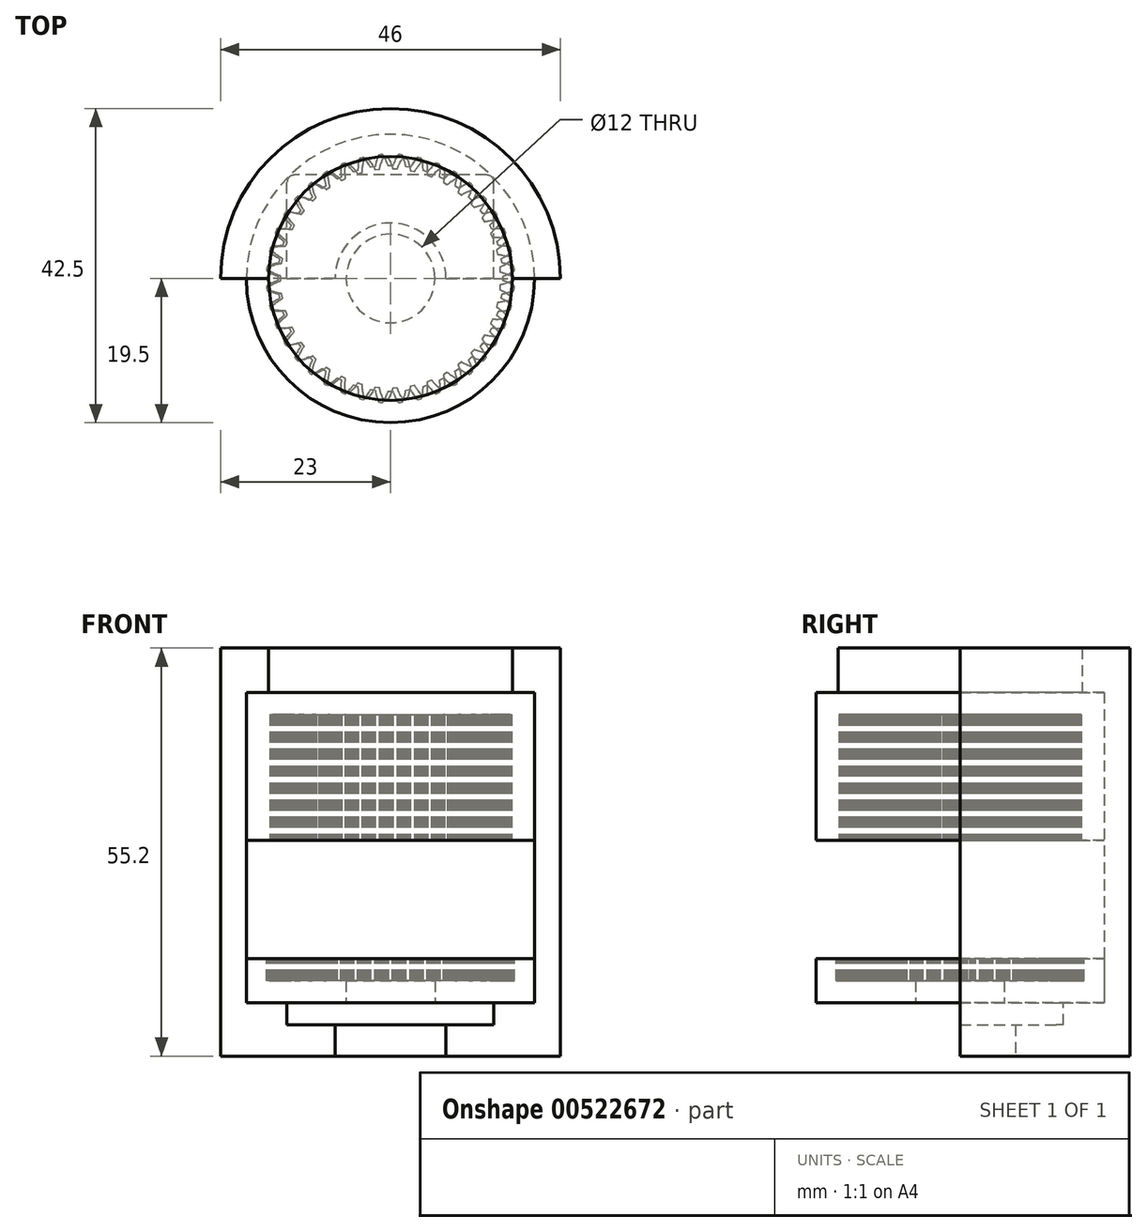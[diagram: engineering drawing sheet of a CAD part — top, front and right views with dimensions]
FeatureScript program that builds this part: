
annotation { "Feature Type Name" : "Feature", "Feature Type Description" : "" }
export const myFeature = defineFeature(function(context is Context, id is Id, definition is map)
    precondition{}
    {
        {
            var Q0;
            Q0=qCreatedBy(makeId("Top.planeOp"),FACE);
            var sketch = newSketch(context, id + "F0", { "sketchPlane" : qUnion([Q0])});
            skLineSegment(sketch, "E0", {"start": v(-16.75, 1.06) * mm, "end": v(-16.75, 1.32) * mm});
            skLineSegment(sketch, "E1", {"start": v(-16.75, 1.32) * mm, "end": v(-16.7, 1.58) * mm});
            skLineSegment(sketch, "E2", {"start": v(-16.7, 1.58) * mm, "end": v(-16.66, 1.63) * mm});
            skLineSegment(sketch, "E3", {"start": v(-16.66, 1.63) * mm, "end": v(-16.6, 1.66) * mm});
            skLineSegment(sketch, "E4", {"start": v(-16.6, 1.66) * mm, "end": v(-16.3, 1.78) * mm});
            skLineSegment(sketch, "E5", {"start": v(-16.3, 1.78) * mm, "end": v(-16.24, 1.8) * mm});
            skLineSegment(sketch, "E6", {"start": v(-16.24, 1.8) * mm, "end": v(-16.22, 1.8) * mm});
            skLineSegment(sketch, "E7", {"start": v(-16.22, 1.8) * mm, "end": v(-16.03, 1.87) * mm});
            skLineSegment(sketch, "E8", {"start": v(-16.03, 1.87) * mm, "end": v(-16.03, 1.87) * mm});
            skLineSegment(sketch, "E9", {"start": v(-16.03, 1.87) * mm, "end": v(-16, 1.87) * mm});
            skLineSegment(sketch, "E10", {"start": v(-16, 1.87) * mm, "end": v(-15.79, 1.94) * mm});
            skLineSegment(sketch, "E11", {"start": v(-15.79, 1.94) * mm, "end": v(-15.77, 1.94) * mm});
            skLineSegment(sketch, "E12", {"start": v(-15.77, 1.94) * mm, "end": v(-15.6, 1.99) * mm});
            skLineSegment(sketch, "E13", {"start": v(-15.6, 1.99) * mm, "end": v(-15.53, 2) * mm});
            skLineSegment(sketch, "E14", {"start": v(-15.53, 2) * mm, "end": v(-15.42, 2.02) * mm});
            skLineSegment(sketch, "E15", {"start": v(-15.42, 2.02) * mm, "end": v(-15.32, 2.04) * mm});
            skLineSegment(sketch, "E16", {"start": v(-15.32, 2.04) * mm, "end": v(-15.2, 2.06) * mm});
            skLineSegment(sketch, "E17", {"start": v(-15.2, 2.06) * mm, "end": v(-15.16, 2.07) * mm});
            skLineSegment(sketch, "E18", {"start": v(-15.16, 2.07) * mm, "end": v(-15.14, 2.08) * mm});
            skLineSegment(sketch, "E19", {"start": v(-15.14, 2.08) * mm, "end": v(-15.12, 2.1) * mm});
            skLineSegment(sketch, "E20", {"start": v(-15.12, 2.1) * mm, "end": v(-15.1, 2.1) * mm});
            skLineSegment(sketch, "E21", {"start": v(-15.1, 2.1) * mm, "end": v(-15.02, 2.66) * mm});
            skLineSegment(sketch, "E22", {"start": v(-15.02, 2.66) * mm, "end": v(-15.03, 2.68) * mm});
            skLineSegment(sketch, "E23", {"start": v(-15.03, 2.68) * mm, "end": v(-15.04, 2.7) * mm});
            skLineSegment(sketch, "E24", {"start": v(-15.04, 2.7) * mm, "end": v(-15.06, 2.71) * mm});
            skLineSegment(sketch, "E25", {"start": v(-15.06, 2.71) * mm, "end": v(-15.1, 2.74) * mm});
            skLineSegment(sketch, "E26", {"start": v(-15.1, 2.74) * mm, "end": v(-15.2, 2.8) * mm});
            skLineSegment(sketch, "E27", {"start": v(-15.2, 2.8) * mm, "end": v(-15.29, 2.84) * mm});
            skLineSegment(sketch, "E28", {"start": v(-15.29, 2.84) * mm, "end": v(-15.39, 2.9) * mm});
            skLineSegment(sketch, "E29", {"start": v(-15.39, 2.9) * mm, "end": v(-15.44, 2.93) * mm});
            skLineSegment(sketch, "E30", {"start": v(-15.44, 2.93) * mm, "end": v(-15.6, 3.03) * mm});
            skLineSegment(sketch, "E31", {"start": v(-15.6, 3.03) * mm, "end": v(-15.61, 3.04) * mm});
            skLineSegment(sketch, "E32", {"start": v(-15.61, 3.04) * mm, "end": v(-15.8, 3.16) * mm});
            skLineSegment(sketch, "E33", {"start": v(-15.8, 3.16) * mm, "end": v(-15.82, 3.18) * mm});
            skLineSegment(sketch, "E34", {"start": v(-15.82, 3.18) * mm, "end": v(-15.82, 3.18) * mm});
            skLineSegment(sketch, "E35", {"start": v(-15.82, 3.18) * mm, "end": v(-15.98, 3.3) * mm});
            skLineSegment(sketch, "E36", {"start": v(-15.98, 3.3) * mm, "end": v(-16, 3.3) * mm});
            skLineSegment(sketch, "E37", {"start": v(-16, 3.3) * mm, "end": v(-16.05, 3.35) * mm});
            skLineSegment(sketch, "E38", {"start": v(-16.05, 3.35) * mm, "end": v(-16.3, 3.54) * mm});
            skLineSegment(sketch, "E39", {"start": v(-16.3, 3.54) * mm, "end": v(-16.35, 3.6) * mm});
            skLineSegment(sketch, "E40", {"start": v(-16.35, 3.6) * mm, "end": v(-16.38, 3.66) * mm});
            skLineSegment(sketch, "E41", {"start": v(-16.38, 3.66) * mm, "end": v(-16.34, 3.92) * mm});
            skLineSegment(sketch, "E42", {"start": v(-16.34, 3.92) * mm, "end": v(-16.26, 4.17) * mm});
            skLineSegment(sketch, "E43", {"start": v(-16.26, 4.17) * mm, "end": v(-16.2, 4.22) * mm});
            skLineSegment(sketch, "E44", {"start": v(-16.2, 4.22) * mm, "end": v(-16.13, 4.24) * mm});
            skLineSegment(sketch, "E45", {"start": v(-16.13, 4.24) * mm, "end": v(-15.82, 4.3) * mm});
            skLineSegment(sketch, "E46", {"start": v(-15.82, 4.3) * mm, "end": v(-15.76, 4.32) * mm});
            skLineSegment(sketch, "E47", {"start": v(-15.76, 4.32) * mm, "end": v(-15.74, 4.32) * mm});
            skLineSegment(sketch, "E48", {"start": v(-15.74, 4.32) * mm, "end": v(-15.54, 4.35) * mm});
            skLineSegment(sketch, "E49", {"start": v(-15.54, 4.35) * mm, "end": v(-15.54, 4.35) * mm});
            skLineSegment(sketch, "E50", {"start": v(-15.54, 4.35) * mm, "end": v(-15.51, 4.36) * mm});
            skLineSegment(sketch, "E51", {"start": v(-15.51, 4.36) * mm, "end": v(-15.3, 4.38) * mm});
            skLineSegment(sketch, "E52", {"start": v(-15.3, 4.38) * mm, "end": v(-15.27, 4.38) * mm});
            skLineSegment(sketch, "E53", {"start": v(-15.27, 4.38) * mm, "end": v(-15.09, 4.4) * mm});
            skLineSegment(sketch, "E54", {"start": v(-15.09, 4.4) * mm, "end": v(-15.03, 4.4) * mm});
            skLineSegment(sketch, "E55", {"start": v(-15.03, 4.4) * mm, "end": v(-14.91, 4.4) * mm});
            skLineSegment(sketch, "E56", {"start": v(-14.91, 4.4) * mm, "end": v(-14.8, 4.41) * mm});
            skLineSegment(sketch, "E57", {"start": v(-14.8, 4.41) * mm, "end": v(-14.7, 4.41) * mm});
            skLineSegment(sketch, "E58", {"start": v(-14.7, 4.41) * mm, "end": v(-14.65, 4.42) * mm});
            skLineSegment(sketch, "E59", {"start": v(-14.65, 4.42) * mm, "end": v(-14.62, 4.43) * mm});
            skLineSegment(sketch, "E60", {"start": v(-14.62, 4.43) * mm, "end": v(-14.6, 4.43) * mm});
            skLineSegment(sketch, "E61", {"start": v(-14.6, 4.43) * mm, "end": v(-14.6, 4.44) * mm});
            skLineSegment(sketch, "E62", {"start": v(-14.6, 4.44) * mm, "end": v(-14.42, 4.98) * mm});
            skLineSegment(sketch, "E63", {"start": v(-14.42, 4.98) * mm, "end": v(-14.42, 5) * mm});
            skLineSegment(sketch, "E64", {"start": v(-14.42, 5) * mm, "end": v(-14.43, 5.02) * mm});
            skLineSegment(sketch, "E65", {"start": v(-14.43, 5.02) * mm, "end": v(-14.45, 5.04) * mm});
            skLineSegment(sketch, "E66", {"start": v(-14.45, 5.04) * mm, "end": v(-14.48, 5.07) * mm});
            skLineSegment(sketch, "E67", {"start": v(-14.48, 5.07) * mm, "end": v(-14.57, 5.13) * mm});
            skLineSegment(sketch, "E68", {"start": v(-14.57, 5.13) * mm, "end": v(-14.65, 5.2) * mm});
            skLineSegment(sketch, "E69", {"start": v(-14.65, 5.2) * mm, "end": v(-14.75, 5.27) * mm});
            skLineSegment(sketch, "E70", {"start": v(-14.75, 5.27) * mm, "end": v(-14.8, 5.3) * mm});
            skLineSegment(sketch, "E71", {"start": v(-14.8, 5.3) * mm, "end": v(-14.93, 5.43) * mm});
            skLineSegment(sketch, "E72", {"start": v(-14.93, 5.43) * mm, "end": v(-14.95, 5.44) * mm});
            skLineSegment(sketch, "E73", {"start": v(-14.95, 5.44) * mm, "end": v(-15.11, 5.6) * mm});
            skLineSegment(sketch, "E74", {"start": v(-15.11, 5.6) * mm, "end": v(-15.13, 5.61) * mm});
            skLineSegment(sketch, "E75", {"start": v(-15.13, 5.61) * mm, "end": v(-15.13, 5.61) * mm});
            skLineSegment(sketch, "E76", {"start": v(-15.13, 5.61) * mm, "end": v(-15.27, 5.76) * mm});
            skLineSegment(sketch, "E77", {"start": v(-15.27, 5.76) * mm, "end": v(-15.29, 5.77) * mm});
            skLineSegment(sketch, "E78", {"start": v(-15.29, 5.77) * mm, "end": v(-15.33, 5.82) * mm});
            skLineSegment(sketch, "E79", {"start": v(-15.33, 5.82) * mm, "end": v(-15.54, 6.05) * mm});
            skLineSegment(sketch, "E80", {"start": v(-15.54, 6.05) * mm, "end": v(-15.58, 6.11) * mm});
            skLineSegment(sketch, "E81", {"start": v(-15.58, 6.11) * mm, "end": v(-15.6, 6.18) * mm});
            skLineSegment(sketch, "E82", {"start": v(-15.6, 6.18) * mm, "end": v(-15.52, 6.43) * mm});
            skLineSegment(sketch, "E83", {"start": v(-15.52, 6.43) * mm, "end": v(-15.4, 6.66) * mm});
            skLineSegment(sketch, "E84", {"start": v(-15.4, 6.66) * mm, "end": v(-15.34, 6.7) * mm});
            skLineSegment(sketch, "E85", {"start": v(-15.34, 6.7) * mm, "end": v(-15.27, 6.71) * mm});
            skLineSegment(sketch, "E86", {"start": v(-15.27, 6.71) * mm, "end": v(-14.95, 6.73) * mm});
            skLineSegment(sketch, "E87", {"start": v(-14.95, 6.73) * mm, "end": v(-14.89, 6.73) * mm});
            skLineSegment(sketch, "E88", {"start": v(-14.89, 6.73) * mm, "end": v(-14.87, 6.73) * mm});
            skLineSegment(sketch, "E89", {"start": v(-14.87, 6.73) * mm, "end": v(-14.67, 6.73) * mm});
            skLineSegment(sketch, "E90", {"start": v(-14.67, 6.73) * mm, "end": v(-14.66, 6.73) * mm});
            skLineSegment(sketch, "E91", {"start": v(-14.66, 6.73) * mm, "end": v(-14.64, 6.73) * mm});
            skLineSegment(sketch, "E92", {"start": v(-14.64, 6.73) * mm, "end": v(-14.42, 6.72) * mm});
            skLineSegment(sketch, "E93", {"start": v(-14.42, 6.72) * mm, "end": v(-14.4, 6.72) * mm});
            skLineSegment(sketch, "E94", {"start": v(-14.4, 6.72) * mm, "end": v(-14.22, 6.7) * mm});
            skLineSegment(sketch, "E95", {"start": v(-14.22, 6.7) * mm, "end": v(-14.15, 6.7) * mm});
            skLineSegment(sketch, "E96", {"start": v(-14.15, 6.7) * mm, "end": v(-14.04, 6.69) * mm});
            skLineSegment(sketch, "E97", {"start": v(-14.04, 6.69) * mm, "end": v(-13.93, 6.67) * mm});
            skLineSegment(sketch, "E98", {"start": v(-13.93, 6.67) * mm, "end": v(-13.83, 6.66) * mm});
            skLineSegment(sketch, "E99", {"start": v(-13.83, 6.66) * mm, "end": v(-13.78, 6.66) * mm});
            skLineSegment(sketch, "E100", {"start": v(-13.78, 6.66) * mm, "end": v(-13.75, 6.66) * mm});
            skLineSegment(sketch, "E101", {"start": v(-13.75, 6.66) * mm, "end": v(-13.73, 6.66) * mm});
            skLineSegment(sketch, "E102", {"start": v(-13.73, 6.66) * mm, "end": v(-13.72, 6.67) * mm});
            skLineSegment(sketch, "E103", {"start": v(-13.72, 6.67) * mm, "end": v(-13.46, 7.17) * mm});
            skLineSegment(sketch, "E104", {"start": v(-13.46, 7.17) * mm, "end": v(-13.46, 7.2) * mm});
            skLineSegment(sketch, "E105", {"start": v(-13.46, 7.2) * mm, "end": v(-13.47, 7.21) * mm});
            skLineSegment(sketch, "E106", {"start": v(-13.47, 7.21) * mm, "end": v(-13.48, 7.23) * mm});
            skLineSegment(sketch, "E107", {"start": v(-13.48, 7.23) * mm, "end": v(-13.51, 7.27) * mm});
            skLineSegment(sketch, "E108", {"start": v(-13.51, 7.27) * mm, "end": v(-13.6, 7.35) * mm});
            skLineSegment(sketch, "E109", {"start": v(-13.6, 7.35) * mm, "end": v(-13.66, 7.43) * mm});
            skLineSegment(sketch, "E110", {"start": v(-13.66, 7.43) * mm, "end": v(-13.74, 7.51) * mm});
            skLineSegment(sketch, "E111", {"start": v(-13.74, 7.51) * mm, "end": v(-13.78, 7.56) * mm});
            skLineSegment(sketch, "E112", {"start": v(-13.78, 7.56) * mm, "end": v(-13.9, 7.7) * mm});
            skLineSegment(sketch, "E113", {"start": v(-13.9, 7.7) * mm, "end": v(-13.91, 7.71) * mm});
            skLineSegment(sketch, "E114", {"start": v(-13.91, 7.71) * mm, "end": v(-14.05, 7.89) * mm});
            skLineSegment(sketch, "E115", {"start": v(-14.05, 7.89) * mm, "end": v(-14.06, 7.9) * mm});
            skLineSegment(sketch, "E116", {"start": v(-14.06, 7.9) * mm, "end": v(-14.07, 7.91) * mm});
            skLineSegment(sketch, "E117", {"start": v(-14.07, 7.91) * mm, "end": v(-14.18, 8.08) * mm});
            skLineSegment(sketch, "E118", {"start": v(-14.18, 8.08) * mm, "end": v(-14.2, 8.1) * mm});
            skLineSegment(sketch, "E119", {"start": v(-14.2, 8.1) * mm, "end": v(-14.23, 8.14) * mm});
            skLineSegment(sketch, "E120", {"start": v(-14.23, 8.14) * mm, "end": v(-14.4, 8.4) * mm});
            skLineSegment(sketch, "E121", {"start": v(-14.4, 8.4) * mm, "end": v(-14.44, 8.47) * mm});
            skLineSegment(sketch, "E122", {"start": v(-14.44, 8.47) * mm, "end": v(-14.44, 8.54) * mm});
            skLineSegment(sketch, "E123", {"start": v(-14.44, 8.54) * mm, "end": v(-14.32, 8.78) * mm});
            skLineSegment(sketch, "E124", {"start": v(-14.32, 8.78) * mm, "end": v(-14.17, 9) * mm});
            skLineSegment(sketch, "E125", {"start": v(-14.17, 9) * mm, "end": v(-14.1, 9.02) * mm});
            skLineSegment(sketch, "E126", {"start": v(-14.1, 9.02) * mm, "end": v(-14.03, 9.02) * mm});
            skLineSegment(sketch, "E127", {"start": v(-14.03, 9.02) * mm, "end": v(-13.72, 8.98) * mm});
            skLineSegment(sketch, "E128", {"start": v(-13.72, 8.98) * mm, "end": v(-13.65, 8.97) * mm});
            skLineSegment(sketch, "E129", {"start": v(-13.65, 8.97) * mm, "end": v(-13.63, 8.97) * mm});
            skLineSegment(sketch, "E130", {"start": v(-13.63, 8.97) * mm, "end": v(-13.44, 8.94) * mm});
            skLineSegment(sketch, "E131", {"start": v(-13.44, 8.94) * mm, "end": v(-13.43, 8.94) * mm});
            skLineSegment(sketch, "E132", {"start": v(-13.43, 8.94) * mm, "end": v(-13.4, 8.94) * mm});
            skLineSegment(sketch, "E133", {"start": v(-13.4, 8.94) * mm, "end": v(-13.19, 8.9) * mm});
            skLineSegment(sketch, "E134", {"start": v(-13.19, 8.9) * mm, "end": v(-13.17, 8.89) * mm});
            skLineSegment(sketch, "E135", {"start": v(-13.17, 8.89) * mm, "end": v(-13, 8.85) * mm});
            skLineSegment(sketch, "E136", {"start": v(-13, 8.85) * mm, "end": v(-12.93, 8.83) * mm});
            skLineSegment(sketch, "E137", {"start": v(-12.93, 8.83) * mm, "end": v(-12.82, 8.8) * mm});
            skLineSegment(sketch, "E138", {"start": v(-12.82, 8.8) * mm, "end": v(-12.72, 8.77) * mm});
            skLineSegment(sketch, "E139", {"start": v(-12.72, 8.77) * mm, "end": v(-12.61, 8.74) * mm});
            skLineSegment(sketch, "E140", {"start": v(-12.61, 8.74) * mm, "end": v(-12.57, 8.73) * mm});
            skLineSegment(sketch, "E141", {"start": v(-12.57, 8.73) * mm, "end": v(-12.54, 8.73) * mm});
            skLineSegment(sketch, "E142", {"start": v(-12.54, 8.73) * mm, "end": v(-12.52, 8.73) * mm});
            skLineSegment(sketch, "E143", {"start": v(-12.52, 8.73) * mm, "end": v(-12.5, 8.74) * mm});
            skLineSegment(sketch, "E144", {"start": v(-12.5, 8.74) * mm, "end": v(-12.17, 9.2) * mm});
            skLineSegment(sketch, "E145", {"start": v(-12.17, 9.2) * mm, "end": v(-12.17, 9.21) * mm});
            skLineSegment(sketch, "E146", {"start": v(-12.17, 9.21) * mm, "end": v(-12.18, 9.23) * mm});
            skLineSegment(sketch, "E147", {"start": v(-12.18, 9.23) * mm, "end": v(-12.19, 9.25) * mm});
            skLineSegment(sketch, "E148", {"start": v(-12.19, 9.25) * mm, "end": v(-12.2, 9.3) * mm});
            skLineSegment(sketch, "E149", {"start": v(-12.2, 9.3) * mm, "end": v(-12.27, 9.39) * mm});
            skLineSegment(sketch, "E150", {"start": v(-12.27, 9.39) * mm, "end": v(-12.33, 9.47) * mm});
            skLineSegment(sketch, "E151", {"start": v(-12.33, 9.47) * mm, "end": v(-12.4, 9.57) * mm});
            skLineSegment(sketch, "E152", {"start": v(-12.4, 9.57) * mm, "end": v(-12.43, 9.62) * mm});
            skLineSegment(sketch, "E153", {"start": v(-12.43, 9.62) * mm, "end": v(-12.52, 9.78) * mm});
            skLineSegment(sketch, "E154", {"start": v(-12.52, 9.78) * mm, "end": v(-12.53, 9.8) * mm});
            skLineSegment(sketch, "E155", {"start": v(-12.53, 9.8) * mm, "end": v(-12.64, 10) * mm});
            skLineSegment(sketch, "E156", {"start": v(-12.64, 10) * mm, "end": v(-12.65, 10.01) * mm});
            skLineSegment(sketch, "E157", {"start": v(-12.65, 10.01) * mm, "end": v(-12.65, 10.02) * mm});
            skLineSegment(sketch, "E158", {"start": v(-12.65, 10.02) * mm, "end": v(-12.74, 10.2) * mm});
            skLineSegment(sketch, "E159", {"start": v(-12.74, 10.2) * mm, "end": v(-12.75, 10.21) * mm});
            skLineSegment(sketch, "E160", {"start": v(-12.75, 10.21) * mm, "end": v(-12.78, 10.27) * mm});
            skLineSegment(sketch, "E161", {"start": v(-12.78, 10.27) * mm, "end": v(-12.9, 10.56) * mm});
            skLineSegment(sketch, "E162", {"start": v(-12.9, 10.56) * mm, "end": v(-12.93, 10.63) * mm});
            skLineSegment(sketch, "E163", {"start": v(-12.93, 10.63) * mm, "end": v(-12.93, 10.7) * mm});
            skLineSegment(sketch, "E164", {"start": v(-12.93, 10.7) * mm, "end": v(-12.77, 10.91) * mm});
            skLineSegment(sketch, "E165", {"start": v(-12.77, 10.91) * mm, "end": v(-12.59, 11.1) * mm});
            skLineSegment(sketch, "E166", {"start": v(-12.59, 11.1) * mm, "end": v(-12.52, 11.11) * mm});
            skLineSegment(sketch, "E167", {"start": v(-12.52, 11.11) * mm, "end": v(-12.44, 11.1) * mm});
            skLineSegment(sketch, "E168", {"start": v(-12.44, 11.1) * mm, "end": v(-12.14, 11.02) * mm});
            skLineSegment(sketch, "E169", {"start": v(-12.14, 11.02) * mm, "end": v(-12.08, 11) * mm});
            skLineSegment(sketch, "E170", {"start": v(-12.08, 11) * mm, "end": v(-12.06, 11) * mm});
            skLineSegment(sketch, "E171", {"start": v(-12.06, 11) * mm, "end": v(-11.87, 10.93) * mm});
            skLineSegment(sketch, "E172", {"start": v(-11.87, 10.93) * mm, "end": v(-11.87, 10.93) * mm});
            skLineSegment(sketch, "E173", {"start": v(-11.87, 10.93) * mm, "end": v(-11.85, 10.92) * mm});
            skLineSegment(sketch, "E174", {"start": v(-11.85, 10.92) * mm, "end": v(-11.63, 10.85) * mm});
            skLineSegment(sketch, "E175", {"start": v(-11.63, 10.85) * mm, "end": v(-11.62, 10.84) * mm});
            skLineSegment(sketch, "E176", {"start": v(-11.62, 10.84) * mm, "end": v(-11.45, 10.77) * mm});
            skLineSegment(sketch, "E177", {"start": v(-11.45, 10.77) * mm, "end": v(-11.4, 10.75) * mm});
            skLineSegment(sketch, "E178", {"start": v(-11.4, 10.75) * mm, "end": v(-11.28, 10.7) * mm});
            skLineSegment(sketch, "E179", {"start": v(-11.28, 10.7) * mm, "end": v(-11.2, 10.65) * mm});
            skLineSegment(sketch, "E180", {"start": v(-11.2, 10.65) * mm, "end": v(-11.1, 10.6) * mm});
            skLineSegment(sketch, "E181", {"start": v(-11.1, 10.6) * mm, "end": v(-11.05, 10.59) * mm});
            skLineSegment(sketch, "E182", {"start": v(-11.05, 10.59) * mm, "end": v(-11.02, 10.58) * mm});
            skLineSegment(sketch, "E183", {"start": v(-11.02, 10.58) * mm, "end": v(-11, 10.58) * mm});
            skLineSegment(sketch, "E184", {"start": v(-11, 10.58) * mm, "end": v(-10.98, 10.58) * mm});
            skLineSegment(sketch, "E185", {"start": v(-10.98, 10.58) * mm, "end": v(-10.58, 10.98) * mm});
            skLineSegment(sketch, "E186", {"start": v(-10.58, 10.98) * mm, "end": v(-10.58, 11) * mm});
            skLineSegment(sketch, "E187", {"start": v(-10.58, 11) * mm, "end": v(-10.58, 11.02) * mm});
            skLineSegment(sketch, "E188", {"start": v(-10.58, 11.02) * mm, "end": v(-10.59, 11.05) * mm});
            skLineSegment(sketch, "E189", {"start": v(-10.59, 11.05) * mm, "end": v(-10.6, 11.1) * mm});
            skLineSegment(sketch, "E190", {"start": v(-10.6, 11.1) * mm, "end": v(-10.65, 11.2) * mm});
            skLineSegment(sketch, "E191", {"start": v(-10.65, 11.2) * mm, "end": v(-10.7, 11.28) * mm});
            skLineSegment(sketch, "E192", {"start": v(-10.7, 11.28) * mm, "end": v(-10.75, 11.4) * mm});
            skLineSegment(sketch, "E193", {"start": v(-10.75, 11.4) * mm, "end": v(-10.77, 11.45) * mm});
            skLineSegment(sketch, "E194", {"start": v(-10.77, 11.45) * mm, "end": v(-10.84, 11.62) * mm});
            skLineSegment(sketch, "E195", {"start": v(-10.84, 11.62) * mm, "end": v(-10.85, 11.63) * mm});
            skLineSegment(sketch, "E196", {"start": v(-10.85, 11.63) * mm, "end": v(-10.92, 11.85) * mm});
            skLineSegment(sketch, "E197", {"start": v(-10.92, 11.85) * mm, "end": v(-10.93, 11.87) * mm});
            skLineSegment(sketch, "E198", {"start": v(-10.93, 11.87) * mm, "end": v(-10.93, 11.87) * mm});
            skLineSegment(sketch, "E199", {"start": v(-10.93, 11.87) * mm, "end": v(-11, 12.06) * mm});
            skLineSegment(sketch, "E200", {"start": v(-11, 12.06) * mm, "end": v(-11, 12.08) * mm});
            skLineSegment(sketch, "E201", {"start": v(-11, 12.08) * mm, "end": v(-11.02, 12.14) * mm});
            skLineSegment(sketch, "E202", {"start": v(-11.02, 12.14) * mm, "end": v(-11.1, 12.44) * mm});
            skLineSegment(sketch, "E203", {"start": v(-11.1, 12.44) * mm, "end": v(-11.11, 12.52) * mm});
            skLineSegment(sketch, "E204", {"start": v(-11.11, 12.52) * mm, "end": v(-11.1, 12.59) * mm});
            skLineSegment(sketch, "E205", {"start": v(-11.1, 12.59) * mm, "end": v(-10.91, 12.77) * mm});
            skLineSegment(sketch, "E206", {"start": v(-10.91, 12.77) * mm, "end": v(-10.7, 12.93) * mm});
            skLineSegment(sketch, "E207", {"start": v(-10.7, 12.93) * mm, "end": v(-10.63, 12.93) * mm});
            skLineSegment(sketch, "E208", {"start": v(-10.63, 12.93) * mm, "end": v(-10.56, 12.9) * mm});
            skLineSegment(sketch, "E209", {"start": v(-10.56, 12.9) * mm, "end": v(-10.27, 12.78) * mm});
            skLineSegment(sketch, "E210", {"start": v(-10.27, 12.78) * mm, "end": v(-10.21, 12.75) * mm});
            skLineSegment(sketch, "E211", {"start": v(-10.21, 12.75) * mm, "end": v(-10.2, 12.74) * mm});
            skLineSegment(sketch, "E212", {"start": v(-10.2, 12.74) * mm, "end": v(-10.02, 12.65) * mm});
            skLineSegment(sketch, "E213", {"start": v(-10.02, 12.65) * mm, "end": v(-10.01, 12.65) * mm});
            skLineSegment(sketch, "E214", {"start": v(-10.01, 12.65) * mm, "end": v(-10, 12.64) * mm});
            skLineSegment(sketch, "E215", {"start": v(-10, 12.64) * mm, "end": v(-9.8, 12.53) * mm});
            skLineSegment(sketch, "E216", {"start": v(-9.8, 12.53) * mm, "end": v(-9.78, 12.52) * mm});
            skLineSegment(sketch, "E217", {"start": v(-9.78, 12.52) * mm, "end": v(-9.62, 12.43) * mm});
            skLineSegment(sketch, "E218", {"start": v(-9.62, 12.43) * mm, "end": v(-9.57, 12.4) * mm});
            skLineSegment(sketch, "E219", {"start": v(-9.57, 12.4) * mm, "end": v(-9.47, 12.33) * mm});
            skLineSegment(sketch, "E220", {"start": v(-9.47, 12.33) * mm, "end": v(-9.39, 12.27) * mm});
            skLineSegment(sketch, "E221", {"start": v(-9.39, 12.27) * mm, "end": v(-9.3, 12.2) * mm});
            skLineSegment(sketch, "E222", {"start": v(-9.3, 12.2) * mm, "end": v(-9.25, 12.19) * mm});
            skLineSegment(sketch, "E223", {"start": v(-9.25, 12.19) * mm, "end": v(-9.23, 12.18) * mm});
            skLineSegment(sketch, "E224", {"start": v(-9.23, 12.18) * mm, "end": v(-9.21, 12.17) * mm});
            skLineSegment(sketch, "E225", {"start": v(-9.21, 12.17) * mm, "end": v(-9.2, 12.17) * mm});
            skLineSegment(sketch, "E226", {"start": v(-9.2, 12.17) * mm, "end": v(-8.74, 12.5) * mm});
            skLineSegment(sketch, "E227", {"start": v(-8.74, 12.5) * mm, "end": v(-8.73, 12.52) * mm});
            skLineSegment(sketch, "E228", {"start": v(-8.73, 12.52) * mm, "end": v(-8.73, 12.54) * mm});
            skLineSegment(sketch, "E229", {"start": v(-8.73, 12.54) * mm, "end": v(-8.73, 12.57) * mm});
            skLineSegment(sketch, "E230", {"start": v(-8.73, 12.57) * mm, "end": v(-8.74, 12.61) * mm});
            skLineSegment(sketch, "E231", {"start": v(-8.74, 12.61) * mm, "end": v(-8.77, 12.72) * mm});
            skLineSegment(sketch, "E232", {"start": v(-8.77, 12.72) * mm, "end": v(-8.8, 12.82) * mm});
            skLineSegment(sketch, "E233", {"start": v(-8.8, 12.82) * mm, "end": v(-8.83, 12.93) * mm});
            skLineSegment(sketch, "E234", {"start": v(-8.83, 12.93) * mm, "end": v(-8.85, 13) * mm});
            skLineSegment(sketch, "E235", {"start": v(-8.85, 13) * mm, "end": v(-8.89, 13.17) * mm});
            skLineSegment(sketch, "E236", {"start": v(-8.89, 13.17) * mm, "end": v(-8.9, 13.19) * mm});
            skLineSegment(sketch, "E237", {"start": v(-8.9, 13.19) * mm, "end": v(-8.94, 13.4) * mm});
            skLineSegment(sketch, "E238", {"start": v(-8.94, 13.4) * mm, "end": v(-8.94, 13.43) * mm});
            skLineSegment(sketch, "E239", {"start": v(-8.94, 13.43) * mm, "end": v(-8.94, 13.44) * mm});
            skLineSegment(sketch, "E240", {"start": v(-8.94, 13.44) * mm, "end": v(-8.97, 13.63) * mm});
            skLineSegment(sketch, "E241", {"start": v(-8.97, 13.63) * mm, "end": v(-8.97, 13.65) * mm});
            skLineSegment(sketch, "E242", {"start": v(-8.97, 13.65) * mm, "end": v(-8.98, 13.72) * mm});
            skLineSegment(sketch, "E243", {"start": v(-8.98, 13.72) * mm, "end": v(-9.02, 14.03) * mm});
            skLineSegment(sketch, "E244", {"start": v(-9.02, 14.03) * mm, "end": v(-9.02, 14.1) * mm});
            skLineSegment(sketch, "E245", {"start": v(-9.02, 14.1) * mm, "end": v(-9, 14.17) * mm});
            skLineSegment(sketch, "E246", {"start": v(-9, 14.17) * mm, "end": v(-8.78, 14.32) * mm});
            skLineSegment(sketch, "E247", {"start": v(-8.78, 14.32) * mm, "end": v(-8.54, 14.44) * mm});
            skLineSegment(sketch, "E248", {"start": v(-8.54, 14.44) * mm, "end": v(-8.47, 14.44) * mm});
            skLineSegment(sketch, "E249", {"start": v(-8.47, 14.44) * mm, "end": v(-8.4, 14.4) * mm});
            skLineSegment(sketch, "E250", {"start": v(-8.4, 14.4) * mm, "end": v(-8.14, 14.23) * mm});
            skLineSegment(sketch, "E251", {"start": v(-8.14, 14.23) * mm, "end": v(-8.1, 14.2) * mm});
            skLineSegment(sketch, "E252", {"start": v(-8.1, 14.2) * mm, "end": v(-8.08, 14.18) * mm});
            skLineSegment(sketch, "E253", {"start": v(-8.08, 14.18) * mm, "end": v(-7.91, 14.07) * mm});
            skLineSegment(sketch, "E254", {"start": v(-7.91, 14.07) * mm, "end": v(-7.9, 14.06) * mm});
            skLineSegment(sketch, "E255", {"start": v(-7.9, 14.06) * mm, "end": v(-7.89, 14.05) * mm});
            skLineSegment(sketch, "E256", {"start": v(-7.89, 14.05) * mm, "end": v(-7.71, 13.91) * mm});
            skLineSegment(sketch, "E257", {"start": v(-7.71, 13.91) * mm, "end": v(-7.7, 13.9) * mm});
            skLineSegment(sketch, "E258", {"start": v(-7.7, 13.9) * mm, "end": v(-7.56, 13.78) * mm});
            skLineSegment(sketch, "E259", {"start": v(-7.56, 13.78) * mm, "end": v(-7.51, 13.74) * mm});
            skLineSegment(sketch, "E260", {"start": v(-7.51, 13.74) * mm, "end": v(-7.43, 13.66) * mm});
            skLineSegment(sketch, "E261", {"start": v(-7.43, 13.66) * mm, "end": v(-7.35, 13.6) * mm});
            skLineSegment(sketch, "E262", {"start": v(-7.35, 13.6) * mm, "end": v(-7.27, 13.51) * mm});
            skLineSegment(sketch, "E263", {"start": v(-7.27, 13.51) * mm, "end": v(-7.23, 13.48) * mm});
            skLineSegment(sketch, "E264", {"start": v(-7.23, 13.48) * mm, "end": v(-7.21, 13.47) * mm});
            skLineSegment(sketch, "E265", {"start": v(-7.21, 13.47) * mm, "end": v(-7.2, 13.46) * mm});
            skLineSegment(sketch, "E266", {"start": v(-7.2, 13.46) * mm, "end": v(-7.17, 13.46) * mm});
            skLineSegment(sketch, "E267", {"start": v(-7.17, 13.46) * mm, "end": v(-6.67, 13.72) * mm});
            skLineSegment(sketch, "E268", {"start": v(-6.67, 13.72) * mm, "end": v(-6.66, 13.73) * mm});
            skLineSegment(sketch, "E269", {"start": v(-6.66, 13.73) * mm, "end": v(-6.66, 13.75) * mm});
            skLineSegment(sketch, "E270", {"start": v(-6.66, 13.75) * mm, "end": v(-6.66, 13.78) * mm});
            skLineSegment(sketch, "E271", {"start": v(-6.66, 13.78) * mm, "end": v(-6.66, 13.83) * mm});
            skLineSegment(sketch, "E272", {"start": v(-6.66, 13.83) * mm, "end": v(-6.67, 13.93) * mm});
            skLineSegment(sketch, "E273", {"start": v(-6.67, 13.93) * mm, "end": v(-6.69, 14.04) * mm});
            skLineSegment(sketch, "E274", {"start": v(-6.69, 14.04) * mm, "end": v(-6.7, 14.15) * mm});
            skLineSegment(sketch, "E275", {"start": v(-6.7, 14.15) * mm, "end": v(-6.7, 14.22) * mm});
            skLineSegment(sketch, "E276", {"start": v(-6.7, 14.22) * mm, "end": v(-6.72, 14.4) * mm});
            skLineSegment(sketch, "E277", {"start": v(-6.72, 14.4) * mm, "end": v(-6.72, 14.42) * mm});
            skLineSegment(sketch, "E278", {"start": v(-6.72, 14.42) * mm, "end": v(-6.73, 14.64) * mm});
            skLineSegment(sketch, "E279", {"start": v(-6.73, 14.64) * mm, "end": v(-6.73, 14.66) * mm});
            skLineSegment(sketch, "E280", {"start": v(-6.73, 14.66) * mm, "end": v(-6.73, 14.67) * mm});
            skLineSegment(sketch, "E281", {"start": v(-6.73, 14.67) * mm, "end": v(-6.73, 14.87) * mm});
            skLineSegment(sketch, "E282", {"start": v(-6.73, 14.87) * mm, "end": v(-6.73, 14.89) * mm});
            skLineSegment(sketch, "E283", {"start": v(-6.73, 14.89) * mm, "end": v(-6.73, 14.95) * mm});
            skLineSegment(sketch, "E284", {"start": v(-6.73, 14.95) * mm, "end": v(-6.71, 15.27) * mm});
            skLineSegment(sketch, "E285", {"start": v(-6.71, 15.27) * mm, "end": v(-6.7, 15.34) * mm});
            skLineSegment(sketch, "E286", {"start": v(-6.7, 15.34) * mm, "end": v(-6.66, 15.4) * mm});
            skLineSegment(sketch, "E287", {"start": v(-6.66, 15.4) * mm, "end": v(-6.43, 15.52) * mm});
            skLineSegment(sketch, "E288", {"start": v(-6.43, 15.52) * mm, "end": v(-6.18, 15.6) * mm});
            skLineSegment(sketch, "E289", {"start": v(-6.18, 15.6) * mm, "end": v(-6.11, 15.58) * mm});
            skLineSegment(sketch, "E290", {"start": v(-6.11, 15.58) * mm, "end": v(-6.05, 15.54) * mm});
            skLineSegment(sketch, "E291", {"start": v(-6.05, 15.54) * mm, "end": v(-5.82, 15.33) * mm});
            skLineSegment(sketch, "E292", {"start": v(-5.82, 15.33) * mm, "end": v(-5.77, 15.29) * mm});
            skLineSegment(sketch, "E293", {"start": v(-5.77, 15.29) * mm, "end": v(-5.76, 15.27) * mm});
            skLineSegment(sketch, "E294", {"start": v(-5.76, 15.27) * mm, "end": v(-5.61, 15.13) * mm});
            skLineSegment(sketch, "E295", {"start": v(-5.61, 15.13) * mm, "end": v(-5.61, 15.13) * mm});
            skLineSegment(sketch, "E296", {"start": v(-5.61, 15.13) * mm, "end": v(-5.6, 15.11) * mm});
            skLineSegment(sketch, "E297", {"start": v(-5.6, 15.11) * mm, "end": v(-5.44, 14.95) * mm});
            skLineSegment(sketch, "E298", {"start": v(-5.44, 14.95) * mm, "end": v(-5.43, 14.93) * mm});
            skLineSegment(sketch, "E299", {"start": v(-5.43, 14.93) * mm, "end": v(-5.3, 14.8) * mm});
            skLineSegment(sketch, "E300", {"start": v(-5.3, 14.8) * mm, "end": v(-5.27, 14.75) * mm});
            skLineSegment(sketch, "E301", {"start": v(-5.27, 14.75) * mm, "end": v(-5.2, 14.65) * mm});
            skLineSegment(sketch, "E302", {"start": v(-5.2, 14.65) * mm, "end": v(-5.13, 14.57) * mm});
            skLineSegment(sketch, "E303", {"start": v(-5.13, 14.57) * mm, "end": v(-5.07, 14.48) * mm});
            skLineSegment(sketch, "E304", {"start": v(-5.07, 14.48) * mm, "end": v(-5.04, 14.45) * mm});
            skLineSegment(sketch, "E305", {"start": v(-5.04, 14.45) * mm, "end": v(-5.02, 14.43) * mm});
            skLineSegment(sketch, "E306", {"start": v(-5.02, 14.43) * mm, "end": v(-5, 14.42) * mm});
            skLineSegment(sketch, "E307", {"start": v(-5, 14.42) * mm, "end": v(-4.98, 14.42) * mm});
            skLineSegment(sketch, "E308", {"start": v(-4.98, 14.42) * mm, "end": v(-4.44, 14.6) * mm});
            skLineSegment(sketch, "E309", {"start": v(-4.44, 14.6) * mm, "end": v(-4.43, 14.6) * mm});
            skLineSegment(sketch, "E310", {"start": v(-4.43, 14.6) * mm, "end": v(-4.43, 14.62) * mm});
            skLineSegment(sketch, "E311", {"start": v(-4.43, 14.62) * mm, "end": v(-4.42, 14.65) * mm});
            skLineSegment(sketch, "E312", {"start": v(-4.42, 14.65) * mm, "end": v(-4.41, 14.7) * mm});
            skLineSegment(sketch, "E313", {"start": v(-4.41, 14.7) * mm, "end": v(-4.41, 14.8) * mm});
            skLineSegment(sketch, "E314", {"start": v(-4.41, 14.8) * mm, "end": v(-4.4, 14.91) * mm});
            skLineSegment(sketch, "E315", {"start": v(-4.4, 14.91) * mm, "end": v(-4.4, 15.03) * mm});
            skLineSegment(sketch, "E316", {"start": v(-4.4, 15.03) * mm, "end": v(-4.4, 15.09) * mm});
            skLineSegment(sketch, "E317", {"start": v(-4.4, 15.09) * mm, "end": v(-4.38, 15.27) * mm});
            skLineSegment(sketch, "E318", {"start": v(-4.38, 15.27) * mm, "end": v(-4.38, 15.3) * mm});
            skLineSegment(sketch, "E319", {"start": v(-4.38, 15.3) * mm, "end": v(-4.36, 15.51) * mm});
            skLineSegment(sketch, "E320", {"start": v(-4.36, 15.51) * mm, "end": v(-4.35, 15.54) * mm});
            skLineSegment(sketch, "E321", {"start": v(-4.35, 15.54) * mm, "end": v(-4.35, 15.54) * mm});
            skLineSegment(sketch, "E322", {"start": v(-4.35, 15.54) * mm, "end": v(-4.32, 15.74) * mm});
            skLineSegment(sketch, "E323", {"start": v(-4.32, 15.74) * mm, "end": v(-4.32, 15.76) * mm});
            skLineSegment(sketch, "E324", {"start": v(-4.32, 15.76) * mm, "end": v(-4.3, 15.82) * mm});
            skLineSegment(sketch, "E325", {"start": v(-4.3, 15.82) * mm, "end": v(-4.24, 16.13) * mm});
            skLineSegment(sketch, "E326", {"start": v(-4.24, 16.13) * mm, "end": v(-4.22, 16.2) * mm});
            skLineSegment(sketch, "E327", {"start": v(-4.22, 16.2) * mm, "end": v(-4.17, 16.26) * mm});
            skLineSegment(sketch, "E328", {"start": v(-4.17, 16.26) * mm, "end": v(-3.92, 16.34) * mm});
            skLineSegment(sketch, "E329", {"start": v(-3.92, 16.34) * mm, "end": v(-3.66, 16.38) * mm});
            skLineSegment(sketch, "E330", {"start": v(-3.66, 16.38) * mm, "end": v(-3.6, 16.35) * mm});
            skLineSegment(sketch, "E331", {"start": v(-3.6, 16.35) * mm, "end": v(-3.54, 16.3) * mm});
            skLineSegment(sketch, "E332", {"start": v(-3.54, 16.3) * mm, "end": v(-3.35, 16.05) * mm});
            skLineSegment(sketch, "E333", {"start": v(-3.35, 16.05) * mm, "end": v(-3.3, 16) * mm});
            skLineSegment(sketch, "E334", {"start": v(-3.3, 16) * mm, "end": v(-3.3, 15.98) * mm});
            skLineSegment(sketch, "E335", {"start": v(-3.3, 15.98) * mm, "end": v(-3.18, 15.82) * mm});
            skLineSegment(sketch, "E336", {"start": v(-3.18, 15.82) * mm, "end": v(-3.18, 15.82) * mm});
            skLineSegment(sketch, "E337", {"start": v(-3.18, 15.82) * mm, "end": v(-3.16, 15.8) * mm});
            skLineSegment(sketch, "E338", {"start": v(-3.16, 15.8) * mm, "end": v(-3.04, 15.61) * mm});
            skLineSegment(sketch, "E339", {"start": v(-3.04, 15.61) * mm, "end": v(-3.03, 15.6) * mm});
            skLineSegment(sketch, "E340", {"start": v(-3.03, 15.6) * mm, "end": v(-2.93, 15.44) * mm});
            skLineSegment(sketch, "E341", {"start": v(-2.93, 15.44) * mm, "end": v(-2.9, 15.39) * mm});
            skLineSegment(sketch, "E342", {"start": v(-2.9, 15.39) * mm, "end": v(-2.84, 15.29) * mm});
            skLineSegment(sketch, "E343", {"start": v(-2.84, 15.29) * mm, "end": v(-2.8, 15.2) * mm});
            skLineSegment(sketch, "E344", {"start": v(-2.8, 15.2) * mm, "end": v(-2.74, 15.1) * mm});
            skLineSegment(sketch, "E345", {"start": v(-2.74, 15.1) * mm, "end": v(-2.71, 15.06) * mm});
            skLineSegment(sketch, "E346", {"start": v(-2.71, 15.06) * mm, "end": v(-2.7, 15.04) * mm});
            skLineSegment(sketch, "E347", {"start": v(-2.7, 15.04) * mm, "end": v(-2.68, 15.03) * mm});
            skLineSegment(sketch, "E348", {"start": v(-2.68, 15.03) * mm, "end": v(-2.66, 15.02) * mm});
            skLineSegment(sketch, "E349", {"start": v(-2.66, 15.02) * mm, "end": v(-2.1, 15.1) * mm});
            skLineSegment(sketch, "E350", {"start": v(-2.1, 15.1) * mm, "end": v(-2.1, 15.12) * mm});
            skLineSegment(sketch, "E351", {"start": v(-2.1, 15.12) * mm, "end": v(-2.08, 15.14) * mm});
            skLineSegment(sketch, "E352", {"start": v(-2.08, 15.14) * mm, "end": v(-2.07, 15.16) * mm});
            skLineSegment(sketch, "E353", {"start": v(-2.07, 15.16) * mm, "end": v(-2.06, 15.2) * mm});
            skLineSegment(sketch, "E354", {"start": v(-2.06, 15.2) * mm, "end": v(-2.04, 15.32) * mm});
            skLineSegment(sketch, "E355", {"start": v(-2.04, 15.32) * mm, "end": v(-2.02, 15.42) * mm});
            skLineSegment(sketch, "E356", {"start": v(-2.02, 15.42) * mm, "end": v(-2, 15.53) * mm});
            skLineSegment(sketch, "E357", {"start": v(-2, 15.53) * mm, "end": v(-1.99, 15.6) * mm});
            skLineSegment(sketch, "E358", {"start": v(-1.99, 15.6) * mm, "end": v(-1.94, 15.77) * mm});
            skLineSegment(sketch, "E359", {"start": v(-1.94, 15.77) * mm, "end": v(-1.94, 15.79) * mm});
            skLineSegment(sketch, "E360", {"start": v(-1.94, 15.79) * mm, "end": v(-1.87, 16) * mm});
            skLineSegment(sketch, "E361", {"start": v(-1.87, 16) * mm, "end": v(-1.87, 16.03) * mm});
            skLineSegment(sketch, "E362", {"start": v(-1.87, 16.03) * mm, "end": v(-1.87, 16.03) * mm});
            skLineSegment(sketch, "E363", {"start": v(-1.87, 16.03) * mm, "end": v(-1.8, 16.22) * mm});
            skLineSegment(sketch, "E364", {"start": v(-1.8, 16.22) * mm, "end": v(-1.8, 16.24) * mm});
            skLineSegment(sketch, "E365", {"start": v(-1.8, 16.24) * mm, "end": v(-1.78, 16.3) * mm});
            skLineSegment(sketch, "E366", {"start": v(-1.78, 16.3) * mm, "end": v(-1.66, 16.6) * mm});
            skLineSegment(sketch, "E367", {"start": v(-1.66, 16.6) * mm, "end": v(-1.63, 16.66) * mm});
            skLineSegment(sketch, "E368", {"start": v(-1.63, 16.66) * mm, "end": v(-1.58, 16.7) * mm});
            skLineSegment(sketch, "E369", {"start": v(-1.58, 16.7) * mm, "end": v(-1.32, 16.75) * mm});
            skLineSegment(sketch, "E370", {"start": v(-1.32, 16.75) * mm, "end": v(-1.06, 16.75) * mm});
            skLineSegment(sketch, "E371", {"start": v(-1.06, 16.75) * mm, "end": v(-1, 16.7) * mm});
            skLineSegment(sketch, "E372", {"start": v(-1, 16.7) * mm, "end": v(-0.95, 16.65) * mm});
            skLineSegment(sketch, "E373", {"start": v(-0.95, 16.65) * mm, "end": v(-0.8, 16.38) * mm});
            skLineSegment(sketch, "E374", {"start": v(-0.8, 16.38) * mm, "end": v(-0.76, 16.32) * mm});
            skLineSegment(sketch, "E375", {"start": v(-0.76, 16.32) * mm, "end": v(-0.76, 16.3) * mm});
            skLineSegment(sketch, "E376", {"start": v(-0.76, 16.3) * mm, "end": v(-0.66, 16.12) * mm});
            skLineSegment(sketch, "E377", {"start": v(-0.66, 16.12) * mm, "end": v(-0.66, 16.12) * mm});
            skLineSegment(sketch, "E378", {"start": v(-0.66, 16.12) * mm, "end": v(-0.65, 16.1) * mm});
            skLineSegment(sketch, "E379", {"start": v(-0.65, 16.1) * mm, "end": v(-0.56, 15.9) * mm});
            skLineSegment(sketch, "E380", {"start": v(-0.56, 15.9) * mm, "end": v(-0.55, 15.88) * mm});
            skLineSegment(sketch, "E381", {"start": v(-0.55, 15.88) * mm, "end": v(-0.48, 15.71) * mm});
            skLineSegment(sketch, "E382", {"start": v(-0.48, 15.71) * mm, "end": v(-0.46, 15.65) * mm});
            skLineSegment(sketch, "E383", {"start": v(-0.46, 15.65) * mm, "end": v(-0.41, 15.54) * mm});
            skLineSegment(sketch, "E384", {"start": v(-0.41, 15.54) * mm, "end": v(-0.38, 15.45) * mm});
            skLineSegment(sketch, "E385", {"start": v(-0.38, 15.45) * mm, "end": v(-0.34, 15.34) * mm});
            skLineSegment(sketch, "E386", {"start": v(-0.34, 15.34) * mm, "end": v(-0.32, 15.3) * mm});
            skLineSegment(sketch, "E387", {"start": v(-0.32, 15.3) * mm, "end": v(-0.31, 15.27) * mm});
            skLineSegment(sketch, "E388", {"start": v(-0.31, 15.27) * mm, "end": v(-0.3, 15.26) * mm});
            skLineSegment(sketch, "E389", {"start": v(-0.3, 15.26) * mm, "end": v(-0.28, 15.25) * mm});
            skLineSegment(sketch, "E390", {"start": v(-0.28, 15.25) * mm, "end": v(0.28, 15.25) * mm});
            skLineSegment(sketch, "E391", {"start": v(0.28, 15.25) * mm, "end": v(0.3, 15.26) * mm});
            skLineSegment(sketch, "E392", {"start": v(0.3, 15.26) * mm, "end": v(0.31, 15.27) * mm});
            skLineSegment(sketch, "E393", {"start": v(0.31, 15.27) * mm, "end": v(0.32, 15.3) * mm});
            skLineSegment(sketch, "E394", {"start": v(0.32, 15.3) * mm, "end": v(0.34, 15.34) * mm});
            skLineSegment(sketch, "E395", {"start": v(0.34, 15.34) * mm, "end": v(0.38, 15.45) * mm});
            skLineSegment(sketch, "E396", {"start": v(0.38, 15.45) * mm, "end": v(0.41, 15.54) * mm});
            skLineSegment(sketch, "E397", {"start": v(0.41, 15.54) * mm, "end": v(0.46, 15.65) * mm});
            skLineSegment(sketch, "E398", {"start": v(0.46, 15.65) * mm, "end": v(0.48, 15.71) * mm});
            skLineSegment(sketch, "E399", {"start": v(0.48, 15.71) * mm, "end": v(0.55, 15.88) * mm});
            skLineSegment(sketch, "E400", {"start": v(0.55, 15.88) * mm, "end": v(0.56, 15.9) * mm});
            skLineSegment(sketch, "E401", {"start": v(0.56, 15.9) * mm, "end": v(0.65, 16.1) * mm});
            skLineSegment(sketch, "E402", {"start": v(0.65, 16.1) * mm, "end": v(0.66, 16.12) * mm});
            skLineSegment(sketch, "E403", {"start": v(0.66, 16.12) * mm, "end": v(0.66, 16.12) * mm});
            skLineSegment(sketch, "E404", {"start": v(0.66, 16.12) * mm, "end": v(0.76, 16.3) * mm});
            skLineSegment(sketch, "E405", {"start": v(0.76, 16.3) * mm, "end": v(0.76, 16.32) * mm});
            skLineSegment(sketch, "E406", {"start": v(0.76, 16.32) * mm, "end": v(0.8, 16.38) * mm});
            skLineSegment(sketch, "E407", {"start": v(0.8, 16.38) * mm, "end": v(0.95, 16.65) * mm});
            skLineSegment(sketch, "E408", {"start": v(0.95, 16.65) * mm, "end": v(1, 16.7) * mm});
            skLineSegment(sketch, "E409", {"start": v(1, 16.7) * mm, "end": v(1.06, 16.75) * mm});
            skLineSegment(sketch, "E410", {"start": v(1.06, 16.75) * mm, "end": v(1.32, 16.75) * mm});
            skLineSegment(sketch, "E411", {"start": v(1.32, 16.75) * mm, "end": v(1.58, 16.7) * mm});
            skLineSegment(sketch, "E412", {"start": v(1.58, 16.7) * mm, "end": v(1.63, 16.66) * mm});
            skLineSegment(sketch, "E413", {"start": v(1.63, 16.66) * mm, "end": v(1.66, 16.6) * mm});
            skLineSegment(sketch, "E414", {"start": v(1.66, 16.6) * mm, "end": v(1.78, 16.3) * mm});
            skLineSegment(sketch, "E415", {"start": v(1.78, 16.3) * mm, "end": v(1.8, 16.24) * mm});
            skLineSegment(sketch, "E416", {"start": v(1.8, 16.24) * mm, "end": v(1.8, 16.22) * mm});
            skLineSegment(sketch, "E417", {"start": v(1.8, 16.22) * mm, "end": v(1.87, 16.03) * mm});
            skLineSegment(sketch, "E418", {"start": v(1.87, 16.03) * mm, "end": v(1.87, 16.03) * mm});
            skLineSegment(sketch, "E419", {"start": v(1.87, 16.03) * mm, "end": v(1.87, 16) * mm});
            skLineSegment(sketch, "E420", {"start": v(1.87, 16) * mm, "end": v(1.94, 15.79) * mm});
            skLineSegment(sketch, "E421", {"start": v(1.94, 15.79) * mm, "end": v(1.94, 15.77) * mm});
            skLineSegment(sketch, "E422", {"start": v(1.94, 15.77) * mm, "end": v(1.99, 15.6) * mm});
            skLineSegment(sketch, "E423", {"start": v(1.99, 15.6) * mm, "end": v(2, 15.53) * mm});
            skLineSegment(sketch, "E424", {"start": v(2, 15.53) * mm, "end": v(2.02, 15.42) * mm});
            skLineSegment(sketch, "E425", {"start": v(2.02, 15.42) * mm, "end": v(2.04, 15.32) * mm});
            skLineSegment(sketch, "E426", {"start": v(2.04, 15.32) * mm, "end": v(2.06, 15.2) * mm});
            skLineSegment(sketch, "E427", {"start": v(2.06, 15.2) * mm, "end": v(2.07, 15.16) * mm});
            skLineSegment(sketch, "E428", {"start": v(2.07, 15.16) * mm, "end": v(2.08, 15.14) * mm});
            skLineSegment(sketch, "E429", {"start": v(2.08, 15.14) * mm, "end": v(2.1, 15.12) * mm});
            skLineSegment(sketch, "E430", {"start": v(2.1, 15.12) * mm, "end": v(2.1, 15.1) * mm});
            skLineSegment(sketch, "E431", {"start": v(2.1, 15.1) * mm, "end": v(2.66, 15.02) * mm});
            skLineSegment(sketch, "E432", {"start": v(2.66, 15.02) * mm, "end": v(2.68, 15.03) * mm});
            skLineSegment(sketch, "E433", {"start": v(2.68, 15.03) * mm, "end": v(2.7, 15.04) * mm});
            skLineSegment(sketch, "E434", {"start": v(2.7, 15.04) * mm, "end": v(2.71, 15.06) * mm});
            skLineSegment(sketch, "E435", {"start": v(2.71, 15.06) * mm, "end": v(2.74, 15.1) * mm});
            skLineSegment(sketch, "E436", {"start": v(2.74, 15.1) * mm, "end": v(2.8, 15.2) * mm});
            skLineSegment(sketch, "E437", {"start": v(2.8, 15.2) * mm, "end": v(2.84, 15.29) * mm});
            skLineSegment(sketch, "E438", {"start": v(2.84, 15.29) * mm, "end": v(2.9, 15.39) * mm});
            skLineSegment(sketch, "E439", {"start": v(2.9, 15.39) * mm, "end": v(2.93, 15.44) * mm});
            skLineSegment(sketch, "E440", {"start": v(2.93, 15.44) * mm, "end": v(3.03, 15.6) * mm});
            skLineSegment(sketch, "E441", {"start": v(3.03, 15.6) * mm, "end": v(3.04, 15.61) * mm});
            skLineSegment(sketch, "E442", {"start": v(3.04, 15.61) * mm, "end": v(3.16, 15.8) * mm});
            skLineSegment(sketch, "E443", {"start": v(3.16, 15.8) * mm, "end": v(3.18, 15.82) * mm});
            skLineSegment(sketch, "E444", {"start": v(3.18, 15.82) * mm, "end": v(3.18, 15.82) * mm});
            skLineSegment(sketch, "E445", {"start": v(3.18, 15.82) * mm, "end": v(3.3, 15.98) * mm});
            skLineSegment(sketch, "E446", {"start": v(3.3, 15.98) * mm, "end": v(3.3, 16) * mm});
            skLineSegment(sketch, "E447", {"start": v(3.3, 16) * mm, "end": v(3.35, 16.05) * mm});
            skLineSegment(sketch, "E448", {"start": v(3.35, 16.05) * mm, "end": v(3.54, 16.3) * mm});
            skLineSegment(sketch, "E449", {"start": v(3.54, 16.3) * mm, "end": v(3.6, 16.35) * mm});
            skLineSegment(sketch, "E450", {"start": v(3.6, 16.35) * mm, "end": v(3.66, 16.38) * mm});
            skLineSegment(sketch, "E451", {"start": v(3.66, 16.38) * mm, "end": v(3.92, 16.34) * mm});
            skLineSegment(sketch, "E452", {"start": v(3.92, 16.34) * mm, "end": v(4.17, 16.26) * mm});
            skLineSegment(sketch, "E453", {"start": v(4.17, 16.26) * mm, "end": v(4.22, 16.2) * mm});
            skLineSegment(sketch, "E454", {"start": v(4.22, 16.2) * mm, "end": v(4.24, 16.13) * mm});
            skLineSegment(sketch, "E455", {"start": v(4.24, 16.13) * mm, "end": v(4.3, 15.82) * mm});
            skLineSegment(sketch, "E456", {"start": v(4.3, 15.82) * mm, "end": v(4.32, 15.76) * mm});
            skLineSegment(sketch, "E457", {"start": v(4.32, 15.76) * mm, "end": v(4.32, 15.74) * mm});
            skLineSegment(sketch, "E458", {"start": v(4.32, 15.74) * mm, "end": v(4.35, 15.54) * mm});
            skLineSegment(sketch, "E459", {"start": v(4.35, 15.54) * mm, "end": v(4.35, 15.54) * mm});
            skLineSegment(sketch, "E460", {"start": v(4.35, 15.54) * mm, "end": v(4.36, 15.51) * mm});
            skLineSegment(sketch, "E461", {"start": v(4.36, 15.51) * mm, "end": v(4.38, 15.3) * mm});
            skLineSegment(sketch, "E462", {"start": v(4.38, 15.3) * mm, "end": v(4.38, 15.27) * mm});
            skLineSegment(sketch, "E463", {"start": v(4.38, 15.27) * mm, "end": v(4.4, 15.09) * mm});
            skLineSegment(sketch, "E464", {"start": v(4.4, 15.09) * mm, "end": v(4.4, 15.03) * mm});
            skLineSegment(sketch, "E465", {"start": v(4.4, 15.03) * mm, "end": v(4.4, 14.91) * mm});
            skLineSegment(sketch, "E466", {"start": v(4.4, 14.91) * mm, "end": v(4.41, 14.8) * mm});
            skLineSegment(sketch, "E467", {"start": v(4.41, 14.8) * mm, "end": v(4.41, 14.7) * mm});
            skLineSegment(sketch, "E468", {"start": v(4.41, 14.7) * mm, "end": v(4.42, 14.65) * mm});
            skLineSegment(sketch, "E469", {"start": v(4.42, 14.65) * mm, "end": v(4.43, 14.62) * mm});
            skLineSegment(sketch, "E470", {"start": v(4.43, 14.62) * mm, "end": v(4.43, 14.6) * mm});
            skLineSegment(sketch, "E471", {"start": v(4.43, 14.6) * mm, "end": v(4.44, 14.6) * mm});
            skLineSegment(sketch, "E472", {"start": v(4.44, 14.6) * mm, "end": v(4.98, 14.42) * mm});
            skLineSegment(sketch, "E473", {"start": v(4.98, 14.42) * mm, "end": v(5, 14.42) * mm});
            skLineSegment(sketch, "E474", {"start": v(5, 14.42) * mm, "end": v(5.02, 14.43) * mm});
            skLineSegment(sketch, "E475", {"start": v(5.02, 14.43) * mm, "end": v(5.04, 14.45) * mm});
            skLineSegment(sketch, "E476", {"start": v(5.04, 14.45) * mm, "end": v(5.07, 14.48) * mm});
            skLineSegment(sketch, "E477", {"start": v(5.07, 14.48) * mm, "end": v(5.13, 14.57) * mm});
            skLineSegment(sketch, "E478", {"start": v(5.13, 14.57) * mm, "end": v(5.2, 14.65) * mm});
            skLineSegment(sketch, "E479", {"start": v(5.2, 14.65) * mm, "end": v(5.27, 14.75) * mm});
            skLineSegment(sketch, "E480", {"start": v(5.27, 14.75) * mm, "end": v(5.3, 14.8) * mm});
            skLineSegment(sketch, "E481", {"start": v(5.3, 14.8) * mm, "end": v(5.43, 14.93) * mm});
            skLineSegment(sketch, "E482", {"start": v(5.43, 14.93) * mm, "end": v(5.44, 14.95) * mm});
            skLineSegment(sketch, "E483", {"start": v(5.44, 14.95) * mm, "end": v(5.6, 15.11) * mm});
            skLineSegment(sketch, "E484", {"start": v(5.6, 15.11) * mm, "end": v(5.61, 15.13) * mm});
            skLineSegment(sketch, "E485", {"start": v(5.61, 15.13) * mm, "end": v(5.61, 15.13) * mm});
            skLineSegment(sketch, "E486", {"start": v(5.61, 15.13) * mm, "end": v(5.76, 15.27) * mm});
            skLineSegment(sketch, "E487", {"start": v(5.76, 15.27) * mm, "end": v(5.77, 15.29) * mm});
            skLineSegment(sketch, "E488", {"start": v(5.77, 15.29) * mm, "end": v(5.82, 15.33) * mm});
            skLineSegment(sketch, "E489", {"start": v(5.82, 15.33) * mm, "end": v(6.05, 15.54) * mm});
            skLineSegment(sketch, "E490", {"start": v(6.05, 15.54) * mm, "end": v(6.11, 15.58) * mm});
            skLineSegment(sketch, "E491", {"start": v(6.11, 15.58) * mm, "end": v(6.18, 15.6) * mm});
            skLineSegment(sketch, "E492", {"start": v(6.18, 15.6) * mm, "end": v(6.43, 15.52) * mm});
            skLineSegment(sketch, "E493", {"start": v(6.43, 15.52) * mm, "end": v(6.66, 15.4) * mm});
            skLineSegment(sketch, "E494", {"start": v(6.66, 15.4) * mm, "end": v(6.7, 15.34) * mm});
            skLineSegment(sketch, "E495", {"start": v(6.7, 15.34) * mm, "end": v(6.71, 15.27) * mm});
            skLineSegment(sketch, "E496", {"start": v(6.71, 15.27) * mm, "end": v(6.73, 14.95) * mm});
            skLineSegment(sketch, "E497", {"start": v(6.73, 14.95) * mm, "end": v(6.73, 14.89) * mm});
            skLineSegment(sketch, "E498", {"start": v(6.73, 14.89) * mm, "end": v(6.73, 14.87) * mm});
            skLineSegment(sketch, "E499", {"start": v(6.73, 14.87) * mm, "end": v(6.73, 14.67) * mm});
            skLineSegment(sketch, "E500", {"start": v(6.73, 14.67) * mm, "end": v(6.73, 14.66) * mm});
            skLineSegment(sketch, "E501", {"start": v(6.73, 14.66) * mm, "end": v(6.73, 14.64) * mm});
            skLineSegment(sketch, "E502", {"start": v(6.73, 14.64) * mm, "end": v(6.72, 14.42) * mm});
            skLineSegment(sketch, "E503", {"start": v(6.72, 14.42) * mm, "end": v(6.72, 14.4) * mm});
            skLineSegment(sketch, "E504", {"start": v(6.72, 14.4) * mm, "end": v(6.7, 14.22) * mm});
            skLineSegment(sketch, "E505", {"start": v(6.7, 14.22) * mm, "end": v(6.7, 14.15) * mm});
            skLineSegment(sketch, "E506", {"start": v(6.7, 14.15) * mm, "end": v(6.69, 14.04) * mm});
            skLineSegment(sketch, "E507", {"start": v(6.69, 14.04) * mm, "end": v(6.67, 13.93) * mm});
            skLineSegment(sketch, "E508", {"start": v(6.67, 13.93) * mm, "end": v(6.66, 13.83) * mm});
            skLineSegment(sketch, "E509", {"start": v(6.66, 13.83) * mm, "end": v(6.66, 13.78) * mm});
            skLineSegment(sketch, "E510", {"start": v(6.66, 13.78) * mm, "end": v(6.66, 13.75) * mm});
            skLineSegment(sketch, "E511", {"start": v(6.66, 13.75) * mm, "end": v(6.66, 13.73) * mm});
            skLineSegment(sketch, "E512", {"start": v(6.66, 13.73) * mm, "end": v(6.67, 13.72) * mm});
            skLineSegment(sketch, "E513", {"start": v(6.67, 13.72) * mm, "end": v(7.17, 13.46) * mm});
            skLineSegment(sketch, "E514", {"start": v(7.17, 13.46) * mm, "end": v(7.2, 13.46) * mm});
            skLineSegment(sketch, "E515", {"start": v(7.2, 13.46) * mm, "end": v(7.21, 13.47) * mm});
            skLineSegment(sketch, "E516", {"start": v(7.21, 13.47) * mm, "end": v(7.23, 13.48) * mm});
            skLineSegment(sketch, "E517", {"start": v(7.23, 13.48) * mm, "end": v(7.27, 13.51) * mm});
            skLineSegment(sketch, "E518", {"start": v(7.27, 13.51) * mm, "end": v(7.35, 13.6) * mm});
            skLineSegment(sketch, "E519", {"start": v(7.35, 13.6) * mm, "end": v(7.43, 13.66) * mm});
            skLineSegment(sketch, "E520", {"start": v(7.43, 13.66) * mm, "end": v(7.51, 13.74) * mm});
            skLineSegment(sketch, "E521", {"start": v(7.51, 13.74) * mm, "end": v(7.56, 13.78) * mm});
            skLineSegment(sketch, "E522", {"start": v(7.56, 13.78) * mm, "end": v(7.7, 13.9) * mm});
            skLineSegment(sketch, "E523", {"start": v(7.7, 13.9) * mm, "end": v(7.71, 13.91) * mm});
            skLineSegment(sketch, "E524", {"start": v(7.71, 13.91) * mm, "end": v(7.89, 14.05) * mm});
            skLineSegment(sketch, "E525", {"start": v(7.89, 14.05) * mm, "end": v(7.9, 14.06) * mm});
            skLineSegment(sketch, "E526", {"start": v(7.9, 14.06) * mm, "end": v(7.91, 14.07) * mm});
            skLineSegment(sketch, "E527", {"start": v(7.91, 14.07) * mm, "end": v(8.08, 14.18) * mm});
            skLineSegment(sketch, "E528", {"start": v(8.08, 14.18) * mm, "end": v(8.1, 14.2) * mm});
            skLineSegment(sketch, "E529", {"start": v(8.1, 14.2) * mm, "end": v(8.14, 14.23) * mm});
            skLineSegment(sketch, "E530", {"start": v(8.14, 14.23) * mm, "end": v(8.4, 14.4) * mm});
            skLineSegment(sketch, "E531", {"start": v(8.4, 14.4) * mm, "end": v(8.47, 14.44) * mm});
            skLineSegment(sketch, "E532", {"start": v(8.47, 14.44) * mm, "end": v(8.54, 14.44) * mm});
            skLineSegment(sketch, "E533", {"start": v(8.54, 14.44) * mm, "end": v(8.78, 14.32) * mm});
            skLineSegment(sketch, "E534", {"start": v(8.78, 14.32) * mm, "end": v(9, 14.17) * mm});
            skLineSegment(sketch, "E535", {"start": v(9, 14.17) * mm, "end": v(9.02, 14.1) * mm});
            skLineSegment(sketch, "E536", {"start": v(9.02, 14.1) * mm, "end": v(9.02, 14.03) * mm});
            skLineSegment(sketch, "E537", {"start": v(9.02, 14.03) * mm, "end": v(8.98, 13.72) * mm});
            skLineSegment(sketch, "E538", {"start": v(8.98, 13.72) * mm, "end": v(8.97, 13.65) * mm});
            skLineSegment(sketch, "E539", {"start": v(8.97, 13.65) * mm, "end": v(8.97, 13.63) * mm});
            skLineSegment(sketch, "E540", {"start": v(8.97, 13.63) * mm, "end": v(8.94, 13.44) * mm});
            skLineSegment(sketch, "E541", {"start": v(8.94, 13.44) * mm, "end": v(8.94, 13.43) * mm});
            skLineSegment(sketch, "E542", {"start": v(8.94, 13.43) * mm, "end": v(8.94, 13.4) * mm});
            skLineSegment(sketch, "E543", {"start": v(8.94, 13.4) * mm, "end": v(8.9, 13.19) * mm});
            skLineSegment(sketch, "E544", {"start": v(8.9, 13.19) * mm, "end": v(8.89, 13.17) * mm});
            skLineSegment(sketch, "E545", {"start": v(8.89, 13.17) * mm, "end": v(8.85, 13) * mm});
            skLineSegment(sketch, "E546", {"start": v(8.85, 13) * mm, "end": v(8.83, 12.93) * mm});
            skLineSegment(sketch, "E547", {"start": v(8.83, 12.93) * mm, "end": v(8.8, 12.82) * mm});
            skLineSegment(sketch, "E548", {"start": v(8.8, 12.82) * mm, "end": v(8.77, 12.72) * mm});
            skLineSegment(sketch, "E549", {"start": v(8.77, 12.72) * mm, "end": v(8.74, 12.61) * mm});
            skLineSegment(sketch, "E550", {"start": v(8.74, 12.61) * mm, "end": v(8.73, 12.57) * mm});
            skLineSegment(sketch, "E551", {"start": v(8.73, 12.57) * mm, "end": v(8.73, 12.54) * mm});
            skLineSegment(sketch, "E552", {"start": v(8.73, 12.54) * mm, "end": v(8.73, 12.52) * mm});
            skLineSegment(sketch, "E553", {"start": v(8.73, 12.52) * mm, "end": v(8.74, 12.5) * mm});
            skLineSegment(sketch, "E554", {"start": v(8.74, 12.5) * mm, "end": v(9.2, 12.17) * mm});
            skLineSegment(sketch, "E555", {"start": v(9.2, 12.17) * mm, "end": v(9.21, 12.17) * mm});
            skLineSegment(sketch, "E556", {"start": v(9.21, 12.17) * mm, "end": v(9.23, 12.18) * mm});
            skLineSegment(sketch, "E557", {"start": v(9.23, 12.18) * mm, "end": v(9.25, 12.19) * mm});
            skLineSegment(sketch, "E558", {"start": v(9.25, 12.19) * mm, "end": v(9.3, 12.2) * mm});
            skLineSegment(sketch, "E559", {"start": v(9.3, 12.2) * mm, "end": v(9.39, 12.27) * mm});
            skLineSegment(sketch, "E560", {"start": v(9.39, 12.27) * mm, "end": v(9.47, 12.33) * mm});
            skLineSegment(sketch, "E561", {"start": v(9.47, 12.33) * mm, "end": v(9.57, 12.4) * mm});
            skLineSegment(sketch, "E562", {"start": v(9.57, 12.4) * mm, "end": v(9.62, 12.43) * mm});
            skLineSegment(sketch, "E563", {"start": v(9.62, 12.43) * mm, "end": v(9.78, 12.52) * mm});
            skLineSegment(sketch, "E564", {"start": v(9.78, 12.52) * mm, "end": v(9.8, 12.53) * mm});
            skLineSegment(sketch, "E565", {"start": v(9.8, 12.53) * mm, "end": v(10, 12.64) * mm});
            skLineSegment(sketch, "E566", {"start": v(10, 12.64) * mm, "end": v(10.01, 12.65) * mm});
            skLineSegment(sketch, "E567", {"start": v(10.01, 12.65) * mm, "end": v(10.02, 12.65) * mm});
            skLineSegment(sketch, "E568", {"start": v(10.02, 12.65) * mm, "end": v(10.2, 12.74) * mm});
            skLineSegment(sketch, "E569", {"start": v(10.2, 12.74) * mm, "end": v(10.21, 12.75) * mm});
            skLineSegment(sketch, "E570", {"start": v(10.21, 12.75) * mm, "end": v(10.27, 12.78) * mm});
            skLineSegment(sketch, "E571", {"start": v(10.27, 12.78) * mm, "end": v(10.56, 12.9) * mm});
            skLineSegment(sketch, "E572", {"start": v(10.56, 12.9) * mm, "end": v(10.63, 12.93) * mm});
            skLineSegment(sketch, "E573", {"start": v(10.63, 12.93) * mm, "end": v(10.7, 12.93) * mm});
            skLineSegment(sketch, "E574", {"start": v(10.7, 12.93) * mm, "end": v(10.91, 12.77) * mm});
            skLineSegment(sketch, "E575", {"start": v(10.91, 12.77) * mm, "end": v(11.1, 12.59) * mm});
            skLineSegment(sketch, "E576", {"start": v(11.1, 12.59) * mm, "end": v(11.11, 12.52) * mm});
            skLineSegment(sketch, "E577", {"start": v(11.11, 12.52) * mm, "end": v(11.1, 12.44) * mm});
            skLineSegment(sketch, "E578", {"start": v(11.1, 12.44) * mm, "end": v(11.02, 12.14) * mm});
            skLineSegment(sketch, "E579", {"start": v(11.02, 12.14) * mm, "end": v(11, 12.08) * mm});
            skLineSegment(sketch, "E580", {"start": v(11, 12.08) * mm, "end": v(11, 12.06) * mm});
            skLineSegment(sketch, "E581", {"start": v(11, 12.06) * mm, "end": v(10.93, 11.87) * mm});
            skLineSegment(sketch, "E582", {"start": v(10.93, 11.87) * mm, "end": v(10.93, 11.87) * mm});
            skLineSegment(sketch, "E583", {"start": v(10.93, 11.87) * mm, "end": v(10.92, 11.85) * mm});
            skLineSegment(sketch, "E584", {"start": v(10.92, 11.85) * mm, "end": v(10.85, 11.63) * mm});
            skLineSegment(sketch, "E585", {"start": v(10.85, 11.63) * mm, "end": v(10.84, 11.62) * mm});
            skLineSegment(sketch, "E586", {"start": v(10.84, 11.62) * mm, "end": v(10.77, 11.45) * mm});
            skLineSegment(sketch, "E587", {"start": v(10.77, 11.45) * mm, "end": v(10.75, 11.4) * mm});
            skLineSegment(sketch, "E588", {"start": v(10.75, 11.4) * mm, "end": v(10.7, 11.28) * mm});
            skLineSegment(sketch, "E589", {"start": v(10.7, 11.28) * mm, "end": v(10.65, 11.2) * mm});
            skLineSegment(sketch, "E590", {"start": v(10.65, 11.2) * mm, "end": v(10.6, 11.1) * mm});
            skLineSegment(sketch, "E591", {"start": v(10.6, 11.1) * mm, "end": v(10.59, 11.05) * mm});
            skLineSegment(sketch, "E592", {"start": v(10.59, 11.05) * mm, "end": v(10.58, 11.02) * mm});
            skLineSegment(sketch, "E593", {"start": v(10.58, 11.02) * mm, "end": v(10.58, 11) * mm});
            skLineSegment(sketch, "E594", {"start": v(10.58, 11) * mm, "end": v(10.58, 10.98) * mm});
            skLineSegment(sketch, "E595", {"start": v(10.58, 10.98) * mm, "end": v(10.98, 10.58) * mm});
            skLineSegment(sketch, "E596", {"start": v(10.98, 10.58) * mm, "end": v(11, 10.58) * mm});
            skLineSegment(sketch, "E597", {"start": v(11, 10.58) * mm, "end": v(11.02, 10.58) * mm});
            skLineSegment(sketch, "E598", {"start": v(11.02, 10.58) * mm, "end": v(11.05, 10.59) * mm});
            skLineSegment(sketch, "E599", {"start": v(11.05, 10.59) * mm, "end": v(11.1, 10.6) * mm});
            skLineSegment(sketch, "E600", {"start": v(11.1, 10.6) * mm, "end": v(11.2, 10.65) * mm});
            skLineSegment(sketch, "E601", {"start": v(11.2, 10.65) * mm, "end": v(11.28, 10.7) * mm});
            skLineSegment(sketch, "E602", {"start": v(11.28, 10.7) * mm, "end": v(11.4, 10.75) * mm});
            skLineSegment(sketch, "E603", {"start": v(11.4, 10.75) * mm, "end": v(11.45, 10.77) * mm});
            skLineSegment(sketch, "E604", {"start": v(11.45, 10.77) * mm, "end": v(11.62, 10.84) * mm});
            skLineSegment(sketch, "E605", {"start": v(11.62, 10.84) * mm, "end": v(11.63, 10.85) * mm});
            skLineSegment(sketch, "E606", {"start": v(11.63, 10.85) * mm, "end": v(11.85, 10.92) * mm});
            skLineSegment(sketch, "E607", {"start": v(11.85, 10.92) * mm, "end": v(11.87, 10.93) * mm});
            skLineSegment(sketch, "E608", {"start": v(11.87, 10.93) * mm, "end": v(11.87, 10.93) * mm});
            skLineSegment(sketch, "E609", {"start": v(11.87, 10.93) * mm, "end": v(12.06, 11) * mm});
            skLineSegment(sketch, "E610", {"start": v(12.06, 11) * mm, "end": v(12.08, 11) * mm});
            skLineSegment(sketch, "E611", {"start": v(12.08, 11) * mm, "end": v(12.14, 11.02) * mm});
            skLineSegment(sketch, "E612", {"start": v(12.14, 11.02) * mm, "end": v(12.44, 11.1) * mm});
            skLineSegment(sketch, "E613", {"start": v(12.44, 11.1) * mm, "end": v(12.52, 11.11) * mm});
            skLineSegment(sketch, "E614", {"start": v(12.52, 11.11) * mm, "end": v(12.59, 11.1) * mm});
            skLineSegment(sketch, "E615", {"start": v(12.59, 11.1) * mm, "end": v(12.77, 10.91) * mm});
            skLineSegment(sketch, "E616", {"start": v(12.77, 10.91) * mm, "end": v(12.93, 10.7) * mm});
            skLineSegment(sketch, "E617", {"start": v(12.93, 10.7) * mm, "end": v(12.93, 10.63) * mm});
            skLineSegment(sketch, "E618", {"start": v(12.93, 10.63) * mm, "end": v(12.9, 10.56) * mm});
            skLineSegment(sketch, "E619", {"start": v(12.9, 10.56) * mm, "end": v(12.78, 10.27) * mm});
            skLineSegment(sketch, "E620", {"start": v(12.78, 10.27) * mm, "end": v(12.75, 10.21) * mm});
            skLineSegment(sketch, "E621", {"start": v(12.75, 10.21) * mm, "end": v(12.74, 10.2) * mm});
            skLineSegment(sketch, "E622", {"start": v(12.74, 10.2) * mm, "end": v(12.65, 10.02) * mm});
            skLineSegment(sketch, "E623", {"start": v(12.65, 10.02) * mm, "end": v(12.65, 10.01) * mm});
            skLineSegment(sketch, "E624", {"start": v(12.65, 10.01) * mm, "end": v(12.64, 10) * mm});
            skLineSegment(sketch, "E625", {"start": v(12.64, 10) * mm, "end": v(12.53, 9.8) * mm});
            skLineSegment(sketch, "E626", {"start": v(12.53, 9.8) * mm, "end": v(12.52, 9.78) * mm});
            skLineSegment(sketch, "E627", {"start": v(12.52, 9.78) * mm, "end": v(12.43, 9.62) * mm});
            skLineSegment(sketch, "E628", {"start": v(12.43, 9.62) * mm, "end": v(12.4, 9.57) * mm});
            skLineSegment(sketch, "E629", {"start": v(12.4, 9.57) * mm, "end": v(12.33, 9.47) * mm});
            skLineSegment(sketch, "E630", {"start": v(12.33, 9.47) * mm, "end": v(12.27, 9.39) * mm});
            skLineSegment(sketch, "E631", {"start": v(12.27, 9.39) * mm, "end": v(12.2, 9.3) * mm});
            skLineSegment(sketch, "E632", {"start": v(12.2, 9.3) * mm, "end": v(12.19, 9.25) * mm});
            skLineSegment(sketch, "E633", {"start": v(12.19, 9.25) * mm, "end": v(12.18, 9.23) * mm});
            skLineSegment(sketch, "E634", {"start": v(12.18, 9.23) * mm, "end": v(12.17, 9.21) * mm});
            skLineSegment(sketch, "E635", {"start": v(12.17, 9.21) * mm, "end": v(12.17, 9.2) * mm});
            skLineSegment(sketch, "E636", {"start": v(12.17, 9.2) * mm, "end": v(12.5, 8.74) * mm});
            skLineSegment(sketch, "E637", {"start": v(12.5, 8.74) * mm, "end": v(12.52, 8.73) * mm});
            skLineSegment(sketch, "E638", {"start": v(12.52, 8.73) * mm, "end": v(12.54, 8.73) * mm});
            skLineSegment(sketch, "E639", {"start": v(12.54, 8.73) * mm, "end": v(12.57, 8.73) * mm});
            skLineSegment(sketch, "E640", {"start": v(12.57, 8.73) * mm, "end": v(12.61, 8.74) * mm});
            skLineSegment(sketch, "E641", {"start": v(12.61, 8.74) * mm, "end": v(12.72, 8.77) * mm});
            skLineSegment(sketch, "E642", {"start": v(12.72, 8.77) * mm, "end": v(12.82, 8.8) * mm});
            skLineSegment(sketch, "E643", {"start": v(12.82, 8.8) * mm, "end": v(12.93, 8.83) * mm});
            skLineSegment(sketch, "E644", {"start": v(12.93, 8.83) * mm, "end": v(13, 8.85) * mm});
            skLineSegment(sketch, "E645", {"start": v(13, 8.85) * mm, "end": v(13.17, 8.89) * mm});
            skLineSegment(sketch, "E646", {"start": v(13.17, 8.89) * mm, "end": v(13.19, 8.9) * mm});
            skLineSegment(sketch, "E647", {"start": v(13.19, 8.9) * mm, "end": v(13.4, 8.94) * mm});
            skLineSegment(sketch, "E648", {"start": v(13.4, 8.94) * mm, "end": v(13.43, 8.94) * mm});
            skLineSegment(sketch, "E649", {"start": v(13.43, 8.94) * mm, "end": v(13.44, 8.94) * mm});
            skLineSegment(sketch, "E650", {"start": v(13.44, 8.94) * mm, "end": v(13.63, 8.97) * mm});
            skLineSegment(sketch, "E651", {"start": v(13.63, 8.97) * mm, "end": v(13.65, 8.97) * mm});
            skLineSegment(sketch, "E652", {"start": v(13.65, 8.97) * mm, "end": v(13.72, 8.98) * mm});
            skLineSegment(sketch, "E653", {"start": v(13.72, 8.98) * mm, "end": v(14.03, 9.02) * mm});
            skLineSegment(sketch, "E654", {"start": v(14.03, 9.02) * mm, "end": v(14.1, 9.02) * mm});
            skLineSegment(sketch, "E655", {"start": v(14.1, 9.02) * mm, "end": v(14.17, 9) * mm});
            skLineSegment(sketch, "E656", {"start": v(14.17, 9) * mm, "end": v(14.32, 8.78) * mm});
            skLineSegment(sketch, "E657", {"start": v(14.32, 8.78) * mm, "end": v(14.44, 8.54) * mm});
            skLineSegment(sketch, "E658", {"start": v(14.44, 8.54) * mm, "end": v(14.44, 8.47) * mm});
            skLineSegment(sketch, "E659", {"start": v(14.44, 8.47) * mm, "end": v(14.4, 8.4) * mm});
            skLineSegment(sketch, "E660", {"start": v(14.4, 8.4) * mm, "end": v(14.23, 8.14) * mm});
            skLineSegment(sketch, "E661", {"start": v(14.23, 8.14) * mm, "end": v(14.2, 8.1) * mm});
            skLineSegment(sketch, "E662", {"start": v(14.2, 8.1) * mm, "end": v(14.18, 8.08) * mm});
            skLineSegment(sketch, "E663", {"start": v(14.18, 8.08) * mm, "end": v(14.07, 7.91) * mm});
            skLineSegment(sketch, "E664", {"start": v(14.07, 7.91) * mm, "end": v(14.06, 7.9) * mm});
            skLineSegment(sketch, "E665", {"start": v(14.06, 7.9) * mm, "end": v(14.05, 7.89) * mm});
            skLineSegment(sketch, "E666", {"start": v(14.05, 7.89) * mm, "end": v(13.91, 7.71) * mm});
            skLineSegment(sketch, "E667", {"start": v(13.91, 7.71) * mm, "end": v(13.9, 7.7) * mm});
            skLineSegment(sketch, "E668", {"start": v(13.9, 7.7) * mm, "end": v(13.78, 7.56) * mm});
            skLineSegment(sketch, "E669", {"start": v(13.78, 7.56) * mm, "end": v(13.74, 7.51) * mm});
            skLineSegment(sketch, "E670", {"start": v(13.74, 7.51) * mm, "end": v(13.66, 7.43) * mm});
            skLineSegment(sketch, "E671", {"start": v(13.66, 7.43) * mm, "end": v(13.6, 7.35) * mm});
            skLineSegment(sketch, "E672", {"start": v(13.6, 7.35) * mm, "end": v(13.51, 7.27) * mm});
            skLineSegment(sketch, "E673", {"start": v(13.51, 7.27) * mm, "end": v(13.48, 7.23) * mm});
            skLineSegment(sketch, "E674", {"start": v(13.48, 7.23) * mm, "end": v(13.47, 7.21) * mm});
            skLineSegment(sketch, "E675", {"start": v(13.47, 7.21) * mm, "end": v(13.46, 7.2) * mm});
            skLineSegment(sketch, "E676", {"start": v(13.46, 7.2) * mm, "end": v(13.46, 7.17) * mm});
            skLineSegment(sketch, "E677", {"start": v(13.46, 7.17) * mm, "end": v(13.72, 6.67) * mm});
            skLineSegment(sketch, "E678", {"start": v(13.72, 6.67) * mm, "end": v(13.73, 6.66) * mm});
            skLineSegment(sketch, "E679", {"start": v(13.73, 6.66) * mm, "end": v(13.75, 6.66) * mm});
            skLineSegment(sketch, "E680", {"start": v(13.75, 6.66) * mm, "end": v(13.78, 6.66) * mm});
            skLineSegment(sketch, "E681", {"start": v(13.78, 6.66) * mm, "end": v(13.83, 6.66) * mm});
            skLineSegment(sketch, "E682", {"start": v(13.83, 6.66) * mm, "end": v(13.93, 6.67) * mm});
            skLineSegment(sketch, "E683", {"start": v(13.93, 6.67) * mm, "end": v(14.04, 6.69) * mm});
            skLineSegment(sketch, "E684", {"start": v(14.04, 6.69) * mm, "end": v(14.15, 6.7) * mm});
            skLineSegment(sketch, "E685", {"start": v(14.15, 6.7) * mm, "end": v(14.22, 6.7) * mm});
            skLineSegment(sketch, "E686", {"start": v(14.22, 6.7) * mm, "end": v(14.4, 6.72) * mm});
            skLineSegment(sketch, "E687", {"start": v(14.4, 6.72) * mm, "end": v(14.42, 6.72) * mm});
            skLineSegment(sketch, "E688", {"start": v(14.42, 6.72) * mm, "end": v(14.64, 6.73) * mm});
            skLineSegment(sketch, "E689", {"start": v(14.64, 6.73) * mm, "end": v(14.66, 6.73) * mm});
            skLineSegment(sketch, "E690", {"start": v(14.66, 6.73) * mm, "end": v(14.67, 6.73) * mm});
            skLineSegment(sketch, "E691", {"start": v(14.67, 6.73) * mm, "end": v(14.87, 6.73) * mm});
            skLineSegment(sketch, "E692", {"start": v(14.87, 6.73) * mm, "end": v(14.89, 6.73) * mm});
            skLineSegment(sketch, "E693", {"start": v(14.89, 6.73) * mm, "end": v(14.95, 6.73) * mm});
            skLineSegment(sketch, "E694", {"start": v(14.95, 6.73) * mm, "end": v(15.27, 6.71) * mm});
            skLineSegment(sketch, "E695", {"start": v(15.27, 6.71) * mm, "end": v(15.34, 6.7) * mm});
            skLineSegment(sketch, "E696", {"start": v(15.34, 6.7) * mm, "end": v(15.4, 6.66) * mm});
            skLineSegment(sketch, "E697", {"start": v(15.4, 6.66) * mm, "end": v(15.52, 6.43) * mm});
            skLineSegment(sketch, "E698", {"start": v(15.52, 6.43) * mm, "end": v(15.6, 6.18) * mm});
            skLineSegment(sketch, "E699", {"start": v(15.6, 6.18) * mm, "end": v(15.58, 6.11) * mm});
            skLineSegment(sketch, "E700", {"start": v(15.58, 6.11) * mm, "end": v(15.54, 6.05) * mm});
            skLineSegment(sketch, "E701", {"start": v(15.54, 6.05) * mm, "end": v(15.33, 5.82) * mm});
            skLineSegment(sketch, "E702", {"start": v(15.33, 5.82) * mm, "end": v(15.29, 5.77) * mm});
            skLineSegment(sketch, "E703", {"start": v(15.29, 5.77) * mm, "end": v(15.27, 5.76) * mm});
            skLineSegment(sketch, "E704", {"start": v(15.27, 5.76) * mm, "end": v(15.13, 5.61) * mm});
            skLineSegment(sketch, "E705", {"start": v(15.13, 5.61) * mm, "end": v(15.13, 5.61) * mm});
            skLineSegment(sketch, "E706", {"start": v(15.13, 5.61) * mm, "end": v(15.11, 5.6) * mm});
            skLineSegment(sketch, "E707", {"start": v(15.11, 5.6) * mm, "end": v(14.95, 5.44) * mm});
            skLineSegment(sketch, "E708", {"start": v(14.95, 5.44) * mm, "end": v(14.93, 5.43) * mm});
            skLineSegment(sketch, "E709", {"start": v(14.93, 5.43) * mm, "end": v(14.8, 5.3) * mm});
            skLineSegment(sketch, "E710", {"start": v(14.8, 5.3) * mm, "end": v(14.75, 5.27) * mm});
            skLineSegment(sketch, "E711", {"start": v(14.75, 5.27) * mm, "end": v(14.65, 5.2) * mm});
            skLineSegment(sketch, "E712", {"start": v(14.65, 5.2) * mm, "end": v(14.57, 5.13) * mm});
            skLineSegment(sketch, "E713", {"start": v(14.57, 5.13) * mm, "end": v(14.48, 5.07) * mm});
            skLineSegment(sketch, "E714", {"start": v(14.48, 5.07) * mm, "end": v(14.45, 5.04) * mm});
            skLineSegment(sketch, "E715", {"start": v(14.45, 5.04) * mm, "end": v(14.43, 5.02) * mm});
            skLineSegment(sketch, "E716", {"start": v(14.43, 5.02) * mm, "end": v(14.42, 5) * mm});
            skLineSegment(sketch, "E717", {"start": v(14.42, 5) * mm, "end": v(14.42, 4.98) * mm});
            skLineSegment(sketch, "E718", {"start": v(14.42, 4.98) * mm, "end": v(14.6, 4.44) * mm});
            skLineSegment(sketch, "E719", {"start": v(14.6, 4.44) * mm, "end": v(14.6, 4.43) * mm});
            skLineSegment(sketch, "E720", {"start": v(14.6, 4.43) * mm, "end": v(14.62, 4.43) * mm});
            skLineSegment(sketch, "E721", {"start": v(14.62, 4.43) * mm, "end": v(14.65, 4.42) * mm});
            skLineSegment(sketch, "E722", {"start": v(14.65, 4.42) * mm, "end": v(14.7, 4.41) * mm});
            skLineSegment(sketch, "E723", {"start": v(14.7, 4.41) * mm, "end": v(14.8, 4.41) * mm});
            skLineSegment(sketch, "E724", {"start": v(14.8, 4.41) * mm, "end": v(14.91, 4.4) * mm});
            skLineSegment(sketch, "E725", {"start": v(14.91, 4.4) * mm, "end": v(15.03, 4.4) * mm});
            skLineSegment(sketch, "E726", {"start": v(15.03, 4.4) * mm, "end": v(15.09, 4.4) * mm});
            skLineSegment(sketch, "E727", {"start": v(15.09, 4.4) * mm, "end": v(15.27, 4.38) * mm});
            skLineSegment(sketch, "E728", {"start": v(15.27, 4.38) * mm, "end": v(15.3, 4.38) * mm});
            skLineSegment(sketch, "E729", {"start": v(15.3, 4.38) * mm, "end": v(15.51, 4.36) * mm});
            skLineSegment(sketch, "E730", {"start": v(15.51, 4.36) * mm, "end": v(15.54, 4.35) * mm});
            skLineSegment(sketch, "E731", {"start": v(15.54, 4.35) * mm, "end": v(15.54, 4.35) * mm});
            skLineSegment(sketch, "E732", {"start": v(15.54, 4.35) * mm, "end": v(15.74, 4.32) * mm});
            skLineSegment(sketch, "E733", {"start": v(15.74, 4.32) * mm, "end": v(15.76, 4.32) * mm});
            skLineSegment(sketch, "E734", {"start": v(15.76, 4.32) * mm, "end": v(15.82, 4.3) * mm});
            skLineSegment(sketch, "E735", {"start": v(15.82, 4.3) * mm, "end": v(16.13, 4.24) * mm});
            skLineSegment(sketch, "E736", {"start": v(16.13, 4.24) * mm, "end": v(16.2, 4.22) * mm});
            skLineSegment(sketch, "E737", {"start": v(16.2, 4.22) * mm, "end": v(16.26, 4.17) * mm});
            skLineSegment(sketch, "E738", {"start": v(16.26, 4.17) * mm, "end": v(16.34, 3.92) * mm});
            skLineSegment(sketch, "E739", {"start": v(16.34, 3.92) * mm, "end": v(16.38, 3.66) * mm});
            skLineSegment(sketch, "E740", {"start": v(16.38, 3.66) * mm, "end": v(16.35, 3.6) * mm});
            skLineSegment(sketch, "E741", {"start": v(16.35, 3.6) * mm, "end": v(16.3, 3.54) * mm});
            skLineSegment(sketch, "E742", {"start": v(16.3, 3.54) * mm, "end": v(16.05, 3.35) * mm});
            skLineSegment(sketch, "E743", {"start": v(16.05, 3.35) * mm, "end": v(16, 3.3) * mm});
            skLineSegment(sketch, "E744", {"start": v(16, 3.3) * mm, "end": v(15.98, 3.3) * mm});
            skLineSegment(sketch, "E745", {"start": v(15.98, 3.3) * mm, "end": v(15.82, 3.18) * mm});
            skLineSegment(sketch, "E746", {"start": v(15.82, 3.18) * mm, "end": v(15.82, 3.18) * mm});
            skLineSegment(sketch, "E747", {"start": v(15.82, 3.18) * mm, "end": v(15.8, 3.16) * mm});
            skLineSegment(sketch, "E748", {"start": v(15.8, 3.16) * mm, "end": v(15.61, 3.04) * mm});
            skLineSegment(sketch, "E749", {"start": v(15.61, 3.04) * mm, "end": v(15.6, 3.03) * mm});
            skLineSegment(sketch, "E750", {"start": v(15.6, 3.03) * mm, "end": v(15.44, 2.93) * mm});
            skLineSegment(sketch, "E751", {"start": v(15.44, 2.93) * mm, "end": v(15.39, 2.9) * mm});
            skLineSegment(sketch, "E752", {"start": v(15.39, 2.9) * mm, "end": v(15.29, 2.84) * mm});
            skLineSegment(sketch, "E753", {"start": v(15.29, 2.84) * mm, "end": v(15.2, 2.8) * mm});
            skLineSegment(sketch, "E754", {"start": v(15.2, 2.8) * mm, "end": v(15.1, 2.74) * mm});
            skLineSegment(sketch, "E755", {"start": v(15.1, 2.74) * mm, "end": v(15.06, 2.71) * mm});
            skLineSegment(sketch, "E756", {"start": v(15.06, 2.71) * mm, "end": v(15.04, 2.7) * mm});
            skLineSegment(sketch, "E757", {"start": v(15.04, 2.7) * mm, "end": v(15.03, 2.68) * mm});
            skLineSegment(sketch, "E758", {"start": v(15.03, 2.68) * mm, "end": v(15.02, 2.66) * mm});
            skLineSegment(sketch, "E759", {"start": v(15.02, 2.66) * mm, "end": v(15.1, 2.1) * mm});
            skLineSegment(sketch, "E760", {"start": v(15.1, 2.1) * mm, "end": v(15.12, 2.1) * mm});
            skLineSegment(sketch, "E761", {"start": v(15.12, 2.1) * mm, "end": v(15.14, 2.08) * mm});
            skLineSegment(sketch, "E762", {"start": v(15.14, 2.08) * mm, "end": v(15.16, 2.07) * mm});
            skLineSegment(sketch, "E763", {"start": v(15.16, 2.07) * mm, "end": v(15.2, 2.06) * mm});
            skLineSegment(sketch, "E764", {"start": v(15.2, 2.06) * mm, "end": v(15.32, 2.04) * mm});
            skLineSegment(sketch, "E765", {"start": v(15.32, 2.04) * mm, "end": v(15.42, 2.02) * mm});
            skLineSegment(sketch, "E766", {"start": v(15.42, 2.02) * mm, "end": v(15.53, 2) * mm});
            skLineSegment(sketch, "E767", {"start": v(15.53, 2) * mm, "end": v(15.6, 1.99) * mm});
            skLineSegment(sketch, "E768", {"start": v(15.6, 1.99) * mm, "end": v(15.77, 1.94) * mm});
            skLineSegment(sketch, "E769", {"start": v(15.77, 1.94) * mm, "end": v(15.79, 1.94) * mm});
            skLineSegment(sketch, "E770", {"start": v(15.79, 1.94) * mm, "end": v(16, 1.87) * mm});
            skLineSegment(sketch, "E771", {"start": v(16, 1.87) * mm, "end": v(16.03, 1.87) * mm});
            skLineSegment(sketch, "E772", {"start": v(16.03, 1.87) * mm, "end": v(16.03, 1.87) * mm});
            skLineSegment(sketch, "E773", {"start": v(16.03, 1.87) * mm, "end": v(16.22, 1.8) * mm});
            skLineSegment(sketch, "E774", {"start": v(16.22, 1.8) * mm, "end": v(16.24, 1.8) * mm});
            skLineSegment(sketch, "E775", {"start": v(16.24, 1.8) * mm, "end": v(16.3, 1.78) * mm});
            skLineSegment(sketch, "E776", {"start": v(16.3, 1.78) * mm, "end": v(16.6, 1.66) * mm});
            skLineSegment(sketch, "E777", {"start": v(16.6, 1.66) * mm, "end": v(16.66, 1.63) * mm});
            skLineSegment(sketch, "E778", {"start": v(16.66, 1.63) * mm, "end": v(16.7, 1.58) * mm});
            skLineSegment(sketch, "E779", {"start": v(16.7, 1.58) * mm, "end": v(16.75, 1.32) * mm});
            skLineSegment(sketch, "E780", {"start": v(16.75, 1.32) * mm, "end": v(16.75, 1.06) * mm});
            skLineSegment(sketch, "E781", {"start": v(16.75, 1.06) * mm, "end": v(16.7, 1) * mm});
            skLineSegment(sketch, "E782", {"start": v(16.7, 1) * mm, "end": v(16.65, 0.95) * mm});
            skLineSegment(sketch, "E783", {"start": v(16.65, 0.95) * mm, "end": v(16.38, 0.8) * mm});
            skLineSegment(sketch, "E784", {"start": v(16.38, 0.8) * mm, "end": v(16.32, 0.76) * mm});
            skLineSegment(sketch, "E785", {"start": v(16.32, 0.76) * mm, "end": v(16.3, 0.76) * mm});
            skLineSegment(sketch, "E786", {"start": v(16.3, 0.76) * mm, "end": v(16.12, 0.66) * mm});
            skLineSegment(sketch, "E787", {"start": v(16.12, 0.66) * mm, "end": v(16.12, 0.66) * mm});
            skLineSegment(sketch, "E788", {"start": v(16.12, 0.66) * mm, "end": v(16.1, 0.65) * mm});
            skLineSegment(sketch, "E789", {"start": v(16.1, 0.65) * mm, "end": v(15.9, 0.56) * mm});
            skLineSegment(sketch, "E790", {"start": v(15.9, 0.56) * mm, "end": v(15.88, 0.55) * mm});
            skLineSegment(sketch, "E791", {"start": v(15.88, 0.55) * mm, "end": v(15.71, 0.48) * mm});
            skLineSegment(sketch, "E792", {"start": v(15.71, 0.48) * mm, "end": v(15.65, 0.46) * mm});
            skLineSegment(sketch, "E793", {"start": v(15.65, 0.46) * mm, "end": v(15.54, 0.41) * mm});
            skLineSegment(sketch, "E794", {"start": v(15.54, 0.41) * mm, "end": v(15.45, 0.38) * mm});
            skLineSegment(sketch, "E795", {"start": v(15.45, 0.38) * mm, "end": v(15.34, 0.34) * mm});
            skLineSegment(sketch, "E796", {"start": v(15.34, 0.34) * mm, "end": v(15.3, 0.32) * mm});
            skLineSegment(sketch, "E797", {"start": v(15.3, 0.32) * mm, "end": v(15.27, 0.31) * mm});
            skLineSegment(sketch, "E798", {"start": v(15.27, 0.31) * mm, "end": v(15.26, 0.3) * mm});
            skLineSegment(sketch, "E799", {"start": v(15.26, 0.3) * mm, "end": v(15.25, 0.28) * mm});
            skLineSegment(sketch, "E800", {"start": v(15.25, 0.28) * mm, "end": v(15.25, -0.28) * mm});
            skLineSegment(sketch, "E801", {"start": v(15.25, -0.28) * mm, "end": v(15.26, -0.3) * mm});
            skLineSegment(sketch, "E802", {"start": v(15.26, -0.3) * mm, "end": v(15.27, -0.31) * mm});
            skLineSegment(sketch, "E803", {"start": v(15.27, -0.31) * mm, "end": v(15.3, -0.32) * mm});
            skLineSegment(sketch, "E804", {"start": v(15.3, -0.32) * mm, "end": v(15.34, -0.34) * mm});
            skLineSegment(sketch, "E805", {"start": v(15.34, -0.34) * mm, "end": v(15.45, -0.38) * mm});
            skLineSegment(sketch, "E806", {"start": v(15.45, -0.38) * mm, "end": v(15.54, -0.41) * mm});
            skLineSegment(sketch, "E807", {"start": v(15.54, -0.41) * mm, "end": v(15.65, -0.46) * mm});
            skLineSegment(sketch, "E808", {"start": v(15.65, -0.46) * mm, "end": v(15.71, -0.48) * mm});
            skLineSegment(sketch, "E809", {"start": v(15.71, -0.48) * mm, "end": v(15.88, -0.55) * mm});
            skLineSegment(sketch, "E810", {"start": v(15.88, -0.55) * mm, "end": v(15.9, -0.56) * mm});
            skLineSegment(sketch, "E811", {"start": v(15.9, -0.56) * mm, "end": v(16.1, -0.65) * mm});
            skLineSegment(sketch, "E812", {"start": v(16.1, -0.65) * mm, "end": v(16.12, -0.66) * mm});
            skLineSegment(sketch, "E813", {"start": v(16.12, -0.66) * mm, "end": v(16.12, -0.66) * mm});
            skLineSegment(sketch, "E814", {"start": v(16.12, -0.66) * mm, "end": v(16.3, -0.76) * mm});
            skLineSegment(sketch, "E815", {"start": v(16.3, -0.76) * mm, "end": v(16.32, -0.76) * mm});
            skLineSegment(sketch, "E816", {"start": v(16.32, -0.76) * mm, "end": v(16.38, -0.8) * mm});
            skLineSegment(sketch, "E817", {"start": v(16.38, -0.8) * mm, "end": v(16.65, -0.95) * mm});
            skLineSegment(sketch, "E818", {"start": v(16.65, -0.95) * mm, "end": v(16.7, -1) * mm});
            skLineSegment(sketch, "E819", {"start": v(16.7, -1) * mm, "end": v(16.75, -1.06) * mm});
            skLineSegment(sketch, "E820", {"start": v(16.75, -1.06) * mm, "end": v(16.75, -1.32) * mm});
            skLineSegment(sketch, "E821", {"start": v(16.75, -1.32) * mm, "end": v(16.7, -1.58) * mm});
            skLineSegment(sketch, "E822", {"start": v(16.7, -1.58) * mm, "end": v(16.66, -1.63) * mm});
            skLineSegment(sketch, "E823", {"start": v(16.66, -1.63) * mm, "end": v(16.6, -1.66) * mm});
            skLineSegment(sketch, "E824", {"start": v(16.6, -1.66) * mm, "end": v(16.3, -1.78) * mm});
            skLineSegment(sketch, "E825", {"start": v(16.3, -1.78) * mm, "end": v(16.24, -1.8) * mm});
            skLineSegment(sketch, "E826", {"start": v(16.24, -1.8) * mm, "end": v(16.22, -1.8) * mm});
            skLineSegment(sketch, "E827", {"start": v(16.22, -1.8) * mm, "end": v(16.03, -1.87) * mm});
            skLineSegment(sketch, "E828", {"start": v(16.03, -1.87) * mm, "end": v(16.03, -1.87) * mm});
            skLineSegment(sketch, "E829", {"start": v(16.03, -1.87) * mm, "end": v(16, -1.87) * mm});
            skLineSegment(sketch, "E830", {"start": v(16, -1.87) * mm, "end": v(15.79, -1.94) * mm});
            skLineSegment(sketch, "E831", {"start": v(15.79, -1.94) * mm, "end": v(15.77, -1.94) * mm});
            skLineSegment(sketch, "E832", {"start": v(15.77, -1.94) * mm, "end": v(15.6, -1.99) * mm});
            skLineSegment(sketch, "E833", {"start": v(15.6, -1.99) * mm, "end": v(15.53, -2) * mm});
            skLineSegment(sketch, "E834", {"start": v(15.53, -2) * mm, "end": v(15.42, -2.02) * mm});
            skLineSegment(sketch, "E835", {"start": v(15.42, -2.02) * mm, "end": v(15.32, -2.04) * mm});
            skLineSegment(sketch, "E836", {"start": v(15.32, -2.04) * mm, "end": v(15.2, -2.06) * mm});
            skLineSegment(sketch, "E837", {"start": v(15.2, -2.06) * mm, "end": v(15.16, -2.07) * mm});
            skLineSegment(sketch, "E838", {"start": v(15.16, -2.07) * mm, "end": v(15.14, -2.08) * mm});
            skLineSegment(sketch, "E839", {"start": v(15.14, -2.08) * mm, "end": v(15.12, -2.1) * mm});
            skLineSegment(sketch, "E840", {"start": v(15.12, -2.1) * mm, "end": v(15.1, -2.1) * mm});
            skLineSegment(sketch, "E841", {"start": v(15.1, -2.1) * mm, "end": v(15.02, -2.66) * mm});
            skLineSegment(sketch, "E842", {"start": v(15.02, -2.66) * mm, "end": v(15.03, -2.68) * mm});
            skLineSegment(sketch, "E843", {"start": v(15.03, -2.68) * mm, "end": v(15.04, -2.7) * mm});
            skLineSegment(sketch, "E844", {"start": v(15.04, -2.7) * mm, "end": v(15.06, -2.71) * mm});
            skLineSegment(sketch, "E845", {"start": v(15.06, -2.71) * mm, "end": v(15.1, -2.74) * mm});
            skLineSegment(sketch, "E846", {"start": v(15.1, -2.74) * mm, "end": v(15.2, -2.8) * mm});
            skLineSegment(sketch, "E847", {"start": v(15.2, -2.8) * mm, "end": v(15.29, -2.84) * mm});
            skLineSegment(sketch, "E848", {"start": v(15.29, -2.84) * mm, "end": v(15.39, -2.9) * mm});
            skLineSegment(sketch, "E849", {"start": v(15.39, -2.9) * mm, "end": v(15.44, -2.93) * mm});
            skLineSegment(sketch, "E850", {"start": v(15.44, -2.93) * mm, "end": v(15.6, -3.03) * mm});
            skLineSegment(sketch, "E851", {"start": v(15.6, -3.03) * mm, "end": v(15.61, -3.04) * mm});
            skLineSegment(sketch, "E852", {"start": v(15.61, -3.04) * mm, "end": v(15.8, -3.16) * mm});
            skLineSegment(sketch, "E853", {"start": v(15.8, -3.16) * mm, "end": v(15.82, -3.18) * mm});
            skLineSegment(sketch, "E854", {"start": v(15.82, -3.18) * mm, "end": v(15.82, -3.18) * mm});
            skLineSegment(sketch, "E855", {"start": v(15.82, -3.18) * mm, "end": v(15.98, -3.3) * mm});
            skLineSegment(sketch, "E856", {"start": v(15.98, -3.3) * mm, "end": v(16, -3.3) * mm});
            skLineSegment(sketch, "E857", {"start": v(16, -3.3) * mm, "end": v(16.05, -3.35) * mm});
            skLineSegment(sketch, "E858", {"start": v(16.05, -3.35) * mm, "end": v(16.3, -3.54) * mm});
            skLineSegment(sketch, "E859", {"start": v(16.3, -3.54) * mm, "end": v(16.35, -3.6) * mm});
            skLineSegment(sketch, "E860", {"start": v(16.35, -3.6) * mm, "end": v(16.38, -3.66) * mm});
            skLineSegment(sketch, "E861", {"start": v(16.38, -3.66) * mm, "end": v(16.34, -3.92) * mm});
            skLineSegment(sketch, "E862", {"start": v(16.34, -3.92) * mm, "end": v(16.26, -4.17) * mm});
            skLineSegment(sketch, "E863", {"start": v(16.26, -4.17) * mm, "end": v(16.2, -4.22) * mm});
            skLineSegment(sketch, "E864", {"start": v(16.2, -4.22) * mm, "end": v(16.13, -4.24) * mm});
            skLineSegment(sketch, "E865", {"start": v(16.13, -4.24) * mm, "end": v(15.82, -4.3) * mm});
            skLineSegment(sketch, "E866", {"start": v(15.82, -4.3) * mm, "end": v(15.76, -4.32) * mm});
            skLineSegment(sketch, "E867", {"start": v(15.76, -4.32) * mm, "end": v(15.74, -4.32) * mm});
            skLineSegment(sketch, "E868", {"start": v(15.74, -4.32) * mm, "end": v(15.54, -4.35) * mm});
            skLineSegment(sketch, "E869", {"start": v(15.54, -4.35) * mm, "end": v(15.54, -4.35) * mm});
            skLineSegment(sketch, "E870", {"start": v(15.54, -4.35) * mm, "end": v(15.51, -4.36) * mm});
            skLineSegment(sketch, "E871", {"start": v(15.51, -4.36) * mm, "end": v(15.3, -4.38) * mm});
            skLineSegment(sketch, "E872", {"start": v(15.3, -4.38) * mm, "end": v(15.27, -4.38) * mm});
            skLineSegment(sketch, "E873", {"start": v(15.27, -4.38) * mm, "end": v(15.09, -4.4) * mm});
            skLineSegment(sketch, "E874", {"start": v(15.09, -4.4) * mm, "end": v(15.03, -4.4) * mm});
            skLineSegment(sketch, "E875", {"start": v(15.03, -4.4) * mm, "end": v(14.91, -4.4) * mm});
            skLineSegment(sketch, "E876", {"start": v(14.91, -4.4) * mm, "end": v(14.8, -4.41) * mm});
            skLineSegment(sketch, "E877", {"start": v(14.8, -4.41) * mm, "end": v(14.7, -4.41) * mm});
            skLineSegment(sketch, "E878", {"start": v(14.7, -4.41) * mm, "end": v(14.65, -4.42) * mm});
            skLineSegment(sketch, "E879", {"start": v(14.65, -4.42) * mm, "end": v(14.62, -4.43) * mm});
            skLineSegment(sketch, "E880", {"start": v(14.62, -4.43) * mm, "end": v(14.6, -4.43) * mm});
            skLineSegment(sketch, "E881", {"start": v(14.6, -4.43) * mm, "end": v(14.6, -4.44) * mm});
            skLineSegment(sketch, "E882", {"start": v(14.6, -4.44) * mm, "end": v(14.42, -4.98) * mm});
            skLineSegment(sketch, "E883", {"start": v(14.42, -4.98) * mm, "end": v(14.42, -5) * mm});
            skLineSegment(sketch, "E884", {"start": v(14.42, -5) * mm, "end": v(14.43, -5.02) * mm});
            skLineSegment(sketch, "E885", {"start": v(14.43, -5.02) * mm, "end": v(14.45, -5.04) * mm});
            skLineSegment(sketch, "E886", {"start": v(14.45, -5.04) * mm, "end": v(14.48, -5.07) * mm});
            skLineSegment(sketch, "E887", {"start": v(14.48, -5.07) * mm, "end": v(14.57, -5.13) * mm});
            skLineSegment(sketch, "E888", {"start": v(14.57, -5.13) * mm, "end": v(14.65, -5.2) * mm});
            skLineSegment(sketch, "E889", {"start": v(14.65, -5.2) * mm, "end": v(14.75, -5.27) * mm});
            skLineSegment(sketch, "E890", {"start": v(14.75, -5.27) * mm, "end": v(14.8, -5.3) * mm});
            skLineSegment(sketch, "E891", {"start": v(14.8, -5.3) * mm, "end": v(14.93, -5.43) * mm});
            skLineSegment(sketch, "E892", {"start": v(14.93, -5.43) * mm, "end": v(14.95, -5.44) * mm});
            skLineSegment(sketch, "E893", {"start": v(14.95, -5.44) * mm, "end": v(15.11, -5.6) * mm});
            skLineSegment(sketch, "E894", {"start": v(15.11, -5.6) * mm, "end": v(15.13, -5.61) * mm});
            skLineSegment(sketch, "E895", {"start": v(15.13, -5.61) * mm, "end": v(15.13, -5.61) * mm});
            skLineSegment(sketch, "E896", {"start": v(15.13, -5.61) * mm, "end": v(15.27, -5.76) * mm});
            skLineSegment(sketch, "E897", {"start": v(15.27, -5.76) * mm, "end": v(15.29, -5.77) * mm});
            skLineSegment(sketch, "E898", {"start": v(15.29, -5.77) * mm, "end": v(15.33, -5.82) * mm});
            skLineSegment(sketch, "E899", {"start": v(15.33, -5.82) * mm, "end": v(15.54, -6.05) * mm});
            skLineSegment(sketch, "E900", {"start": v(15.54, -6.05) * mm, "end": v(15.58, -6.11) * mm});
            skLineSegment(sketch, "E901", {"start": v(15.58, -6.11) * mm, "end": v(15.6, -6.18) * mm});
            skLineSegment(sketch, "E902", {"start": v(15.6, -6.18) * mm, "end": v(15.52, -6.43) * mm});
            skLineSegment(sketch, "E903", {"start": v(15.52, -6.43) * mm, "end": v(15.4, -6.66) * mm});
            skLineSegment(sketch, "E904", {"start": v(15.4, -6.66) * mm, "end": v(15.34, -6.7) * mm});
            skLineSegment(sketch, "E905", {"start": v(15.34, -6.7) * mm, "end": v(15.27, -6.71) * mm});
            skLineSegment(sketch, "E906", {"start": v(15.27, -6.71) * mm, "end": v(14.95, -6.73) * mm});
            skLineSegment(sketch, "E907", {"start": v(14.95, -6.73) * mm, "end": v(14.89, -6.73) * mm});
            skLineSegment(sketch, "E908", {"start": v(14.89, -6.73) * mm, "end": v(14.87, -6.73) * mm});
            skLineSegment(sketch, "E909", {"start": v(14.87, -6.73) * mm, "end": v(14.67, -6.73) * mm});
            skLineSegment(sketch, "E910", {"start": v(14.67, -6.73) * mm, "end": v(14.66, -6.73) * mm});
            skLineSegment(sketch, "E911", {"start": v(14.66, -6.73) * mm, "end": v(14.64, -6.73) * mm});
            skLineSegment(sketch, "E912", {"start": v(14.64, -6.73) * mm, "end": v(14.42, -6.72) * mm});
            skLineSegment(sketch, "E913", {"start": v(14.42, -6.72) * mm, "end": v(14.4, -6.72) * mm});
            skLineSegment(sketch, "E914", {"start": v(14.4, -6.72) * mm, "end": v(14.22, -6.7) * mm});
            skLineSegment(sketch, "E915", {"start": v(14.22, -6.7) * mm, "end": v(14.15, -6.7) * mm});
            skLineSegment(sketch, "E916", {"start": v(14.15, -6.7) * mm, "end": v(14.04, -6.69) * mm});
            skLineSegment(sketch, "E917", {"start": v(14.04, -6.69) * mm, "end": v(13.93, -6.67) * mm});
            skLineSegment(sketch, "E918", {"start": v(13.93, -6.67) * mm, "end": v(13.83, -6.66) * mm});
            skLineSegment(sketch, "E919", {"start": v(13.83, -6.66) * mm, "end": v(13.78, -6.66) * mm});
            skLineSegment(sketch, "E920", {"start": v(13.78, -6.66) * mm, "end": v(13.75, -6.66) * mm});
            skLineSegment(sketch, "E921", {"start": v(13.75, -6.66) * mm, "end": v(13.73, -6.66) * mm});
            skLineSegment(sketch, "E922", {"start": v(13.73, -6.66) * mm, "end": v(13.72, -6.67) * mm});
            skLineSegment(sketch, "E923", {"start": v(13.72, -6.67) * mm, "end": v(13.46, -7.17) * mm});
            skLineSegment(sketch, "E924", {"start": v(13.46, -7.17) * mm, "end": v(13.46, -7.2) * mm});
            skLineSegment(sketch, "E925", {"start": v(13.46, -7.2) * mm, "end": v(13.47, -7.21) * mm});
            skLineSegment(sketch, "E926", {"start": v(13.47, -7.21) * mm, "end": v(13.48, -7.23) * mm});
            skLineSegment(sketch, "E927", {"start": v(13.48, -7.23) * mm, "end": v(13.51, -7.27) * mm});
            skLineSegment(sketch, "E928", {"start": v(13.51, -7.27) * mm, "end": v(13.6, -7.35) * mm});
            skLineSegment(sketch, "E929", {"start": v(13.6, -7.35) * mm, "end": v(13.66, -7.43) * mm});
            skLineSegment(sketch, "E930", {"start": v(13.66, -7.43) * mm, "end": v(13.74, -7.51) * mm});
            skLineSegment(sketch, "E931", {"start": v(13.74, -7.51) * mm, "end": v(13.78, -7.56) * mm});
            skLineSegment(sketch, "E932", {"start": v(13.78, -7.56) * mm, "end": v(13.9, -7.7) * mm});
            skLineSegment(sketch, "E933", {"start": v(13.9, -7.7) * mm, "end": v(13.91, -7.71) * mm});
            skLineSegment(sketch, "E934", {"start": v(13.91, -7.71) * mm, "end": v(14.05, -7.89) * mm});
            skLineSegment(sketch, "E935", {"start": v(14.05, -7.89) * mm, "end": v(14.06, -7.9) * mm});
            skLineSegment(sketch, "E936", {"start": v(14.06, -7.9) * mm, "end": v(14.07, -7.91) * mm});
            skLineSegment(sketch, "E937", {"start": v(14.07, -7.91) * mm, "end": v(14.18, -8.08) * mm});
            skLineSegment(sketch, "E938", {"start": v(14.18, -8.08) * mm, "end": v(14.2, -8.1) * mm});
            skLineSegment(sketch, "E939", {"start": v(14.2, -8.1) * mm, "end": v(14.23, -8.14) * mm});
            skLineSegment(sketch, "E940", {"start": v(14.23, -8.14) * mm, "end": v(14.4, -8.4) * mm});
            skLineSegment(sketch, "E941", {"start": v(14.4, -8.4) * mm, "end": v(14.44, -8.47) * mm});
            skLineSegment(sketch, "E942", {"start": v(14.44, -8.47) * mm, "end": v(14.44, -8.54) * mm});
            skLineSegment(sketch, "E943", {"start": v(14.44, -8.54) * mm, "end": v(14.32, -8.78) * mm});
            skLineSegment(sketch, "E944", {"start": v(14.32, -8.78) * mm, "end": v(14.17, -9) * mm});
            skLineSegment(sketch, "E945", {"start": v(14.17, -9) * mm, "end": v(14.1, -9.02) * mm});
            skLineSegment(sketch, "E946", {"start": v(14.1, -9.02) * mm, "end": v(14.03, -9.02) * mm});
            skLineSegment(sketch, "E947", {"start": v(14.03, -9.02) * mm, "end": v(13.72, -8.98) * mm});
            skLineSegment(sketch, "E948", {"start": v(13.72, -8.98) * mm, "end": v(13.65, -8.97) * mm});
            skLineSegment(sketch, "E949", {"start": v(13.65, -8.97) * mm, "end": v(13.63, -8.97) * mm});
            skLineSegment(sketch, "E950", {"start": v(13.63, -8.97) * mm, "end": v(13.44, -8.94) * mm});
            skLineSegment(sketch, "E951", {"start": v(13.44, -8.94) * mm, "end": v(13.43, -8.94) * mm});
            skLineSegment(sketch, "E952", {"start": v(13.43, -8.94) * mm, "end": v(13.4, -8.94) * mm});
            skLineSegment(sketch, "E953", {"start": v(13.4, -8.94) * mm, "end": v(13.19, -8.9) * mm});
            skLineSegment(sketch, "E954", {"start": v(13.19, -8.9) * mm, "end": v(13.17, -8.89) * mm});
            skLineSegment(sketch, "E955", {"start": v(13.17, -8.89) * mm, "end": v(13, -8.85) * mm});
            skLineSegment(sketch, "E956", {"start": v(13, -8.85) * mm, "end": v(12.93, -8.83) * mm});
            skLineSegment(sketch, "E957", {"start": v(12.93, -8.83) * mm, "end": v(12.82, -8.8) * mm});
            skLineSegment(sketch, "E958", {"start": v(12.82, -8.8) * mm, "end": v(12.72, -8.77) * mm});
            skLineSegment(sketch, "E959", {"start": v(12.72, -8.77) * mm, "end": v(12.61, -8.74) * mm});
            skLineSegment(sketch, "E960", {"start": v(12.61, -8.74) * mm, "end": v(12.57, -8.73) * mm});
            skLineSegment(sketch, "E961", {"start": v(12.57, -8.73) * mm, "end": v(12.54, -8.73) * mm});
            skLineSegment(sketch, "E962", {"start": v(12.54, -8.73) * mm, "end": v(12.52, -8.73) * mm});
            skLineSegment(sketch, "E963", {"start": v(12.52, -8.73) * mm, "end": v(12.5, -8.74) * mm});
            skLineSegment(sketch, "E964", {"start": v(12.5, -8.74) * mm, "end": v(12.17, -9.2) * mm});
            skLineSegment(sketch, "E965", {"start": v(12.17, -9.2) * mm, "end": v(12.17, -9.21) * mm});
            skLineSegment(sketch, "E966", {"start": v(12.17, -9.21) * mm, "end": v(12.18, -9.23) * mm});
            skLineSegment(sketch, "E967", {"start": v(12.18, -9.23) * mm, "end": v(12.19, -9.25) * mm});
            skLineSegment(sketch, "E968", {"start": v(12.19, -9.25) * mm, "end": v(12.2, -9.3) * mm});
            skLineSegment(sketch, "E969", {"start": v(12.2, -9.3) * mm, "end": v(12.27, -9.39) * mm});
            skLineSegment(sketch, "E970", {"start": v(12.27, -9.39) * mm, "end": v(12.33, -9.47) * mm});
            skLineSegment(sketch, "E971", {"start": v(12.33, -9.47) * mm, "end": v(12.4, -9.57) * mm});
            skLineSegment(sketch, "E972", {"start": v(12.4, -9.57) * mm, "end": v(12.43, -9.62) * mm});
            skLineSegment(sketch, "E973", {"start": v(12.43, -9.62) * mm, "end": v(12.52, -9.78) * mm});
            skLineSegment(sketch, "E974", {"start": v(12.52, -9.78) * mm, "end": v(12.53, -9.8) * mm});
            skLineSegment(sketch, "E975", {"start": v(12.53, -9.8) * mm, "end": v(12.64, -10) * mm});
            skLineSegment(sketch, "E976", {"start": v(12.64, -10) * mm, "end": v(12.65, -10.01) * mm});
            skLineSegment(sketch, "E977", {"start": v(12.65, -10.01) * mm, "end": v(12.65, -10.02) * mm});
            skLineSegment(sketch, "E978", {"start": v(12.65, -10.02) * mm, "end": v(12.74, -10.2) * mm});
            skLineSegment(sketch, "E979", {"start": v(12.74, -10.2) * mm, "end": v(12.75, -10.21) * mm});
            skLineSegment(sketch, "E980", {"start": v(12.75, -10.21) * mm, "end": v(12.78, -10.27) * mm});
            skLineSegment(sketch, "E981", {"start": v(12.78, -10.27) * mm, "end": v(12.9, -10.56) * mm});
            skLineSegment(sketch, "E982", {"start": v(12.9, -10.56) * mm, "end": v(12.93, -10.63) * mm});
            skLineSegment(sketch, "E983", {"start": v(12.93, -10.63) * mm, "end": v(12.93, -10.7) * mm});
            skLineSegment(sketch, "E984", {"start": v(12.93, -10.7) * mm, "end": v(12.77, -10.91) * mm});
            skLineSegment(sketch, "E985", {"start": v(12.77, -10.91) * mm, "end": v(12.59, -11.1) * mm});
            skLineSegment(sketch, "E986", {"start": v(12.59, -11.1) * mm, "end": v(12.52, -11.11) * mm});
            skLineSegment(sketch, "E987", {"start": v(12.52, -11.11) * mm, "end": v(12.44, -11.1) * mm});
            skLineSegment(sketch, "E988", {"start": v(12.44, -11.1) * mm, "end": v(12.14, -11.02) * mm});
            skLineSegment(sketch, "E989", {"start": v(12.14, -11.02) * mm, "end": v(12.08, -11) * mm});
            skLineSegment(sketch, "E990", {"start": v(12.08, -11) * mm, "end": v(12.06, -11) * mm});
            skLineSegment(sketch, "E991", {"start": v(12.06, -11) * mm, "end": v(11.87, -10.93) * mm});
            skLineSegment(sketch, "E992", {"start": v(11.87, -10.93) * mm, "end": v(11.87, -10.93) * mm});
            skLineSegment(sketch, "E993", {"start": v(11.87, -10.93) * mm, "end": v(11.85, -10.92) * mm});
            skLineSegment(sketch, "E994", {"start": v(11.85, -10.92) * mm, "end": v(11.63, -10.85) * mm});
            skLineSegment(sketch, "E995", {"start": v(11.63, -10.85) * mm, "end": v(11.62, -10.84) * mm});
            skLineSegment(sketch, "E996", {"start": v(11.62, -10.84) * mm, "end": v(11.45, -10.77) * mm});
            skLineSegment(sketch, "E997", {"start": v(11.45, -10.77) * mm, "end": v(11.4, -10.75) * mm});
            skLineSegment(sketch, "E998", {"start": v(11.4, -10.75) * mm, "end": v(11.28, -10.7) * mm});
            skLineSegment(sketch, "E999", {"start": v(11.28, -10.7) * mm, "end": v(11.2, -10.65) * mm});
            skLineSegment(sketch, "E1000", {"start": v(11.2, -10.65) * mm, "end": v(11.1, -10.6) * mm});
            skLineSegment(sketch, "E1001", {"start": v(11.1, -10.6) * mm, "end": v(11.05, -10.59) * mm});
            skLineSegment(sketch, "E1002", {"start": v(11.05, -10.59) * mm, "end": v(11.02, -10.58) * mm});
            skLineSegment(sketch, "E1003", {"start": v(11.02, -10.58) * mm, "end": v(11, -10.58) * mm});
            skLineSegment(sketch, "E1004", {"start": v(11, -10.58) * mm, "end": v(10.98, -10.58) * mm});
            skLineSegment(sketch, "E1005", {"start": v(10.98, -10.58) * mm, "end": v(10.58, -10.98) * mm});
            skLineSegment(sketch, "E1006", {"start": v(10.58, -10.98) * mm, "end": v(10.58, -11) * mm});
            skLineSegment(sketch, "E1007", {"start": v(10.58, -11) * mm, "end": v(10.58, -11.02) * mm});
            skLineSegment(sketch, "E1008", {"start": v(10.58, -11.02) * mm, "end": v(10.59, -11.05) * mm});
            skLineSegment(sketch, "E1009", {"start": v(10.59, -11.05) * mm, "end": v(10.6, -11.1) * mm});
            skLineSegment(sketch, "E1010", {"start": v(10.6, -11.1) * mm, "end": v(10.65, -11.2) * mm});
            skLineSegment(sketch, "E1011", {"start": v(10.65, -11.2) * mm, "end": v(10.7, -11.28) * mm});
            skLineSegment(sketch, "E1012", {"start": v(10.7, -11.28) * mm, "end": v(10.75, -11.4) * mm});
            skLineSegment(sketch, "E1013", {"start": v(10.75, -11.4) * mm, "end": v(10.77, -11.45) * mm});
            skLineSegment(sketch, "E1014", {"start": v(10.77, -11.45) * mm, "end": v(10.84, -11.62) * mm});
            skLineSegment(sketch, "E1015", {"start": v(10.84, -11.62) * mm, "end": v(10.85, -11.63) * mm});
            skLineSegment(sketch, "E1016", {"start": v(10.85, -11.63) * mm, "end": v(10.92, -11.85) * mm});
            skLineSegment(sketch, "E1017", {"start": v(10.92, -11.85) * mm, "end": v(10.93, -11.87) * mm});
            skLineSegment(sketch, "E1018", {"start": v(10.93, -11.87) * mm, "end": v(10.93, -11.87) * mm});
            skLineSegment(sketch, "E1019", {"start": v(10.93, -11.87) * mm, "end": v(11, -12.06) * mm});
            skLineSegment(sketch, "E1020", {"start": v(11, -12.06) * mm, "end": v(11, -12.08) * mm});
            skLineSegment(sketch, "E1021", {"start": v(11, -12.08) * mm, "end": v(11.02, -12.14) * mm});
            skLineSegment(sketch, "E1022", {"start": v(11.02, -12.14) * mm, "end": v(11.1, -12.44) * mm});
            skLineSegment(sketch, "E1023", {"start": v(11.1, -12.44) * mm, "end": v(11.11, -12.52) * mm});
            skLineSegment(sketch, "E1024", {"start": v(11.11, -12.52) * mm, "end": v(11.1, -12.59) * mm});
            skLineSegment(sketch, "E1025", {"start": v(11.1, -12.59) * mm, "end": v(10.91, -12.77) * mm});
            skLineSegment(sketch, "E1026", {"start": v(10.91, -12.77) * mm, "end": v(10.7, -12.93) * mm});
            skLineSegment(sketch, "E1027", {"start": v(10.7, -12.93) * mm, "end": v(10.63, -12.93) * mm});
            skLineSegment(sketch, "E1028", {"start": v(10.63, -12.93) * mm, "end": v(10.56, -12.9) * mm});
            skLineSegment(sketch, "E1029", {"start": v(10.56, -12.9) * mm, "end": v(10.27, -12.78) * mm});
            skLineSegment(sketch, "E1030", {"start": v(10.27, -12.78) * mm, "end": v(10.21, -12.75) * mm});
            skLineSegment(sketch, "E1031", {"start": v(10.21, -12.75) * mm, "end": v(10.2, -12.74) * mm});
            skLineSegment(sketch, "E1032", {"start": v(10.2, -12.74) * mm, "end": v(10.02, -12.65) * mm});
            skLineSegment(sketch, "E1033", {"start": v(10.02, -12.65) * mm, "end": v(10.01, -12.65) * mm});
            skLineSegment(sketch, "E1034", {"start": v(10.01, -12.65) * mm, "end": v(10, -12.64) * mm});
            skLineSegment(sketch, "E1035", {"start": v(10, -12.64) * mm, "end": v(9.8, -12.53) * mm});
            skLineSegment(sketch, "E1036", {"start": v(9.8, -12.53) * mm, "end": v(9.78, -12.52) * mm});
            skLineSegment(sketch, "E1037", {"start": v(9.78, -12.52) * mm, "end": v(9.62, -12.43) * mm});
            skLineSegment(sketch, "E1038", {"start": v(9.62, -12.43) * mm, "end": v(9.57, -12.4) * mm});
            skLineSegment(sketch, "E1039", {"start": v(9.57, -12.4) * mm, "end": v(9.47, -12.33) * mm});
            skLineSegment(sketch, "E1040", {"start": v(9.47, -12.33) * mm, "end": v(9.39, -12.27) * mm});
            skLineSegment(sketch, "E1041", {"start": v(9.39, -12.27) * mm, "end": v(9.3, -12.2) * mm});
            skLineSegment(sketch, "E1042", {"start": v(9.3, -12.2) * mm, "end": v(9.25, -12.19) * mm});
            skLineSegment(sketch, "E1043", {"start": v(9.25, -12.19) * mm, "end": v(9.23, -12.18) * mm});
            skLineSegment(sketch, "E1044", {"start": v(9.23, -12.18) * mm, "end": v(9.21, -12.17) * mm});
            skLineSegment(sketch, "E1045", {"start": v(9.21, -12.17) * mm, "end": v(9.2, -12.17) * mm});
            skLineSegment(sketch, "E1046", {"start": v(9.2, -12.17) * mm, "end": v(8.74, -12.5) * mm});
            skLineSegment(sketch, "E1047", {"start": v(8.74, -12.5) * mm, "end": v(8.73, -12.52) * mm});
            skLineSegment(sketch, "E1048", {"start": v(8.73, -12.52) * mm, "end": v(8.73, -12.54) * mm});
            skLineSegment(sketch, "E1049", {"start": v(8.73, -12.54) * mm, "end": v(8.73, -12.57) * mm});
            skLineSegment(sketch, "E1050", {"start": v(8.73, -12.57) * mm, "end": v(8.74, -12.61) * mm});
            skLineSegment(sketch, "E1051", {"start": v(8.74, -12.61) * mm, "end": v(8.77, -12.72) * mm});
            skLineSegment(sketch, "E1052", {"start": v(8.77, -12.72) * mm, "end": v(8.8, -12.82) * mm});
            skLineSegment(sketch, "E1053", {"start": v(8.8, -12.82) * mm, "end": v(8.83, -12.93) * mm});
            skLineSegment(sketch, "E1054", {"start": v(8.83, -12.93) * mm, "end": v(8.85, -13) * mm});
            skLineSegment(sketch, "E1055", {"start": v(8.85, -13) * mm, "end": v(8.89, -13.17) * mm});
            skLineSegment(sketch, "E1056", {"start": v(8.89, -13.17) * mm, "end": v(8.9, -13.19) * mm});
            skLineSegment(sketch, "E1057", {"start": v(8.9, -13.19) * mm, "end": v(8.94, -13.4) * mm});
            skLineSegment(sketch, "E1058", {"start": v(8.94, -13.4) * mm, "end": v(8.94, -13.43) * mm});
            skLineSegment(sketch, "E1059", {"start": v(8.94, -13.43) * mm, "end": v(8.94, -13.44) * mm});
            skLineSegment(sketch, "E1060", {"start": v(8.94, -13.44) * mm, "end": v(8.97, -13.63) * mm});
            skLineSegment(sketch, "E1061", {"start": v(8.97, -13.63) * mm, "end": v(8.97, -13.65) * mm});
            skLineSegment(sketch, "E1062", {"start": v(8.97, -13.65) * mm, "end": v(8.98, -13.72) * mm});
            skLineSegment(sketch, "E1063", {"start": v(8.98, -13.72) * mm, "end": v(9.02, -14.03) * mm});
            skLineSegment(sketch, "E1064", {"start": v(9.02, -14.03) * mm, "end": v(9.02, -14.1) * mm});
            skLineSegment(sketch, "E1065", {"start": v(9.02, -14.1) * mm, "end": v(9, -14.17) * mm});
            skLineSegment(sketch, "E1066", {"start": v(9, -14.17) * mm, "end": v(8.78, -14.32) * mm});
            skLineSegment(sketch, "E1067", {"start": v(8.78, -14.32) * mm, "end": v(8.54, -14.44) * mm});
            skLineSegment(sketch, "E1068", {"start": v(8.54, -14.44) * mm, "end": v(8.47, -14.44) * mm});
            skLineSegment(sketch, "E1069", {"start": v(8.47, -14.44) * mm, "end": v(8.4, -14.4) * mm});
            skLineSegment(sketch, "E1070", {"start": v(8.4, -14.4) * mm, "end": v(8.14, -14.23) * mm});
            skLineSegment(sketch, "E1071", {"start": v(8.14, -14.23) * mm, "end": v(8.1, -14.2) * mm});
            skLineSegment(sketch, "E1072", {"start": v(8.1, -14.2) * mm, "end": v(8.08, -14.18) * mm});
            skLineSegment(sketch, "E1073", {"start": v(8.08, -14.18) * mm, "end": v(7.91, -14.07) * mm});
            skLineSegment(sketch, "E1074", {"start": v(7.91, -14.07) * mm, "end": v(7.9, -14.06) * mm});
            skLineSegment(sketch, "E1075", {"start": v(7.9, -14.06) * mm, "end": v(7.89, -14.05) * mm});
            skLineSegment(sketch, "E1076", {"start": v(7.89, -14.05) * mm, "end": v(7.71, -13.91) * mm});
            skLineSegment(sketch, "E1077", {"start": v(7.71, -13.91) * mm, "end": v(7.7, -13.9) * mm});
            skLineSegment(sketch, "E1078", {"start": v(7.7, -13.9) * mm, "end": v(7.56, -13.78) * mm});
            skLineSegment(sketch, "E1079", {"start": v(7.56, -13.78) * mm, "end": v(7.51, -13.74) * mm});
            skLineSegment(sketch, "E1080", {"start": v(7.51, -13.74) * mm, "end": v(7.43, -13.66) * mm});
            skLineSegment(sketch, "E1081", {"start": v(7.43, -13.66) * mm, "end": v(7.35, -13.6) * mm});
            skLineSegment(sketch, "E1082", {"start": v(7.35, -13.6) * mm, "end": v(7.27, -13.51) * mm});
            skLineSegment(sketch, "E1083", {"start": v(7.27, -13.51) * mm, "end": v(7.23, -13.48) * mm});
            skLineSegment(sketch, "E1084", {"start": v(7.23, -13.48) * mm, "end": v(7.21, -13.47) * mm});
            skLineSegment(sketch, "E1085", {"start": v(7.21, -13.47) * mm, "end": v(7.2, -13.46) * mm});
            skLineSegment(sketch, "E1086", {"start": v(7.2, -13.46) * mm, "end": v(7.17, -13.46) * mm});
            skLineSegment(sketch, "E1087", {"start": v(7.17, -13.46) * mm, "end": v(6.67, -13.72) * mm});
            skLineSegment(sketch, "E1088", {"start": v(6.67, -13.72) * mm, "end": v(6.66, -13.73) * mm});
            skLineSegment(sketch, "E1089", {"start": v(6.66, -13.73) * mm, "end": v(6.66, -13.75) * mm});
            skLineSegment(sketch, "E1090", {"start": v(6.66, -13.75) * mm, "end": v(6.66, -13.78) * mm});
            skLineSegment(sketch, "E1091", {"start": v(6.66, -13.78) * mm, "end": v(6.66, -13.83) * mm});
            skLineSegment(sketch, "E1092", {"start": v(6.66, -13.83) * mm, "end": v(6.67, -13.93) * mm});
            skLineSegment(sketch, "E1093", {"start": v(6.67, -13.93) * mm, "end": v(6.69, -14.04) * mm});
            skLineSegment(sketch, "E1094", {"start": v(6.69, -14.04) * mm, "end": v(6.7, -14.15) * mm});
            skLineSegment(sketch, "E1095", {"start": v(6.7, -14.15) * mm, "end": v(6.7, -14.22) * mm});
            skLineSegment(sketch, "E1096", {"start": v(6.7, -14.22) * mm, "end": v(6.72, -14.4) * mm});
            skLineSegment(sketch, "E1097", {"start": v(6.72, -14.4) * mm, "end": v(6.72, -14.42) * mm});
            skLineSegment(sketch, "E1098", {"start": v(6.72, -14.42) * mm, "end": v(6.73, -14.64) * mm});
            skLineSegment(sketch, "E1099", {"start": v(6.73, -14.64) * mm, "end": v(6.73, -14.66) * mm});
            skLineSegment(sketch, "E1100", {"start": v(6.73, -14.66) * mm, "end": v(6.73, -14.67) * mm});
            skLineSegment(sketch, "E1101", {"start": v(6.73, -14.67) * mm, "end": v(6.73, -14.87) * mm});
            skLineSegment(sketch, "E1102", {"start": v(6.73, -14.87) * mm, "end": v(6.73, -14.89) * mm});
            skLineSegment(sketch, "E1103", {"start": v(6.73, -14.89) * mm, "end": v(6.73, -14.95) * mm});
            skLineSegment(sketch, "E1104", {"start": v(6.73, -14.95) * mm, "end": v(6.71, -15.27) * mm});
            skLineSegment(sketch, "E1105", {"start": v(6.71, -15.27) * mm, "end": v(6.7, -15.34) * mm});
            skLineSegment(sketch, "E1106", {"start": v(6.7, -15.34) * mm, "end": v(6.66, -15.4) * mm});
            skLineSegment(sketch, "E1107", {"start": v(6.66, -15.4) * mm, "end": v(6.43, -15.52) * mm});
            skLineSegment(sketch, "E1108", {"start": v(6.43, -15.52) * mm, "end": v(6.18, -15.6) * mm});
            skLineSegment(sketch, "E1109", {"start": v(6.18, -15.6) * mm, "end": v(6.11, -15.58) * mm});
            skLineSegment(sketch, "E1110", {"start": v(6.11, -15.58) * mm, "end": v(6.05, -15.54) * mm});
            skLineSegment(sketch, "E1111", {"start": v(6.05, -15.54) * mm, "end": v(5.82, -15.33) * mm});
            skLineSegment(sketch, "E1112", {"start": v(5.82, -15.33) * mm, "end": v(5.77, -15.29) * mm});
            skLineSegment(sketch, "E1113", {"start": v(5.77, -15.29) * mm, "end": v(5.76, -15.27) * mm});
            skLineSegment(sketch, "E1114", {"start": v(5.76, -15.27) * mm, "end": v(5.61, -15.13) * mm});
            skLineSegment(sketch, "E1115", {"start": v(5.61, -15.13) * mm, "end": v(5.61, -15.13) * mm});
            skLineSegment(sketch, "E1116", {"start": v(5.61, -15.13) * mm, "end": v(5.6, -15.11) * mm});
            skLineSegment(sketch, "E1117", {"start": v(5.6, -15.11) * mm, "end": v(5.44, -14.95) * mm});
            skLineSegment(sketch, "E1118", {"start": v(5.44, -14.95) * mm, "end": v(5.43, -14.93) * mm});
            skLineSegment(sketch, "E1119", {"start": v(5.43, -14.93) * mm, "end": v(5.3, -14.8) * mm});
            skLineSegment(sketch, "E1120", {"start": v(5.3, -14.8) * mm, "end": v(5.27, -14.75) * mm});
            skLineSegment(sketch, "E1121", {"start": v(5.27, -14.75) * mm, "end": v(5.2, -14.65) * mm});
            skLineSegment(sketch, "E1122", {"start": v(5.2, -14.65) * mm, "end": v(5.13, -14.57) * mm});
            skLineSegment(sketch, "E1123", {"start": v(5.13, -14.57) * mm, "end": v(5.07, -14.48) * mm});
            skLineSegment(sketch, "E1124", {"start": v(5.07, -14.48) * mm, "end": v(5.04, -14.45) * mm});
            skLineSegment(sketch, "E1125", {"start": v(5.04, -14.45) * mm, "end": v(5.02, -14.43) * mm});
            skLineSegment(sketch, "E1126", {"start": v(5.02, -14.43) * mm, "end": v(5, -14.42) * mm});
            skLineSegment(sketch, "E1127", {"start": v(5, -14.42) * mm, "end": v(4.98, -14.42) * mm});
            skLineSegment(sketch, "E1128", {"start": v(4.98, -14.42) * mm, "end": v(4.44, -14.6) * mm});
            skLineSegment(sketch, "E1129", {"start": v(4.44, -14.6) * mm, "end": v(4.43, -14.6) * mm});
            skLineSegment(sketch, "E1130", {"start": v(4.43, -14.6) * mm, "end": v(4.43, -14.62) * mm});
            skLineSegment(sketch, "E1131", {"start": v(4.43, -14.62) * mm, "end": v(4.42, -14.65) * mm});
            skLineSegment(sketch, "E1132", {"start": v(4.42, -14.65) * mm, "end": v(4.41, -14.7) * mm});
            skLineSegment(sketch, "E1133", {"start": v(4.41, -14.7) * mm, "end": v(4.41, -14.8) * mm});
            skLineSegment(sketch, "E1134", {"start": v(4.41, -14.8) * mm, "end": v(4.4, -14.91) * mm});
            skLineSegment(sketch, "E1135", {"start": v(4.4, -14.91) * mm, "end": v(4.4, -15.03) * mm});
            skLineSegment(sketch, "E1136", {"start": v(4.4, -15.03) * mm, "end": v(4.4, -15.09) * mm});
            skLineSegment(sketch, "E1137", {"start": v(4.4, -15.09) * mm, "end": v(4.38, -15.27) * mm});
            skLineSegment(sketch, "E1138", {"start": v(4.38, -15.27) * mm, "end": v(4.38, -15.3) * mm});
            skLineSegment(sketch, "E1139", {"start": v(4.38, -15.3) * mm, "end": v(4.36, -15.51) * mm});
            skLineSegment(sketch, "E1140", {"start": v(4.36, -15.51) * mm, "end": v(4.35, -15.54) * mm});
            skLineSegment(sketch, "E1141", {"start": v(4.35, -15.54) * mm, "end": v(4.35, -15.54) * mm});
            skLineSegment(sketch, "E1142", {"start": v(4.35, -15.54) * mm, "end": v(4.32, -15.74) * mm});
            skLineSegment(sketch, "E1143", {"start": v(4.32, -15.74) * mm, "end": v(4.32, -15.76) * mm});
            skLineSegment(sketch, "E1144", {"start": v(4.32, -15.76) * mm, "end": v(4.3, -15.82) * mm});
            skLineSegment(sketch, "E1145", {"start": v(4.3, -15.82) * mm, "end": v(4.24, -16.13) * mm});
            skLineSegment(sketch, "E1146", {"start": v(4.24, -16.13) * mm, "end": v(4.22, -16.2) * mm});
            skLineSegment(sketch, "E1147", {"start": v(4.22, -16.2) * mm, "end": v(4.17, -16.26) * mm});
            skLineSegment(sketch, "E1148", {"start": v(4.17, -16.26) * mm, "end": v(3.92, -16.34) * mm});
            skLineSegment(sketch, "E1149", {"start": v(3.92, -16.34) * mm, "end": v(3.66, -16.38) * mm});
            skLineSegment(sketch, "E1150", {"start": v(3.66, -16.38) * mm, "end": v(3.6, -16.35) * mm});
            skLineSegment(sketch, "E1151", {"start": v(3.6, -16.35) * mm, "end": v(3.54, -16.3) * mm});
            skLineSegment(sketch, "E1152", {"start": v(3.54, -16.3) * mm, "end": v(3.35, -16.05) * mm});
            skLineSegment(sketch, "E1153", {"start": v(3.35, -16.05) * mm, "end": v(3.3, -16) * mm});
            skLineSegment(sketch, "E1154", {"start": v(3.3, -16) * mm, "end": v(3.3, -15.98) * mm});
            skLineSegment(sketch, "E1155", {"start": v(3.3, -15.98) * mm, "end": v(3.18, -15.82) * mm});
            skLineSegment(sketch, "E1156", {"start": v(3.18, -15.82) * mm, "end": v(3.18, -15.82) * mm});
            skLineSegment(sketch, "E1157", {"start": v(3.18, -15.82) * mm, "end": v(3.16, -15.8) * mm});
            skLineSegment(sketch, "E1158", {"start": v(3.16, -15.8) * mm, "end": v(3.04, -15.61) * mm});
            skLineSegment(sketch, "E1159", {"start": v(3.04, -15.61) * mm, "end": v(3.03, -15.6) * mm});
            skLineSegment(sketch, "E1160", {"start": v(3.03, -15.6) * mm, "end": v(2.93, -15.44) * mm});
            skLineSegment(sketch, "E1161", {"start": v(2.93, -15.44) * mm, "end": v(2.9, -15.39) * mm});
            skLineSegment(sketch, "E1162", {"start": v(2.9, -15.39) * mm, "end": v(2.84, -15.29) * mm});
            skLineSegment(sketch, "E1163", {"start": v(2.84, -15.29) * mm, "end": v(2.8, -15.2) * mm});
            skLineSegment(sketch, "E1164", {"start": v(2.8, -15.2) * mm, "end": v(2.74, -15.1) * mm});
            skLineSegment(sketch, "E1165", {"start": v(2.74, -15.1) * mm, "end": v(2.71, -15.06) * mm});
            skLineSegment(sketch, "E1166", {"start": v(2.71, -15.06) * mm, "end": v(2.7, -15.04) * mm});
            skLineSegment(sketch, "E1167", {"start": v(2.7, -15.04) * mm, "end": v(2.68, -15.03) * mm});
            skLineSegment(sketch, "E1168", {"start": v(2.68, -15.03) * mm, "end": v(2.66, -15.02) * mm});
            skLineSegment(sketch, "E1169", {"start": v(2.66, -15.02) * mm, "end": v(2.1, -15.1) * mm});
            skLineSegment(sketch, "E1170", {"start": v(2.1, -15.1) * mm, "end": v(2.1, -15.12) * mm});
            skLineSegment(sketch, "E1171", {"start": v(2.1, -15.12) * mm, "end": v(2.08, -15.14) * mm});
            skLineSegment(sketch, "E1172", {"start": v(2.08, -15.14) * mm, "end": v(2.07, -15.16) * mm});
            skLineSegment(sketch, "E1173", {"start": v(2.07, -15.16) * mm, "end": v(2.06, -15.2) * mm});
            skLineSegment(sketch, "E1174", {"start": v(2.06, -15.2) * mm, "end": v(2.04, -15.32) * mm});
            skLineSegment(sketch, "E1175", {"start": v(2.04, -15.32) * mm, "end": v(2.02, -15.42) * mm});
            skLineSegment(sketch, "E1176", {"start": v(2.02, -15.42) * mm, "end": v(2, -15.53) * mm});
            skLineSegment(sketch, "E1177", {"start": v(2, -15.53) * mm, "end": v(1.99, -15.6) * mm});
            skLineSegment(sketch, "E1178", {"start": v(1.99, -15.6) * mm, "end": v(1.94, -15.77) * mm});
            skLineSegment(sketch, "E1179", {"start": v(1.94, -15.77) * mm, "end": v(1.94, -15.79) * mm});
            skLineSegment(sketch, "E1180", {"start": v(1.94, -15.79) * mm, "end": v(1.87, -16) * mm});
            skLineSegment(sketch, "E1181", {"start": v(1.87, -16) * mm, "end": v(1.87, -16.03) * mm});
            skLineSegment(sketch, "E1182", {"start": v(1.87, -16.03) * mm, "end": v(1.87, -16.03) * mm});
            skLineSegment(sketch, "E1183", {"start": v(1.87, -16.03) * mm, "end": v(1.8, -16.22) * mm});
            skLineSegment(sketch, "E1184", {"start": v(1.8, -16.22) * mm, "end": v(1.8, -16.24) * mm});
            skLineSegment(sketch, "E1185", {"start": v(1.8, -16.24) * mm, "end": v(1.78, -16.3) * mm});
            skLineSegment(sketch, "E1186", {"start": v(1.78, -16.3) * mm, "end": v(1.66, -16.6) * mm});
            skLineSegment(sketch, "E1187", {"start": v(1.66, -16.6) * mm, "end": v(1.63, -16.66) * mm});
            skLineSegment(sketch, "E1188", {"start": v(1.63, -16.66) * mm, "end": v(1.58, -16.7) * mm});
            skLineSegment(sketch, "E1189", {"start": v(1.58, -16.7) * mm, "end": v(1.32, -16.75) * mm});
            skLineSegment(sketch, "E1190", {"start": v(1.32, -16.75) * mm, "end": v(1.06, -16.75) * mm});
            skLineSegment(sketch, "E1191", {"start": v(1.06, -16.75) * mm, "end": v(1, -16.7) * mm});
            skLineSegment(sketch, "E1192", {"start": v(1, -16.7) * mm, "end": v(0.95, -16.65) * mm});
            skLineSegment(sketch, "E1193", {"start": v(0.95, -16.65) * mm, "end": v(0.8, -16.38) * mm});
            skLineSegment(sketch, "E1194", {"start": v(0.8, -16.38) * mm, "end": v(0.76, -16.32) * mm});
            skLineSegment(sketch, "E1195", {"start": v(0.76, -16.32) * mm, "end": v(0.76, -16.3) * mm});
            skLineSegment(sketch, "E1196", {"start": v(0.76, -16.3) * mm, "end": v(0.66, -16.12) * mm});
            skLineSegment(sketch, "E1197", {"start": v(0.66, -16.12) * mm, "end": v(0.66, -16.12) * mm});
            skLineSegment(sketch, "E1198", {"start": v(0.66, -16.12) * mm, "end": v(0.65, -16.1) * mm});
            skLineSegment(sketch, "E1199", {"start": v(0.65, -16.1) * mm, "end": v(0.56, -15.9) * mm});
            skLineSegment(sketch, "E1200", {"start": v(0.56, -15.9) * mm, "end": v(0.55, -15.88) * mm});
            skLineSegment(sketch, "E1201", {"start": v(0.55, -15.88) * mm, "end": v(0.48, -15.71) * mm});
            skLineSegment(sketch, "E1202", {"start": v(0.48, -15.71) * mm, "end": v(0.46, -15.65) * mm});
            skLineSegment(sketch, "E1203", {"start": v(0.46, -15.65) * mm, "end": v(0.41, -15.54) * mm});
            skLineSegment(sketch, "E1204", {"start": v(0.41, -15.54) * mm, "end": v(0.38, -15.45) * mm});
            skLineSegment(sketch, "E1205", {"start": v(0.38, -15.45) * mm, "end": v(0.34, -15.34) * mm});
            skLineSegment(sketch, "E1206", {"start": v(0.34, -15.34) * mm, "end": v(0.32, -15.3) * mm});
            skLineSegment(sketch, "E1207", {"start": v(0.32, -15.3) * mm, "end": v(0.31, -15.27) * mm});
            skLineSegment(sketch, "E1208", {"start": v(0.31, -15.27) * mm, "end": v(0.3, -15.26) * mm});
            skLineSegment(sketch, "E1209", {"start": v(0.3, -15.26) * mm, "end": v(0.28, -15.25) * mm});
            skLineSegment(sketch, "E1210", {"start": v(0.28, -15.25) * mm, "end": v(-0.28, -15.25) * mm});
            skLineSegment(sketch, "E1211", {"start": v(-0.28, -15.25) * mm, "end": v(-0.3, -15.26) * mm});
            skLineSegment(sketch, "E1212", {"start": v(-0.3, -15.26) * mm, "end": v(-0.31, -15.27) * mm});
            skLineSegment(sketch, "E1213", {"start": v(-0.31, -15.27) * mm, "end": v(-0.32, -15.3) * mm});
            skLineSegment(sketch, "E1214", {"start": v(-0.32, -15.3) * mm, "end": v(-0.34, -15.34) * mm});
            skLineSegment(sketch, "E1215", {"start": v(-0.34, -15.34) * mm, "end": v(-0.38, -15.45) * mm});
            skLineSegment(sketch, "E1216", {"start": v(-0.38, -15.45) * mm, "end": v(-0.41, -15.54) * mm});
            skLineSegment(sketch, "E1217", {"start": v(-0.41, -15.54) * mm, "end": v(-0.46, -15.65) * mm});
            skLineSegment(sketch, "E1218", {"start": v(-0.46, -15.65) * mm, "end": v(-0.48, -15.71) * mm});
            skLineSegment(sketch, "E1219", {"start": v(-0.48, -15.71) * mm, "end": v(-0.55, -15.88) * mm});
            skLineSegment(sketch, "E1220", {"start": v(-0.55, -15.88) * mm, "end": v(-0.56, -15.9) * mm});
            skLineSegment(sketch, "E1221", {"start": v(-0.56, -15.9) * mm, "end": v(-0.65, -16.1) * mm});
            skLineSegment(sketch, "E1222", {"start": v(-0.65, -16.1) * mm, "end": v(-0.66, -16.12) * mm});
            skLineSegment(sketch, "E1223", {"start": v(-0.66, -16.12) * mm, "end": v(-0.66, -16.12) * mm});
            skLineSegment(sketch, "E1224", {"start": v(-0.66, -16.12) * mm, "end": v(-0.76, -16.3) * mm});
            skLineSegment(sketch, "E1225", {"start": v(-0.76, -16.3) * mm, "end": v(-0.76, -16.32) * mm});
            skLineSegment(sketch, "E1226", {"start": v(-0.76, -16.32) * mm, "end": v(-0.8, -16.38) * mm});
            skLineSegment(sketch, "E1227", {"start": v(-0.8, -16.38) * mm, "end": v(-0.95, -16.65) * mm});
            skLineSegment(sketch, "E1228", {"start": v(-0.95, -16.65) * mm, "end": v(-1, -16.7) * mm});
            skLineSegment(sketch, "E1229", {"start": v(-1, -16.7) * mm, "end": v(-1.06, -16.75) * mm});
            skLineSegment(sketch, "E1230", {"start": v(-1.06, -16.75) * mm, "end": v(-1.32, -16.75) * mm});
            skLineSegment(sketch, "E1231", {"start": v(-1.32, -16.75) * mm, "end": v(-1.58, -16.7) * mm});
            skLineSegment(sketch, "E1232", {"start": v(-1.58, -16.7) * mm, "end": v(-1.63, -16.66) * mm});
            skLineSegment(sketch, "E1233", {"start": v(-1.63, -16.66) * mm, "end": v(-1.66, -16.6) * mm});
            skLineSegment(sketch, "E1234", {"start": v(-1.66, -16.6) * mm, "end": v(-1.78, -16.3) * mm});
            skLineSegment(sketch, "E1235", {"start": v(-1.78, -16.3) * mm, "end": v(-1.8, -16.24) * mm});
            skLineSegment(sketch, "E1236", {"start": v(-1.8, -16.24) * mm, "end": v(-1.8, -16.22) * mm});
            skLineSegment(sketch, "E1237", {"start": v(-1.8, -16.22) * mm, "end": v(-1.87, -16.03) * mm});
            skLineSegment(sketch, "E1238", {"start": v(-1.87, -16.03) * mm, "end": v(-1.87, -16.03) * mm});
            skLineSegment(sketch, "E1239", {"start": v(-1.87, -16.03) * mm, "end": v(-1.87, -16) * mm});
            skLineSegment(sketch, "E1240", {"start": v(-1.87, -16) * mm, "end": v(-1.94, -15.79) * mm});
            skLineSegment(sketch, "E1241", {"start": v(-1.94, -15.79) * mm, "end": v(-1.94, -15.77) * mm});
            skLineSegment(sketch, "E1242", {"start": v(-1.94, -15.77) * mm, "end": v(-1.99, -15.6) * mm});
            skLineSegment(sketch, "E1243", {"start": v(-1.99, -15.6) * mm, "end": v(-2, -15.53) * mm});
            skLineSegment(sketch, "E1244", {"start": v(-2, -15.53) * mm, "end": v(-2.02, -15.42) * mm});
            skLineSegment(sketch, "E1245", {"start": v(-2.02, -15.42) * mm, "end": v(-2.04, -15.32) * mm});
            skLineSegment(sketch, "E1246", {"start": v(-2.04, -15.32) * mm, "end": v(-2.06, -15.2) * mm});
            skLineSegment(sketch, "E1247", {"start": v(-2.06, -15.2) * mm, "end": v(-2.07, -15.16) * mm});
            skLineSegment(sketch, "E1248", {"start": v(-2.07, -15.16) * mm, "end": v(-2.08, -15.14) * mm});
            skLineSegment(sketch, "E1249", {"start": v(-2.08, -15.14) * mm, "end": v(-2.1, -15.12) * mm});
            skLineSegment(sketch, "E1250", {"start": v(-2.1, -15.12) * mm, "end": v(-2.1, -15.1) * mm});
            skLineSegment(sketch, "E1251", {"start": v(-2.1, -15.1) * mm, "end": v(-2.66, -15.02) * mm});
            skLineSegment(sketch, "E1252", {"start": v(-2.66, -15.02) * mm, "end": v(-2.68, -15.03) * mm});
            skLineSegment(sketch, "E1253", {"start": v(-2.68, -15.03) * mm, "end": v(-2.7, -15.04) * mm});
            skLineSegment(sketch, "E1254", {"start": v(-2.7, -15.04) * mm, "end": v(-2.71, -15.06) * mm});
            skLineSegment(sketch, "E1255", {"start": v(-2.71, -15.06) * mm, "end": v(-2.74, -15.1) * mm});
            skLineSegment(sketch, "E1256", {"start": v(-2.74, -15.1) * mm, "end": v(-2.8, -15.2) * mm});
            skLineSegment(sketch, "E1257", {"start": v(-2.8, -15.2) * mm, "end": v(-2.84, -15.29) * mm});
            skLineSegment(sketch, "E1258", {"start": v(-2.84, -15.29) * mm, "end": v(-2.9, -15.39) * mm});
            skLineSegment(sketch, "E1259", {"start": v(-2.9, -15.39) * mm, "end": v(-2.93, -15.44) * mm});
            skLineSegment(sketch, "E1260", {"start": v(-2.93, -15.44) * mm, "end": v(-3.03, -15.6) * mm});
            skLineSegment(sketch, "E1261", {"start": v(-3.03, -15.6) * mm, "end": v(-3.04, -15.61) * mm});
            skLineSegment(sketch, "E1262", {"start": v(-3.04, -15.61) * mm, "end": v(-3.16, -15.8) * mm});
            skLineSegment(sketch, "E1263", {"start": v(-3.16, -15.8) * mm, "end": v(-3.18, -15.82) * mm});
            skLineSegment(sketch, "E1264", {"start": v(-3.18, -15.82) * mm, "end": v(-3.18, -15.82) * mm});
            skLineSegment(sketch, "E1265", {"start": v(-3.18, -15.82) * mm, "end": v(-3.3, -15.98) * mm});
            skLineSegment(sketch, "E1266", {"start": v(-3.3, -15.98) * mm, "end": v(-3.3, -16) * mm});
            skLineSegment(sketch, "E1267", {"start": v(-3.3, -16) * mm, "end": v(-3.35, -16.05) * mm});
            skLineSegment(sketch, "E1268", {"start": v(-3.35, -16.05) * mm, "end": v(-3.54, -16.3) * mm});
            skLineSegment(sketch, "E1269", {"start": v(-3.54, -16.3) * mm, "end": v(-3.6, -16.35) * mm});
            skLineSegment(sketch, "E1270", {"start": v(-3.6, -16.35) * mm, "end": v(-3.66, -16.38) * mm});
            skLineSegment(sketch, "E1271", {"start": v(-3.66, -16.38) * mm, "end": v(-3.92, -16.34) * mm});
            skLineSegment(sketch, "E1272", {"start": v(-3.92, -16.34) * mm, "end": v(-4.17, -16.26) * mm});
            skLineSegment(sketch, "E1273", {"start": v(-4.17, -16.26) * mm, "end": v(-4.22, -16.2) * mm});
            skLineSegment(sketch, "E1274", {"start": v(-4.22, -16.2) * mm, "end": v(-4.24, -16.13) * mm});
            skLineSegment(sketch, "E1275", {"start": v(-4.24, -16.13) * mm, "end": v(-4.3, -15.82) * mm});
            skLineSegment(sketch, "E1276", {"start": v(-4.3, -15.82) * mm, "end": v(-4.32, -15.76) * mm});
            skLineSegment(sketch, "E1277", {"start": v(-4.32, -15.76) * mm, "end": v(-4.32, -15.74) * mm});
            skLineSegment(sketch, "E1278", {"start": v(-4.32, -15.74) * mm, "end": v(-4.35, -15.54) * mm});
            skLineSegment(sketch, "E1279", {"start": v(-4.35, -15.54) * mm, "end": v(-4.35, -15.54) * mm});
            skLineSegment(sketch, "E1280", {"start": v(-4.35, -15.54) * mm, "end": v(-4.36, -15.51) * mm});
            skLineSegment(sketch, "E1281", {"start": v(-4.36, -15.51) * mm, "end": v(-4.38, -15.3) * mm});
            skLineSegment(sketch, "E1282", {"start": v(-4.38, -15.3) * mm, "end": v(-4.38, -15.27) * mm});
            skLineSegment(sketch, "E1283", {"start": v(-4.38, -15.27) * mm, "end": v(-4.4, -15.09) * mm});
            skLineSegment(sketch, "E1284", {"start": v(-4.4, -15.09) * mm, "end": v(-4.4, -15.03) * mm});
            skLineSegment(sketch, "E1285", {"start": v(-4.4, -15.03) * mm, "end": v(-4.4, -14.91) * mm});
            skLineSegment(sketch, "E1286", {"start": v(-4.4, -14.91) * mm, "end": v(-4.41, -14.8) * mm});
            skLineSegment(sketch, "E1287", {"start": v(-4.41, -14.8) * mm, "end": v(-4.41, -14.7) * mm});
            skLineSegment(sketch, "E1288", {"start": v(-4.41, -14.7) * mm, "end": v(-4.42, -14.65) * mm});
            skLineSegment(sketch, "E1289", {"start": v(-4.42, -14.65) * mm, "end": v(-4.43, -14.62) * mm});
            skLineSegment(sketch, "E1290", {"start": v(-4.43, -14.62) * mm, "end": v(-4.43, -14.6) * mm});
            skLineSegment(sketch, "E1291", {"start": v(-4.43, -14.6) * mm, "end": v(-4.44, -14.6) * mm});
            skLineSegment(sketch, "E1292", {"start": v(-4.44, -14.6) * mm, "end": v(-4.98, -14.42) * mm});
            skLineSegment(sketch, "E1293", {"start": v(-4.98, -14.42) * mm, "end": v(-5, -14.42) * mm});
            skLineSegment(sketch, "E1294", {"start": v(-5, -14.42) * mm, "end": v(-5.02, -14.43) * mm});
            skLineSegment(sketch, "E1295", {"start": v(-5.02, -14.43) * mm, "end": v(-5.04, -14.45) * mm});
            skLineSegment(sketch, "E1296", {"start": v(-5.04, -14.45) * mm, "end": v(-5.07, -14.48) * mm});
            skLineSegment(sketch, "E1297", {"start": v(-5.07, -14.48) * mm, "end": v(-5.13, -14.57) * mm});
            skLineSegment(sketch, "E1298", {"start": v(-5.13, -14.57) * mm, "end": v(-5.2, -14.65) * mm});
            skLineSegment(sketch, "E1299", {"start": v(-5.2, -14.65) * mm, "end": v(-5.27, -14.75) * mm});
            skLineSegment(sketch, "E1300", {"start": v(-5.27, -14.75) * mm, "end": v(-5.3, -14.8) * mm});
            skLineSegment(sketch, "E1301", {"start": v(-5.3, -14.8) * mm, "end": v(-5.43, -14.93) * mm});
            skLineSegment(sketch, "E1302", {"start": v(-5.43, -14.93) * mm, "end": v(-5.44, -14.95) * mm});
            skLineSegment(sketch, "E1303", {"start": v(-5.44, -14.95) * mm, "end": v(-5.6, -15.11) * mm});
            skLineSegment(sketch, "E1304", {"start": v(-5.6, -15.11) * mm, "end": v(-5.61, -15.13) * mm});
            skLineSegment(sketch, "E1305", {"start": v(-5.61, -15.13) * mm, "end": v(-5.61, -15.13) * mm});
            skLineSegment(sketch, "E1306", {"start": v(-5.61, -15.13) * mm, "end": v(-5.76, -15.27) * mm});
            skLineSegment(sketch, "E1307", {"start": v(-5.76, -15.27) * mm, "end": v(-5.77, -15.29) * mm});
            skLineSegment(sketch, "E1308", {"start": v(-5.77, -15.29) * mm, "end": v(-5.82, -15.33) * mm});
            skLineSegment(sketch, "E1309", {"start": v(-5.82, -15.33) * mm, "end": v(-6.05, -15.54) * mm});
            skLineSegment(sketch, "E1310", {"start": v(-6.05, -15.54) * mm, "end": v(-6.11, -15.58) * mm});
            skLineSegment(sketch, "E1311", {"start": v(-6.11, -15.58) * mm, "end": v(-6.18, -15.6) * mm});
            skLineSegment(sketch, "E1312", {"start": v(-6.18, -15.6) * mm, "end": v(-6.43, -15.52) * mm});
            skLineSegment(sketch, "E1313", {"start": v(-6.43, -15.52) * mm, "end": v(-6.66, -15.4) * mm});
            skLineSegment(sketch, "E1314", {"start": v(-6.66, -15.4) * mm, "end": v(-6.7, -15.34) * mm});
            skLineSegment(sketch, "E1315", {"start": v(-6.7, -15.34) * mm, "end": v(-6.71, -15.27) * mm});
            skLineSegment(sketch, "E1316", {"start": v(-6.71, -15.27) * mm, "end": v(-6.73, -14.95) * mm});
            skLineSegment(sketch, "E1317", {"start": v(-6.73, -14.95) * mm, "end": v(-6.73, -14.89) * mm});
            skLineSegment(sketch, "E1318", {"start": v(-6.73, -14.89) * mm, "end": v(-6.73, -14.87) * mm});
            skLineSegment(sketch, "E1319", {"start": v(-6.73, -14.87) * mm, "end": v(-6.73, -14.67) * mm});
            skLineSegment(sketch, "E1320", {"start": v(-6.73, -14.67) * mm, "end": v(-6.73, -14.66) * mm});
            skLineSegment(sketch, "E1321", {"start": v(-6.73, -14.66) * mm, "end": v(-6.73, -14.64) * mm});
            skLineSegment(sketch, "E1322", {"start": v(-6.73, -14.64) * mm, "end": v(-6.72, -14.42) * mm});
            skLineSegment(sketch, "E1323", {"start": v(-6.72, -14.42) * mm, "end": v(-6.72, -14.4) * mm});
            skLineSegment(sketch, "E1324", {"start": v(-6.72, -14.4) * mm, "end": v(-6.7, -14.22) * mm});
            skLineSegment(sketch, "E1325", {"start": v(-6.7, -14.22) * mm, "end": v(-6.7, -14.15) * mm});
            skLineSegment(sketch, "E1326", {"start": v(-6.7, -14.15) * mm, "end": v(-6.69, -14.04) * mm});
            skLineSegment(sketch, "E1327", {"start": v(-6.69, -14.04) * mm, "end": v(-6.67, -13.93) * mm});
            skLineSegment(sketch, "E1328", {"start": v(-6.67, -13.93) * mm, "end": v(-6.66, -13.83) * mm});
            skLineSegment(sketch, "E1329", {"start": v(-6.66, -13.83) * mm, "end": v(-6.66, -13.78) * mm});
            skLineSegment(sketch, "E1330", {"start": v(-6.66, -13.78) * mm, "end": v(-6.66, -13.75) * mm});
            skLineSegment(sketch, "E1331", {"start": v(-6.66, -13.75) * mm, "end": v(-6.66, -13.73) * mm});
            skLineSegment(sketch, "E1332", {"start": v(-6.66, -13.73) * mm, "end": v(-6.67, -13.72) * mm});
            skLineSegment(sketch, "E1333", {"start": v(-6.67, -13.72) * mm, "end": v(-7.17, -13.46) * mm});
            skLineSegment(sketch, "E1334", {"start": v(-7.17, -13.46) * mm, "end": v(-7.2, -13.46) * mm});
            skLineSegment(sketch, "E1335", {"start": v(-7.2, -13.46) * mm, "end": v(-7.21, -13.47) * mm});
            skLineSegment(sketch, "E1336", {"start": v(-7.21, -13.47) * mm, "end": v(-7.23, -13.48) * mm});
            skLineSegment(sketch, "E1337", {"start": v(-7.23, -13.48) * mm, "end": v(-7.27, -13.51) * mm});
            skLineSegment(sketch, "E1338", {"start": v(-7.27, -13.51) * mm, "end": v(-7.35, -13.6) * mm});
            skLineSegment(sketch, "E1339", {"start": v(-7.35, -13.6) * mm, "end": v(-7.43, -13.66) * mm});
            skLineSegment(sketch, "E1340", {"start": v(-7.43, -13.66) * mm, "end": v(-7.51, -13.74) * mm});
            skLineSegment(sketch, "E1341", {"start": v(-7.51, -13.74) * mm, "end": v(-7.56, -13.78) * mm});
            skLineSegment(sketch, "E1342", {"start": v(-7.56, -13.78) * mm, "end": v(-7.7, -13.9) * mm});
            skLineSegment(sketch, "E1343", {"start": v(-7.7, -13.9) * mm, "end": v(-7.71, -13.91) * mm});
            skLineSegment(sketch, "E1344", {"start": v(-7.71, -13.91) * mm, "end": v(-7.89, -14.05) * mm});
            skLineSegment(sketch, "E1345", {"start": v(-7.89, -14.05) * mm, "end": v(-7.9, -14.06) * mm});
            skLineSegment(sketch, "E1346", {"start": v(-7.9, -14.06) * mm, "end": v(-7.91, -14.07) * mm});
            skLineSegment(sketch, "E1347", {"start": v(-7.91, -14.07) * mm, "end": v(-8.08, -14.18) * mm});
            skLineSegment(sketch, "E1348", {"start": v(-8.08, -14.18) * mm, "end": v(-8.1, -14.2) * mm});
            skLineSegment(sketch, "E1349", {"start": v(-8.1, -14.2) * mm, "end": v(-8.14, -14.23) * mm});
            skLineSegment(sketch, "E1350", {"start": v(-8.14, -14.23) * mm, "end": v(-8.4, -14.4) * mm});
            skLineSegment(sketch, "E1351", {"start": v(-8.4, -14.4) * mm, "end": v(-8.47, -14.44) * mm});
            skLineSegment(sketch, "E1352", {"start": v(-8.47, -14.44) * mm, "end": v(-8.54, -14.44) * mm});
            skLineSegment(sketch, "E1353", {"start": v(-8.54, -14.44) * mm, "end": v(-8.78, -14.32) * mm});
            skLineSegment(sketch, "E1354", {"start": v(-8.78, -14.32) * mm, "end": v(-9, -14.17) * mm});
            skLineSegment(sketch, "E1355", {"start": v(-9, -14.17) * mm, "end": v(-9.02, -14.1) * mm});
            skLineSegment(sketch, "E1356", {"start": v(-9.02, -14.1) * mm, "end": v(-9.02, -14.03) * mm});
            skLineSegment(sketch, "E1357", {"start": v(-9.02, -14.03) * mm, "end": v(-8.98, -13.72) * mm});
            skLineSegment(sketch, "E1358", {"start": v(-8.98, -13.72) * mm, "end": v(-8.97, -13.65) * mm});
            skLineSegment(sketch, "E1359", {"start": v(-8.97, -13.65) * mm, "end": v(-8.97, -13.63) * mm});
            skLineSegment(sketch, "E1360", {"start": v(-8.97, -13.63) * mm, "end": v(-8.94, -13.44) * mm});
            skLineSegment(sketch, "E1361", {"start": v(-8.94, -13.44) * mm, "end": v(-8.94, -13.43) * mm});
            skLineSegment(sketch, "E1362", {"start": v(-8.94, -13.43) * mm, "end": v(-8.94, -13.4) * mm});
            skLineSegment(sketch, "E1363", {"start": v(-8.94, -13.4) * mm, "end": v(-8.9, -13.19) * mm});
            skLineSegment(sketch, "E1364", {"start": v(-8.9, -13.19) * mm, "end": v(-8.89, -13.17) * mm});
            skLineSegment(sketch, "E1365", {"start": v(-8.89, -13.17) * mm, "end": v(-8.85, -13) * mm});
            skLineSegment(sketch, "E1366", {"start": v(-8.85, -13) * mm, "end": v(-8.83, -12.93) * mm});
            skLineSegment(sketch, "E1367", {"start": v(-8.83, -12.93) * mm, "end": v(-8.8, -12.82) * mm});
            skLineSegment(sketch, "E1368", {"start": v(-8.8, -12.82) * mm, "end": v(-8.77, -12.72) * mm});
            skLineSegment(sketch, "E1369", {"start": v(-8.77, -12.72) * mm, "end": v(-8.74, -12.61) * mm});
            skLineSegment(sketch, "E1370", {"start": v(-8.74, -12.61) * mm, "end": v(-8.73, -12.57) * mm});
            skLineSegment(sketch, "E1371", {"start": v(-8.73, -12.57) * mm, "end": v(-8.73, -12.54) * mm});
            skLineSegment(sketch, "E1372", {"start": v(-8.73, -12.54) * mm, "end": v(-8.73, -12.52) * mm});
            skLineSegment(sketch, "E1373", {"start": v(-8.73, -12.52) * mm, "end": v(-8.74, -12.5) * mm});
            skLineSegment(sketch, "E1374", {"start": v(-8.74, -12.5) * mm, "end": v(-9.2, -12.17) * mm});
            skLineSegment(sketch, "E1375", {"start": v(-9.2, -12.17) * mm, "end": v(-9.21, -12.17) * mm});
            skLineSegment(sketch, "E1376", {"start": v(-9.21, -12.17) * mm, "end": v(-9.23, -12.18) * mm});
            skLineSegment(sketch, "E1377", {"start": v(-9.23, -12.18) * mm, "end": v(-9.25, -12.19) * mm});
            skLineSegment(sketch, "E1378", {"start": v(-9.25, -12.19) * mm, "end": v(-9.3, -12.2) * mm});
            skLineSegment(sketch, "E1379", {"start": v(-9.3, -12.2) * mm, "end": v(-9.39, -12.27) * mm});
            skLineSegment(sketch, "E1380", {"start": v(-9.39, -12.27) * mm, "end": v(-9.47, -12.33) * mm});
            skLineSegment(sketch, "E1381", {"start": v(-9.47, -12.33) * mm, "end": v(-9.57, -12.4) * mm});
            skLineSegment(sketch, "E1382", {"start": v(-9.57, -12.4) * mm, "end": v(-9.62, -12.43) * mm});
            skLineSegment(sketch, "E1383", {"start": v(-9.62, -12.43) * mm, "end": v(-9.78, -12.52) * mm});
            skLineSegment(sketch, "E1384", {"start": v(-9.78, -12.52) * mm, "end": v(-9.8, -12.53) * mm});
            skLineSegment(sketch, "E1385", {"start": v(-9.8, -12.53) * mm, "end": v(-10, -12.64) * mm});
            skLineSegment(sketch, "E1386", {"start": v(-10, -12.64) * mm, "end": v(-10.01, -12.65) * mm});
            skLineSegment(sketch, "E1387", {"start": v(-10.01, -12.65) * mm, "end": v(-10.02, -12.65) * mm});
            skLineSegment(sketch, "E1388", {"start": v(-10.02, -12.65) * mm, "end": v(-10.2, -12.74) * mm});
            skLineSegment(sketch, "E1389", {"start": v(-10.2, -12.74) * mm, "end": v(-10.21, -12.75) * mm});
            skLineSegment(sketch, "E1390", {"start": v(-10.21, -12.75) * mm, "end": v(-10.27, -12.78) * mm});
            skLineSegment(sketch, "E1391", {"start": v(-10.27, -12.78) * mm, "end": v(-10.56, -12.9) * mm});
            skLineSegment(sketch, "E1392", {"start": v(-10.56, -12.9) * mm, "end": v(-10.63, -12.93) * mm});
            skLineSegment(sketch, "E1393", {"start": v(-10.63, -12.93) * mm, "end": v(-10.7, -12.93) * mm});
            skLineSegment(sketch, "E1394", {"start": v(-10.7, -12.93) * mm, "end": v(-10.91, -12.77) * mm});
            skLineSegment(sketch, "E1395", {"start": v(-10.91, -12.77) * mm, "end": v(-11.1, -12.59) * mm});
            skLineSegment(sketch, "E1396", {"start": v(-11.1, -12.59) * mm, "end": v(-11.11, -12.52) * mm});
            skLineSegment(sketch, "E1397", {"start": v(-11.11, -12.52) * mm, "end": v(-11.1, -12.44) * mm});
            skLineSegment(sketch, "E1398", {"start": v(-11.1, -12.44) * mm, "end": v(-11.02, -12.14) * mm});
            skLineSegment(sketch, "E1399", {"start": v(-11.02, -12.14) * mm, "end": v(-11, -12.08) * mm});
            skLineSegment(sketch, "E1400", {"start": v(-11, -12.08) * mm, "end": v(-11, -12.06) * mm});
            skLineSegment(sketch, "E1401", {"start": v(-11, -12.06) * mm, "end": v(-10.93, -11.87) * mm});
            skLineSegment(sketch, "E1402", {"start": v(-10.93, -11.87) * mm, "end": v(-10.93, -11.87) * mm});
            skLineSegment(sketch, "E1403", {"start": v(-10.93, -11.87) * mm, "end": v(-10.92, -11.85) * mm});
            skLineSegment(sketch, "E1404", {"start": v(-10.92, -11.85) * mm, "end": v(-10.85, -11.63) * mm});
            skLineSegment(sketch, "E1405", {"start": v(-10.85, -11.63) * mm, "end": v(-10.84, -11.62) * mm});
            skLineSegment(sketch, "E1406", {"start": v(-10.84, -11.62) * mm, "end": v(-10.77, -11.45) * mm});
            skLineSegment(sketch, "E1407", {"start": v(-10.77, -11.45) * mm, "end": v(-10.75, -11.4) * mm});
            skLineSegment(sketch, "E1408", {"start": v(-10.75, -11.4) * mm, "end": v(-10.7, -11.28) * mm});
            skLineSegment(sketch, "E1409", {"start": v(-10.7, -11.28) * mm, "end": v(-10.65, -11.2) * mm});
            skLineSegment(sketch, "E1410", {"start": v(-10.65, -11.2) * mm, "end": v(-10.6, -11.1) * mm});
            skLineSegment(sketch, "E1411", {"start": v(-10.6, -11.1) * mm, "end": v(-10.59, -11.05) * mm});
            skLineSegment(sketch, "E1412", {"start": v(-10.59, -11.05) * mm, "end": v(-10.58, -11.02) * mm});
            skLineSegment(sketch, "E1413", {"start": v(-10.58, -11.02) * mm, "end": v(-10.58, -11) * mm});
            skLineSegment(sketch, "E1414", {"start": v(-10.58, -11) * mm, "end": v(-10.58, -10.98) * mm});
            skLineSegment(sketch, "E1415", {"start": v(-10.58, -10.98) * mm, "end": v(-10.98, -10.58) * mm});
            skLineSegment(sketch, "E1416", {"start": v(-10.98, -10.58) * mm, "end": v(-11, -10.58) * mm});
            skLineSegment(sketch, "E1417", {"start": v(-11, -10.58) * mm, "end": v(-11.02, -10.58) * mm});
            skLineSegment(sketch, "E1418", {"start": v(-11.02, -10.58) * mm, "end": v(-11.05, -10.59) * mm});
            skLineSegment(sketch, "E1419", {"start": v(-11.05, -10.59) * mm, "end": v(-11.1, -10.6) * mm});
            skLineSegment(sketch, "E1420", {"start": v(-11.1, -10.6) * mm, "end": v(-11.2, -10.65) * mm});
            skLineSegment(sketch, "E1421", {"start": v(-11.2, -10.65) * mm, "end": v(-11.28, -10.7) * mm});
            skLineSegment(sketch, "E1422", {"start": v(-11.28, -10.7) * mm, "end": v(-11.4, -10.75) * mm});
            skLineSegment(sketch, "E1423", {"start": v(-11.4, -10.75) * mm, "end": v(-11.45, -10.77) * mm});
            skLineSegment(sketch, "E1424", {"start": v(-11.45, -10.77) * mm, "end": v(-11.62, -10.84) * mm});
            skLineSegment(sketch, "E1425", {"start": v(-11.62, -10.84) * mm, "end": v(-11.63, -10.85) * mm});
            skLineSegment(sketch, "E1426", {"start": v(-11.63, -10.85) * mm, "end": v(-11.85, -10.92) * mm});
            skLineSegment(sketch, "E1427", {"start": v(-11.85, -10.92) * mm, "end": v(-11.87, -10.93) * mm});
            skLineSegment(sketch, "E1428", {"start": v(-11.87, -10.93) * mm, "end": v(-11.87, -10.93) * mm});
            skLineSegment(sketch, "E1429", {"start": v(-11.87, -10.93) * mm, "end": v(-12.06, -11) * mm});
            skLineSegment(sketch, "E1430", {"start": v(-12.06, -11) * mm, "end": v(-12.08, -11) * mm});
            skLineSegment(sketch, "E1431", {"start": v(-12.08, -11) * mm, "end": v(-12.14, -11.02) * mm});
            skLineSegment(sketch, "E1432", {"start": v(-12.14, -11.02) * mm, "end": v(-12.44, -11.1) * mm});
            skLineSegment(sketch, "E1433", {"start": v(-12.44, -11.1) * mm, "end": v(-12.52, -11.11) * mm});
            skLineSegment(sketch, "E1434", {"start": v(-12.52, -11.11) * mm, "end": v(-12.59, -11.1) * mm});
            skLineSegment(sketch, "E1435", {"start": v(-12.59, -11.1) * mm, "end": v(-12.77, -10.91) * mm});
            skLineSegment(sketch, "E1436", {"start": v(-12.77, -10.91) * mm, "end": v(-12.93, -10.7) * mm});
            skLineSegment(sketch, "E1437", {"start": v(-12.93, -10.7) * mm, "end": v(-12.93, -10.63) * mm});
            skLineSegment(sketch, "E1438", {"start": v(-12.93, -10.63) * mm, "end": v(-12.9, -10.56) * mm});
            skLineSegment(sketch, "E1439", {"start": v(-12.9, -10.56) * mm, "end": v(-12.78, -10.27) * mm});
            skLineSegment(sketch, "E1440", {"start": v(-12.78, -10.27) * mm, "end": v(-12.75, -10.21) * mm});
            skLineSegment(sketch, "E1441", {"start": v(-12.75, -10.21) * mm, "end": v(-12.74, -10.2) * mm});
            skLineSegment(sketch, "E1442", {"start": v(-12.74, -10.2) * mm, "end": v(-12.65, -10.02) * mm});
            skLineSegment(sketch, "E1443", {"start": v(-12.65, -10.02) * mm, "end": v(-12.65, -10.01) * mm});
            skLineSegment(sketch, "E1444", {"start": v(-12.65, -10.01) * mm, "end": v(-12.64, -10) * mm});
            skLineSegment(sketch, "E1445", {"start": v(-12.64, -10) * mm, "end": v(-12.53, -9.8) * mm});
            skLineSegment(sketch, "E1446", {"start": v(-12.53, -9.8) * mm, "end": v(-12.52, -9.78) * mm});
            skLineSegment(sketch, "E1447", {"start": v(-12.52, -9.78) * mm, "end": v(-12.43, -9.62) * mm});
            skLineSegment(sketch, "E1448", {"start": v(-12.43, -9.62) * mm, "end": v(-12.4, -9.57) * mm});
            skLineSegment(sketch, "E1449", {"start": v(-12.4, -9.57) * mm, "end": v(-12.33, -9.47) * mm});
            skLineSegment(sketch, "E1450", {"start": v(-12.33, -9.47) * mm, "end": v(-12.27, -9.39) * mm});
            skLineSegment(sketch, "E1451", {"start": v(-12.27, -9.39) * mm, "end": v(-12.2, -9.3) * mm});
            skLineSegment(sketch, "E1452", {"start": v(-12.2, -9.3) * mm, "end": v(-12.19, -9.25) * mm});
            skLineSegment(sketch, "E1453", {"start": v(-12.19, -9.25) * mm, "end": v(-12.18, -9.23) * mm});
            skLineSegment(sketch, "E1454", {"start": v(-12.18, -9.23) * mm, "end": v(-12.17, -9.21) * mm});
            skLineSegment(sketch, "E1455", {"start": v(-12.17, -9.21) * mm, "end": v(-12.17, -9.2) * mm});
            skLineSegment(sketch, "E1456", {"start": v(-12.17, -9.2) * mm, "end": v(-12.5, -8.74) * mm});
            skLineSegment(sketch, "E1457", {"start": v(-12.5, -8.74) * mm, "end": v(-12.52, -8.73) * mm});
            skLineSegment(sketch, "E1458", {"start": v(-12.52, -8.73) * mm, "end": v(-12.54, -8.73) * mm});
            skLineSegment(sketch, "E1459", {"start": v(-12.54, -8.73) * mm, "end": v(-12.57, -8.73) * mm});
            skLineSegment(sketch, "E1460", {"start": v(-12.57, -8.73) * mm, "end": v(-12.61, -8.74) * mm});
            skLineSegment(sketch, "E1461", {"start": v(-12.61, -8.74) * mm, "end": v(-12.72, -8.77) * mm});
            skLineSegment(sketch, "E1462", {"start": v(-12.72, -8.77) * mm, "end": v(-12.82, -8.8) * mm});
            skLineSegment(sketch, "E1463", {"start": v(-12.82, -8.8) * mm, "end": v(-12.93, -8.83) * mm});
            skLineSegment(sketch, "E1464", {"start": v(-12.93, -8.83) * mm, "end": v(-13, -8.85) * mm});
            skLineSegment(sketch, "E1465", {"start": v(-13, -8.85) * mm, "end": v(-13.17, -8.89) * mm});
            skLineSegment(sketch, "E1466", {"start": v(-13.17, -8.89) * mm, "end": v(-13.19, -8.9) * mm});
            skLineSegment(sketch, "E1467", {"start": v(-13.19, -8.9) * mm, "end": v(-13.4, -8.94) * mm});
            skLineSegment(sketch, "E1468", {"start": v(-13.4, -8.94) * mm, "end": v(-13.43, -8.94) * mm});
            skLineSegment(sketch, "E1469", {"start": v(-13.43, -8.94) * mm, "end": v(-13.44, -8.94) * mm});
            skLineSegment(sketch, "E1470", {"start": v(-13.44, -8.94) * mm, "end": v(-13.63, -8.97) * mm});
            skLineSegment(sketch, "E1471", {"start": v(-13.63, -8.97) * mm, "end": v(-13.65, -8.97) * mm});
            skLineSegment(sketch, "E1472", {"start": v(-13.65, -8.97) * mm, "end": v(-13.72, -8.98) * mm});
            skLineSegment(sketch, "E1473", {"start": v(-13.72, -8.98) * mm, "end": v(-14.03, -9.02) * mm});
            skLineSegment(sketch, "E1474", {"start": v(-14.03, -9.02) * mm, "end": v(-14.1, -9.02) * mm});
            skLineSegment(sketch, "E1475", {"start": v(-14.1, -9.02) * mm, "end": v(-14.17, -9) * mm});
            skLineSegment(sketch, "E1476", {"start": v(-14.17, -9) * mm, "end": v(-14.32, -8.78) * mm});
            skLineSegment(sketch, "E1477", {"start": v(-14.32, -8.78) * mm, "end": v(-14.44, -8.54) * mm});
            skLineSegment(sketch, "E1478", {"start": v(-14.44, -8.54) * mm, "end": v(-14.44, -8.47) * mm});
            skLineSegment(sketch, "E1479", {"start": v(-14.44, -8.47) * mm, "end": v(-14.4, -8.4) * mm});
            skLineSegment(sketch, "E1480", {"start": v(-14.4, -8.4) * mm, "end": v(-14.23, -8.14) * mm});
            skLineSegment(sketch, "E1481", {"start": v(-14.23, -8.14) * mm, "end": v(-14.2, -8.1) * mm});
            skLineSegment(sketch, "E1482", {"start": v(-14.2, -8.1) * mm, "end": v(-14.18, -8.08) * mm});
            skLineSegment(sketch, "E1483", {"start": v(-14.18, -8.08) * mm, "end": v(-14.07, -7.91) * mm});
            skLineSegment(sketch, "E1484", {"start": v(-14.07, -7.91) * mm, "end": v(-14.06, -7.9) * mm});
            skLineSegment(sketch, "E1485", {"start": v(-14.06, -7.9) * mm, "end": v(-14.05, -7.89) * mm});
            skLineSegment(sketch, "E1486", {"start": v(-14.05, -7.89) * mm, "end": v(-13.91, -7.71) * mm});
            skLineSegment(sketch, "E1487", {"start": v(-13.91, -7.71) * mm, "end": v(-13.9, -7.7) * mm});
            skLineSegment(sketch, "E1488", {"start": v(-13.9, -7.7) * mm, "end": v(-13.78, -7.56) * mm});
            skLineSegment(sketch, "E1489", {"start": v(-13.78, -7.56) * mm, "end": v(-13.74, -7.51) * mm});
            skLineSegment(sketch, "E1490", {"start": v(-13.74, -7.51) * mm, "end": v(-13.66, -7.43) * mm});
            skLineSegment(sketch, "E1491", {"start": v(-13.66, -7.43) * mm, "end": v(-13.6, -7.35) * mm});
            skLineSegment(sketch, "E1492", {"start": v(-13.6, -7.35) * mm, "end": v(-13.51, -7.27) * mm});
            skLineSegment(sketch, "E1493", {"start": v(-13.51, -7.27) * mm, "end": v(-13.48, -7.23) * mm});
            skLineSegment(sketch, "E1494", {"start": v(-13.48, -7.23) * mm, "end": v(-13.47, -7.21) * mm});
            skLineSegment(sketch, "E1495", {"start": v(-13.47, -7.21) * mm, "end": v(-13.46, -7.2) * mm});
            skLineSegment(sketch, "E1496", {"start": v(-13.46, -7.2) * mm, "end": v(-13.46, -7.17) * mm});
            skLineSegment(sketch, "E1497", {"start": v(-13.46, -7.17) * mm, "end": v(-13.72, -6.67) * mm});
            skLineSegment(sketch, "E1498", {"start": v(-13.72, -6.67) * mm, "end": v(-13.73, -6.66) * mm});
            skLineSegment(sketch, "E1499", {"start": v(-13.73, -6.66) * mm, "end": v(-13.75, -6.66) * mm});
            skLineSegment(sketch, "E1500", {"start": v(-13.75, -6.66) * mm, "end": v(-13.78, -6.66) * mm});
            skLineSegment(sketch, "E1501", {"start": v(-13.78, -6.66) * mm, "end": v(-13.83, -6.66) * mm});
            skLineSegment(sketch, "E1502", {"start": v(-13.83, -6.66) * mm, "end": v(-13.93, -6.67) * mm});
            skLineSegment(sketch, "E1503", {"start": v(-13.93, -6.67) * mm, "end": v(-14.04, -6.69) * mm});
            skLineSegment(sketch, "E1504", {"start": v(-14.04, -6.69) * mm, "end": v(-14.15, -6.7) * mm});
            skLineSegment(sketch, "E1505", {"start": v(-14.15, -6.7) * mm, "end": v(-14.22, -6.7) * mm});
            skLineSegment(sketch, "E1506", {"start": v(-14.22, -6.7) * mm, "end": v(-14.4, -6.72) * mm});
            skLineSegment(sketch, "E1507", {"start": v(-14.4, -6.72) * mm, "end": v(-14.42, -6.72) * mm});
            skLineSegment(sketch, "E1508", {"start": v(-14.42, -6.72) * mm, "end": v(-14.64, -6.73) * mm});
            skLineSegment(sketch, "E1509", {"start": v(-14.64, -6.73) * mm, "end": v(-14.66, -6.73) * mm});
            skLineSegment(sketch, "E1510", {"start": v(-14.66, -6.73) * mm, "end": v(-14.67, -6.73) * mm});
            skLineSegment(sketch, "E1511", {"start": v(-14.67, -6.73) * mm, "end": v(-14.87, -6.73) * mm});
            skLineSegment(sketch, "E1512", {"start": v(-14.87, -6.73) * mm, "end": v(-14.89, -6.73) * mm});
            skLineSegment(sketch, "E1513", {"start": v(-14.89, -6.73) * mm, "end": v(-14.95, -6.73) * mm});
            skLineSegment(sketch, "E1514", {"start": v(-14.95, -6.73) * mm, "end": v(-15.27, -6.71) * mm});
            skLineSegment(sketch, "E1515", {"start": v(-15.27, -6.71) * mm, "end": v(-15.34, -6.7) * mm});
            skLineSegment(sketch, "E1516", {"start": v(-15.34, -6.7) * mm, "end": v(-15.4, -6.66) * mm});
            skLineSegment(sketch, "E1517", {"start": v(-15.4, -6.66) * mm, "end": v(-15.52, -6.43) * mm});
            skLineSegment(sketch, "E1518", {"start": v(-15.52, -6.43) * mm, "end": v(-15.6, -6.18) * mm});
            skLineSegment(sketch, "E1519", {"start": v(-15.6, -6.18) * mm, "end": v(-15.58, -6.11) * mm});
            skLineSegment(sketch, "E1520", {"start": v(-15.58, -6.11) * mm, "end": v(-15.54, -6.05) * mm});
            skLineSegment(sketch, "E1521", {"start": v(-15.54, -6.05) * mm, "end": v(-15.33, -5.82) * mm});
            skLineSegment(sketch, "E1522", {"start": v(-15.33, -5.82) * mm, "end": v(-15.29, -5.77) * mm});
            skLineSegment(sketch, "E1523", {"start": v(-15.29, -5.77) * mm, "end": v(-15.27, -5.76) * mm});
            skLineSegment(sketch, "E1524", {"start": v(-15.27, -5.76) * mm, "end": v(-15.13, -5.61) * mm});
            skLineSegment(sketch, "E1525", {"start": v(-15.13, -5.61) * mm, "end": v(-15.13, -5.61) * mm});
            skLineSegment(sketch, "E1526", {"start": v(-15.13, -5.61) * mm, "end": v(-15.11, -5.6) * mm});
            skLineSegment(sketch, "E1527", {"start": v(-15.11, -5.6) * mm, "end": v(-14.95, -5.44) * mm});
            skLineSegment(sketch, "E1528", {"start": v(-14.95, -5.44) * mm, "end": v(-14.93, -5.43) * mm});
            skLineSegment(sketch, "E1529", {"start": v(-14.93, -5.43) * mm, "end": v(-14.8, -5.3) * mm});
            skLineSegment(sketch, "E1530", {"start": v(-14.8, -5.3) * mm, "end": v(-14.75, -5.27) * mm});
            skLineSegment(sketch, "E1531", {"start": v(-14.75, -5.27) * mm, "end": v(-14.65, -5.2) * mm});
            skLineSegment(sketch, "E1532", {"start": v(-14.65, -5.2) * mm, "end": v(-14.57, -5.13) * mm});
            skLineSegment(sketch, "E1533", {"start": v(-14.57, -5.13) * mm, "end": v(-14.48, -5.07) * mm});
            skLineSegment(sketch, "E1534", {"start": v(-14.48, -5.07) * mm, "end": v(-14.45, -5.04) * mm});
            skLineSegment(sketch, "E1535", {"start": v(-14.45, -5.04) * mm, "end": v(-14.43, -5.02) * mm});
            skLineSegment(sketch, "E1536", {"start": v(-14.43, -5.02) * mm, "end": v(-14.42, -5) * mm});
            skLineSegment(sketch, "E1537", {"start": v(-14.42, -5) * mm, "end": v(-14.42, -4.98) * mm});
            skLineSegment(sketch, "E1538", {"start": v(-14.42, -4.98) * mm, "end": v(-14.6, -4.44) * mm});
            skLineSegment(sketch, "E1539", {"start": v(-14.6, -4.44) * mm, "end": v(-14.6, -4.43) * mm});
            skLineSegment(sketch, "E1540", {"start": v(-14.6, -4.43) * mm, "end": v(-14.62, -4.43) * mm});
            skLineSegment(sketch, "E1541", {"start": v(-14.62, -4.43) * mm, "end": v(-14.65, -4.42) * mm});
            skLineSegment(sketch, "E1542", {"start": v(-14.65, -4.42) * mm, "end": v(-14.7, -4.41) * mm});
            skLineSegment(sketch, "E1543", {"start": v(-14.7, -4.41) * mm, "end": v(-14.8, -4.41) * mm});
            skLineSegment(sketch, "E1544", {"start": v(-14.8, -4.41) * mm, "end": v(-14.91, -4.4) * mm});
            skLineSegment(sketch, "E1545", {"start": v(-14.91, -4.4) * mm, "end": v(-15.03, -4.4) * mm});
            skLineSegment(sketch, "E1546", {"start": v(-15.03, -4.4) * mm, "end": v(-15.09, -4.4) * mm});
            skLineSegment(sketch, "E1547", {"start": v(-15.09, -4.4) * mm, "end": v(-15.27, -4.38) * mm});
            skLineSegment(sketch, "E1548", {"start": v(-15.27, -4.38) * mm, "end": v(-15.3, -4.38) * mm});
            skLineSegment(sketch, "E1549", {"start": v(-15.3, -4.38) * mm, "end": v(-15.51, -4.36) * mm});
            skLineSegment(sketch, "E1550", {"start": v(-15.51, -4.36) * mm, "end": v(-15.54, -4.35) * mm});
            skLineSegment(sketch, "E1551", {"start": v(-15.54, -4.35) * mm, "end": v(-15.54, -4.35) * mm});
            skLineSegment(sketch, "E1552", {"start": v(-15.54, -4.35) * mm, "end": v(-15.74, -4.32) * mm});
            skLineSegment(sketch, "E1553", {"start": v(-15.74, -4.32) * mm, "end": v(-15.76, -4.32) * mm});
            skLineSegment(sketch, "E1554", {"start": v(-15.76, -4.32) * mm, "end": v(-15.82, -4.3) * mm});
            skLineSegment(sketch, "E1555", {"start": v(-15.82, -4.3) * mm, "end": v(-16.13, -4.24) * mm});
            skLineSegment(sketch, "E1556", {"start": v(-16.13, -4.24) * mm, "end": v(-16.2, -4.22) * mm});
            skLineSegment(sketch, "E1557", {"start": v(-16.2, -4.22) * mm, "end": v(-16.26, -4.17) * mm});
            skLineSegment(sketch, "E1558", {"start": v(-16.26, -4.17) * mm, "end": v(-16.34, -3.92) * mm});
            skLineSegment(sketch, "E1559", {"start": v(-16.34, -3.92) * mm, "end": v(-16.38, -3.66) * mm});
            skLineSegment(sketch, "E1560", {"start": v(-16.38, -3.66) * mm, "end": v(-16.35, -3.6) * mm});
            skLineSegment(sketch, "E1561", {"start": v(-16.35, -3.6) * mm, "end": v(-16.3, -3.54) * mm});
            skLineSegment(sketch, "E1562", {"start": v(-16.3, -3.54) * mm, "end": v(-16.05, -3.35) * mm});
            skLineSegment(sketch, "E1563", {"start": v(-16.05, -3.35) * mm, "end": v(-16, -3.3) * mm});
            skLineSegment(sketch, "E1564", {"start": v(-16, -3.3) * mm, "end": v(-15.98, -3.3) * mm});
            skLineSegment(sketch, "E1565", {"start": v(-15.98, -3.3) * mm, "end": v(-15.82, -3.18) * mm});
            skLineSegment(sketch, "E1566", {"start": v(-15.82, -3.18) * mm, "end": v(-15.82, -3.18) * mm});
            skLineSegment(sketch, "E1567", {"start": v(-15.82, -3.18) * mm, "end": v(-15.8, -3.16) * mm});
            skLineSegment(sketch, "E1568", {"start": v(-15.8, -3.16) * mm, "end": v(-15.61, -3.04) * mm});
            skLineSegment(sketch, "E1569", {"start": v(-15.61, -3.04) * mm, "end": v(-15.6, -3.03) * mm});
            skLineSegment(sketch, "E1570", {"start": v(-15.6, -3.03) * mm, "end": v(-15.44, -2.93) * mm});
            skLineSegment(sketch, "E1571", {"start": v(-15.44, -2.93) * mm, "end": v(-15.39, -2.9) * mm});
            skLineSegment(sketch, "E1572", {"start": v(-15.39, -2.9) * mm, "end": v(-15.29, -2.84) * mm});
            skLineSegment(sketch, "E1573", {"start": v(-15.29, -2.84) * mm, "end": v(-15.2, -2.8) * mm});
            skLineSegment(sketch, "E1574", {"start": v(-15.2, -2.8) * mm, "end": v(-15.1, -2.74) * mm});
            skLineSegment(sketch, "E1575", {"start": v(-15.1, -2.74) * mm, "end": v(-15.06, -2.71) * mm});
            skLineSegment(sketch, "E1576", {"start": v(-15.06, -2.71) * mm, "end": v(-15.04, -2.7) * mm});
            skLineSegment(sketch, "E1577", {"start": v(-15.04, -2.7) * mm, "end": v(-15.03, -2.68) * mm});
            skLineSegment(sketch, "E1578", {"start": v(-15.03, -2.68) * mm, "end": v(-15.02, -2.66) * mm});
            skLineSegment(sketch, "E1579", {"start": v(-15.02, -2.66) * mm, "end": v(-15.1, -2.1) * mm});
            skLineSegment(sketch, "E1580", {"start": v(-15.1, -2.1) * mm, "end": v(-15.12, -2.1) * mm});
            skLineSegment(sketch, "E1581", {"start": v(-15.12, -2.1) * mm, "end": v(-15.14, -2.08) * mm});
            skLineSegment(sketch, "E1582", {"start": v(-15.14, -2.08) * mm, "end": v(-15.16, -2.07) * mm});
            skLineSegment(sketch, "E1583", {"start": v(-15.16, -2.07) * mm, "end": v(-15.2, -2.06) * mm});
            skLineSegment(sketch, "E1584", {"start": v(-15.2, -2.06) * mm, "end": v(-15.32, -2.04) * mm});
            skLineSegment(sketch, "E1585", {"start": v(-15.32, -2.04) * mm, "end": v(-15.42, -2.02) * mm});
            skLineSegment(sketch, "E1586", {"start": v(-15.42, -2.02) * mm, "end": v(-15.53, -2) * mm});
            skLineSegment(sketch, "E1587", {"start": v(-15.53, -2) * mm, "end": v(-15.6, -1.99) * mm});
            skLineSegment(sketch, "E1588", {"start": v(-15.6, -1.99) * mm, "end": v(-15.77, -1.94) * mm});
            skLineSegment(sketch, "E1589", {"start": v(-15.77, -1.94) * mm, "end": v(-15.79, -1.94) * mm});
            skLineSegment(sketch, "E1590", {"start": v(-15.79, -1.94) * mm, "end": v(-16, -1.87) * mm});
            skLineSegment(sketch, "E1591", {"start": v(-16, -1.87) * mm, "end": v(-16.03, -1.87) * mm});
            skLineSegment(sketch, "E1592", {"start": v(-16.03, -1.87) * mm, "end": v(-16.03, -1.87) * mm});
            skLineSegment(sketch, "E1593", {"start": v(-16.03, -1.87) * mm, "end": v(-16.22, -1.8) * mm});
            skLineSegment(sketch, "E1594", {"start": v(-16.22, -1.8) * mm, "end": v(-16.24, -1.8) * mm});
            skLineSegment(sketch, "E1595", {"start": v(-16.24, -1.8) * mm, "end": v(-16.3, -1.78) * mm});
            skLineSegment(sketch, "E1596", {"start": v(-16.3, -1.78) * mm, "end": v(-16.6, -1.66) * mm});
            skLineSegment(sketch, "E1597", {"start": v(-16.6, -1.66) * mm, "end": v(-16.66, -1.63) * mm});
            skLineSegment(sketch, "E1598", {"start": v(-16.66, -1.63) * mm, "end": v(-16.7, -1.58) * mm});
            skLineSegment(sketch, "E1599", {"start": v(-16.7, -1.58) * mm, "end": v(-16.75, -1.32) * mm});
            skLineSegment(sketch, "E1600", {"start": v(-16.75, -1.32) * mm, "end": v(-16.75, -1.06) * mm});
            skLineSegment(sketch, "E1601", {"start": v(-16.75, -1.06) * mm, "end": v(-16.7, -1) * mm});
            skLineSegment(sketch, "E1602", {"start": v(-16.7, -1) * mm, "end": v(-16.65, -0.95) * mm});
            skLineSegment(sketch, "E1603", {"start": v(-16.65, -0.95) * mm, "end": v(-16.38, -0.8) * mm});
            skLineSegment(sketch, "E1604", {"start": v(-16.38, -0.8) * mm, "end": v(-16.32, -0.76) * mm});
            skLineSegment(sketch, "E1605", {"start": v(-16.32, -0.76) * mm, "end": v(-16.3, -0.76) * mm});
            skLineSegment(sketch, "E1606", {"start": v(-16.3, -0.76) * mm, "end": v(-16.12, -0.66) * mm});
            skLineSegment(sketch, "E1607", {"start": v(-16.12, -0.66) * mm, "end": v(-16.12, -0.66) * mm});
            skLineSegment(sketch, "E1608", {"start": v(-16.12, -0.66) * mm, "end": v(-16.1, -0.65) * mm});
            skLineSegment(sketch, "E1609", {"start": v(-16.1, -0.65) * mm, "end": v(-15.9, -0.56) * mm});
            skLineSegment(sketch, "E1610", {"start": v(-15.9, -0.56) * mm, "end": v(-15.88, -0.55) * mm});
            skLineSegment(sketch, "E1611", {"start": v(-15.88, -0.55) * mm, "end": v(-15.71, -0.48) * mm});
            skLineSegment(sketch, "E1612", {"start": v(-15.71, -0.48) * mm, "end": v(-15.65, -0.46) * mm});
            skLineSegment(sketch, "E1613", {"start": v(-15.65, -0.46) * mm, "end": v(-15.54, -0.41) * mm});
            skLineSegment(sketch, "E1614", {"start": v(-15.54, -0.41) * mm, "end": v(-15.45, -0.38) * mm});
            skLineSegment(sketch, "E1615", {"start": v(-15.45, -0.38) * mm, "end": v(-15.34, -0.34) * mm});
            skLineSegment(sketch, "E1616", {"start": v(-15.34, -0.34) * mm, "end": v(-15.3, -0.32) * mm});
            skLineSegment(sketch, "E1617", {"start": v(-15.3, -0.32) * mm, "end": v(-15.27, -0.31) * mm});
            skLineSegment(sketch, "E1618", {"start": v(-15.27, -0.31) * mm, "end": v(-15.26, -0.3) * mm});
            skLineSegment(sketch, "E1619", {"start": v(-15.26, -0.3) * mm, "end": v(-15.25, -0.28) * mm});
            skLineSegment(sketch, "E1620", {"start": v(-15.25, -0.28) * mm, "end": v(-15.25, 0.28) * mm});
            skLineSegment(sketch, "E1621", {"start": v(-15.25, 0.28) * mm, "end": v(-15.26, 0.3) * mm});
            skLineSegment(sketch, "E1622", {"start": v(-15.26, 0.3) * mm, "end": v(-15.27, 0.31) * mm});
            skLineSegment(sketch, "E1623", {"start": v(-15.27, 0.31) * mm, "end": v(-15.3, 0.32) * mm});
            skLineSegment(sketch, "E1624", {"start": v(-15.3, 0.32) * mm, "end": v(-15.34, 0.34) * mm});
            skLineSegment(sketch, "E1625", {"start": v(-15.34, 0.34) * mm, "end": v(-15.45, 0.38) * mm});
            skLineSegment(sketch, "E1626", {"start": v(-15.45, 0.38) * mm, "end": v(-15.54, 0.41) * mm});
            skLineSegment(sketch, "E1627", {"start": v(-15.54, 0.41) * mm, "end": v(-15.65, 0.46) * mm});
            skLineSegment(sketch, "E1628", {"start": v(-15.65, 0.46) * mm, "end": v(-15.71, 0.48) * mm});
            skLineSegment(sketch, "E1629", {"start": v(-15.71, 0.48) * mm, "end": v(-15.88, 0.55) * mm});
            skLineSegment(sketch, "E1630", {"start": v(-15.88, 0.55) * mm, "end": v(-15.9, 0.56) * mm});
            skLineSegment(sketch, "E1631", {"start": v(-15.9, 0.56) * mm, "end": v(-16.1, 0.65) * mm});
            skLineSegment(sketch, "E1632", {"start": v(-16.1, 0.65) * mm, "end": v(-16.12, 0.66) * mm});
            skLineSegment(sketch, "E1633", {"start": v(-16.12, 0.66) * mm, "end": v(-16.12, 0.66) * mm});
            skLineSegment(sketch, "E1634", {"start": v(-16.12, 0.66) * mm, "end": v(-16.3, 0.76) * mm});
            skLineSegment(sketch, "E1635", {"start": v(-16.3, 0.76) * mm, "end": v(-16.32, 0.76) * mm});
            skLineSegment(sketch, "E1636", {"start": v(-16.32, 0.76) * mm, "end": v(-16.38, 0.8) * mm});
            skLineSegment(sketch, "E1637", {"start": v(-16.38, 0.8) * mm, "end": v(-16.65, 0.95) * mm});
            skLineSegment(sketch, "E1638", {"start": v(-16.65, 0.95) * mm, "end": v(-16.7, 1) * mm});
            skLineSegment(sketch, "E1639", {"start": v(-16.7, 1) * mm, "end": v(-16.75, 1.06) * mm});
            skLineSegment(sketch, "E1640", {"start": v(-16.58, 1.61) * mm, "end": v(-16.64, 1.42) * mm});
            skLineSegment(sketch, "E1641", {"start": v(-16.64, 1.42) * mm, "end": v(-16.67, 1.23) * mm});
            skLineSegment(sketch, "E1642", {"start": v(-16.67, 1.23) * mm, "end": v(-16.6, 1.14) * mm});
            skLineSegment(sketch, "E1643", {"start": v(-16.6, 1.14) * mm, "end": v(-16.32, 0.9) * mm});
            skLineSegment(sketch, "E1644", {"start": v(-16.32, 0.9) * mm, "end": v(-16.07, 0.71) * mm});
            skLineSegment(sketch, "E1645", {"start": v(-16.07, 0.71) * mm, "end": v(-15.86, 0.6) * mm});
            skLineSegment(sketch, "E1646", {"start": v(-15.86, 0.6) * mm, "end": v(-15.7, 0.53) * mm});
            skLineSegment(sketch, "E1647", {"start": v(-15.7, 0.53) * mm, "end": v(-15.59, 0.5) * mm});
            skLineSegment(sketch, "E1648", {"start": v(-15.59, 0.5) * mm, "end": v(-15.38, 0.46) * mm});
            skLineSegment(sketch, "E1649", {"start": v(-15.38, 0.46) * mm, "end": v(-15.22, 0.39) * mm});
            skLineSegment(sketch, "E1650", {"start": v(-15.22, 0.39) * mm, "end": v(-15.15, 0.3) * mm});
            skLineSegment(sketch, "E1651", {"start": v(-15.15, 0.3) * mm, "end": v(-15.15, -0.3) * mm});
            skLineSegment(sketch, "E1652", {"start": v(-15.15, -0.3) * mm, "end": v(-15.22, -0.39) * mm});
            skLineSegment(sketch, "E1653", {"start": v(-15.22, -0.39) * mm, "end": v(-15.38, -0.46) * mm});
            skLineSegment(sketch, "E1654", {"start": v(-15.38, -0.46) * mm, "end": v(-15.59, -0.5) * mm});
            skLineSegment(sketch, "E1655", {"start": v(-15.59, -0.5) * mm, "end": v(-15.7, -0.53) * mm});
            skLineSegment(sketch, "E1656", {"start": v(-15.7, -0.53) * mm, "end": v(-15.86, -0.6) * mm});
            skLineSegment(sketch, "E1657", {"start": v(-15.86, -0.6) * mm, "end": v(-16.07, -0.71) * mm});
            skLineSegment(sketch, "E1658", {"start": v(-16.07, -0.71) * mm, "end": v(-16.32, -0.9) * mm});
            skLineSegment(sketch, "E1659", {"start": v(-16.32, -0.9) * mm, "end": v(-16.6, -1.14) * mm});
            skLineSegment(sketch, "E1660", {"start": v(-16.6, -1.14) * mm, "end": v(-16.67, -1.23) * mm});
            skLineSegment(sketch, "E1661", {"start": v(-16.67, -1.23) * mm, "end": v(-16.64, -1.42) * mm});
            skLineSegment(sketch, "E1662", {"start": v(-16.64, -1.42) * mm, "end": v(-16.58, -1.61) * mm});
            skLineSegment(sketch, "E1663", {"start": v(-16.58, -1.61) * mm, "end": v(-16.47, -1.66) * mm});
            skLineSegment(sketch, "E1664", {"start": v(-16.47, -1.66) * mm, "end": v(-16.12, -1.76) * mm});
            skLineSegment(sketch, "E1665", {"start": v(-16.12, -1.76) * mm, "end": v(-15.82, -1.82) * mm});
            skLineSegment(sketch, "E1666", {"start": v(-15.82, -1.82) * mm, "end": v(-15.57, -1.83) * mm});
            skLineSegment(sketch, "E1667", {"start": v(-15.57, -1.83) * mm, "end": v(-15.4, -1.82) * mm});
            skLineSegment(sketch, "E1668", {"start": v(-15.4, -1.82) * mm, "end": v(-15.29, -1.8) * mm});
            skLineSegment(sketch, "E1669", {"start": v(-15.29, -1.8) * mm, "end": v(-15.08, -1.75) * mm});
            skLineSegment(sketch, "E1670", {"start": v(-15.08, -1.75) * mm, "end": v(-14.91, -1.74) * mm});
            skLineSegment(sketch, "E1671", {"start": v(-14.91, -1.74) * mm, "end": v(-14.8, -1.8) * mm});
            skLineSegment(sketch, "E1672", {"start": v(-14.8, -1.8) * mm, "end": v(-14.55, -2.33) * mm});
            skLineSegment(sketch, "E1673", {"start": v(-14.55, -2.33) * mm, "end": v(-14.58, -2.44) * mm});
            skLineSegment(sketch, "E1674", {"start": v(-14.58, -2.44) * mm, "end": v(-14.68, -2.57) * mm});
            skLineSegment(sketch, "E1675", {"start": v(-14.68, -2.57) * mm, "end": v(-14.86, -2.7) * mm});
            skLineSegment(sketch, "E1676", {"start": v(-14.86, -2.7) * mm, "end": v(-14.94, -2.77) * mm});
            skLineSegment(sketch, "E1677", {"start": v(-14.94, -2.77) * mm, "end": v(-15.06, -2.9) * mm});
            skLineSegment(sketch, "E1678", {"start": v(-15.06, -2.9) * mm, "end": v(-15.2, -3.1) * mm});
            skLineSegment(sketch, "E1679", {"start": v(-15.2, -3.1) * mm, "end": v(-15.34, -3.37) * mm});
            skLineSegment(sketch, "E1680", {"start": v(-15.34, -3.37) * mm, "end": v(-15.48, -3.72) * mm});
            skLineSegment(sketch, "E1681", {"start": v(-15.48, -3.72) * mm, "end": v(-15.51, -3.83) * mm});
            skLineSegment(sketch, "E1682", {"start": v(-15.51, -3.83) * mm, "end": v(-15.4, -4) * mm});
            skLineSegment(sketch, "E1683", {"start": v(-15.4, -4) * mm, "end": v(-15.27, -4.13) * mm});
            skLineSegment(sketch, "E1684", {"start": v(-15.27, -4.13) * mm, "end": v(-15.15, -4.13) * mm});
            skLineSegment(sketch, "E1685", {"start": v(-15.15, -4.13) * mm, "end": v(-14.79, -4.07) * mm});
            skLineSegment(sketch, "E1686", {"start": v(-14.79, -4.07) * mm, "end": v(-14.5, -3.99) * mm});
            skLineSegment(sketch, "E1687", {"start": v(-14.5, -3.99) * mm, "end": v(-14.27, -3.9) * mm});
            skLineSegment(sketch, "E1688", {"start": v(-14.27, -3.9) * mm, "end": v(-14.11, -3.8) * mm});
            skLineSegment(sketch, "E1689", {"start": v(-14.11, -3.8) * mm, "end": v(-14.02, -3.75) * mm});
            skLineSegment(sketch, "E1690", {"start": v(-14.02, -3.75) * mm, "end": v(-13.86, -3.6) * mm});
            skLineSegment(sketch, "E1691", {"start": v(-13.86, -3.6) * mm, "end": v(-13.71, -3.53) * mm});
            skLineSegment(sketch, "E1692", {"start": v(-13.71, -3.53) * mm, "end": v(-13.6, -3.53) * mm});
            skLineSegment(sketch, "E1693", {"start": v(-13.6, -3.53) * mm, "end": v(-13.13, -3.9) * mm});
            skLineSegment(sketch, "E1694", {"start": v(-13.13, -3.9) * mm, "end": v(-13.1, -4.01) * mm});
            skLineSegment(sketch, "E1695", {"start": v(-13.1, -4.01) * mm, "end": v(-13.14, -4.18) * mm});
            skLineSegment(sketch, "E1696", {"start": v(-13.14, -4.18) * mm, "end": v(-13.25, -4.36) * mm});
            skLineSegment(sketch, "E1697", {"start": v(-13.25, -4.36) * mm, "end": v(-13.29, -4.47) * mm});
            skLineSegment(sketch, "E1698", {"start": v(-13.29, -4.47) * mm, "end": v(-13.34, -4.64) * mm});
            skLineSegment(sketch, "E1699", {"start": v(-13.34, -4.64) * mm, "end": v(-13.38, -4.88) * mm});
            skLineSegment(sketch, "E1700", {"start": v(-13.38, -4.88) * mm, "end": v(-13.4, -5.18) * mm});
            skLineSegment(sketch, "E1701", {"start": v(-13.4, -5.18) * mm, "end": v(-13.37, -5.55) * mm});
            skLineSegment(sketch, "E1702", {"start": v(-13.37, -5.55) * mm, "end": v(-13.35, -5.67) * mm});
            skLineSegment(sketch, "E1703", {"start": v(-13.35, -5.67) * mm, "end": v(-13.18, -5.77) * mm});
            skLineSegment(sketch, "E1704", {"start": v(-13.18, -5.77) * mm, "end": v(-13, -5.84) * mm});
            skLineSegment(sketch, "E1705", {"start": v(-13, -5.84) * mm, "end": v(-12.9, -5.78) * mm});
            skLineSegment(sketch, "E1706", {"start": v(-12.9, -5.78) * mm, "end": v(-12.59, -5.57) * mm});
            skLineSegment(sketch, "E1707", {"start": v(-12.59, -5.57) * mm, "end": v(-12.36, -5.37) * mm});
            skLineSegment(sketch, "E1708", {"start": v(-12.36, -5.37) * mm, "end": v(-12.2, -5.19) * mm});
            skLineSegment(sketch, "E1709", {"start": v(-12.2, -5.19) * mm, "end": v(-12.1, -5.04) * mm});
            skLineSegment(sketch, "E1710", {"start": v(-12.1, -5.04) * mm, "end": v(-12.04, -4.95) * mm});
            skLineSegment(sketch, "E1711", {"start": v(-12.04, -4.95) * mm, "end": v(-11.95, -4.75) * mm});
            skLineSegment(sketch, "E1712", {"start": v(-11.95, -4.75) * mm, "end": v(-11.85, -4.62) * mm});
            skLineSegment(sketch, "E1713", {"start": v(-11.85, -4.62) * mm, "end": v(-11.75, -4.56) * mm});
            skLineSegment(sketch, "E1714", {"start": v(-11.75, -4.56) * mm, "end": v(-11.17, -4.7) * mm});
            skLineSegment(sketch, "E1715", {"start": v(-11.17, -4.7) * mm, "end": v(-11.1, -4.79) * mm});
            skLineSegment(sketch, "E1716", {"start": v(-11.1, -4.79) * mm, "end": v(-11.06, -4.95) * mm});
            skLineSegment(sketch, "E1717", {"start": v(-11.06, -4.95) * mm, "end": v(-11.07, -5.17) * mm});
            skLineSegment(sketch, "E1718", {"start": v(-11.07, -5.17) * mm, "end": v(-11.06, -5.28) * mm});
            skLineSegment(sketch, "E1719", {"start": v(-11.06, -5.28) * mm, "end": v(-11.03, -5.45) * mm});
            skLineSegment(sketch, "E1720", {"start": v(-11.03, -5.45) * mm, "end": v(-10.96, -5.68) * mm});
            skLineSegment(sketch, "E1721", {"start": v(-10.96, -5.68) * mm, "end": v(-10.85, -5.97) * mm});
            skLineSegment(sketch, "E1722", {"start": v(-10.85, -5.97) * mm, "end": v(-10.66, -6.3) * mm});
            skLineSegment(sketch, "E1723", {"start": v(-10.66, -6.3) * mm, "end": v(-10.6, -6.39) * mm});
            skLineSegment(sketch, "E1724", {"start": v(-10.6, -6.39) * mm, "end": v(-10.4, -6.4) * mm});
            skLineSegment(sketch, "E1725", {"start": v(-10.4, -6.4) * mm, "end": v(-10.2, -6.39) * mm});
            skLineSegment(sketch, "E1726", {"start": v(-10.2, -6.39) * mm, "end": v(-10.14, -6.3) * mm});
            skLineSegment(sketch, "E1727", {"start": v(-10.14, -6.3) * mm, "end": v(-9.95, -5.97) * mm});
            skLineSegment(sketch, "E1728", {"start": v(-9.95, -5.97) * mm, "end": v(-9.84, -5.68) * mm});
            skLineSegment(sketch, "E1729", {"start": v(-9.84, -5.68) * mm, "end": v(-9.77, -5.45) * mm});
            skLineSegment(sketch, "E1730", {"start": v(-9.77, -5.45) * mm, "end": v(-9.74, -5.28) * mm});
            skLineSegment(sketch, "E1731", {"start": v(-9.74, -5.28) * mm, "end": v(-9.73, -5.17) * mm});
            skLineSegment(sketch, "E1732", {"start": v(-9.73, -5.17) * mm, "end": v(-9.74, -4.95) * mm});
            skLineSegment(sketch, "E1733", {"start": v(-9.74, -4.95) * mm, "end": v(-9.7, -4.79) * mm});
            skLineSegment(sketch, "E1734", {"start": v(-9.7, -4.79) * mm, "end": v(-9.63, -4.7) * mm});
            skLineSegment(sketch, "E1735", {"start": v(-9.63, -4.7) * mm, "end": v(-9.05, -4.56) * mm});
            skLineSegment(sketch, "E1736", {"start": v(-9.05, -4.56) * mm, "end": v(-8.95, -4.62) * mm});
            skLineSegment(sketch, "E1737", {"start": v(-8.95, -4.62) * mm, "end": v(-8.85, -4.75) * mm});
            skLineSegment(sketch, "E1738", {"start": v(-8.85, -4.75) * mm, "end": v(-8.76, -4.95) * mm});
            skLineSegment(sketch, "E1739", {"start": v(-8.76, -4.95) * mm, "end": v(-8.7, -5.04) * mm});
            skLineSegment(sketch, "E1740", {"start": v(-8.7, -5.04) * mm, "end": v(-8.6, -5.19) * mm});
            skLineSegment(sketch, "E1741", {"start": v(-8.6, -5.19) * mm, "end": v(-8.44, -5.37) * mm});
            skLineSegment(sketch, "E1742", {"start": v(-8.44, -5.37) * mm, "end": v(-8.21, -5.57) * mm});
            skLineSegment(sketch, "E1743", {"start": v(-8.21, -5.57) * mm, "end": v(-7.9, -5.78) * mm});
            skLineSegment(sketch, "E1744", {"start": v(-7.9, -5.78) * mm, "end": v(-7.8, -5.84) * mm});
            skLineSegment(sketch, "E1745", {"start": v(-7.8, -5.84) * mm, "end": v(-7.62, -5.77) * mm});
            skLineSegment(sketch, "E1746", {"start": v(-7.62, -5.77) * mm, "end": v(-7.45, -5.67) * mm});
            skLineSegment(sketch, "E1747", {"start": v(-7.45, -5.67) * mm, "end": v(-7.43, -5.55) * mm});
            skLineSegment(sketch, "E1748", {"start": v(-7.43, -5.55) * mm, "end": v(-7.4, -5.18) * mm});
            skLineSegment(sketch, "E1749", {"start": v(-7.4, -5.18) * mm, "end": v(-7.42, -4.88) * mm});
            skLineSegment(sketch, "E1750", {"start": v(-7.42, -4.88) * mm, "end": v(-7.46, -4.64) * mm});
            skLineSegment(sketch, "E1751", {"start": v(-7.46, -4.64) * mm, "end": v(-7.51, -4.47) * mm});
            skLineSegment(sketch, "E1752", {"start": v(-7.51, -4.47) * mm, "end": v(-7.55, -4.36) * mm});
            skLineSegment(sketch, "E1753", {"start": v(-7.55, -4.36) * mm, "end": v(-7.66, -4.18) * mm});
            skLineSegment(sketch, "E1754", {"start": v(-7.66, -4.18) * mm, "end": v(-7.7, -4.01) * mm});
            skLineSegment(sketch, "E1755", {"start": v(-7.7, -4.01) * mm, "end": v(-7.67, -3.9) * mm});
            skLineSegment(sketch, "E1756", {"start": v(-7.67, -3.9) * mm, "end": v(-7.2, -3.53) * mm});
            skLineSegment(sketch, "E1757", {"start": v(-7.2, -3.53) * mm, "end": v(-7.09, -3.53) * mm});
            skLineSegment(sketch, "E1758", {"start": v(-7.09, -3.53) * mm, "end": v(-6.94, -3.6) * mm});
            skLineSegment(sketch, "E1759", {"start": v(-6.94, -3.6) * mm, "end": v(-6.78, -3.75) * mm});
            skLineSegment(sketch, "E1760", {"start": v(-6.78, -3.75) * mm, "end": v(-6.69, -3.8) * mm});
            skLineSegment(sketch, "E1761", {"start": v(-6.69, -3.8) * mm, "end": v(-6.53, -3.9) * mm});
            skLineSegment(sketch, "E1762", {"start": v(-6.53, -3.9) * mm, "end": v(-6.3, -3.99) * mm});
            skLineSegment(sketch, "E1763", {"start": v(-6.3, -3.99) * mm, "end": v(-6.01, -4.07) * mm});
            skLineSegment(sketch, "E1764", {"start": v(-6.01, -4.07) * mm, "end": v(-5.65, -4.13) * mm});
            skLineSegment(sketch, "E1765", {"start": v(-5.65, -4.13) * mm, "end": v(-5.53, -4.13) * mm});
            skLineSegment(sketch, "E1766", {"start": v(-5.53, -4.13) * mm, "end": v(-5.4, -4) * mm});
            skLineSegment(sketch, "E1767", {"start": v(-5.4, -4) * mm, "end": v(-5.29, -3.83) * mm});
            skLineSegment(sketch, "E1768", {"start": v(-5.29, -3.83) * mm, "end": v(-5.32, -3.72) * mm});
            skLineSegment(sketch, "E1769", {"start": v(-5.32, -3.72) * mm, "end": v(-5.46, -3.37) * mm});
            skLineSegment(sketch, "E1770", {"start": v(-5.46, -3.37) * mm, "end": v(-5.6, -3.1) * mm});
            skLineSegment(sketch, "E1771", {"start": v(-5.6, -3.1) * mm, "end": v(-5.74, -2.9) * mm});
            skLineSegment(sketch, "E1772", {"start": v(-5.74, -2.9) * mm, "end": v(-5.86, -2.77) * mm});
            skLineSegment(sketch, "E1773", {"start": v(-5.86, -2.77) * mm, "end": v(-5.94, -2.7) * mm});
            skLineSegment(sketch, "E1774", {"start": v(-5.94, -2.7) * mm, "end": v(-6.12, -2.57) * mm});
            skLineSegment(sketch, "E1775", {"start": v(-6.12, -2.57) * mm, "end": v(-6.22, -2.44) * mm});
            skLineSegment(sketch, "E1776", {"start": v(-6.22, -2.44) * mm, "end": v(-6.25, -2.33) * mm});
            skLineSegment(sketch, "E1777", {"start": v(-6.25, -2.33) * mm, "end": v(-6, -1.8) * mm});
            skLineSegment(sketch, "E1778", {"start": v(-6, -1.8) * mm, "end": v(-5.89, -1.74) * mm});
            skLineSegment(sketch, "E1779", {"start": v(-5.89, -1.74) * mm, "end": v(-5.72, -1.75) * mm});
            skLineSegment(sketch, "E1780", {"start": v(-5.72, -1.75) * mm, "end": v(-5.51, -1.8) * mm});
            skLineSegment(sketch, "E1781", {"start": v(-5.51, -1.8) * mm, "end": v(-5.4, -1.82) * mm});
            skLineSegment(sketch, "E1782", {"start": v(-5.4, -1.82) * mm, "end": v(-5.23, -1.83) * mm});
            skLineSegment(sketch, "E1783", {"start": v(-5.23, -1.83) * mm, "end": v(-4.98, -1.82) * mm});
            skLineSegment(sketch, "E1784", {"start": v(-4.98, -1.82) * mm, "end": v(-4.68, -1.76) * mm});
            skLineSegment(sketch, "E1785", {"start": v(-4.68, -1.76) * mm, "end": v(-4.33, -1.66) * mm});
            skLineSegment(sketch, "E1786", {"start": v(-4.33, -1.66) * mm, "end": v(-4.22, -1.61) * mm});
            skLineSegment(sketch, "E1787", {"start": v(-4.22, -1.61) * mm, "end": v(-4.16, -1.42) * mm});
            skLineSegment(sketch, "E1788", {"start": v(-4.16, -1.42) * mm, "end": v(-4.13, -1.23) * mm});
            skLineSegment(sketch, "E1789", {"start": v(-4.13, -1.23) * mm, "end": v(-4.2, -1.14) * mm});
            skLineSegment(sketch, "E1790", {"start": v(-4.2, -1.14) * mm, "end": v(-4.48, -0.9) * mm});
            skLineSegment(sketch, "E1791", {"start": v(-4.48, -0.9) * mm, "end": v(-4.73, -0.71) * mm});
            skLineSegment(sketch, "E1792", {"start": v(-4.73, -0.71) * mm, "end": v(-4.94, -0.6) * mm});
            skLineSegment(sketch, "E1793", {"start": v(-4.94, -0.6) * mm, "end": v(-5.1, -0.53) * mm});
            skLineSegment(sketch, "E1794", {"start": v(-5.1, -0.53) * mm, "end": v(-5.21, -0.5) * mm});
            skLineSegment(sketch, "E1795", {"start": v(-5.21, -0.5) * mm, "end": v(-5.42, -0.46) * mm});
            skLineSegment(sketch, "E1796", {"start": v(-5.42, -0.46) * mm, "end": v(-5.58, -0.39) * mm});
            skLineSegment(sketch, "E1797", {"start": v(-5.58, -0.39) * mm, "end": v(-5.65, -0.3) * mm});
            skLineSegment(sketch, "E1798", {"start": v(-5.65, -0.3) * mm, "end": v(-5.65, 0.3) * mm});
            skLineSegment(sketch, "E1799", {"start": v(-5.65, 0.3) * mm, "end": v(-5.58, 0.39) * mm});
            skLineSegment(sketch, "E1800", {"start": v(-5.58, 0.39) * mm, "end": v(-5.42, 0.46) * mm});
            skLineSegment(sketch, "E1801", {"start": v(-5.42, 0.46) * mm, "end": v(-5.21, 0.5) * mm});
            skLineSegment(sketch, "E1802", {"start": v(-5.21, 0.5) * mm, "end": v(-5.1, 0.53) * mm});
            skLineSegment(sketch, "E1803", {"start": v(-5.1, 0.53) * mm, "end": v(-4.94, 0.6) * mm});
            skLineSegment(sketch, "E1804", {"start": v(-4.94, 0.6) * mm, "end": v(-4.73, 0.71) * mm});
            skLineSegment(sketch, "E1805", {"start": v(-4.73, 0.71) * mm, "end": v(-4.48, 0.9) * mm});
            skLineSegment(sketch, "E1806", {"start": v(-4.48, 0.9) * mm, "end": v(-4.2, 1.14) * mm});
            skLineSegment(sketch, "E1807", {"start": v(-4.2, 1.14) * mm, "end": v(-4.13, 1.23) * mm});
            skLineSegment(sketch, "E1808", {"start": v(-4.13, 1.23) * mm, "end": v(-4.16, 1.42) * mm});
            skLineSegment(sketch, "E1809", {"start": v(-4.16, 1.42) * mm, "end": v(-4.22, 1.61) * mm});
            skLineSegment(sketch, "E1810", {"start": v(-4.22, 1.61) * mm, "end": v(-4.33, 1.66) * mm});
            skLineSegment(sketch, "E1811", {"start": v(-4.33, 1.66) * mm, "end": v(-4.68, 1.76) * mm});
            skLineSegment(sketch, "E1812", {"start": v(-4.68, 1.76) * mm, "end": v(-4.98, 1.82) * mm});
            skLineSegment(sketch, "E1813", {"start": v(-4.98, 1.82) * mm, "end": v(-5.23, 1.83) * mm});
            skLineSegment(sketch, "E1814", {"start": v(-5.23, 1.83) * mm, "end": v(-5.4, 1.82) * mm});
            skLineSegment(sketch, "E1815", {"start": v(-5.4, 1.82) * mm, "end": v(-5.51, 1.8) * mm});
            skLineSegment(sketch, "E1816", {"start": v(-5.51, 1.8) * mm, "end": v(-5.72, 1.75) * mm});
            skLineSegment(sketch, "E1817", {"start": v(-5.72, 1.75) * mm, "end": v(-5.89, 1.74) * mm});
            skLineSegment(sketch, "E1818", {"start": v(-5.89, 1.74) * mm, "end": v(-6, 1.8) * mm});
            skLineSegment(sketch, "E1819", {"start": v(-6, 1.8) * mm, "end": v(-6.25, 2.33) * mm});
            skLineSegment(sketch, "E1820", {"start": v(-6.25, 2.33) * mm, "end": v(-6.22, 2.44) * mm});
            skLineSegment(sketch, "E1821", {"start": v(-6.22, 2.44) * mm, "end": v(-6.12, 2.57) * mm});
            skLineSegment(sketch, "E1822", {"start": v(-6.12, 2.57) * mm, "end": v(-5.94, 2.7) * mm});
            skLineSegment(sketch, "E1823", {"start": v(-5.94, 2.7) * mm, "end": v(-5.86, 2.77) * mm});
            skLineSegment(sketch, "E1824", {"start": v(-5.86, 2.77) * mm, "end": v(-5.74, 2.9) * mm});
            skLineSegment(sketch, "E1825", {"start": v(-5.74, 2.9) * mm, "end": v(-5.6, 3.1) * mm});
            skLineSegment(sketch, "E1826", {"start": v(-5.6, 3.1) * mm, "end": v(-5.46, 3.37) * mm});
            skLineSegment(sketch, "E1827", {"start": v(-5.46, 3.37) * mm, "end": v(-5.32, 3.72) * mm});
            skLineSegment(sketch, "E1828", {"start": v(-5.32, 3.72) * mm, "end": v(-5.29, 3.83) * mm});
            skLineSegment(sketch, "E1829", {"start": v(-5.29, 3.83) * mm, "end": v(-5.4, 4) * mm});
            skLineSegment(sketch, "E1830", {"start": v(-5.4, 4) * mm, "end": v(-5.53, 4.13) * mm});
            skLineSegment(sketch, "E1831", {"start": v(-5.53, 4.13) * mm, "end": v(-5.65, 4.13) * mm});
            skLineSegment(sketch, "E1832", {"start": v(-5.65, 4.13) * mm, "end": v(-6.01, 4.07) * mm});
            skLineSegment(sketch, "E1833", {"start": v(-6.01, 4.07) * mm, "end": v(-6.3, 3.99) * mm});
            skLineSegment(sketch, "E1834", {"start": v(-6.3, 3.99) * mm, "end": v(-6.53, 3.9) * mm});
            skLineSegment(sketch, "E1835", {"start": v(-6.53, 3.9) * mm, "end": v(-6.69, 3.8) * mm});
            skLineSegment(sketch, "E1836", {"start": v(-6.69, 3.8) * mm, "end": v(-6.78, 3.75) * mm});
            skLineSegment(sketch, "E1837", {"start": v(-6.78, 3.75) * mm, "end": v(-6.94, 3.6) * mm});
            skLineSegment(sketch, "E1838", {"start": v(-6.94, 3.6) * mm, "end": v(-7.09, 3.53) * mm});
            skLineSegment(sketch, "E1839", {"start": v(-7.09, 3.53) * mm, "end": v(-7.2, 3.53) * mm});
            skLineSegment(sketch, "E1840", {"start": v(-7.2, 3.53) * mm, "end": v(-7.67, 3.9) * mm});
            skLineSegment(sketch, "E1841", {"start": v(-7.67, 3.9) * mm, "end": v(-7.7, 4.01) * mm});
            skLineSegment(sketch, "E1842", {"start": v(-7.7, 4.01) * mm, "end": v(-7.66, 4.18) * mm});
            skLineSegment(sketch, "E1843", {"start": v(-7.66, 4.18) * mm, "end": v(-7.55, 4.36) * mm});
            skLineSegment(sketch, "E1844", {"start": v(-7.55, 4.36) * mm, "end": v(-7.51, 4.47) * mm});
            skLineSegment(sketch, "E1845", {"start": v(-7.51, 4.47) * mm, "end": v(-7.46, 4.64) * mm});
            skLineSegment(sketch, "E1846", {"start": v(-7.46, 4.64) * mm, "end": v(-7.42, 4.88) * mm});
            skLineSegment(sketch, "E1847", {"start": v(-7.42, 4.88) * mm, "end": v(-7.4, 5.18) * mm});
            skLineSegment(sketch, "E1848", {"start": v(-7.4, 5.18) * mm, "end": v(-7.43, 5.55) * mm});
            skLineSegment(sketch, "E1849", {"start": v(-7.43, 5.55) * mm, "end": v(-7.45, 5.67) * mm});
            skLineSegment(sketch, "E1850", {"start": v(-7.45, 5.67) * mm, "end": v(-7.62, 5.77) * mm});
            skLineSegment(sketch, "E1851", {"start": v(-7.62, 5.77) * mm, "end": v(-7.8, 5.84) * mm});
            skLineSegment(sketch, "E1852", {"start": v(-7.8, 5.84) * mm, "end": v(-7.9, 5.78) * mm});
            skLineSegment(sketch, "E1853", {"start": v(-7.9, 5.78) * mm, "end": v(-8.21, 5.57) * mm});
            skLineSegment(sketch, "E1854", {"start": v(-8.21, 5.57) * mm, "end": v(-8.44, 5.37) * mm});
            skLineSegment(sketch, "E1855", {"start": v(-8.44, 5.37) * mm, "end": v(-8.6, 5.19) * mm});
            skLineSegment(sketch, "E1856", {"start": v(-8.6, 5.19) * mm, "end": v(-8.7, 5.04) * mm});
            skLineSegment(sketch, "E1857", {"start": v(-8.7, 5.04) * mm, "end": v(-8.76, 4.95) * mm});
            skLineSegment(sketch, "E1858", {"start": v(-8.76, 4.95) * mm, "end": v(-8.85, 4.75) * mm});
            skLineSegment(sketch, "E1859", {"start": v(-8.85, 4.75) * mm, "end": v(-8.95, 4.62) * mm});
            skLineSegment(sketch, "E1860", {"start": v(-8.95, 4.62) * mm, "end": v(-9.05, 4.56) * mm});
            skLineSegment(sketch, "E1861", {"start": v(-9.05, 4.56) * mm, "end": v(-9.63, 4.7) * mm});
            skLineSegment(sketch, "E1862", {"start": v(-9.63, 4.7) * mm, "end": v(-9.7, 4.79) * mm});
            skLineSegment(sketch, "E1863", {"start": v(-9.7, 4.79) * mm, "end": v(-9.74, 4.95) * mm});
            skLineSegment(sketch, "E1864", {"start": v(-9.74, 4.95) * mm, "end": v(-9.73, 5.17) * mm});
            skLineSegment(sketch, "E1865", {"start": v(-9.73, 5.17) * mm, "end": v(-9.74, 5.28) * mm});
            skLineSegment(sketch, "E1866", {"start": v(-9.74, 5.28) * mm, "end": v(-9.77, 5.45) * mm});
            skLineSegment(sketch, "E1867", {"start": v(-9.77, 5.45) * mm, "end": v(-9.84, 5.68) * mm});
            skLineSegment(sketch, "E1868", {"start": v(-9.84, 5.68) * mm, "end": v(-9.95, 5.97) * mm});
            skLineSegment(sketch, "E1869", {"start": v(-9.95, 5.97) * mm, "end": v(-10.14, 6.3) * mm});
            skLineSegment(sketch, "E1870", {"start": v(-10.14, 6.3) * mm, "end": v(-10.2, 6.39) * mm});
            skLineSegment(sketch, "E1871", {"start": v(-10.2, 6.39) * mm, "end": v(-10.4, 6.4) * mm});
            skLineSegment(sketch, "E1872", {"start": v(-10.4, 6.4) * mm, "end": v(-10.6, 6.39) * mm});
            skLineSegment(sketch, "E1873", {"start": v(-10.6, 6.39) * mm, "end": v(-10.66, 6.3) * mm});
            skLineSegment(sketch, "E1874", {"start": v(-10.66, 6.3) * mm, "end": v(-10.85, 5.97) * mm});
            skLineSegment(sketch, "E1875", {"start": v(-10.85, 5.97) * mm, "end": v(-10.96, 5.68) * mm});
            skLineSegment(sketch, "E1876", {"start": v(-10.96, 5.68) * mm, "end": v(-11.03, 5.45) * mm});
            skLineSegment(sketch, "E1877", {"start": v(-11.03, 5.45) * mm, "end": v(-11.06, 5.28) * mm});
            skLineSegment(sketch, "E1878", {"start": v(-11.06, 5.28) * mm, "end": v(-11.07, 5.17) * mm});
            skLineSegment(sketch, "E1879", {"start": v(-11.07, 5.17) * mm, "end": v(-11.06, 4.95) * mm});
            skLineSegment(sketch, "E1880", {"start": v(-11.06, 4.95) * mm, "end": v(-11.1, 4.79) * mm});
            skLineSegment(sketch, "E1881", {"start": v(-11.1, 4.79) * mm, "end": v(-11.17, 4.7) * mm});
            skLineSegment(sketch, "E1882", {"start": v(-11.17, 4.7) * mm, "end": v(-11.75, 4.56) * mm});
            skLineSegment(sketch, "E1883", {"start": v(-11.75, 4.56) * mm, "end": v(-11.85, 4.62) * mm});
            skLineSegment(sketch, "E1884", {"start": v(-11.85, 4.62) * mm, "end": v(-11.95, 4.75) * mm});
            skLineSegment(sketch, "E1885", {"start": v(-11.95, 4.75) * mm, "end": v(-12.04, 4.95) * mm});
            skLineSegment(sketch, "E1886", {"start": v(-12.04, 4.95) * mm, "end": v(-12.1, 5.04) * mm});
            skLineSegment(sketch, "E1887", {"start": v(-12.1, 5.04) * mm, "end": v(-12.2, 5.19) * mm});
            skLineSegment(sketch, "E1888", {"start": v(-12.2, 5.19) * mm, "end": v(-12.36, 5.37) * mm});
            skLineSegment(sketch, "E1889", {"start": v(-12.36, 5.37) * mm, "end": v(-12.59, 5.57) * mm});
            skLineSegment(sketch, "E1890", {"start": v(-12.59, 5.57) * mm, "end": v(-12.9, 5.78) * mm});
            skLineSegment(sketch, "E1891", {"start": v(-12.9, 5.78) * mm, "end": v(-13, 5.84) * mm});
            skLineSegment(sketch, "E1892", {"start": v(-13, 5.84) * mm, "end": v(-13.18, 5.77) * mm});
            skLineSegment(sketch, "E1893", {"start": v(-13.18, 5.77) * mm, "end": v(-13.35, 5.67) * mm});
            skLineSegment(sketch, "E1894", {"start": v(-13.35, 5.67) * mm, "end": v(-13.37, 5.55) * mm});
            skLineSegment(sketch, "E1895", {"start": v(-13.37, 5.55) * mm, "end": v(-13.4, 5.18) * mm});
            skLineSegment(sketch, "E1896", {"start": v(-13.4, 5.18) * mm, "end": v(-13.38, 4.88) * mm});
            skLineSegment(sketch, "E1897", {"start": v(-13.38, 4.88) * mm, "end": v(-13.34, 4.64) * mm});
            skLineSegment(sketch, "E1898", {"start": v(-13.34, 4.64) * mm, "end": v(-13.29, 4.47) * mm});
            skLineSegment(sketch, "E1899", {"start": v(-13.29, 4.47) * mm, "end": v(-13.25, 4.36) * mm});
            skLineSegment(sketch, "E1900", {"start": v(-13.25, 4.36) * mm, "end": v(-13.14, 4.18) * mm});
            skLineSegment(sketch, "E1901", {"start": v(-13.14, 4.18) * mm, "end": v(-13.1, 4.01) * mm});
            skLineSegment(sketch, "E1902", {"start": v(-13.1, 4.01) * mm, "end": v(-13.13, 3.9) * mm});
            skLineSegment(sketch, "E1903", {"start": v(-13.13, 3.9) * mm, "end": v(-13.6, 3.53) * mm});
            skLineSegment(sketch, "E1904", {"start": v(-13.6, 3.53) * mm, "end": v(-13.71, 3.53) * mm});
            skLineSegment(sketch, "E1905", {"start": v(-13.71, 3.53) * mm, "end": v(-13.86, 3.6) * mm});
            skLineSegment(sketch, "E1906", {"start": v(-13.86, 3.6) * mm, "end": v(-14.02, 3.75) * mm});
            skLineSegment(sketch, "E1907", {"start": v(-14.02, 3.75) * mm, "end": v(-14.11, 3.8) * mm});
            skLineSegment(sketch, "E1908", {"start": v(-14.11, 3.8) * mm, "end": v(-14.27, 3.9) * mm});
            skLineSegment(sketch, "E1909", {"start": v(-14.27, 3.9) * mm, "end": v(-14.5, 3.99) * mm});
            skLineSegment(sketch, "E1910", {"start": v(-14.5, 3.99) * mm, "end": v(-14.79, 4.07) * mm});
            skLineSegment(sketch, "E1911", {"start": v(-14.79, 4.07) * mm, "end": v(-15.15, 4.13) * mm});
            skLineSegment(sketch, "E1912", {"start": v(-15.15, 4.13) * mm, "end": v(-15.27, 4.13) * mm});
            skLineSegment(sketch, "E1913", {"start": v(-15.27, 4.13) * mm, "end": v(-15.4, 4) * mm});
            skLineSegment(sketch, "E1914", {"start": v(-15.4, 4) * mm, "end": v(-15.51, 3.83) * mm});
            skLineSegment(sketch, "E1915", {"start": v(-15.51, 3.83) * mm, "end": v(-15.48, 3.72) * mm});
            skLineSegment(sketch, "E1916", {"start": v(-15.48, 3.72) * mm, "end": v(-15.34, 3.37) * mm});
            skLineSegment(sketch, "E1917", {"start": v(-15.34, 3.37) * mm, "end": v(-15.2, 3.1) * mm});
            skLineSegment(sketch, "E1918", {"start": v(-15.2, 3.1) * mm, "end": v(-15.06, 2.9) * mm});
            skLineSegment(sketch, "E1919", {"start": v(-15.06, 2.9) * mm, "end": v(-14.94, 2.77) * mm});
            skLineSegment(sketch, "E1920", {"start": v(-14.94, 2.77) * mm, "end": v(-14.86, 2.7) * mm});
            skLineSegment(sketch, "E1921", {"start": v(-14.86, 2.7) * mm, "end": v(-14.68, 2.57) * mm});
            skLineSegment(sketch, "E1922", {"start": v(-14.68, 2.57) * mm, "end": v(-14.58, 2.44) * mm});
            skLineSegment(sketch, "E1923", {"start": v(-14.58, 2.44) * mm, "end": v(-14.55, 2.33) * mm});
            skLineSegment(sketch, "E1924", {"start": v(-14.55, 2.33) * mm, "end": v(-14.8, 1.8) * mm});
            skLineSegment(sketch, "E1925", {"start": v(-14.8, 1.8) * mm, "end": v(-14.91, 1.74) * mm});
            skLineSegment(sketch, "E1926", {"start": v(-14.91, 1.74) * mm, "end": v(-15.08, 1.75) * mm});
            skLineSegment(sketch, "E1927", {"start": v(-15.08, 1.75) * mm, "end": v(-15.29, 1.8) * mm});
            skLineSegment(sketch, "E1928", {"start": v(-15.29, 1.8) * mm, "end": v(-15.4, 1.82) * mm});
            skLineSegment(sketch, "E1929", {"start": v(-15.4, 1.82) * mm, "end": v(-15.57, 1.83) * mm});
            skLineSegment(sketch, "E1930", {"start": v(-15.57, 1.83) * mm, "end": v(-15.82, 1.82) * mm});
            skLineSegment(sketch, "E1931", {"start": v(-15.82, 1.82) * mm, "end": v(-16.12, 1.76) * mm});
            skLineSegment(sketch, "E1932", {"start": v(-16.12, 1.76) * mm, "end": v(-16.47, 1.66) * mm});
            skLineSegment(sketch, "E1933", {"start": v(-16.47, 1.66) * mm, "end": v(-16.58, 1.61) * mm});
            skCircle(sketch, "E1934", {"center": v(0, 0) * mm, "radius": 19.5 * mm});
            skCircle(sketch, "E1935", {"center": v(-10.4, 0) * mm, "radius": 1.5 * mm});
            skCircle(sketch, "E1936", {"center": v(0, 0) * mm, "radius": 23 * mm});
            skSolve(sketch);
        }
        {
            var Q0;
            Q0=qCreatedBy(makeId("Top.planeOp"),FACE);
            var sketch = newSketch(context, id + "F1", { "sketchPlane" : qUnion([Q0])});
            skLineSegment(sketch, "E1937", {"start": v(-16.35, 1.06) * mm, "end": v(-16.35, 1.32) * mm});
            skLineSegment(sketch, "E1938", {"start": v(-16.35, 1.32) * mm, "end": v(-16.3, 1.58) * mm});
            skLineSegment(sketch, "E1939", {"start": v(-16.3, 1.58) * mm, "end": v(-16.25, 1.63) * mm});
            skLineSegment(sketch, "E1940", {"start": v(-16.25, 1.63) * mm, "end": v(-16.2, 1.66) * mm});
            skLineSegment(sketch, "E1941", {"start": v(-16.2, 1.66) * mm, "end": v(-15.9, 1.78) * mm});
            skLineSegment(sketch, "E1942", {"start": v(-15.9, 1.78) * mm, "end": v(-15.83, 1.8) * mm});
            skLineSegment(sketch, "E1943", {"start": v(-15.83, 1.8) * mm, "end": v(-15.81, 1.8) * mm});
            skLineSegment(sketch, "E1944", {"start": v(-15.81, 1.8) * mm, "end": v(-15.63, 1.87) * mm});
            skLineSegment(sketch, "E1945", {"start": v(-15.63, 1.87) * mm, "end": v(-15.62, 1.87) * mm});
            skLineSegment(sketch, "E1946", {"start": v(-15.62, 1.87) * mm, "end": v(-15.6, 1.88) * mm});
            skLineSegment(sketch, "E1947", {"start": v(-15.6, 1.88) * mm, "end": v(-15.39, 1.94) * mm});
            skLineSegment(sketch, "E1948", {"start": v(-15.39, 1.94) * mm, "end": v(-15.37, 1.94) * mm});
            skLineSegment(sketch, "E1949", {"start": v(-15.37, 1.94) * mm, "end": v(-15.2, 1.98) * mm});
            skLineSegment(sketch, "E1950", {"start": v(-15.2, 1.98) * mm, "end": v(-15.13, 2) * mm});
            skLineSegment(sketch, "E1951", {"start": v(-15.13, 2) * mm, "end": v(-15.02, 2.02) * mm});
            skLineSegment(sketch, "E1952", {"start": v(-15.02, 2.02) * mm, "end": v(-14.9, 2.04) * mm});
            skLineSegment(sketch, "E1953", {"start": v(-14.9, 2.04) * mm, "end": v(-14.8, 2.06) * mm});
            skLineSegment(sketch, "E1954", {"start": v(-14.8, 2.06) * mm, "end": v(-14.76, 2.07) * mm});
            skLineSegment(sketch, "E1955", {"start": v(-14.76, 2.07) * mm, "end": v(-14.73, 2.08) * mm});
            skLineSegment(sketch, "E1956", {"start": v(-14.73, 2.08) * mm, "end": v(-14.72, 2.1) * mm});
            skLineSegment(sketch, "E1957", {"start": v(-14.72, 2.1) * mm, "end": v(-14.7, 2.1) * mm});
            skLineSegment(sketch, "E1958", {"start": v(-14.7, 2.1) * mm, "end": v(-14.61, 2.66) * mm});
            skLineSegment(sketch, "E1959", {"start": v(-14.61, 2.66) * mm, "end": v(-14.62, 2.68) * mm});
            skLineSegment(sketch, "E1960", {"start": v(-14.62, 2.68) * mm, "end": v(-14.63, 2.7) * mm});
            skLineSegment(sketch, "E1961", {"start": v(-14.63, 2.7) * mm, "end": v(-14.65, 2.71) * mm});
            skLineSegment(sketch, "E1962", {"start": v(-14.65, 2.71) * mm, "end": v(-14.7, 2.74) * mm});
            skLineSegment(sketch, "E1963", {"start": v(-14.7, 2.74) * mm, "end": v(-14.79, 2.79) * mm});
            skLineSegment(sketch, "E1964", {"start": v(-14.79, 2.79) * mm, "end": v(-14.89, 2.84) * mm});
            skLineSegment(sketch, "E1965", {"start": v(-14.89, 2.84) * mm, "end": v(-14.98, 2.9) * mm});
            skLineSegment(sketch, "E1966", {"start": v(-14.98, 2.9) * mm, "end": v(-15.04, 2.93) * mm});
            skLineSegment(sketch, "E1967", {"start": v(-15.04, 2.93) * mm, "end": v(-15.19, 3.02) * mm});
            skLineSegment(sketch, "E1968", {"start": v(-15.19, 3.02) * mm, "end": v(-15.2, 3.04) * mm});
            skLineSegment(sketch, "E1969", {"start": v(-15.2, 3.04) * mm, "end": v(-15.4, 3.16) * mm});
            skLineSegment(sketch, "E1970", {"start": v(-15.4, 3.16) * mm, "end": v(-15.41, 3.18) * mm});
            skLineSegment(sketch, "E1971", {"start": v(-15.41, 3.18) * mm, "end": v(-15.41, 3.18) * mm});
            skLineSegment(sketch, "E1972", {"start": v(-15.41, 3.18) * mm, "end": v(-15.57, 3.3) * mm});
            skLineSegment(sketch, "E1973", {"start": v(-15.57, 3.3) * mm, "end": v(-15.59, 3.3) * mm});
            skLineSegment(sketch, "E1974", {"start": v(-15.59, 3.3) * mm, "end": v(-15.65, 3.35) * mm});
            skLineSegment(sketch, "E1975", {"start": v(-15.65, 3.35) * mm, "end": v(-15.89, 3.55) * mm});
            skLineSegment(sketch, "E1976", {"start": v(-15.89, 3.55) * mm, "end": v(-15.93, 3.6) * mm});
            skLineSegment(sketch, "E1977", {"start": v(-15.93, 3.6) * mm, "end": v(-15.97, 3.67) * mm});
            skLineSegment(sketch, "E1978", {"start": v(-15.97, 3.67) * mm, "end": v(-15.92, 3.92) * mm});
            skLineSegment(sketch, "E1979", {"start": v(-15.92, 3.92) * mm, "end": v(-15.84, 4.17) * mm});
            skLineSegment(sketch, "E1980", {"start": v(-15.84, 4.17) * mm, "end": v(-15.78, 4.22) * mm});
            skLineSegment(sketch, "E1981", {"start": v(-15.78, 4.22) * mm, "end": v(-15.72, 4.24) * mm});
            skLineSegment(sketch, "E1982", {"start": v(-15.72, 4.24) * mm, "end": v(-15.41, 4.3) * mm});
            skLineSegment(sketch, "E1983", {"start": v(-15.41, 4.3) * mm, "end": v(-15.34, 4.32) * mm});
            skLineSegment(sketch, "E1984", {"start": v(-15.34, 4.32) * mm, "end": v(-15.32, 4.32) * mm});
            skLineSegment(sketch, "E1985", {"start": v(-15.32, 4.32) * mm, "end": v(-15.13, 4.35) * mm});
            skLineSegment(sketch, "E1986", {"start": v(-15.13, 4.35) * mm, "end": v(-15.12, 4.35) * mm});
            skLineSegment(sketch, "E1987", {"start": v(-15.12, 4.35) * mm, "end": v(-15.1, 4.35) * mm});
            skLineSegment(sketch, "E1988", {"start": v(-15.1, 4.35) * mm, "end": v(-14.88, 4.38) * mm});
            skLineSegment(sketch, "E1989", {"start": v(-14.88, 4.38) * mm, "end": v(-14.85, 4.38) * mm});
            skLineSegment(sketch, "E1990", {"start": v(-14.85, 4.38) * mm, "end": v(-14.68, 4.4) * mm});
            skLineSegment(sketch, "E1991", {"start": v(-14.68, 4.4) * mm, "end": v(-14.6, 4.4) * mm});
            skLineSegment(sketch, "E1992", {"start": v(-14.6, 4.4) * mm, "end": v(-14.5, 4.4) * mm});
            skLineSegment(sketch, "E1993", {"start": v(-14.5, 4.4) * mm, "end": v(-14.39, 4.4) * mm});
            skLineSegment(sketch, "E1994", {"start": v(-14.39, 4.4) * mm, "end": v(-14.29, 4.4) * mm});
            skLineSegment(sketch, "E1995", {"start": v(-14.29, 4.4) * mm, "end": v(-14.24, 4.41) * mm});
            skLineSegment(sketch, "E1996", {"start": v(-14.24, 4.41) * mm, "end": v(-14.2, 4.42) * mm});
            skLineSegment(sketch, "E1997", {"start": v(-14.2, 4.42) * mm, "end": v(-14.2, 4.42) * mm});
            skLineSegment(sketch, "E1998", {"start": v(-14.2, 4.42) * mm, "end": v(-14.18, 4.44) * mm});
            skLineSegment(sketch, "E1999", {"start": v(-14.18, 4.44) * mm, "end": v(-14, 4.97) * mm});
            skLineSegment(sketch, "E2000", {"start": v(-14, 4.97) * mm, "end": v(-14, 4.99) * mm});
            skLineSegment(sketch, "E2001", {"start": v(-14, 4.99) * mm, "end": v(-14.01, 5) * mm});
            skLineSegment(sketch, "E2002", {"start": v(-14.01, 5) * mm, "end": v(-14.03, 5.03) * mm});
            skLineSegment(sketch, "E2003", {"start": v(-14.03, 5.03) * mm, "end": v(-14.07, 5.06) * mm});
            skLineSegment(sketch, "E2004", {"start": v(-14.07, 5.06) * mm, "end": v(-14.15, 5.12) * mm});
            skLineSegment(sketch, "E2005", {"start": v(-14.15, 5.12) * mm, "end": v(-14.24, 5.2) * mm});
            skLineSegment(sketch, "E2006", {"start": v(-14.24, 5.2) * mm, "end": v(-14.32, 5.26) * mm});
            skLineSegment(sketch, "E2007", {"start": v(-14.32, 5.26) * mm, "end": v(-14.37, 5.3) * mm});
            skLineSegment(sketch, "E2008", {"start": v(-14.37, 5.3) * mm, "end": v(-14.5, 5.42) * mm});
            skLineSegment(sketch, "E2009", {"start": v(-14.5, 5.42) * mm, "end": v(-14.52, 5.44) * mm});
            skLineSegment(sketch, "E2010", {"start": v(-14.52, 5.44) * mm, "end": v(-14.68, 5.59) * mm});
            skLineSegment(sketch, "E2011", {"start": v(-14.68, 5.59) * mm, "end": v(-14.7, 5.6) * mm});
            skLineSegment(sketch, "E2012", {"start": v(-14.7, 5.6) * mm, "end": v(-14.7, 5.61) * mm});
            skLineSegment(sketch, "E2013", {"start": v(-14.7, 5.61) * mm, "end": v(-14.84, 5.75) * mm});
            skLineSegment(sketch, "E2014", {"start": v(-14.84, 5.75) * mm, "end": v(-14.86, 5.76) * mm});
            skLineSegment(sketch, "E2015", {"start": v(-14.86, 5.76) * mm, "end": v(-14.9, 5.82) * mm});
            skLineSegment(sketch, "E2016", {"start": v(-14.9, 5.82) * mm, "end": v(-15.11, 6.05) * mm});
            skLineSegment(sketch, "E2017", {"start": v(-15.11, 6.05) * mm, "end": v(-15.15, 6.1) * mm});
            skLineSegment(sketch, "E2018", {"start": v(-15.15, 6.1) * mm, "end": v(-15.17, 6.18) * mm});
            skLineSegment(sketch, "E2019", {"start": v(-15.17, 6.18) * mm, "end": v(-15.09, 6.43) * mm});
            skLineSegment(sketch, "E2020", {"start": v(-15.09, 6.43) * mm, "end": v(-14.97, 6.66) * mm});
            skLineSegment(sketch, "E2021", {"start": v(-14.97, 6.66) * mm, "end": v(-14.9, 6.7) * mm});
            skLineSegment(sketch, "E2022", {"start": v(-14.9, 6.7) * mm, "end": v(-14.84, 6.7) * mm});
            skLineSegment(sketch, "E2023", {"start": v(-14.84, 6.7) * mm, "end": v(-14.52, 6.72) * mm});
            skLineSegment(sketch, "E2024", {"start": v(-14.52, 6.72) * mm, "end": v(-14.45, 6.72) * mm});
            skLineSegment(sketch, "E2025", {"start": v(-14.45, 6.72) * mm, "end": v(-14.43, 6.72) * mm});
            skLineSegment(sketch, "E2026", {"start": v(-14.43, 6.72) * mm, "end": v(-14.23, 6.72) * mm});
            skLineSegment(sketch, "E2027", {"start": v(-14.23, 6.72) * mm, "end": v(-14.23, 6.72) * mm});
            skLineSegment(sketch, "E2028", {"start": v(-14.23, 6.72) * mm, "end": v(-14.2, 6.72) * mm});
            skLineSegment(sketch, "E2029", {"start": v(-14.2, 6.72) * mm, "end": v(-13.98, 6.7) * mm});
            skLineSegment(sketch, "E2030", {"start": v(-13.98, 6.7) * mm, "end": v(-13.96, 6.7) * mm});
            skLineSegment(sketch, "E2031", {"start": v(-13.96, 6.7) * mm, "end": v(-13.78, 6.7) * mm});
            skLineSegment(sketch, "E2032", {"start": v(-13.78, 6.7) * mm, "end": v(-13.71, 6.69) * mm});
            skLineSegment(sketch, "E2033", {"start": v(-13.71, 6.69) * mm, "end": v(-13.6, 6.67) * mm});
            skLineSegment(sketch, "E2034", {"start": v(-13.6, 6.67) * mm, "end": v(-13.5, 6.66) * mm});
            skLineSegment(sketch, "E2035", {"start": v(-13.5, 6.66) * mm, "end": v(-13.4, 6.64) * mm});
            skLineSegment(sketch, "E2036", {"start": v(-13.4, 6.64) * mm, "end": v(-13.34, 6.64) * mm});
            skLineSegment(sketch, "E2037", {"start": v(-13.34, 6.64) * mm, "end": v(-13.32, 6.64) * mm});
            skLineSegment(sketch, "E2038", {"start": v(-13.32, 6.64) * mm, "end": v(-13.3, 6.64) * mm});
            skLineSegment(sketch, "E2039", {"start": v(-13.3, 6.64) * mm, "end": v(-13.28, 6.65) * mm});
            skLineSegment(sketch, "E2040", {"start": v(-13.28, 6.65) * mm, "end": v(-13.02, 7.15) * mm});
            skLineSegment(sketch, "E2041", {"start": v(-13.02, 7.15) * mm, "end": v(-13.02, 7.17) * mm});
            skLineSegment(sketch, "E2042", {"start": v(-13.02, 7.17) * mm, "end": v(-13.03, 7.19) * mm});
            skLineSegment(sketch, "E2043", {"start": v(-13.03, 7.19) * mm, "end": v(-13.04, 7.21) * mm});
            skLineSegment(sketch, "E2044", {"start": v(-13.04, 7.21) * mm, "end": v(-13.07, 7.25) * mm});
            skLineSegment(sketch, "E2045", {"start": v(-13.07, 7.25) * mm, "end": v(-13.14, 7.33) * mm});
            skLineSegment(sketch, "E2046", {"start": v(-13.14, 7.33) * mm, "end": v(-13.22, 7.4) * mm});
            skLineSegment(sketch, "E2047", {"start": v(-13.22, 7.4) * mm, "end": v(-13.3, 7.49) * mm});
            skLineSegment(sketch, "E2048", {"start": v(-13.3, 7.49) * mm, "end": v(-13.34, 7.54) * mm});
            skLineSegment(sketch, "E2049", {"start": v(-13.34, 7.54) * mm, "end": v(-13.45, 7.68) * mm});
            skLineSegment(sketch, "E2050", {"start": v(-13.45, 7.68) * mm, "end": v(-13.46, 7.7) * mm});
            skLineSegment(sketch, "E2051", {"start": v(-13.46, 7.7) * mm, "end": v(-13.6, 7.87) * mm});
            skLineSegment(sketch, "E2052", {"start": v(-13.6, 7.87) * mm, "end": v(-13.61, 7.9) * mm});
            skLineSegment(sketch, "E2053", {"start": v(-13.61, 7.9) * mm, "end": v(-13.61, 7.9) * mm});
            skLineSegment(sketch, "E2054", {"start": v(-13.61, 7.9) * mm, "end": v(-13.73, 8.06) * mm});
            skLineSegment(sketch, "E2055", {"start": v(-13.73, 8.06) * mm, "end": v(-13.74, 8.07) * mm});
            skLineSegment(sketch, "E2056", {"start": v(-13.74, 8.07) * mm, "end": v(-13.78, 8.13) * mm});
            skLineSegment(sketch, "E2057", {"start": v(-13.78, 8.13) * mm, "end": v(-13.95, 8.4) * mm});
            skLineSegment(sketch, "E2058", {"start": v(-13.95, 8.4) * mm, "end": v(-13.97, 8.46) * mm});
            skLineSegment(sketch, "E2059", {"start": v(-13.97, 8.46) * mm, "end": v(-13.98, 8.53) * mm});
            skLineSegment(sketch, "E2060", {"start": v(-13.98, 8.53) * mm, "end": v(-13.86, 8.77) * mm});
            skLineSegment(sketch, "E2061", {"start": v(-13.86, 8.77) * mm, "end": v(-13.7, 8.97) * mm});
            skLineSegment(sketch, "E2062", {"start": v(-13.7, 8.97) * mm, "end": v(-13.63, 9) * mm});
            skLineSegment(sketch, "E2063", {"start": v(-13.63, 9) * mm, "end": v(-13.57, 9) * mm});
            skLineSegment(sketch, "E2064", {"start": v(-13.57, 9) * mm, "end": v(-13.25, 8.96) * mm});
            skLineSegment(sketch, "E2065", {"start": v(-13.25, 8.96) * mm, "end": v(-13.18, 8.95) * mm});
            skLineSegment(sketch, "E2066", {"start": v(-13.18, 8.95) * mm, "end": v(-13.16, 8.95) * mm});
            skLineSegment(sketch, "E2067", {"start": v(-13.16, 8.95) * mm, "end": v(-12.97, 8.92) * mm});
            skLineSegment(sketch, "E2068", {"start": v(-12.97, 8.92) * mm, "end": v(-12.97, 8.91) * mm});
            skLineSegment(sketch, "E2069", {"start": v(-12.97, 8.91) * mm, "end": v(-12.94, 8.91) * mm});
            skLineSegment(sketch, "E2070", {"start": v(-12.94, 8.91) * mm, "end": v(-12.72, 8.86) * mm});
            skLineSegment(sketch, "E2071", {"start": v(-12.72, 8.86) * mm, "end": v(-12.7, 8.86) * mm});
            skLineSegment(sketch, "E2072", {"start": v(-12.7, 8.86) * mm, "end": v(-12.53, 8.82) * mm});
            skLineSegment(sketch, "E2073", {"start": v(-12.53, 8.82) * mm, "end": v(-12.46, 8.8) * mm});
            skLineSegment(sketch, "E2074", {"start": v(-12.46, 8.8) * mm, "end": v(-12.36, 8.77) * mm});
            skLineSegment(sketch, "E2075", {"start": v(-12.36, 8.77) * mm, "end": v(-12.25, 8.73) * mm});
            skLineSegment(sketch, "E2076", {"start": v(-12.25, 8.73) * mm, "end": v(-12.16, 8.7) * mm});
            skLineSegment(sketch, "E2077", {"start": v(-12.16, 8.7) * mm, "end": v(-12.1, 8.7) * mm});
            skLineSegment(sketch, "E2078", {"start": v(-12.1, 8.7) * mm, "end": v(-12.08, 8.69) * mm});
            skLineSegment(sketch, "E2079", {"start": v(-12.08, 8.69) * mm, "end": v(-12.06, 8.7) * mm});
            skLineSegment(sketch, "E2080", {"start": v(-12.06, 8.7) * mm, "end": v(-12.04, 8.7) * mm});
            skLineSegment(sketch, "E2081", {"start": v(-12.04, 8.7) * mm, "end": v(-11.7, 9.15) * mm});
            skLineSegment(sketch, "E2082", {"start": v(-11.7, 9.15) * mm, "end": v(-11.7, 9.17) * mm});
            skLineSegment(sketch, "E2083", {"start": v(-11.7, 9.17) * mm, "end": v(-11.7, 9.18) * mm});
            skLineSegment(sketch, "E2084", {"start": v(-11.7, 9.18) * mm, "end": v(-11.72, 9.21) * mm});
            skLineSegment(sketch, "E2085", {"start": v(-11.72, 9.21) * mm, "end": v(-11.74, 9.26) * mm});
            skLineSegment(sketch, "E2086", {"start": v(-11.74, 9.26) * mm, "end": v(-11.8, 9.34) * mm});
            skLineSegment(sketch, "E2087", {"start": v(-11.8, 9.34) * mm, "end": v(-11.86, 9.43) * mm});
            skLineSegment(sketch, "E2088", {"start": v(-11.86, 9.43) * mm, "end": v(-11.92, 9.52) * mm});
            skLineSegment(sketch, "E2089", {"start": v(-11.92, 9.52) * mm, "end": v(-11.95, 9.58) * mm});
            skLineSegment(sketch, "E2090", {"start": v(-11.95, 9.58) * mm, "end": v(-12.04, 9.74) * mm});
            skLineSegment(sketch, "E2091", {"start": v(-12.04, 9.74) * mm, "end": v(-12.05, 9.75) * mm});
            skLineSegment(sketch, "E2092", {"start": v(-12.05, 9.75) * mm, "end": v(-12.16, 9.95) * mm});
            skLineSegment(sketch, "E2093", {"start": v(-12.16, 9.95) * mm, "end": v(-12.17, 9.97) * mm});
            skLineSegment(sketch, "E2094", {"start": v(-12.17, 9.97) * mm, "end": v(-12.17, 9.98) * mm});
            skLineSegment(sketch, "E2095", {"start": v(-12.17, 9.98) * mm, "end": v(-12.26, 10.15) * mm});
            skLineSegment(sketch, "E2096", {"start": v(-12.26, 10.15) * mm, "end": v(-12.27, 10.17) * mm});
            skLineSegment(sketch, "E2097", {"start": v(-12.27, 10.17) * mm, "end": v(-12.3, 10.24) * mm});
            skLineSegment(sketch, "E2098", {"start": v(-12.3, 10.24) * mm, "end": v(-12.42, 10.53) * mm});
            skLineSegment(sketch, "E2099", {"start": v(-12.42, 10.53) * mm, "end": v(-12.44, 10.59) * mm});
            skLineSegment(sketch, "E2100", {"start": v(-12.44, 10.59) * mm, "end": v(-12.43, 10.67) * mm});
            skLineSegment(sketch, "E2101", {"start": v(-12.43, 10.67) * mm, "end": v(-12.28, 10.88) * mm});
            skLineSegment(sketch, "E2102", {"start": v(-12.28, 10.88) * mm, "end": v(-12.09, 11.06) * mm});
            skLineSegment(sketch, "E2103", {"start": v(-12.09, 11.06) * mm, "end": v(-12.01, 11.07) * mm});
            skLineSegment(sketch, "E2104", {"start": v(-12.01, 11.07) * mm, "end": v(-11.95, 11.06) * mm});
            skLineSegment(sketch, "E2105", {"start": v(-11.95, 11.06) * mm, "end": v(-11.65, 10.97) * mm});
            skLineSegment(sketch, "E2106", {"start": v(-11.65, 10.97) * mm, "end": v(-11.58, 10.95) * mm});
            skLineSegment(sketch, "E2107", {"start": v(-11.58, 10.95) * mm, "end": v(-11.56, 10.94) * mm});
            skLineSegment(sketch, "E2108", {"start": v(-11.56, 10.94) * mm, "end": v(-11.37, 10.88) * mm});
            skLineSegment(sketch, "E2109", {"start": v(-11.37, 10.88) * mm, "end": v(-11.37, 10.88) * mm});
            skLineSegment(sketch, "E2110", {"start": v(-11.37, 10.88) * mm, "end": v(-11.34, 10.87) * mm});
            skLineSegment(sketch, "E2111", {"start": v(-11.34, 10.87) * mm, "end": v(-11.14, 10.8) * mm});
            skLineSegment(sketch, "E2112", {"start": v(-11.14, 10.8) * mm, "end": v(-11.12, 10.78) * mm});
            skLineSegment(sketch, "E2113", {"start": v(-11.12, 10.78) * mm, "end": v(-10.95, 10.71) * mm});
            skLineSegment(sketch, "E2114", {"start": v(-10.95, 10.71) * mm, "end": v(-10.9, 10.68) * mm});
            skLineSegment(sketch, "E2115", {"start": v(-10.9, 10.68) * mm, "end": v(-10.8, 10.64) * mm});
            skLineSegment(sketch, "E2116", {"start": v(-10.8, 10.64) * mm, "end": v(-10.7, 10.59) * mm});
            skLineSegment(sketch, "E2117", {"start": v(-10.7, 10.59) * mm, "end": v(-10.6, 10.54) * mm});
            skLineSegment(sketch, "E2118", {"start": v(-10.6, 10.54) * mm, "end": v(-10.56, 10.52) * mm});
            skLineSegment(sketch, "E2119", {"start": v(-10.56, 10.52) * mm, "end": v(-10.53, 10.51) * mm});
            skLineSegment(sketch, "E2120", {"start": v(-10.53, 10.51) * mm, "end": v(-10.51, 10.51) * mm});
            skLineSegment(sketch, "E2121", {"start": v(-10.51, 10.51) * mm, "end": v(-10.5, 10.52) * mm});
            skLineSegment(sketch, "E2122", {"start": v(-10.5, 10.52) * mm, "end": v(-10.08, 10.9) * mm});
            skLineSegment(sketch, "E2123", {"start": v(-10.08, 10.9) * mm, "end": v(-10.08, 10.92) * mm});
            skLineSegment(sketch, "E2124", {"start": v(-10.08, 10.92) * mm, "end": v(-10.08, 10.94) * mm});
            skLineSegment(sketch, "E2125", {"start": v(-10.08, 10.94) * mm, "end": v(-10.09, 10.97) * mm});
            skLineSegment(sketch, "E2126", {"start": v(-10.09, 10.97) * mm, "end": v(-10.1, 11.02) * mm});
            skLineSegment(sketch, "E2127", {"start": v(-10.1, 11.02) * mm, "end": v(-10.15, 11.11) * mm});
            skLineSegment(sketch, "E2128", {"start": v(-10.15, 11.11) * mm, "end": v(-10.2, 11.21) * mm});
            skLineSegment(sketch, "E2129", {"start": v(-10.2, 11.21) * mm, "end": v(-10.24, 11.31) * mm});
            skLineSegment(sketch, "E2130", {"start": v(-10.24, 11.31) * mm, "end": v(-10.26, 11.38) * mm});
            skLineSegment(sketch, "E2131", {"start": v(-10.26, 11.38) * mm, "end": v(-10.33, 11.54) * mm});
            skLineSegment(sketch, "E2132", {"start": v(-10.33, 11.54) * mm, "end": v(-10.33, 11.56) * mm});
            skLineSegment(sketch, "E2133", {"start": v(-10.33, 11.56) * mm, "end": v(-10.4, 11.77) * mm});
            skLineSegment(sketch, "E2134", {"start": v(-10.4, 11.77) * mm, "end": v(-10.41, 11.8) * mm});
            skLineSegment(sketch, "E2135", {"start": v(-10.41, 11.8) * mm, "end": v(-10.41, 11.8) * mm});
            skLineSegment(sketch, "E2136", {"start": v(-10.41, 11.8) * mm, "end": v(-10.47, 11.99) * mm});
            skLineSegment(sketch, "E2137", {"start": v(-10.47, 11.99) * mm, "end": v(-10.48, 12) * mm});
            skLineSegment(sketch, "E2138", {"start": v(-10.48, 12) * mm, "end": v(-10.5, 12.08) * mm});
            skLineSegment(sketch, "E2139", {"start": v(-10.5, 12.08) * mm, "end": v(-10.57, 12.38) * mm});
            skLineSegment(sketch, "E2140", {"start": v(-10.57, 12.38) * mm, "end": v(-10.58, 12.45) * mm});
            skLineSegment(sketch, "E2141", {"start": v(-10.58, 12.45) * mm, "end": v(-10.56, 12.52) * mm});
            skLineSegment(sketch, "E2142", {"start": v(-10.56, 12.52) * mm, "end": v(-10.37, 12.7) * mm});
            skLineSegment(sketch, "E2143", {"start": v(-10.37, 12.7) * mm, "end": v(-10.16, 12.85) * mm});
            skLineSegment(sketch, "E2144", {"start": v(-10.16, 12.85) * mm, "end": v(-10.08, 12.85) * mm});
            skLineSegment(sketch, "E2145", {"start": v(-10.08, 12.85) * mm, "end": v(-10.02, 12.83) * mm});
            skLineSegment(sketch, "E2146", {"start": v(-10.02, 12.83) * mm, "end": v(-9.73, 12.7) * mm});
            skLineSegment(sketch, "E2147", {"start": v(-9.73, 12.7) * mm, "end": v(-9.67, 12.67) * mm});
            skLineSegment(sketch, "E2148", {"start": v(-9.67, 12.67) * mm, "end": v(-9.65, 12.65) * mm});
            skLineSegment(sketch, "E2149", {"start": v(-9.65, 12.65) * mm, "end": v(-9.48, 12.56) * mm});
            skLineSegment(sketch, "E2150", {"start": v(-9.48, 12.56) * mm, "end": v(-9.48, 12.56) * mm});
            skLineSegment(sketch, "E2151", {"start": v(-9.48, 12.56) * mm, "end": v(-9.45, 12.55) * mm});
            skLineSegment(sketch, "E2152", {"start": v(-9.45, 12.55) * mm, "end": v(-9.26, 12.44) * mm});
            skLineSegment(sketch, "E2153", {"start": v(-9.26, 12.44) * mm, "end": v(-9.24, 12.43) * mm});
            skLineSegment(sketch, "E2154", {"start": v(-9.24, 12.43) * mm, "end": v(-9.1, 12.33) * mm});
            skLineSegment(sketch, "E2155", {"start": v(-9.1, 12.33) * mm, "end": v(-9.04, 12.3) * mm});
            skLineSegment(sketch, "E2156", {"start": v(-9.04, 12.3) * mm, "end": v(-8.95, 12.23) * mm});
            skLineSegment(sketch, "E2157", {"start": v(-8.95, 12.23) * mm, "end": v(-8.86, 12.16) * mm});
            skLineSegment(sketch, "E2158", {"start": v(-8.86, 12.16) * mm, "end": v(-8.78, 12.1) * mm});
            skLineSegment(sketch, "E2159", {"start": v(-8.78, 12.1) * mm, "end": v(-8.73, 12.08) * mm});
            skLineSegment(sketch, "E2160", {"start": v(-8.73, 12.08) * mm, "end": v(-8.7, 12.07) * mm});
            skLineSegment(sketch, "E2161", {"start": v(-8.7, 12.07) * mm, "end": v(-8.69, 12.06) * mm});
            skLineSegment(sketch, "E2162", {"start": v(-8.69, 12.06) * mm, "end": v(-8.67, 12.06) * mm});
            skLineSegment(sketch, "E2163", {"start": v(-8.67, 12.06) * mm, "end": v(-8.2, 12.38) * mm});
            skLineSegment(sketch, "E2164", {"start": v(-8.2, 12.38) * mm, "end": v(-8.2, 12.4) * mm});
            skLineSegment(sketch, "E2165", {"start": v(-8.2, 12.4) * mm, "end": v(-8.2, 12.42) * mm});
            skLineSegment(sketch, "E2166", {"start": v(-8.2, 12.42) * mm, "end": v(-8.2, 12.45) * mm});
            skLineSegment(sketch, "E2167", {"start": v(-8.2, 12.45) * mm, "end": v(-8.2, 12.5) * mm});
            skLineSegment(sketch, "E2168", {"start": v(-8.2, 12.5) * mm, "end": v(-8.23, 12.6) * mm});
            skLineSegment(sketch, "E2169", {"start": v(-8.23, 12.6) * mm, "end": v(-8.26, 12.7) * mm});
            skLineSegment(sketch, "E2170", {"start": v(-8.26, 12.7) * mm, "end": v(-8.29, 12.8) * mm});
            skLineSegment(sketch, "E2171", {"start": v(-8.29, 12.8) * mm, "end": v(-8.3, 12.88) * mm});
            skLineSegment(sketch, "E2172", {"start": v(-8.3, 12.88) * mm, "end": v(-8.34, 13.05) * mm});
            skLineSegment(sketch, "E2173", {"start": v(-8.34, 13.05) * mm, "end": v(-8.34, 13.07) * mm});
            skLineSegment(sketch, "E2174", {"start": v(-8.34, 13.07) * mm, "end": v(-8.38, 13.29) * mm});
            skLineSegment(sketch, "E2175", {"start": v(-8.38, 13.29) * mm, "end": v(-8.39, 13.31) * mm});
            skLineSegment(sketch, "E2176", {"start": v(-8.39, 13.31) * mm, "end": v(-8.39, 13.32) * mm});
            skLineSegment(sketch, "E2177", {"start": v(-8.39, 13.32) * mm, "end": v(-8.4, 13.51) * mm});
            skLineSegment(sketch, "E2178", {"start": v(-8.4, 13.51) * mm, "end": v(-8.41, 13.53) * mm});
            skLineSegment(sketch, "E2179", {"start": v(-8.41, 13.53) * mm, "end": v(-8.42, 13.6) * mm});
            skLineSegment(sketch, "E2180", {"start": v(-8.42, 13.6) * mm, "end": v(-8.45, 13.92) * mm});
            skLineSegment(sketch, "E2181", {"start": v(-8.45, 13.92) * mm, "end": v(-8.44, 13.98) * mm});
            skLineSegment(sketch, "E2182", {"start": v(-8.44, 13.98) * mm, "end": v(-8.41, 14.05) * mm});
            skLineSegment(sketch, "E2183", {"start": v(-8.41, 14.05) * mm, "end": v(-8.2, 14.2) * mm});
            skLineSegment(sketch, "E2184", {"start": v(-8.2, 14.2) * mm, "end": v(-7.96, 14.31) * mm});
            skLineSegment(sketch, "E2185", {"start": v(-7.96, 14.31) * mm, "end": v(-7.89, 14.3) * mm});
            skLineSegment(sketch, "E2186", {"start": v(-7.89, 14.3) * mm, "end": v(-7.83, 14.27) * mm});
            skLineSegment(sketch, "E2187", {"start": v(-7.83, 14.27) * mm, "end": v(-7.57, 14.1) * mm});
            skLineSegment(sketch, "E2188", {"start": v(-7.57, 14.1) * mm, "end": v(-7.51, 14.05) * mm});
            skLineSegment(sketch, "E2189", {"start": v(-7.51, 14.05) * mm, "end": v(-7.5, 14.04) * mm});
            skLineSegment(sketch, "E2190", {"start": v(-7.5, 14.04) * mm, "end": v(-7.34, 13.92) * mm});
            skLineSegment(sketch, "E2191", {"start": v(-7.34, 13.92) * mm, "end": v(-7.34, 13.92) * mm});
            skLineSegment(sketch, "E2192", {"start": v(-7.34, 13.92) * mm, "end": v(-7.32, 13.9) * mm});
            skLineSegment(sketch, "E2193", {"start": v(-7.32, 13.9) * mm, "end": v(-7.15, 13.76) * mm});
            skLineSegment(sketch, "E2194", {"start": v(-7.15, 13.76) * mm, "end": v(-7.13, 13.75) * mm});
            skLineSegment(sketch, "E2195", {"start": v(-7.13, 13.75) * mm, "end": v(-7, 13.63) * mm});
            skLineSegment(sketch, "E2196", {"start": v(-7, 13.63) * mm, "end": v(-6.95, 13.58) * mm});
            skLineSegment(sketch, "E2197", {"start": v(-6.95, 13.58) * mm, "end": v(-6.87, 13.5) * mm});
            skLineSegment(sketch, "E2198", {"start": v(-6.87, 13.5) * mm, "end": v(-6.8, 13.43) * mm});
            skLineSegment(sketch, "E2199", {"start": v(-6.8, 13.43) * mm, "end": v(-6.72, 13.35) * mm});
            skLineSegment(sketch, "E2200", {"start": v(-6.72, 13.35) * mm, "end": v(-6.68, 13.32) * mm});
            skLineSegment(sketch, "E2201", {"start": v(-6.68, 13.32) * mm, "end": v(-6.66, 13.3) * mm});
            skLineSegment(sketch, "E2202", {"start": v(-6.66, 13.3) * mm, "end": v(-6.64, 13.3) * mm});
            skLineSegment(sketch, "E2203", {"start": v(-6.64, 13.3) * mm, "end": v(-6.62, 13.3) * mm});
            skLineSegment(sketch, "E2204", {"start": v(-6.62, 13.3) * mm, "end": v(-6.11, 13.54) * mm});
            skLineSegment(sketch, "E2205", {"start": v(-6.11, 13.54) * mm, "end": v(-6.1, 13.56) * mm});
            skLineSegment(sketch, "E2206", {"start": v(-6.1, 13.56) * mm, "end": v(-6.1, 13.57) * mm});
            skLineSegment(sketch, "E2207", {"start": v(-6.1, 13.57) * mm, "end": v(-6.1, 13.6) * mm});
            skLineSegment(sketch, "E2208", {"start": v(-6.1, 13.6) * mm, "end": v(-6.1, 13.65) * mm});
            skLineSegment(sketch, "E2209", {"start": v(-6.1, 13.65) * mm, "end": v(-6.1, 13.75) * mm});
            skLineSegment(sketch, "E2210", {"start": v(-6.1, 13.75) * mm, "end": v(-6.12, 13.87) * mm});
            skLineSegment(sketch, "E2211", {"start": v(-6.12, 13.87) * mm, "end": v(-6.13, 13.97) * mm});
            skLineSegment(sketch, "E2212", {"start": v(-6.13, 13.97) * mm, "end": v(-6.13, 14.04) * mm});
            skLineSegment(sketch, "E2213", {"start": v(-6.13, 14.04) * mm, "end": v(-6.14, 14.22) * mm});
            skLineSegment(sketch, "E2214", {"start": v(-6.14, 14.22) * mm, "end": v(-6.14, 14.24) * mm});
            skLineSegment(sketch, "E2215", {"start": v(-6.14, 14.24) * mm, "end": v(-6.14, 14.46) * mm});
            skLineSegment(sketch, "E2216", {"start": v(-6.14, 14.46) * mm, "end": v(-6.14, 14.49) * mm});
            skLineSegment(sketch, "E2217", {"start": v(-6.14, 14.49) * mm, "end": v(-6.14, 14.5) * mm});
            skLineSegment(sketch, "E2218", {"start": v(-6.14, 14.5) * mm, "end": v(-6.13, 14.69) * mm});
            skLineSegment(sketch, "E2219", {"start": v(-6.13, 14.69) * mm, "end": v(-6.13, 14.7) * mm});
            skLineSegment(sketch, "E2220", {"start": v(-6.13, 14.7) * mm, "end": v(-6.13, 14.78) * mm});
            skLineSegment(sketch, "E2221", {"start": v(-6.13, 14.78) * mm, "end": v(-6.1, 15.1) * mm});
            skLineSegment(sketch, "E2222", {"start": v(-6.1, 15.1) * mm, "end": v(-6.1, 15.15) * mm});
            skLineSegment(sketch, "E2223", {"start": v(-6.1, 15.15) * mm, "end": v(-6.05, 15.22) * mm});
            skLineSegment(sketch, "E2224", {"start": v(-6.05, 15.22) * mm, "end": v(-5.82, 15.33) * mm});
            skLineSegment(sketch, "E2225", {"start": v(-5.82, 15.33) * mm, "end": v(-5.56, 15.4) * mm});
            skLineSegment(sketch, "E2226", {"start": v(-5.56, 15.4) * mm, "end": v(-5.5, 15.38) * mm});
            skLineSegment(sketch, "E2227", {"start": v(-5.5, 15.38) * mm, "end": v(-5.44, 15.35) * mm});
            skLineSegment(sketch, "E2228", {"start": v(-5.44, 15.35) * mm, "end": v(-5.21, 15.13) * mm});
            skLineSegment(sketch, "E2229", {"start": v(-5.21, 15.13) * mm, "end": v(-5.16, 15.08) * mm});
            skLineSegment(sketch, "E2230", {"start": v(-5.16, 15.08) * mm, "end": v(-5.15, 15.06) * mm});
            skLineSegment(sketch, "E2231", {"start": v(-5.15, 15.06) * mm, "end": v(-5.01, 14.92) * mm});
            skLineSegment(sketch, "E2232", {"start": v(-5.01, 14.92) * mm, "end": v(-5.01, 14.92) * mm});
            skLineSegment(sketch, "E2233", {"start": v(-5.01, 14.92) * mm, "end": v(-5, 14.9) * mm});
            skLineSegment(sketch, "E2234", {"start": v(-5, 14.9) * mm, "end": v(-4.85, 14.73) * mm});
            skLineSegment(sketch, "E2235", {"start": v(-4.85, 14.73) * mm, "end": v(-4.83, 14.71) * mm});
            skLineSegment(sketch, "E2236", {"start": v(-4.83, 14.71) * mm, "end": v(-4.72, 14.58) * mm});
            skLineSegment(sketch, "E2237", {"start": v(-4.72, 14.58) * mm, "end": v(-4.68, 14.52) * mm});
            skLineSegment(sketch, "E2238", {"start": v(-4.68, 14.52) * mm, "end": v(-4.61, 14.44) * mm});
            skLineSegment(sketch, "E2239", {"start": v(-4.61, 14.44) * mm, "end": v(-4.55, 14.34) * mm});
            skLineSegment(sketch, "E2240", {"start": v(-4.55, 14.34) * mm, "end": v(-4.5, 14.26) * mm});
            skLineSegment(sketch, "E2241", {"start": v(-4.5, 14.26) * mm, "end": v(-4.46, 14.22) * mm});
            skLineSegment(sketch, "E2242", {"start": v(-4.46, 14.22) * mm, "end": v(-4.44, 14.2) * mm});
            skLineSegment(sketch, "E2243", {"start": v(-4.44, 14.2) * mm, "end": v(-4.42, 14.2) * mm});
            skLineSegment(sketch, "E2244", {"start": v(-4.42, 14.2) * mm, "end": v(-4.4, 14.19) * mm});
            skLineSegment(sketch, "E2245", {"start": v(-4.4, 14.19) * mm, "end": v(-3.86, 14.34) * mm});
            skLineSegment(sketch, "E2246", {"start": v(-3.86, 14.34) * mm, "end": v(-3.85, 14.36) * mm});
            skLineSegment(sketch, "E2247", {"start": v(-3.85, 14.36) * mm, "end": v(-3.84, 14.37) * mm});
            skLineSegment(sketch, "E2248", {"start": v(-3.84, 14.37) * mm, "end": v(-3.83, 14.4) * mm});
            skLineSegment(sketch, "E2249", {"start": v(-3.83, 14.4) * mm, "end": v(-3.83, 14.45) * mm});
            skLineSegment(sketch, "E2250", {"start": v(-3.83, 14.45) * mm, "end": v(-3.82, 14.55) * mm});
            skLineSegment(sketch, "E2251", {"start": v(-3.82, 14.55) * mm, "end": v(-3.82, 14.67) * mm});
            skLineSegment(sketch, "E2252", {"start": v(-3.82, 14.67) * mm, "end": v(-3.8, 14.77) * mm});
            skLineSegment(sketch, "E2253", {"start": v(-3.8, 14.77) * mm, "end": v(-3.8, 14.84) * mm});
            skLineSegment(sketch, "E2254", {"start": v(-3.8, 14.84) * mm, "end": v(-3.78, 15.02) * mm});
            skLineSegment(sketch, "E2255", {"start": v(-3.78, 15.02) * mm, "end": v(-3.78, 15.04) * mm});
            skLineSegment(sketch, "E2256", {"start": v(-3.78, 15.04) * mm, "end": v(-3.74, 15.26) * mm});
            skLineSegment(sketch, "E2257", {"start": v(-3.74, 15.26) * mm, "end": v(-3.74, 15.28) * mm});
            skLineSegment(sketch, "E2258", {"start": v(-3.74, 15.28) * mm, "end": v(-3.74, 15.29) * mm});
            skLineSegment(sketch, "E2259", {"start": v(-3.74, 15.29) * mm, "end": v(-3.7, 15.48) * mm});
            skLineSegment(sketch, "E2260", {"start": v(-3.7, 15.48) * mm, "end": v(-3.7, 15.5) * mm});
            skLineSegment(sketch, "E2261", {"start": v(-3.7, 15.5) * mm, "end": v(-3.68, 15.57) * mm});
            skLineSegment(sketch, "E2262", {"start": v(-3.68, 15.57) * mm, "end": v(-3.6, 15.88) * mm});
            skLineSegment(sketch, "E2263", {"start": v(-3.6, 15.88) * mm, "end": v(-3.58, 15.94) * mm});
            skLineSegment(sketch, "E2264", {"start": v(-3.58, 15.94) * mm, "end": v(-3.53, 16) * mm});
            skLineSegment(sketch, "E2265", {"start": v(-3.53, 16) * mm, "end": v(-3.28, 16.07) * mm});
            skLineSegment(sketch, "E2266", {"start": v(-3.28, 16.07) * mm, "end": v(-3.02, 16.1) * mm});
            skLineSegment(sketch, "E2267", {"start": v(-3.02, 16.1) * mm, "end": v(-2.95, 16.06) * mm});
            skLineSegment(sketch, "E2268", {"start": v(-2.95, 16.06) * mm, "end": v(-2.9, 16.02) * mm});
            skLineSegment(sketch, "E2269", {"start": v(-2.9, 16.02) * mm, "end": v(-2.72, 15.77) * mm});
            skLineSegment(sketch, "E2270", {"start": v(-2.72, 15.77) * mm, "end": v(-2.68, 15.7) * mm});
            skLineSegment(sketch, "E2271", {"start": v(-2.68, 15.7) * mm, "end": v(-2.67, 15.7) * mm});
            skLineSegment(sketch, "E2272", {"start": v(-2.67, 15.7) * mm, "end": v(-2.56, 15.53) * mm});
            skLineSegment(sketch, "E2273", {"start": v(-2.56, 15.53) * mm, "end": v(-2.55, 15.53) * mm});
            skLineSegment(sketch, "E2274", {"start": v(-2.55, 15.53) * mm, "end": v(-2.54, 15.5) * mm});
            skLineSegment(sketch, "E2275", {"start": v(-2.54, 15.5) * mm, "end": v(-2.42, 15.32) * mm});
            skLineSegment(sketch, "E2276", {"start": v(-2.42, 15.32) * mm, "end": v(-2.41, 15.3) * mm});
            skLineSegment(sketch, "E2277", {"start": v(-2.41, 15.3) * mm, "end": v(-2.32, 15.14) * mm});
            skLineSegment(sketch, "E2278", {"start": v(-2.32, 15.14) * mm, "end": v(-2.29, 15.08) * mm});
            skLineSegment(sketch, "E2279", {"start": v(-2.29, 15.08) * mm, "end": v(-2.24, 14.99) * mm});
            skLineSegment(sketch, "E2280", {"start": v(-2.24, 14.99) * mm, "end": v(-2.19, 14.89) * mm});
            skLineSegment(sketch, "E2281", {"start": v(-2.19, 14.89) * mm, "end": v(-2.15, 14.8) * mm});
            skLineSegment(sketch, "E2282", {"start": v(-2.15, 14.8) * mm, "end": v(-2.12, 14.75) * mm});
            skLineSegment(sketch, "E2283", {"start": v(-2.12, 14.75) * mm, "end": v(-2.1, 14.73) * mm});
            skLineSegment(sketch, "E2284", {"start": v(-2.1, 14.73) * mm, "end": v(-2.09, 14.72) * mm});
            skLineSegment(sketch, "E2285", {"start": v(-2.09, 14.72) * mm, "end": v(-2.07, 14.7) * mm});
            skLineSegment(sketch, "E2286", {"start": v(-2.07, 14.7) * mm, "end": v(-1.51, 14.78) * mm});
            skLineSegment(sketch, "E2287", {"start": v(-1.51, 14.78) * mm, "end": v(-1.5, 14.8) * mm});
            skLineSegment(sketch, "E2288", {"start": v(-1.5, 14.8) * mm, "end": v(-1.48, 14.8) * mm});
            skLineSegment(sketch, "E2289", {"start": v(-1.48, 14.8) * mm, "end": v(-1.47, 14.83) * mm});
            skLineSegment(sketch, "E2290", {"start": v(-1.47, 14.83) * mm, "end": v(-1.46, 14.88) * mm});
            skLineSegment(sketch, "E2291", {"start": v(-1.46, 14.88) * mm, "end": v(-1.44, 14.98) * mm});
            skLineSegment(sketch, "E2292", {"start": v(-1.44, 14.98) * mm, "end": v(-1.41, 15.09) * mm});
            skLineSegment(sketch, "E2293", {"start": v(-1.41, 15.09) * mm, "end": v(-1.39, 15.2) * mm});
            skLineSegment(sketch, "E2294", {"start": v(-1.39, 15.2) * mm, "end": v(-1.37, 15.26) * mm});
            skLineSegment(sketch, "E2295", {"start": v(-1.37, 15.26) * mm, "end": v(-1.32, 15.43) * mm});
            skLineSegment(sketch, "E2296", {"start": v(-1.32, 15.43) * mm, "end": v(-1.32, 15.45) * mm});
            skLineSegment(sketch, "E2297", {"start": v(-1.32, 15.45) * mm, "end": v(-1.25, 15.66) * mm});
            skLineSegment(sketch, "E2298", {"start": v(-1.25, 15.66) * mm, "end": v(-1.24, 15.69) * mm});
            skLineSegment(sketch, "E2299", {"start": v(-1.24, 15.69) * mm, "end": v(-1.24, 15.7) * mm});
            skLineSegment(sketch, "E2300", {"start": v(-1.24, 15.7) * mm, "end": v(-1.17, 15.87) * mm});
            skLineSegment(sketch, "E2301", {"start": v(-1.17, 15.87) * mm, "end": v(-1.16, 15.9) * mm});
            skLineSegment(sketch, "E2302", {"start": v(-1.16, 15.9) * mm, "end": v(-1.13, 15.96) * mm});
            skLineSegment(sketch, "E2303", {"start": v(-1.13, 15.96) * mm, "end": v(-1, 16.25) * mm});
            skLineSegment(sketch, "E2304", {"start": v(-1, 16.25) * mm, "end": v(-0.98, 16.3) * mm});
            skLineSegment(sketch, "E2305", {"start": v(-0.98, 16.3) * mm, "end": v(-0.92, 16.36) * mm});
            skLineSegment(sketch, "E2306", {"start": v(-0.92, 16.36) * mm, "end": v(-0.66, 16.39) * mm});
            skLineSegment(sketch, "E2307", {"start": v(-0.66, 16.39) * mm, "end": v(-0.4, 16.38) * mm});
            skLineSegment(sketch, "E2308", {"start": v(-0.4, 16.38) * mm, "end": v(-0.34, 16.33) * mm});
            skLineSegment(sketch, "E2309", {"start": v(-0.34, 16.33) * mm, "end": v(-0.3, 16.28) * mm});
            skLineSegment(sketch, "E2310", {"start": v(-0.3, 16.28) * mm, "end": v(-0.15, 16) * mm});
            skLineSegment(sketch, "E2311", {"start": v(-0.15, 16) * mm, "end": v(-0.12, 15.93) * mm});
            skLineSegment(sketch, "E2312", {"start": v(-0.12, 15.93) * mm, "end": v(-0.11, 15.92) * mm});
            skLineSegment(sketch, "E2313", {"start": v(-0.11, 15.92) * mm, "end": v(-0.03, 15.74) * mm});
            skLineSegment(sketch, "E2314", {"start": v(-0.03, 15.74) * mm, "end": v(-0.03, 15.74) * mm});
            skLineSegment(sketch, "E2315", {"start": v(-0.03, 15.74) * mm, "end": v(-0.02, 15.71) * mm});
            skLineSegment(sketch, "E2316", {"start": v(-0.02, 15.71) * mm, "end": v(0.07, 15.5) * mm});
            skLineSegment(sketch, "E2317", {"start": v(0.07, 15.5) * mm, "end": v(0.08, 15.49) * mm});
            skLineSegment(sketch, "E2318", {"start": v(0.08, 15.49) * mm, "end": v(0.14, 15.32) * mm});
            skLineSegment(sketch, "E2319", {"start": v(0.14, 15.32) * mm, "end": v(0.16, 15.26) * mm});
            skLineSegment(sketch, "E2320", {"start": v(0.16, 15.26) * mm, "end": v(0.2, 15.15) * mm});
            skLineSegment(sketch, "E2321", {"start": v(0.2, 15.15) * mm, "end": v(0.23, 15.04) * mm});
            skLineSegment(sketch, "E2322", {"start": v(0.23, 15.04) * mm, "end": v(0.26, 14.95) * mm});
            skLineSegment(sketch, "E2323", {"start": v(0.26, 14.95) * mm, "end": v(0.28, 14.9) * mm});
            skLineSegment(sketch, "E2324", {"start": v(0.28, 14.9) * mm, "end": v(0.29, 14.88) * mm});
            skLineSegment(sketch, "E2325", {"start": v(0.29, 14.88) * mm, "end": v(0.3, 14.86) * mm});
            skLineSegment(sketch, "E2326", {"start": v(0.3, 14.86) * mm, "end": v(0.32, 14.85) * mm});
            skLineSegment(sketch, "E2327", {"start": v(0.32, 14.85) * mm, "end": v(0.88, 14.83) * mm});
            skLineSegment(sketch, "E2328", {"start": v(0.88, 14.83) * mm, "end": v(0.9, 14.84) * mm});
            skLineSegment(sketch, "E2329", {"start": v(0.9, 14.84) * mm, "end": v(0.9, 14.85) * mm});
            skLineSegment(sketch, "E2330", {"start": v(0.9, 14.85) * mm, "end": v(0.92, 14.87) * mm});
            skLineSegment(sketch, "E2331", {"start": v(0.92, 14.87) * mm, "end": v(0.95, 14.92) * mm});
            skLineSegment(sketch, "E2332", {"start": v(0.95, 14.92) * mm, "end": v(0.98, 15.01) * mm});
            skLineSegment(sketch, "E2333", {"start": v(0.98, 15.01) * mm, "end": v(1.03, 15.12) * mm});
            skLineSegment(sketch, "E2334", {"start": v(1.03, 15.12) * mm, "end": v(1.07, 15.22) * mm});
            skLineSegment(sketch, "E2335", {"start": v(1.07, 15.22) * mm, "end": v(1.1, 15.28) * mm});
            skLineSegment(sketch, "E2336", {"start": v(1.1, 15.28) * mm, "end": v(1.17, 15.44) * mm});
            skLineSegment(sketch, "E2337", {"start": v(1.17, 15.44) * mm, "end": v(1.18, 15.46) * mm});
            skLineSegment(sketch, "E2338", {"start": v(1.18, 15.46) * mm, "end": v(1.28, 15.66) * mm});
            skLineSegment(sketch, "E2339", {"start": v(1.28, 15.66) * mm, "end": v(1.3, 15.68) * mm});
            skLineSegment(sketch, "E2340", {"start": v(1.3, 15.68) * mm, "end": v(1.3, 15.69) * mm});
            skLineSegment(sketch, "E2341", {"start": v(1.3, 15.69) * mm, "end": v(1.4, 15.85) * mm});
            skLineSegment(sketch, "E2342", {"start": v(1.4, 15.85) * mm, "end": v(1.4, 15.87) * mm});
            skLineSegment(sketch, "E2343", {"start": v(1.4, 15.87) * mm, "end": v(1.44, 15.94) * mm});
            skLineSegment(sketch, "E2344", {"start": v(1.44, 15.94) * mm, "end": v(1.6, 16.2) * mm});
            skLineSegment(sketch, "E2345", {"start": v(1.6, 16.2) * mm, "end": v(1.65, 16.25) * mm});
            skLineSegment(sketch, "E2346", {"start": v(1.65, 16.25) * mm, "end": v(1.72, 16.3) * mm});
            skLineSegment(sketch, "E2347", {"start": v(1.72, 16.3) * mm, "end": v(1.98, 16.28) * mm});
            skLineSegment(sketch, "E2348", {"start": v(1.98, 16.28) * mm, "end": v(2.23, 16.23) * mm});
            skLineSegment(sketch, "E2349", {"start": v(2.23, 16.23) * mm, "end": v(2.29, 16.17) * mm});
            skLineSegment(sketch, "E2350", {"start": v(2.29, 16.17) * mm, "end": v(2.31, 16.12) * mm});
            skLineSegment(sketch, "E2351", {"start": v(2.31, 16.12) * mm, "end": v(2.41, 15.82) * mm});
            skLineSegment(sketch, "E2352", {"start": v(2.41, 15.82) * mm, "end": v(2.44, 15.75) * mm});
            skLineSegment(sketch, "E2353", {"start": v(2.44, 15.75) * mm, "end": v(2.44, 15.73) * mm});
            skLineSegment(sketch, "E2354", {"start": v(2.44, 15.73) * mm, "end": v(2.5, 15.54) * mm});
            skLineSegment(sketch, "E2355", {"start": v(2.5, 15.54) * mm, "end": v(2.5, 15.54) * mm});
            skLineSegment(sketch, "E2356", {"start": v(2.5, 15.54) * mm, "end": v(2.5, 15.51) * mm});
            skLineSegment(sketch, "E2357", {"start": v(2.5, 15.51) * mm, "end": v(2.55, 15.3) * mm});
            skLineSegment(sketch, "E2358", {"start": v(2.55, 15.3) * mm, "end": v(2.56, 15.27) * mm});
            skLineSegment(sketch, "E2359", {"start": v(2.56, 15.27) * mm, "end": v(2.6, 15.1) * mm});
            skLineSegment(sketch, "E2360", {"start": v(2.6, 15.1) * mm, "end": v(2.6, 15.03) * mm});
            skLineSegment(sketch, "E2361", {"start": v(2.6, 15.03) * mm, "end": v(2.62, 14.93) * mm});
            skLineSegment(sketch, "E2362", {"start": v(2.62, 14.93) * mm, "end": v(2.64, 14.81) * mm});
            skLineSegment(sketch, "E2363", {"start": v(2.64, 14.81) * mm, "end": v(2.65, 14.71) * mm});
            skLineSegment(sketch, "E2364", {"start": v(2.65, 14.71) * mm, "end": v(2.66, 14.66) * mm});
            skLineSegment(sketch, "E2365", {"start": v(2.66, 14.66) * mm, "end": v(2.67, 14.64) * mm});
            skLineSegment(sketch, "E2366", {"start": v(2.67, 14.64) * mm, "end": v(2.68, 14.62) * mm});
            skLineSegment(sketch, "E2367", {"start": v(2.68, 14.62) * mm, "end": v(2.7, 14.6) * mm});
            skLineSegment(sketch, "E2368", {"start": v(2.7, 14.6) * mm, "end": v(3.25, 14.5) * mm});
            skLineSegment(sketch, "E2369", {"start": v(3.25, 14.5) * mm, "end": v(3.26, 14.5) * mm});
            skLineSegment(sketch, "E2370", {"start": v(3.26, 14.5) * mm, "end": v(3.28, 14.51) * mm});
            skLineSegment(sketch, "E2371", {"start": v(3.28, 14.51) * mm, "end": v(3.3, 14.53) * mm});
            skLineSegment(sketch, "E2372", {"start": v(3.3, 14.53) * mm, "end": v(3.33, 14.57) * mm});
            skLineSegment(sketch, "E2373", {"start": v(3.33, 14.57) * mm, "end": v(3.38, 14.66) * mm});
            skLineSegment(sketch, "E2374", {"start": v(3.38, 14.66) * mm, "end": v(3.44, 14.76) * mm});
            skLineSegment(sketch, "E2375", {"start": v(3.44, 14.76) * mm, "end": v(3.5, 14.85) * mm});
            skLineSegment(sketch, "E2376", {"start": v(3.5, 14.85) * mm, "end": v(3.53, 14.9) * mm});
            skLineSegment(sketch, "E2377", {"start": v(3.53, 14.9) * mm, "end": v(3.63, 15.06) * mm});
            skLineSegment(sketch, "E2378", {"start": v(3.63, 15.06) * mm, "end": v(3.65, 15.07) * mm});
            skLineSegment(sketch, "E2379", {"start": v(3.65, 15.07) * mm, "end": v(3.78, 15.25) * mm});
            skLineSegment(sketch, "E2380", {"start": v(3.78, 15.25) * mm, "end": v(3.8, 15.27) * mm});
            skLineSegment(sketch, "E2381", {"start": v(3.8, 15.27) * mm, "end": v(3.8, 15.27) * mm});
            skLineSegment(sketch, "E2382", {"start": v(3.8, 15.27) * mm, "end": v(3.92, 15.43) * mm});
            skLineSegment(sketch, "E2383", {"start": v(3.92, 15.43) * mm, "end": v(3.93, 15.44) * mm});
            skLineSegment(sketch, "E2384", {"start": v(3.93, 15.44) * mm, "end": v(3.98, 15.5) * mm});
            skLineSegment(sketch, "E2385", {"start": v(3.98, 15.5) * mm, "end": v(4.19, 15.73) * mm});
            skLineSegment(sketch, "E2386", {"start": v(4.19, 15.73) * mm, "end": v(4.23, 15.78) * mm});
            skLineSegment(sketch, "E2387", {"start": v(4.23, 15.78) * mm, "end": v(4.3, 15.8) * mm});
            skLineSegment(sketch, "E2388", {"start": v(4.3, 15.8) * mm, "end": v(4.56, 15.75) * mm});
            skLineSegment(sketch, "E2389", {"start": v(4.56, 15.75) * mm, "end": v(4.8, 15.66) * mm});
            skLineSegment(sketch, "E2390", {"start": v(4.8, 15.66) * mm, "end": v(4.85, 15.6) * mm});
            skLineSegment(sketch, "E2391", {"start": v(4.85, 15.6) * mm, "end": v(4.87, 15.54) * mm});
            skLineSegment(sketch, "E2392", {"start": v(4.87, 15.54) * mm, "end": v(4.92, 15.22) * mm});
            skLineSegment(sketch, "E2393", {"start": v(4.92, 15.22) * mm, "end": v(4.93, 15.15) * mm});
            skLineSegment(sketch, "E2394", {"start": v(4.93, 15.15) * mm, "end": v(4.93, 15.13) * mm});
            skLineSegment(sketch, "E2395", {"start": v(4.93, 15.13) * mm, "end": v(4.95, 14.94) * mm});
            skLineSegment(sketch, "E2396", {"start": v(4.95, 14.94) * mm, "end": v(4.96, 14.93) * mm});
            skLineSegment(sketch, "E2397", {"start": v(4.96, 14.93) * mm, "end": v(4.96, 14.9) * mm});
            skLineSegment(sketch, "E2398", {"start": v(4.96, 14.9) * mm, "end": v(4.97, 14.69) * mm});
            skLineSegment(sketch, "E2399", {"start": v(4.97, 14.69) * mm, "end": v(4.98, 14.67) * mm});
            skLineSegment(sketch, "E2400", {"start": v(4.98, 14.67) * mm, "end": v(4.98, 14.49) * mm});
            skLineSegment(sketch, "E2401", {"start": v(4.98, 14.49) * mm, "end": v(4.98, 14.42) * mm});
            skLineSegment(sketch, "E2402", {"start": v(4.98, 14.42) * mm, "end": v(4.98, 14.31) * mm});
            skLineSegment(sketch, "E2403", {"start": v(4.98, 14.31) * mm, "end": v(4.98, 14.2) * mm});
            skLineSegment(sketch, "E2404", {"start": v(4.98, 14.2) * mm, "end": v(4.98, 14.1) * mm});
            skLineSegment(sketch, "E2405", {"start": v(4.98, 14.1) * mm, "end": v(4.98, 14.05) * mm});
            skLineSegment(sketch, "E2406", {"start": v(4.98, 14.05) * mm, "end": v(4.98, 14.02) * mm});
            skLineSegment(sketch, "E2407", {"start": v(4.98, 14.02) * mm, "end": v(5, 14) * mm});
            skLineSegment(sketch, "E2408", {"start": v(5, 14) * mm, "end": v(5, 13.99) * mm});
            skLineSegment(sketch, "E2409", {"start": v(5, 13.99) * mm, "end": v(5.53, 13.79) * mm});
            skLineSegment(sketch, "E2410", {"start": v(5.53, 13.79) * mm, "end": v(5.55, 13.8) * mm});
            skLineSegment(sketch, "E2411", {"start": v(5.55, 13.8) * mm, "end": v(5.57, 13.8) * mm});
            skLineSegment(sketch, "E2412", {"start": v(5.57, 13.8) * mm, "end": v(5.59, 13.82) * mm});
            skLineSegment(sketch, "E2413", {"start": v(5.59, 13.82) * mm, "end": v(5.62, 13.85) * mm});
            skLineSegment(sketch, "E2414", {"start": v(5.62, 13.85) * mm, "end": v(5.69, 13.93) * mm});
            skLineSegment(sketch, "E2415", {"start": v(5.69, 13.93) * mm, "end": v(5.76, 14.02) * mm});
            skLineSegment(sketch, "E2416", {"start": v(5.76, 14.02) * mm, "end": v(5.83, 14.1) * mm});
            skLineSegment(sketch, "E2417", {"start": v(5.83, 14.1) * mm, "end": v(5.88, 14.15) * mm});
            skLineSegment(sketch, "E2418", {"start": v(5.88, 14.15) * mm, "end": v(6, 14.28) * mm});
            skLineSegment(sketch, "E2419", {"start": v(6, 14.28) * mm, "end": v(6.02, 14.3) * mm});
            skLineSegment(sketch, "E2420", {"start": v(6.02, 14.3) * mm, "end": v(6.18, 14.45) * mm});
            skLineSegment(sketch, "E2421", {"start": v(6.18, 14.45) * mm, "end": v(6.2, 14.46) * mm});
            skLineSegment(sketch, "E2422", {"start": v(6.2, 14.46) * mm, "end": v(6.2, 14.47) * mm});
            skLineSegment(sketch, "E2423", {"start": v(6.2, 14.47) * mm, "end": v(6.34, 14.6) * mm});
            skLineSegment(sketch, "E2424", {"start": v(6.34, 14.6) * mm, "end": v(6.36, 14.61) * mm});
            skLineSegment(sketch, "E2425", {"start": v(6.36, 14.61) * mm, "end": v(6.41, 14.66) * mm});
            skLineSegment(sketch, "E2426", {"start": v(6.41, 14.66) * mm, "end": v(6.66, 14.86) * mm});
            skLineSegment(sketch, "E2427", {"start": v(6.66, 14.86) * mm, "end": v(6.71, 14.9) * mm});
            skLineSegment(sketch, "E2428", {"start": v(6.71, 14.9) * mm, "end": v(6.79, 14.9) * mm});
            skLineSegment(sketch, "E2429", {"start": v(6.79, 14.9) * mm, "end": v(7.03, 14.82) * mm});
            skLineSegment(sketch, "E2430", {"start": v(7.03, 14.82) * mm, "end": v(7.26, 14.69) * mm});
            skLineSegment(sketch, "E2431", {"start": v(7.26, 14.69) * mm, "end": v(7.3, 14.62) * mm});
            skLineSegment(sketch, "E2432", {"start": v(7.3, 14.62) * mm, "end": v(7.3, 14.55) * mm});
            skLineSegment(sketch, "E2433", {"start": v(7.3, 14.55) * mm, "end": v(7.3, 14.24) * mm});
            skLineSegment(sketch, "E2434", {"start": v(7.3, 14.24) * mm, "end": v(7.3, 14.17) * mm});
            skLineSegment(sketch, "E2435", {"start": v(7.3, 14.17) * mm, "end": v(7.3, 14.15) * mm});
            skLineSegment(sketch, "E2436", {"start": v(7.3, 14.15) * mm, "end": v(7.29, 13.95) * mm});
            skLineSegment(sketch, "E2437", {"start": v(7.29, 13.95) * mm, "end": v(7.29, 13.95) * mm});
            skLineSegment(sketch, "E2438", {"start": v(7.29, 13.95) * mm, "end": v(7.29, 13.92) * mm});
            skLineSegment(sketch, "E2439", {"start": v(7.29, 13.92) * mm, "end": v(7.27, 13.7) * mm});
            skLineSegment(sketch, "E2440", {"start": v(7.27, 13.7) * mm, "end": v(7.26, 13.68) * mm});
            skLineSegment(sketch, "E2441", {"start": v(7.26, 13.68) * mm, "end": v(7.24, 13.5) * mm});
            skLineSegment(sketch, "E2442", {"start": v(7.24, 13.5) * mm, "end": v(7.23, 13.43) * mm});
            skLineSegment(sketch, "E2443", {"start": v(7.23, 13.43) * mm, "end": v(7.21, 13.33) * mm});
            skLineSegment(sketch, "E2444", {"start": v(7.21, 13.33) * mm, "end": v(7.2, 13.22) * mm});
            skLineSegment(sketch, "E2445", {"start": v(7.2, 13.22) * mm, "end": v(7.17, 13.12) * mm});
            skLineSegment(sketch, "E2446", {"start": v(7.17, 13.12) * mm, "end": v(7.17, 13.07) * mm});
            skLineSegment(sketch, "E2447", {"start": v(7.17, 13.07) * mm, "end": v(7.17, 13.04) * mm});
            skLineSegment(sketch, "E2448", {"start": v(7.17, 13.04) * mm, "end": v(7.17, 13.02) * mm});
            skLineSegment(sketch, "E2449", {"start": v(7.17, 13.02) * mm, "end": v(7.18, 13) * mm});
            skLineSegment(sketch, "E2450", {"start": v(7.18, 13) * mm, "end": v(7.67, 12.72) * mm});
            skLineSegment(sketch, "E2451", {"start": v(7.67, 12.72) * mm, "end": v(7.69, 12.72) * mm});
            skLineSegment(sketch, "E2452", {"start": v(7.69, 12.72) * mm, "end": v(7.7, 12.73) * mm});
            skLineSegment(sketch, "E2453", {"start": v(7.7, 12.73) * mm, "end": v(7.73, 12.74) * mm});
            skLineSegment(sketch, "E2454", {"start": v(7.73, 12.74) * mm, "end": v(7.77, 12.77) * mm});
            skLineSegment(sketch, "E2455", {"start": v(7.77, 12.77) * mm, "end": v(7.85, 12.84) * mm});
            skLineSegment(sketch, "E2456", {"start": v(7.85, 12.84) * mm, "end": v(7.94, 12.91) * mm});
            skLineSegment(sketch, "E2457", {"start": v(7.94, 12.91) * mm, "end": v(8.02, 12.98) * mm});
            skLineSegment(sketch, "E2458", {"start": v(8.02, 12.98) * mm, "end": v(8.07, 13.02) * mm});
            skLineSegment(sketch, "E2459", {"start": v(8.07, 13.02) * mm, "end": v(8.21, 13.13) * mm});
            skLineSegment(sketch, "E2460", {"start": v(8.21, 13.13) * mm, "end": v(8.23, 13.14) * mm});
            skLineSegment(sketch, "E2461", {"start": v(8.23, 13.14) * mm, "end": v(8.41, 13.27) * mm});
            skLineSegment(sketch, "E2462", {"start": v(8.41, 13.27) * mm, "end": v(8.43, 13.28) * mm});
            skLineSegment(sketch, "E2463", {"start": v(8.43, 13.28) * mm, "end": v(8.44, 13.29) * mm});
            skLineSegment(sketch, "E2464", {"start": v(8.44, 13.29) * mm, "end": v(8.6, 13.4) * mm});
            skLineSegment(sketch, "E2465", {"start": v(8.6, 13.4) * mm, "end": v(8.62, 13.4) * mm});
            skLineSegment(sketch, "E2466", {"start": v(8.62, 13.4) * mm, "end": v(8.68, 13.44) * mm});
            skLineSegment(sketch, "E2467", {"start": v(8.68, 13.44) * mm, "end": v(8.95, 13.6) * mm});
            skLineSegment(sketch, "E2468", {"start": v(8.95, 13.6) * mm, "end": v(9.01, 13.62) * mm});
            skLineSegment(sketch, "E2469", {"start": v(9.01, 13.62) * mm, "end": v(9.1, 13.63) * mm});
            skLineSegment(sketch, "E2470", {"start": v(9.1, 13.63) * mm, "end": v(9.32, 13.5) * mm});
            skLineSegment(sketch, "E2471", {"start": v(9.32, 13.5) * mm, "end": v(9.52, 13.33) * mm});
            skLineSegment(sketch, "E2472", {"start": v(9.52, 13.33) * mm, "end": v(9.54, 13.26) * mm});
            skLineSegment(sketch, "E2473", {"start": v(9.54, 13.26) * mm, "end": v(9.54, 13.2) * mm});
            skLineSegment(sketch, "E2474", {"start": v(9.54, 13.2) * mm, "end": v(9.49, 12.88) * mm});
            skLineSegment(sketch, "E2475", {"start": v(9.49, 12.88) * mm, "end": v(9.48, 12.81) * mm});
            skLineSegment(sketch, "E2476", {"start": v(9.48, 12.81) * mm, "end": v(9.47, 12.8) * mm});
            skLineSegment(sketch, "E2477", {"start": v(9.47, 12.8) * mm, "end": v(9.43, 12.6) * mm});
            skLineSegment(sketch, "E2478", {"start": v(9.43, 12.6) * mm, "end": v(9.43, 12.6) * mm});
            skLineSegment(sketch, "E2479", {"start": v(9.43, 12.6) * mm, "end": v(9.42, 12.57) * mm});
            skLineSegment(sketch, "E2480", {"start": v(9.42, 12.57) * mm, "end": v(9.37, 12.36) * mm});
            skLineSegment(sketch, "E2481", {"start": v(9.37, 12.36) * mm, "end": v(9.36, 12.34) * mm});
            skLineSegment(sketch, "E2482", {"start": v(9.36, 12.34) * mm, "end": v(9.31, 12.17) * mm});
            skLineSegment(sketch, "E2483", {"start": v(9.31, 12.17) * mm, "end": v(9.3, 12.1) * mm});
            skLineSegment(sketch, "E2484", {"start": v(9.3, 12.1) * mm, "end": v(9.26, 12) * mm});
            skLineSegment(sketch, "E2485", {"start": v(9.26, 12) * mm, "end": v(9.22, 11.9) * mm});
            skLineSegment(sketch, "E2486", {"start": v(9.22, 11.9) * mm, "end": v(9.18, 11.8) * mm});
            skLineSegment(sketch, "E2487", {"start": v(9.18, 11.8) * mm, "end": v(9.17, 11.75) * mm});
            skLineSegment(sketch, "E2488", {"start": v(9.17, 11.75) * mm, "end": v(9.17, 11.72) * mm});
            skLineSegment(sketch, "E2489", {"start": v(9.17, 11.72) * mm, "end": v(9.17, 11.7) * mm});
            skLineSegment(sketch, "E2490", {"start": v(9.17, 11.7) * mm, "end": v(9.17, 11.68) * mm});
            skLineSegment(sketch, "E2491", {"start": v(9.17, 11.68) * mm, "end": v(9.61, 11.33) * mm});
            skLineSegment(sketch, "E2492", {"start": v(9.61, 11.33) * mm, "end": v(9.63, 11.33) * mm});
            skLineSegment(sketch, "E2493", {"start": v(9.63, 11.33) * mm, "end": v(9.65, 11.33) * mm});
            skLineSegment(sketch, "E2494", {"start": v(9.65, 11.33) * mm, "end": v(9.68, 11.34) * mm});
            skLineSegment(sketch, "E2495", {"start": v(9.68, 11.34) * mm, "end": v(9.72, 11.36) * mm});
            skLineSegment(sketch, "E2496", {"start": v(9.72, 11.36) * mm, "end": v(9.8, 11.41) * mm});
            skLineSegment(sketch, "E2497", {"start": v(9.8, 11.41) * mm, "end": v(9.9, 11.47) * mm});
            skLineSegment(sketch, "E2498", {"start": v(9.9, 11.47) * mm, "end": v(10, 11.53) * mm});
            skLineSegment(sketch, "E2499", {"start": v(10, 11.53) * mm, "end": v(10.06, 11.56) * mm});
            skLineSegment(sketch, "E2500", {"start": v(10.06, 11.56) * mm, "end": v(10.21, 11.64) * mm});
            skLineSegment(sketch, "E2501", {"start": v(10.21, 11.64) * mm, "end": v(10.23, 11.65) * mm});
            skLineSegment(sketch, "E2502", {"start": v(10.23, 11.65) * mm, "end": v(10.43, 11.75) * mm});
            skLineSegment(sketch, "E2503", {"start": v(10.43, 11.75) * mm, "end": v(10.46, 11.76) * mm});
            skLineSegment(sketch, "E2504", {"start": v(10.46, 11.76) * mm, "end": v(10.46, 11.76) * mm});
            skLineSegment(sketch, "E2505", {"start": v(10.46, 11.76) * mm, "end": v(10.64, 11.84) * mm});
            skLineSegment(sketch, "E2506", {"start": v(10.64, 11.84) * mm, "end": v(10.66, 11.85) * mm});
            skLineSegment(sketch, "E2507", {"start": v(10.66, 11.85) * mm, "end": v(10.72, 11.87) * mm});
            skLineSegment(sketch, "E2508", {"start": v(10.72, 11.87) * mm, "end": v(11.02, 11.99) * mm});
            skLineSegment(sketch, "E2509", {"start": v(11.02, 11.99) * mm, "end": v(11.08, 12) * mm});
            skLineSegment(sketch, "E2510", {"start": v(11.08, 12) * mm, "end": v(11.16, 12) * mm});
            skLineSegment(sketch, "E2511", {"start": v(11.16, 12) * mm, "end": v(11.36, 11.83) * mm});
            skLineSegment(sketch, "E2512", {"start": v(11.36, 11.83) * mm, "end": v(11.53, 11.63) * mm});
            skLineSegment(sketch, "E2513", {"start": v(11.53, 11.63) * mm, "end": v(11.54, 11.55) * mm});
            skLineSegment(sketch, "E2514", {"start": v(11.54, 11.55) * mm, "end": v(11.53, 11.5) * mm});
            skLineSegment(sketch, "E2515", {"start": v(11.53, 11.5) * mm, "end": v(11.43, 11.2) * mm});
            skLineSegment(sketch, "E2516", {"start": v(11.43, 11.2) * mm, "end": v(11.4, 11.13) * mm});
            skLineSegment(sketch, "E2517", {"start": v(11.4, 11.13) * mm, "end": v(11.4, 11.1) * mm});
            skLineSegment(sketch, "E2518", {"start": v(11.4, 11.1) * mm, "end": v(11.33, 10.93) * mm});
            skLineSegment(sketch, "E2519", {"start": v(11.33, 10.93) * mm, "end": v(11.33, 10.92) * mm});
            skLineSegment(sketch, "E2520", {"start": v(11.33, 10.92) * mm, "end": v(11.32, 10.9) * mm});
            skLineSegment(sketch, "E2521", {"start": v(11.32, 10.9) * mm, "end": v(11.23, 10.7) * mm});
            skLineSegment(sketch, "E2522", {"start": v(11.23, 10.7) * mm, "end": v(11.22, 10.67) * mm});
            skLineSegment(sketch, "E2523", {"start": v(11.22, 10.67) * mm, "end": v(11.14, 10.51) * mm});
            skLineSegment(sketch, "E2524", {"start": v(11.14, 10.51) * mm, "end": v(11.11, 10.45) * mm});
            skLineSegment(sketch, "E2525", {"start": v(11.11, 10.45) * mm, "end": v(11.06, 10.36) * mm});
            skLineSegment(sketch, "E2526", {"start": v(11.06, 10.36) * mm, "end": v(11, 10.26) * mm});
            skLineSegment(sketch, "E2527", {"start": v(11, 10.26) * mm, "end": v(10.96, 10.17) * mm});
            skLineSegment(sketch, "E2528", {"start": v(10.96, 10.17) * mm, "end": v(10.94, 10.12) * mm});
            skLineSegment(sketch, "E2529", {"start": v(10.94, 10.12) * mm, "end": v(10.93, 10.1) * mm});
            skLineSegment(sketch, "E2530", {"start": v(10.93, 10.1) * mm, "end": v(10.93, 10.08) * mm});
            skLineSegment(sketch, "E2531", {"start": v(10.93, 10.08) * mm, "end": v(10.93, 10.06) * mm});
            skLineSegment(sketch, "E2532", {"start": v(10.93, 10.06) * mm, "end": v(11.3, 9.64) * mm});
            skLineSegment(sketch, "E2533", {"start": v(11.3, 9.64) * mm, "end": v(11.32, 9.63) * mm});
            skLineSegment(sketch, "E2534", {"start": v(11.32, 9.63) * mm, "end": v(11.34, 9.63) * mm});
            skLineSegment(sketch, "E2535", {"start": v(11.34, 9.63) * mm, "end": v(11.37, 9.64) * mm});
            skLineSegment(sketch, "E2536", {"start": v(11.37, 9.64) * mm, "end": v(11.42, 9.65) * mm});
            skLineSegment(sketch, "E2537", {"start": v(11.42, 9.65) * mm, "end": v(11.5, 9.7) * mm});
            skLineSegment(sketch, "E2538", {"start": v(11.5, 9.7) * mm, "end": v(11.62, 9.73) * mm});
            skLineSegment(sketch, "E2539", {"start": v(11.62, 9.73) * mm, "end": v(11.72, 9.77) * mm});
            skLineSegment(sketch, "E2540", {"start": v(11.72, 9.77) * mm, "end": v(11.78, 9.8) * mm});
            skLineSegment(sketch, "E2541", {"start": v(11.78, 9.8) * mm, "end": v(11.95, 9.85) * mm});
            skLineSegment(sketch, "E2542", {"start": v(11.95, 9.85) * mm, "end": v(11.97, 9.86) * mm});
            skLineSegment(sketch, "E2543", {"start": v(11.97, 9.86) * mm, "end": v(12.18, 9.92) * mm});
            skLineSegment(sketch, "E2544", {"start": v(12.18, 9.92) * mm, "end": v(12.2, 9.93) * mm});
            skLineSegment(sketch, "E2545", {"start": v(12.2, 9.93) * mm, "end": v(12.21, 9.93) * mm});
            skLineSegment(sketch, "E2546", {"start": v(12.21, 9.93) * mm, "end": v(12.4, 9.98) * mm});
            skLineSegment(sketch, "E2547", {"start": v(12.4, 9.98) * mm, "end": v(12.42, 9.98) * mm});
            skLineSegment(sketch, "E2548", {"start": v(12.42, 9.98) * mm, "end": v(12.5, 10) * mm});
            skLineSegment(sketch, "E2549", {"start": v(12.5, 10) * mm, "end": v(12.8, 10.06) * mm});
            skLineSegment(sketch, "E2550", {"start": v(12.8, 10.06) * mm, "end": v(12.86, 10.07) * mm});
            skLineSegment(sketch, "E2551", {"start": v(12.86, 10.07) * mm, "end": v(12.94, 10.05) * mm});
            skLineSegment(sketch, "E2552", {"start": v(12.94, 10.05) * mm, "end": v(13.11, 9.85) * mm});
            skLineSegment(sketch, "E2553", {"start": v(13.11, 9.85) * mm, "end": v(13.25, 9.63) * mm});
            skLineSegment(sketch, "E2554", {"start": v(13.25, 9.63) * mm, "end": v(13.25, 9.55) * mm});
            skLineSegment(sketch, "E2555", {"start": v(13.25, 9.55) * mm, "end": v(13.23, 9.5) * mm});
            skLineSegment(sketch, "E2556", {"start": v(13.23, 9.5) * mm, "end": v(13.08, 9.22) * mm});
            skLineSegment(sketch, "E2557", {"start": v(13.08, 9.22) * mm, "end": v(13.04, 9.15) * mm});
            skLineSegment(sketch, "E2558", {"start": v(13.04, 9.15) * mm, "end": v(13.03, 9.14) * mm});
            skLineSegment(sketch, "E2559", {"start": v(13.03, 9.14) * mm, "end": v(12.94, 8.97) * mm});
            skLineSegment(sketch, "E2560", {"start": v(12.94, 8.97) * mm, "end": v(12.93, 8.96) * mm});
            skLineSegment(sketch, "E2561", {"start": v(12.93, 8.96) * mm, "end": v(12.92, 8.94) * mm});
            skLineSegment(sketch, "E2562", {"start": v(12.92, 8.94) * mm, "end": v(12.8, 8.75) * mm});
            skLineSegment(sketch, "E2563", {"start": v(12.8, 8.75) * mm, "end": v(12.79, 8.74) * mm});
            skLineSegment(sketch, "E2564", {"start": v(12.79, 8.74) * mm, "end": v(12.69, 8.59) * mm});
            skLineSegment(sketch, "E2565", {"start": v(12.69, 8.59) * mm, "end": v(12.65, 8.53) * mm});
            skLineSegment(sketch, "E2566", {"start": v(12.65, 8.53) * mm, "end": v(12.58, 8.45) * mm});
            skLineSegment(sketch, "E2567", {"start": v(12.58, 8.45) * mm, "end": v(12.51, 8.36) * mm});
            skLineSegment(sketch, "E2568", {"start": v(12.51, 8.36) * mm, "end": v(12.45, 8.28) * mm});
            skLineSegment(sketch, "E2569", {"start": v(12.45, 8.28) * mm, "end": v(12.42, 8.24) * mm});
            skLineSegment(sketch, "E2570", {"start": v(12.42, 8.24) * mm, "end": v(12.4, 8.21) * mm});
            skLineSegment(sketch, "E2571", {"start": v(12.4, 8.21) * mm, "end": v(12.4, 8.2) * mm});
            skLineSegment(sketch, "E2572", {"start": v(12.4, 8.2) * mm, "end": v(12.4, 8.18) * mm});
            skLineSegment(sketch, "E2573", {"start": v(12.4, 8.18) * mm, "end": v(12.7, 7.7) * mm});
            skLineSegment(sketch, "E2574", {"start": v(12.7, 7.7) * mm, "end": v(12.72, 7.7) * mm});
            skLineSegment(sketch, "E2575", {"start": v(12.72, 7.7) * mm, "end": v(12.74, 7.69) * mm});
            skLineSegment(sketch, "E2576", {"start": v(12.74, 7.69) * mm, "end": v(12.77, 7.69) * mm});
            skLineSegment(sketch, "E2577", {"start": v(12.77, 7.69) * mm, "end": v(12.82, 7.7) * mm});
            skLineSegment(sketch, "E2578", {"start": v(12.82, 7.7) * mm, "end": v(12.92, 7.72) * mm});
            skLineSegment(sketch, "E2579", {"start": v(12.92, 7.72) * mm, "end": v(13.03, 7.75) * mm});
            skLineSegment(sketch, "E2580", {"start": v(13.03, 7.75) * mm, "end": v(13.13, 7.77) * mm});
            skLineSegment(sketch, "E2581", {"start": v(13.13, 7.77) * mm, "end": v(13.2, 7.78) * mm});
            skLineSegment(sketch, "E2582", {"start": v(13.2, 7.78) * mm, "end": v(13.37, 7.8) * mm});
            skLineSegment(sketch, "E2583", {"start": v(13.37, 7.8) * mm, "end": v(13.4, 7.81) * mm});
            skLineSegment(sketch, "E2584", {"start": v(13.4, 7.81) * mm, "end": v(13.62, 7.84) * mm});
            skLineSegment(sketch, "E2585", {"start": v(13.62, 7.84) * mm, "end": v(13.64, 7.84) * mm});
            skLineSegment(sketch, "E2586", {"start": v(13.64, 7.84) * mm, "end": v(13.65, 7.84) * mm});
            skLineSegment(sketch, "E2587", {"start": v(13.65, 7.84) * mm, "end": v(13.84, 7.86) * mm});
            skLineSegment(sketch, "E2588", {"start": v(13.84, 7.86) * mm, "end": v(13.86, 7.86) * mm});
            skLineSegment(sketch, "E2589", {"start": v(13.86, 7.86) * mm, "end": v(13.93, 7.87) * mm});
            skLineSegment(sketch, "E2590", {"start": v(13.93, 7.87) * mm, "end": v(14.25, 7.88) * mm});
            skLineSegment(sketch, "E2591", {"start": v(14.25, 7.88) * mm, "end": v(14.31, 7.87) * mm});
            skLineSegment(sketch, "E2592", {"start": v(14.31, 7.87) * mm, "end": v(14.38, 7.84) * mm});
            skLineSegment(sketch, "E2593", {"start": v(14.38, 7.84) * mm, "end": v(14.52, 7.62) * mm});
            skLineSegment(sketch, "E2594", {"start": v(14.52, 7.62) * mm, "end": v(14.62, 7.38) * mm});
            skLineSegment(sketch, "E2595", {"start": v(14.62, 7.38) * mm, "end": v(14.6, 7.3) * mm});
            skLineSegment(sketch, "E2596", {"start": v(14.6, 7.3) * mm, "end": v(14.58, 7.25) * mm});
            skLineSegment(sketch, "E2597", {"start": v(14.58, 7.25) * mm, "end": v(14.39, 7) * mm});
            skLineSegment(sketch, "E2598", {"start": v(14.39, 7) * mm, "end": v(14.34, 6.94) * mm});
            skLineSegment(sketch, "E2599", {"start": v(14.34, 6.94) * mm, "end": v(14.33, 6.93) * mm});
            skLineSegment(sketch, "E2600", {"start": v(14.33, 6.93) * mm, "end": v(14.2, 6.78) * mm});
            skLineSegment(sketch, "E2601", {"start": v(14.2, 6.78) * mm, "end": v(14.2, 6.77) * mm});
            skLineSegment(sketch, "E2602", {"start": v(14.2, 6.77) * mm, "end": v(14.19, 6.75) * mm});
            skLineSegment(sketch, "E2603", {"start": v(14.19, 6.75) * mm, "end": v(14.04, 6.59) * mm});
            skLineSegment(sketch, "E2604", {"start": v(14.04, 6.59) * mm, "end": v(14.02, 6.57) * mm});
            skLineSegment(sketch, "E2605", {"start": v(14.02, 6.57) * mm, "end": v(13.9, 6.44) * mm});
            skLineSegment(sketch, "E2606", {"start": v(13.9, 6.44) * mm, "end": v(13.85, 6.4) * mm});
            skLineSegment(sketch, "E2607", {"start": v(13.85, 6.4) * mm, "end": v(13.77, 6.32) * mm});
            skLineSegment(sketch, "E2608", {"start": v(13.77, 6.32) * mm, "end": v(13.69, 6.24) * mm});
            skLineSegment(sketch, "E2609", {"start": v(13.69, 6.24) * mm, "end": v(13.61, 6.18) * mm});
            skLineSegment(sketch, "E2610", {"start": v(13.61, 6.18) * mm, "end": v(13.58, 6.14) * mm});
            skLineSegment(sketch, "E2611", {"start": v(13.58, 6.14) * mm, "end": v(13.56, 6.12) * mm});
            skLineSegment(sketch, "E2612", {"start": v(13.56, 6.12) * mm, "end": v(13.56, 6.1) * mm});
            skLineSegment(sketch, "E2613", {"start": v(13.56, 6.1) * mm, "end": v(13.55, 6.08) * mm});
            skLineSegment(sketch, "E2614", {"start": v(13.55, 6.08) * mm, "end": v(13.77, 5.56) * mm});
            skLineSegment(sketch, "E2615", {"start": v(13.77, 5.56) * mm, "end": v(13.79, 5.55) * mm});
            skLineSegment(sketch, "E2616", {"start": v(13.79, 5.55) * mm, "end": v(13.8, 5.54) * mm});
            skLineSegment(sketch, "E2617", {"start": v(13.8, 5.54) * mm, "end": v(13.84, 5.54) * mm});
            skLineSegment(sketch, "E2618", {"start": v(13.84, 5.54) * mm, "end": v(13.89, 5.54) * mm});
            skLineSegment(sketch, "E2619", {"start": v(13.89, 5.54) * mm, "end": v(13.99, 5.55) * mm});
            skLineSegment(sketch, "E2620", {"start": v(13.99, 5.55) * mm, "end": v(14.1, 5.56) * mm});
            skLineSegment(sketch, "E2621", {"start": v(14.1, 5.56) * mm, "end": v(14.2, 5.56) * mm});
            skLineSegment(sketch, "E2622", {"start": v(14.2, 5.56) * mm, "end": v(14.28, 5.56) * mm});
            skLineSegment(sketch, "E2623", {"start": v(14.28, 5.56) * mm, "end": v(14.45, 5.56) * mm});
            skLineSegment(sketch, "E2624", {"start": v(14.45, 5.56) * mm, "end": v(14.48, 5.56) * mm});
            skLineSegment(sketch, "E2625", {"start": v(14.48, 5.56) * mm, "end": v(14.7, 5.55) * mm});
            skLineSegment(sketch, "E2626", {"start": v(14.7, 5.55) * mm, "end": v(14.72, 5.55) * mm});
            skLineSegment(sketch, "E2627", {"start": v(14.72, 5.55) * mm, "end": v(14.73, 5.55) * mm});
            skLineSegment(sketch, "E2628", {"start": v(14.73, 5.55) * mm, "end": v(14.92, 5.54) * mm});
            skLineSegment(sketch, "E2629", {"start": v(14.92, 5.54) * mm, "end": v(14.94, 5.54) * mm});
            skLineSegment(sketch, "E2630", {"start": v(14.94, 5.54) * mm, "end": v(15.01, 5.53) * mm});
            skLineSegment(sketch, "E2631", {"start": v(15.01, 5.53) * mm, "end": v(15.33, 5.5) * mm});
            skLineSegment(sketch, "E2632", {"start": v(15.33, 5.5) * mm, "end": v(15.39, 5.48) * mm});
            skLineSegment(sketch, "E2633", {"start": v(15.39, 5.48) * mm, "end": v(15.45, 5.43) * mm});
            skLineSegment(sketch, "E2634", {"start": v(15.45, 5.43) * mm, "end": v(15.56, 5.2) * mm});
            skLineSegment(sketch, "E2635", {"start": v(15.56, 5.2) * mm, "end": v(15.62, 4.94) * mm});
            skLineSegment(sketch, "E2636", {"start": v(15.62, 4.94) * mm, "end": v(15.6, 4.87) * mm});
            skLineSegment(sketch, "E2637", {"start": v(15.6, 4.87) * mm, "end": v(15.55, 4.82) * mm});
            skLineSegment(sketch, "E2638", {"start": v(15.55, 4.82) * mm, "end": v(15.32, 4.6) * mm});
            skLineSegment(sketch, "E2639", {"start": v(15.32, 4.6) * mm, "end": v(15.27, 4.55) * mm});
            skLineSegment(sketch, "E2640", {"start": v(15.27, 4.55) * mm, "end": v(15.26, 4.54) * mm});
            skLineSegment(sketch, "E2641", {"start": v(15.26, 4.54) * mm, "end": v(15.1, 4.4) * mm});
            skLineSegment(sketch, "E2642", {"start": v(15.1, 4.4) * mm, "end": v(15.1, 4.4) * mm});
            skLineSegment(sketch, "E2643", {"start": v(15.1, 4.4) * mm, "end": v(15.09, 4.39) * mm});
            skLineSegment(sketch, "E2644", {"start": v(15.09, 4.39) * mm, "end": v(14.91, 4.25) * mm});
            skLineSegment(sketch, "E2645", {"start": v(14.91, 4.25) * mm, "end": v(14.9, 4.24) * mm});
            skLineSegment(sketch, "E2646", {"start": v(14.9, 4.24) * mm, "end": v(14.75, 4.13) * mm});
            skLineSegment(sketch, "E2647", {"start": v(14.75, 4.13) * mm, "end": v(14.7, 4.1) * mm});
            skLineSegment(sketch, "E2648", {"start": v(14.7, 4.1) * mm, "end": v(14.6, 4.03) * mm});
            skLineSegment(sketch, "E2649", {"start": v(14.6, 4.03) * mm, "end": v(14.51, 3.97) * mm});
            skLineSegment(sketch, "E2650", {"start": v(14.51, 3.97) * mm, "end": v(14.43, 3.91) * mm});
            skLineSegment(sketch, "E2651", {"start": v(14.43, 3.91) * mm, "end": v(14.39, 3.88) * mm});
            skLineSegment(sketch, "E2652", {"start": v(14.39, 3.88) * mm, "end": v(14.37, 3.86) * mm});
            skLineSegment(sketch, "E2653", {"start": v(14.37, 3.86) * mm, "end": v(14.36, 3.85) * mm});
            skLineSegment(sketch, "E2654", {"start": v(14.36, 3.85) * mm, "end": v(14.35, 3.83) * mm});
            skLineSegment(sketch, "E2655", {"start": v(14.35, 3.83) * mm, "end": v(14.49, 3.28) * mm});
            skLineSegment(sketch, "E2656", {"start": v(14.49, 3.28) * mm, "end": v(14.5, 3.27) * mm});
            skLineSegment(sketch, "E2657", {"start": v(14.5, 3.27) * mm, "end": v(14.52, 3.26) * mm});
            skLineSegment(sketch, "E2658", {"start": v(14.52, 3.26) * mm, "end": v(14.54, 3.25) * mm});
            skLineSegment(sketch, "E2659", {"start": v(14.54, 3.25) * mm, "end": v(14.6, 3.24) * mm});
            skLineSegment(sketch, "E2660", {"start": v(14.6, 3.24) * mm, "end": v(14.7, 3.23) * mm});
            skLineSegment(sketch, "E2661", {"start": v(14.7, 3.23) * mm, "end": v(14.8, 3.22) * mm});
            skLineSegment(sketch, "E2662", {"start": v(14.8, 3.22) * mm, "end": v(14.92, 3.2) * mm});
            skLineSegment(sketch, "E2663", {"start": v(14.92, 3.2) * mm, "end": v(14.98, 3.2) * mm});
            skLineSegment(sketch, "E2664", {"start": v(14.98, 3.2) * mm, "end": v(15.16, 3.17) * mm});
            skLineSegment(sketch, "E2665", {"start": v(15.16, 3.17) * mm, "end": v(15.18, 3.17) * mm});
            skLineSegment(sketch, "E2666", {"start": v(15.18, 3.17) * mm, "end": v(15.4, 3.12) * mm});
            skLineSegment(sketch, "E2667", {"start": v(15.4, 3.12) * mm, "end": v(15.42, 3.12) * mm});
            skLineSegment(sketch, "E2668", {"start": v(15.42, 3.12) * mm, "end": v(15.43, 3.12) * mm});
            skLineSegment(sketch, "E2669", {"start": v(15.43, 3.12) * mm, "end": v(15.62, 3.07) * mm});
            skLineSegment(sketch, "E2670", {"start": v(15.62, 3.07) * mm, "end": v(15.64, 3.07) * mm});
            skLineSegment(sketch, "E2671", {"start": v(15.64, 3.07) * mm, "end": v(15.7, 3.05) * mm});
            skLineSegment(sketch, "E2672", {"start": v(15.7, 3.05) * mm, "end": v(16, 2.96) * mm});
            skLineSegment(sketch, "E2673", {"start": v(16, 2.96) * mm, "end": v(16.07, 2.94) * mm});
            skLineSegment(sketch, "E2674", {"start": v(16.07, 2.94) * mm, "end": v(16.13, 2.88) * mm});
            skLineSegment(sketch, "E2675", {"start": v(16.13, 2.88) * mm, "end": v(16.19, 2.63) * mm});
            skLineSegment(sketch, "E2676", {"start": v(16.19, 2.63) * mm, "end": v(16.2, 2.37) * mm});
            skLineSegment(sketch, "E2677", {"start": v(16.2, 2.37) * mm, "end": v(16.17, 2.3) * mm});
            skLineSegment(sketch, "E2678", {"start": v(16.17, 2.3) * mm, "end": v(16.12, 2.26) * mm});
            skLineSegment(sketch, "E2679", {"start": v(16.12, 2.26) * mm, "end": v(15.86, 2.08) * mm});
            skLineSegment(sketch, "E2680", {"start": v(15.86, 2.08) * mm, "end": v(15.8, 2.04) * mm});
            skLineSegment(sketch, "E2681", {"start": v(15.8, 2.04) * mm, "end": v(15.79, 2.03) * mm});
            skLineSegment(sketch, "E2682", {"start": v(15.79, 2.03) * mm, "end": v(15.62, 1.93) * mm});
            skLineSegment(sketch, "E2683", {"start": v(15.62, 1.93) * mm, "end": v(15.62, 1.93) * mm});
            skLineSegment(sketch, "E2684", {"start": v(15.62, 1.93) * mm, "end": v(15.6, 1.91) * mm});
            skLineSegment(sketch, "E2685", {"start": v(15.6, 1.91) * mm, "end": v(15.4, 1.8) * mm});
            skLineSegment(sketch, "E2686", {"start": v(15.4, 1.8) * mm, "end": v(15.38, 1.8) * mm});
            skLineSegment(sketch, "E2687", {"start": v(15.38, 1.8) * mm, "end": v(15.23, 1.7) * mm});
            skLineSegment(sketch, "E2688", {"start": v(15.23, 1.7) * mm, "end": v(15.16, 1.68) * mm});
            skLineSegment(sketch, "E2689", {"start": v(15.16, 1.68) * mm, "end": v(15.07, 1.63) * mm});
            skLineSegment(sketch, "E2690", {"start": v(15.07, 1.63) * mm, "end": v(14.96, 1.59) * mm});
            skLineSegment(sketch, "E2691", {"start": v(14.96, 1.59) * mm, "end": v(14.87, 1.55) * mm});
            skLineSegment(sketch, "E2692", {"start": v(14.87, 1.55) * mm, "end": v(14.83, 1.52) * mm});
            skLineSegment(sketch, "E2693", {"start": v(14.83, 1.52) * mm, "end": v(14.8, 1.5) * mm});
            skLineSegment(sketch, "E2694", {"start": v(14.8, 1.5) * mm, "end": v(14.8, 1.5) * mm});
            skLineSegment(sketch, "E2695", {"start": v(14.8, 1.5) * mm, "end": v(14.78, 1.48) * mm});
            skLineSegment(sketch, "E2696", {"start": v(14.78, 1.48) * mm, "end": v(14.83, 0.91) * mm});
            skLineSegment(sketch, "E2697", {"start": v(14.83, 0.91) * mm, "end": v(14.84, 0.9) * mm});
            skLineSegment(sketch, "E2698", {"start": v(14.84, 0.9) * mm, "end": v(14.85, 0.89) * mm});
            skLineSegment(sketch, "E2699", {"start": v(14.85, 0.89) * mm, "end": v(14.88, 0.88) * mm});
            skLineSegment(sketch, "E2700", {"start": v(14.88, 0.88) * mm, "end": v(14.92, 0.86) * mm});
            skLineSegment(sketch, "E2701", {"start": v(14.92, 0.86) * mm, "end": v(15.02, 0.83) * mm});
            skLineSegment(sketch, "E2702", {"start": v(15.02, 0.83) * mm, "end": v(15.13, 0.8) * mm});
            skLineSegment(sketch, "E2703", {"start": v(15.13, 0.8) * mm, "end": v(15.24, 0.77) * mm});
            skLineSegment(sketch, "E2704", {"start": v(15.24, 0.77) * mm, "end": v(15.3, 0.75) * mm});
            skLineSegment(sketch, "E2705", {"start": v(15.3, 0.75) * mm, "end": v(15.47, 0.7) * mm});
            skLineSegment(sketch, "E2706", {"start": v(15.47, 0.7) * mm, "end": v(15.5, 0.7) * mm});
            skLineSegment(sketch, "E2707", {"start": v(15.5, 0.7) * mm, "end": v(15.7, 0.61) * mm});
            skLineSegment(sketch, "E2708", {"start": v(15.7, 0.61) * mm, "end": v(15.72, 0.6) * mm});
            skLineSegment(sketch, "E2709", {"start": v(15.72, 0.6) * mm, "end": v(15.73, 0.6) * mm});
            skLineSegment(sketch, "E2710", {"start": v(15.73, 0.6) * mm, "end": v(15.9, 0.53) * mm});
            skLineSegment(sketch, "E2711", {"start": v(15.9, 0.53) * mm, "end": v(15.93, 0.52) * mm});
            skLineSegment(sketch, "E2712", {"start": v(15.93, 0.52) * mm, "end": v(16, 0.5) * mm});
            skLineSegment(sketch, "E2713", {"start": v(16, 0.5) * mm, "end": v(16.28, 0.35) * mm});
            skLineSegment(sketch, "E2714", {"start": v(16.28, 0.35) * mm, "end": v(16.33, 0.32) * mm});
            skLineSegment(sketch, "E2715", {"start": v(16.33, 0.32) * mm, "end": v(16.38, 0.26) * mm});
            skLineSegment(sketch, "E2716", {"start": v(16.38, 0.26) * mm, "end": v(16.4, 0) * mm});
            skLineSegment(sketch, "E2717", {"start": v(16.4, 0) * mm, "end": v(16.38, -0.26) * mm});
            skLineSegment(sketch, "E2718", {"start": v(16.38, -0.26) * mm, "end": v(16.33, -0.32) * mm});
            skLineSegment(sketch, "E2719", {"start": v(16.33, -0.32) * mm, "end": v(16.28, -0.35) * mm});
            skLineSegment(sketch, "E2720", {"start": v(16.28, -0.35) * mm, "end": v(16, -0.5) * mm});
            skLineSegment(sketch, "E2721", {"start": v(16, -0.5) * mm, "end": v(15.93, -0.52) * mm});
            skLineSegment(sketch, "E2722", {"start": v(15.93, -0.52) * mm, "end": v(15.9, -0.53) * mm});
            skLineSegment(sketch, "E2723", {"start": v(15.9, -0.53) * mm, "end": v(15.73, -0.6) * mm});
            skLineSegment(sketch, "E2724", {"start": v(15.73, -0.6) * mm, "end": v(15.72, -0.6) * mm});
            skLineSegment(sketch, "E2725", {"start": v(15.72, -0.6) * mm, "end": v(15.7, -0.61) * mm});
            skLineSegment(sketch, "E2726", {"start": v(15.7, -0.61) * mm, "end": v(15.5, -0.7) * mm});
            skLineSegment(sketch, "E2727", {"start": v(15.5, -0.7) * mm, "end": v(15.47, -0.7) * mm});
            skLineSegment(sketch, "E2728", {"start": v(15.47, -0.7) * mm, "end": v(15.3, -0.75) * mm});
            skLineSegment(sketch, "E2729", {"start": v(15.3, -0.75) * mm, "end": v(15.24, -0.77) * mm});
            skLineSegment(sketch, "E2730", {"start": v(15.24, -0.77) * mm, "end": v(15.13, -0.8) * mm});
            skLineSegment(sketch, "E2731", {"start": v(15.13, -0.8) * mm, "end": v(15.02, -0.83) * mm});
            skLineSegment(sketch, "E2732", {"start": v(15.02, -0.83) * mm, "end": v(14.92, -0.86) * mm});
            skLineSegment(sketch, "E2733", {"start": v(14.92, -0.86) * mm, "end": v(14.88, -0.88) * mm});
            skLineSegment(sketch, "E2734", {"start": v(14.88, -0.88) * mm, "end": v(14.85, -0.89) * mm});
            skLineSegment(sketch, "E2735", {"start": v(14.85, -0.89) * mm, "end": v(14.84, -0.9) * mm});
            skLineSegment(sketch, "E2736", {"start": v(14.84, -0.9) * mm, "end": v(14.83, -0.91) * mm});
            skLineSegment(sketch, "E2737", {"start": v(14.83, -0.91) * mm, "end": v(14.78, -1.48) * mm});
            skLineSegment(sketch, "E2738", {"start": v(14.78, -1.48) * mm, "end": v(14.8, -1.5) * mm});
            skLineSegment(sketch, "E2739", {"start": v(14.8, -1.5) * mm, "end": v(14.8, -1.5) * mm});
            skLineSegment(sketch, "E2740", {"start": v(14.8, -1.5) * mm, "end": v(14.83, -1.52) * mm});
            skLineSegment(sketch, "E2741", {"start": v(14.83, -1.52) * mm, "end": v(14.87, -1.55) * mm});
            skLineSegment(sketch, "E2742", {"start": v(14.87, -1.55) * mm, "end": v(14.96, -1.59) * mm});
            skLineSegment(sketch, "E2743", {"start": v(14.96, -1.59) * mm, "end": v(15.07, -1.63) * mm});
            skLineSegment(sketch, "E2744", {"start": v(15.07, -1.63) * mm, "end": v(15.16, -1.68) * mm});
            skLineSegment(sketch, "E2745", {"start": v(15.16, -1.68) * mm, "end": v(15.23, -1.7) * mm});
            skLineSegment(sketch, "E2746", {"start": v(15.23, -1.7) * mm, "end": v(15.38, -1.8) * mm});
            skLineSegment(sketch, "E2747", {"start": v(15.38, -1.8) * mm, "end": v(15.4, -1.8) * mm});
            skLineSegment(sketch, "E2748", {"start": v(15.4, -1.8) * mm, "end": v(15.6, -1.91) * mm});
            skLineSegment(sketch, "E2749", {"start": v(15.6, -1.91) * mm, "end": v(15.62, -1.93) * mm});
            skLineSegment(sketch, "E2750", {"start": v(15.62, -1.93) * mm, "end": v(15.62, -1.93) * mm});
            skLineSegment(sketch, "E2751", {"start": v(15.62, -1.93) * mm, "end": v(15.79, -2.03) * mm});
            skLineSegment(sketch, "E2752", {"start": v(15.79, -2.03) * mm, "end": v(15.8, -2.04) * mm});
            skLineSegment(sketch, "E2753", {"start": v(15.8, -2.04) * mm, "end": v(15.86, -2.08) * mm});
            skLineSegment(sketch, "E2754", {"start": v(15.86, -2.08) * mm, "end": v(16.12, -2.26) * mm});
            skLineSegment(sketch, "E2755", {"start": v(16.12, -2.26) * mm, "end": v(16.17, -2.3) * mm});
            skLineSegment(sketch, "E2756", {"start": v(16.17, -2.3) * mm, "end": v(16.2, -2.37) * mm});
            skLineSegment(sketch, "E2757", {"start": v(16.2, -2.37) * mm, "end": v(16.19, -2.63) * mm});
            skLineSegment(sketch, "E2758", {"start": v(16.19, -2.63) * mm, "end": v(16.13, -2.88) * mm});
            skLineSegment(sketch, "E2759", {"start": v(16.13, -2.88) * mm, "end": v(16.07, -2.94) * mm});
            skLineSegment(sketch, "E2760", {"start": v(16.07, -2.94) * mm, "end": v(16, -2.96) * mm});
            skLineSegment(sketch, "E2761", {"start": v(16, -2.96) * mm, "end": v(15.7, -3.05) * mm});
            skLineSegment(sketch, "E2762", {"start": v(15.7, -3.05) * mm, "end": v(15.64, -3.07) * mm});
            skLineSegment(sketch, "E2763", {"start": v(15.64, -3.07) * mm, "end": v(15.62, -3.07) * mm});
            skLineSegment(sketch, "E2764", {"start": v(15.62, -3.07) * mm, "end": v(15.43, -3.12) * mm});
            skLineSegment(sketch, "E2765", {"start": v(15.43, -3.12) * mm, "end": v(15.42, -3.12) * mm});
            skLineSegment(sketch, "E2766", {"start": v(15.42, -3.12) * mm, "end": v(15.4, -3.12) * mm});
            skLineSegment(sketch, "E2767", {"start": v(15.4, -3.12) * mm, "end": v(15.18, -3.17) * mm});
            skLineSegment(sketch, "E2768", {"start": v(15.18, -3.17) * mm, "end": v(15.16, -3.17) * mm});
            skLineSegment(sketch, "E2769", {"start": v(15.16, -3.17) * mm, "end": v(14.98, -3.2) * mm});
            skLineSegment(sketch, "E2770", {"start": v(14.98, -3.2) * mm, "end": v(14.92, -3.2) * mm});
            skLineSegment(sketch, "E2771", {"start": v(14.92, -3.2) * mm, "end": v(14.8, -3.22) * mm});
            skLineSegment(sketch, "E2772", {"start": v(14.8, -3.22) * mm, "end": v(14.7, -3.23) * mm});
            skLineSegment(sketch, "E2773", {"start": v(14.7, -3.23) * mm, "end": v(14.6, -3.24) * mm});
            skLineSegment(sketch, "E2774", {"start": v(14.6, -3.24) * mm, "end": v(14.54, -3.25) * mm});
            skLineSegment(sketch, "E2775", {"start": v(14.54, -3.25) * mm, "end": v(14.52, -3.26) * mm});
            skLineSegment(sketch, "E2776", {"start": v(14.52, -3.26) * mm, "end": v(14.5, -3.27) * mm});
            skLineSegment(sketch, "E2777", {"start": v(14.5, -3.27) * mm, "end": v(14.49, -3.28) * mm});
            skLineSegment(sketch, "E2778", {"start": v(14.49, -3.28) * mm, "end": v(14.35, -3.83) * mm});
            skLineSegment(sketch, "E2779", {"start": v(14.35, -3.83) * mm, "end": v(14.36, -3.85) * mm});
            skLineSegment(sketch, "E2780", {"start": v(14.36, -3.85) * mm, "end": v(14.37, -3.86) * mm});
            skLineSegment(sketch, "E2781", {"start": v(14.37, -3.86) * mm, "end": v(14.39, -3.88) * mm});
            skLineSegment(sketch, "E2782", {"start": v(14.39, -3.88) * mm, "end": v(14.43, -3.91) * mm});
            skLineSegment(sketch, "E2783", {"start": v(14.43, -3.91) * mm, "end": v(14.51, -3.97) * mm});
            skLineSegment(sketch, "E2784", {"start": v(14.51, -3.97) * mm, "end": v(14.6, -4.03) * mm});
            skLineSegment(sketch, "E2785", {"start": v(14.6, -4.03) * mm, "end": v(14.7, -4.1) * mm});
            skLineSegment(sketch, "E2786", {"start": v(14.7, -4.1) * mm, "end": v(14.75, -4.13) * mm});
            skLineSegment(sketch, "E2787", {"start": v(14.75, -4.13) * mm, "end": v(14.9, -4.24) * mm});
            skLineSegment(sketch, "E2788", {"start": v(14.9, -4.24) * mm, "end": v(14.91, -4.25) * mm});
            skLineSegment(sketch, "E2789", {"start": v(14.91, -4.25) * mm, "end": v(15.09, -4.39) * mm});
            skLineSegment(sketch, "E2790", {"start": v(15.09, -4.39) * mm, "end": v(15.1, -4.4) * mm});
            skLineSegment(sketch, "E2791", {"start": v(15.1, -4.4) * mm, "end": v(15.1, -4.4) * mm});
            skLineSegment(sketch, "E2792", {"start": v(15.1, -4.4) * mm, "end": v(15.26, -4.54) * mm});
            skLineSegment(sketch, "E2793", {"start": v(15.26, -4.54) * mm, "end": v(15.27, -4.55) * mm});
            skLineSegment(sketch, "E2794", {"start": v(15.27, -4.55) * mm, "end": v(15.32, -4.6) * mm});
            skLineSegment(sketch, "E2795", {"start": v(15.32, -4.6) * mm, "end": v(15.55, -4.82) * mm});
            skLineSegment(sketch, "E2796", {"start": v(15.55, -4.82) * mm, "end": v(15.6, -4.87) * mm});
            skLineSegment(sketch, "E2797", {"start": v(15.6, -4.87) * mm, "end": v(15.62, -4.94) * mm});
            skLineSegment(sketch, "E2798", {"start": v(15.62, -4.94) * mm, "end": v(15.56, -5.2) * mm});
            skLineSegment(sketch, "E2799", {"start": v(15.56, -5.2) * mm, "end": v(15.45, -5.43) * mm});
            skLineSegment(sketch, "E2800", {"start": v(15.45, -5.43) * mm, "end": v(15.39, -5.48) * mm});
            skLineSegment(sketch, "E2801", {"start": v(15.39, -5.48) * mm, "end": v(15.33, -5.5) * mm});
            skLineSegment(sketch, "E2802", {"start": v(15.33, -5.5) * mm, "end": v(15.01, -5.53) * mm});
            skLineSegment(sketch, "E2803", {"start": v(15.01, -5.53) * mm, "end": v(14.94, -5.54) * mm});
            skLineSegment(sketch, "E2804", {"start": v(14.94, -5.54) * mm, "end": v(14.92, -5.54) * mm});
            skLineSegment(sketch, "E2805", {"start": v(14.92, -5.54) * mm, "end": v(14.73, -5.55) * mm});
            skLineSegment(sketch, "E2806", {"start": v(14.73, -5.55) * mm, "end": v(14.72, -5.55) * mm});
            skLineSegment(sketch, "E2807", {"start": v(14.72, -5.55) * mm, "end": v(14.7, -5.55) * mm});
            skLineSegment(sketch, "E2808", {"start": v(14.7, -5.55) * mm, "end": v(14.48, -5.56) * mm});
            skLineSegment(sketch, "E2809", {"start": v(14.48, -5.56) * mm, "end": v(14.45, -5.56) * mm});
            skLineSegment(sketch, "E2810", {"start": v(14.45, -5.56) * mm, "end": v(14.28, -5.56) * mm});
            skLineSegment(sketch, "E2811", {"start": v(14.28, -5.56) * mm, "end": v(14.2, -5.56) * mm});
            skLineSegment(sketch, "E2812", {"start": v(14.2, -5.56) * mm, "end": v(14.1, -5.56) * mm});
            skLineSegment(sketch, "E2813", {"start": v(14.1, -5.56) * mm, "end": v(13.99, -5.55) * mm});
            skLineSegment(sketch, "E2814", {"start": v(13.99, -5.55) * mm, "end": v(13.89, -5.54) * mm});
            skLineSegment(sketch, "E2815", {"start": v(13.89, -5.54) * mm, "end": v(13.84, -5.54) * mm});
            skLineSegment(sketch, "E2816", {"start": v(13.84, -5.54) * mm, "end": v(13.8, -5.54) * mm});
            skLineSegment(sketch, "E2817", {"start": v(13.8, -5.54) * mm, "end": v(13.79, -5.55) * mm});
            skLineSegment(sketch, "E2818", {"start": v(13.79, -5.55) * mm, "end": v(13.77, -5.56) * mm});
            skLineSegment(sketch, "E2819", {"start": v(13.77, -5.56) * mm, "end": v(13.55, -6.08) * mm});
            skLineSegment(sketch, "E2820", {"start": v(13.55, -6.08) * mm, "end": v(13.56, -6.1) * mm});
            skLineSegment(sketch, "E2821", {"start": v(13.56, -6.1) * mm, "end": v(13.56, -6.12) * mm});
            skLineSegment(sketch, "E2822", {"start": v(13.56, -6.12) * mm, "end": v(13.58, -6.14) * mm});
            skLineSegment(sketch, "E2823", {"start": v(13.58, -6.14) * mm, "end": v(13.61, -6.18) * mm});
            skLineSegment(sketch, "E2824", {"start": v(13.61, -6.18) * mm, "end": v(13.69, -6.24) * mm});
            skLineSegment(sketch, "E2825", {"start": v(13.69, -6.24) * mm, "end": v(13.77, -6.32) * mm});
            skLineSegment(sketch, "E2826", {"start": v(13.77, -6.32) * mm, "end": v(13.85, -6.4) * mm});
            skLineSegment(sketch, "E2827", {"start": v(13.85, -6.4) * mm, "end": v(13.9, -6.44) * mm});
            skLineSegment(sketch, "E2828", {"start": v(13.9, -6.44) * mm, "end": v(14.02, -6.57) * mm});
            skLineSegment(sketch, "E2829", {"start": v(14.02, -6.57) * mm, "end": v(14.04, -6.59) * mm});
            skLineSegment(sketch, "E2830", {"start": v(14.04, -6.59) * mm, "end": v(14.19, -6.75) * mm});
            skLineSegment(sketch, "E2831", {"start": v(14.19, -6.75) * mm, "end": v(14.2, -6.77) * mm});
            skLineSegment(sketch, "E2832", {"start": v(14.2, -6.77) * mm, "end": v(14.2, -6.78) * mm});
            skLineSegment(sketch, "E2833", {"start": v(14.2, -6.78) * mm, "end": v(14.33, -6.93) * mm});
            skLineSegment(sketch, "E2834", {"start": v(14.33, -6.93) * mm, "end": v(14.34, -6.94) * mm});
            skLineSegment(sketch, "E2835", {"start": v(14.34, -6.94) * mm, "end": v(14.39, -7) * mm});
            skLineSegment(sketch, "E2836", {"start": v(14.39, -7) * mm, "end": v(14.58, -7.25) * mm});
            skLineSegment(sketch, "E2837", {"start": v(14.58, -7.25) * mm, "end": v(14.6, -7.3) * mm});
            skLineSegment(sketch, "E2838", {"start": v(14.6, -7.3) * mm, "end": v(14.62, -7.38) * mm});
            skLineSegment(sketch, "E2839", {"start": v(14.62, -7.38) * mm, "end": v(14.52, -7.62) * mm});
            skLineSegment(sketch, "E2840", {"start": v(14.52, -7.62) * mm, "end": v(14.38, -7.84) * mm});
            skLineSegment(sketch, "E2841", {"start": v(14.38, -7.84) * mm, "end": v(14.31, -7.87) * mm});
            skLineSegment(sketch, "E2842", {"start": v(14.31, -7.87) * mm, "end": v(14.25, -7.88) * mm});
            skLineSegment(sketch, "E2843", {"start": v(14.25, -7.88) * mm, "end": v(13.93, -7.87) * mm});
            skLineSegment(sketch, "E2844", {"start": v(13.93, -7.87) * mm, "end": v(13.86, -7.86) * mm});
            skLineSegment(sketch, "E2845", {"start": v(13.86, -7.86) * mm, "end": v(13.84, -7.86) * mm});
            skLineSegment(sketch, "E2846", {"start": v(13.84, -7.86) * mm, "end": v(13.65, -7.84) * mm});
            skLineSegment(sketch, "E2847", {"start": v(13.65, -7.84) * mm, "end": v(13.64, -7.84) * mm});
            skLineSegment(sketch, "E2848", {"start": v(13.64, -7.84) * mm, "end": v(13.62, -7.84) * mm});
            skLineSegment(sketch, "E2849", {"start": v(13.62, -7.84) * mm, "end": v(13.4, -7.81) * mm});
            skLineSegment(sketch, "E2850", {"start": v(13.4, -7.81) * mm, "end": v(13.37, -7.8) * mm});
            skLineSegment(sketch, "E2851", {"start": v(13.37, -7.8) * mm, "end": v(13.2, -7.78) * mm});
            skLineSegment(sketch, "E2852", {"start": v(13.2, -7.78) * mm, "end": v(13.13, -7.77) * mm});
            skLineSegment(sketch, "E2853", {"start": v(13.13, -7.77) * mm, "end": v(13.03, -7.75) * mm});
            skLineSegment(sketch, "E2854", {"start": v(13.03, -7.75) * mm, "end": v(12.92, -7.72) * mm});
            skLineSegment(sketch, "E2855", {"start": v(12.92, -7.72) * mm, "end": v(12.82, -7.7) * mm});
            skLineSegment(sketch, "E2856", {"start": v(12.82, -7.7) * mm, "end": v(12.77, -7.69) * mm});
            skLineSegment(sketch, "E2857", {"start": v(12.77, -7.69) * mm, "end": v(12.74, -7.69) * mm});
            skLineSegment(sketch, "E2858", {"start": v(12.74, -7.69) * mm, "end": v(12.72, -7.7) * mm});
            skLineSegment(sketch, "E2859", {"start": v(12.72, -7.7) * mm, "end": v(12.7, -7.7) * mm});
            skLineSegment(sketch, "E2860", {"start": v(12.7, -7.7) * mm, "end": v(12.4, -8.18) * mm});
            skLineSegment(sketch, "E2861", {"start": v(12.4, -8.18) * mm, "end": v(12.4, -8.2) * mm});
            skLineSegment(sketch, "E2862", {"start": v(12.4, -8.2) * mm, "end": v(12.4, -8.21) * mm});
            skLineSegment(sketch, "E2863", {"start": v(12.4, -8.21) * mm, "end": v(12.42, -8.24) * mm});
            skLineSegment(sketch, "E2864", {"start": v(12.42, -8.24) * mm, "end": v(12.45, -8.28) * mm});
            skLineSegment(sketch, "E2865", {"start": v(12.45, -8.28) * mm, "end": v(12.51, -8.36) * mm});
            skLineSegment(sketch, "E2866", {"start": v(12.51, -8.36) * mm, "end": v(12.58, -8.45) * mm});
            skLineSegment(sketch, "E2867", {"start": v(12.58, -8.45) * mm, "end": v(12.65, -8.53) * mm});
            skLineSegment(sketch, "E2868", {"start": v(12.65, -8.53) * mm, "end": v(12.69, -8.59) * mm});
            skLineSegment(sketch, "E2869", {"start": v(12.69, -8.59) * mm, "end": v(12.79, -8.74) * mm});
            skLineSegment(sketch, "E2870", {"start": v(12.79, -8.74) * mm, "end": v(12.8, -8.75) * mm});
            skLineSegment(sketch, "E2871", {"start": v(12.8, -8.75) * mm, "end": v(12.92, -8.94) * mm});
            skLineSegment(sketch, "E2872", {"start": v(12.92, -8.94) * mm, "end": v(12.93, -8.96) * mm});
            skLineSegment(sketch, "E2873", {"start": v(12.93, -8.96) * mm, "end": v(12.94, -8.97) * mm});
            skLineSegment(sketch, "E2874", {"start": v(12.94, -8.97) * mm, "end": v(13.03, -9.14) * mm});
            skLineSegment(sketch, "E2875", {"start": v(13.03, -9.14) * mm, "end": v(13.04, -9.15) * mm});
            skLineSegment(sketch, "E2876", {"start": v(13.04, -9.15) * mm, "end": v(13.08, -9.22) * mm});
            skLineSegment(sketch, "E2877", {"start": v(13.08, -9.22) * mm, "end": v(13.23, -9.5) * mm});
            skLineSegment(sketch, "E2878", {"start": v(13.23, -9.5) * mm, "end": v(13.25, -9.55) * mm});
            skLineSegment(sketch, "E2879", {"start": v(13.25, -9.55) * mm, "end": v(13.25, -9.63) * mm});
            skLineSegment(sketch, "E2880", {"start": v(13.25, -9.63) * mm, "end": v(13.11, -9.85) * mm});
            skLineSegment(sketch, "E2881", {"start": v(13.11, -9.85) * mm, "end": v(12.94, -10.05) * mm});
            skLineSegment(sketch, "E2882", {"start": v(12.94, -10.05) * mm, "end": v(12.86, -10.07) * mm});
            skLineSegment(sketch, "E2883", {"start": v(12.86, -10.07) * mm, "end": v(12.8, -10.06) * mm});
            skLineSegment(sketch, "E2884", {"start": v(12.8, -10.06) * mm, "end": v(12.5, -10) * mm});
            skLineSegment(sketch, "E2885", {"start": v(12.5, -10) * mm, "end": v(12.42, -9.98) * mm});
            skLineSegment(sketch, "E2886", {"start": v(12.42, -9.98) * mm, "end": v(12.4, -9.98) * mm});
            skLineSegment(sketch, "E2887", {"start": v(12.4, -9.98) * mm, "end": v(12.21, -9.93) * mm});
            skLineSegment(sketch, "E2888", {"start": v(12.21, -9.93) * mm, "end": v(12.2, -9.93) * mm});
            skLineSegment(sketch, "E2889", {"start": v(12.2, -9.93) * mm, "end": v(12.18, -9.92) * mm});
            skLineSegment(sketch, "E2890", {"start": v(12.18, -9.92) * mm, "end": v(11.97, -9.86) * mm});
            skLineSegment(sketch, "E2891", {"start": v(11.97, -9.86) * mm, "end": v(11.95, -9.85) * mm});
            skLineSegment(sketch, "E2892", {"start": v(11.95, -9.85) * mm, "end": v(11.78, -9.8) * mm});
            skLineSegment(sketch, "E2893", {"start": v(11.78, -9.8) * mm, "end": v(11.72, -9.77) * mm});
            skLineSegment(sketch, "E2894", {"start": v(11.72, -9.77) * mm, "end": v(11.62, -9.73) * mm});
            skLineSegment(sketch, "E2895", {"start": v(11.62, -9.73) * mm, "end": v(11.5, -9.7) * mm});
            skLineSegment(sketch, "E2896", {"start": v(11.5, -9.7) * mm, "end": v(11.42, -9.65) * mm});
            skLineSegment(sketch, "E2897", {"start": v(11.42, -9.65) * mm, "end": v(11.37, -9.64) * mm});
            skLineSegment(sketch, "E2898", {"start": v(11.37, -9.64) * mm, "end": v(11.34, -9.63) * mm});
            skLineSegment(sketch, "E2899", {"start": v(11.34, -9.63) * mm, "end": v(11.32, -9.63) * mm});
            skLineSegment(sketch, "E2900", {"start": v(11.32, -9.63) * mm, "end": v(11.3, -9.64) * mm});
            skLineSegment(sketch, "E2901", {"start": v(11.3, -9.64) * mm, "end": v(10.93, -10.06) * mm});
            skLineSegment(sketch, "E2902", {"start": v(10.93, -10.06) * mm, "end": v(10.93, -10.08) * mm});
            skLineSegment(sketch, "E2903", {"start": v(10.93, -10.08) * mm, "end": v(10.93, -10.1) * mm});
            skLineSegment(sketch, "E2904", {"start": v(10.93, -10.1) * mm, "end": v(10.94, -10.12) * mm});
            skLineSegment(sketch, "E2905", {"start": v(10.94, -10.12) * mm, "end": v(10.96, -10.17) * mm});
            skLineSegment(sketch, "E2906", {"start": v(10.96, -10.17) * mm, "end": v(11, -10.26) * mm});
            skLineSegment(sketch, "E2907", {"start": v(11, -10.26) * mm, "end": v(11.06, -10.36) * mm});
            skLineSegment(sketch, "E2908", {"start": v(11.06, -10.36) * mm, "end": v(11.11, -10.45) * mm});
            skLineSegment(sketch, "E2909", {"start": v(11.11, -10.45) * mm, "end": v(11.14, -10.51) * mm});
            skLineSegment(sketch, "E2910", {"start": v(11.14, -10.51) * mm, "end": v(11.22, -10.67) * mm});
            skLineSegment(sketch, "E2911", {"start": v(11.22, -10.67) * mm, "end": v(11.23, -10.7) * mm});
            skLineSegment(sketch, "E2912", {"start": v(11.23, -10.7) * mm, "end": v(11.32, -10.9) * mm});
            skLineSegment(sketch, "E2913", {"start": v(11.32, -10.9) * mm, "end": v(11.33, -10.92) * mm});
            skLineSegment(sketch, "E2914", {"start": v(11.33, -10.92) * mm, "end": v(11.33, -10.93) * mm});
            skLineSegment(sketch, "E2915", {"start": v(11.33, -10.93) * mm, "end": v(11.4, -11.1) * mm});
            skLineSegment(sketch, "E2916", {"start": v(11.4, -11.1) * mm, "end": v(11.4, -11.13) * mm});
            skLineSegment(sketch, "E2917", {"start": v(11.4, -11.13) * mm, "end": v(11.43, -11.2) * mm});
            skLineSegment(sketch, "E2918", {"start": v(11.43, -11.2) * mm, "end": v(11.53, -11.5) * mm});
            skLineSegment(sketch, "E2919", {"start": v(11.53, -11.5) * mm, "end": v(11.54, -11.55) * mm});
            skLineSegment(sketch, "E2920", {"start": v(11.54, -11.55) * mm, "end": v(11.53, -11.63) * mm});
            skLineSegment(sketch, "E2921", {"start": v(11.53, -11.63) * mm, "end": v(11.36, -11.83) * mm});
            skLineSegment(sketch, "E2922", {"start": v(11.36, -11.83) * mm, "end": v(11.16, -12) * mm});
            skLineSegment(sketch, "E2923", {"start": v(11.16, -12) * mm, "end": v(11.08, -12) * mm});
            skLineSegment(sketch, "E2924", {"start": v(11.08, -12) * mm, "end": v(11.02, -11.99) * mm});
            skLineSegment(sketch, "E2925", {"start": v(11.02, -11.99) * mm, "end": v(10.72, -11.87) * mm});
            skLineSegment(sketch, "E2926", {"start": v(10.72, -11.87) * mm, "end": v(10.66, -11.85) * mm});
            skLineSegment(sketch, "E2927", {"start": v(10.66, -11.85) * mm, "end": v(10.64, -11.84) * mm});
            skLineSegment(sketch, "E2928", {"start": v(10.64, -11.84) * mm, "end": v(10.46, -11.76) * mm});
            skLineSegment(sketch, "E2929", {"start": v(10.46, -11.76) * mm, "end": v(10.46, -11.76) * mm});
            skLineSegment(sketch, "E2930", {"start": v(10.46, -11.76) * mm, "end": v(10.43, -11.75) * mm});
            skLineSegment(sketch, "E2931", {"start": v(10.43, -11.75) * mm, "end": v(10.23, -11.65) * mm});
            skLineSegment(sketch, "E2932", {"start": v(10.23, -11.65) * mm, "end": v(10.21, -11.64) * mm});
            skLineSegment(sketch, "E2933", {"start": v(10.21, -11.64) * mm, "end": v(10.06, -11.56) * mm});
            skLineSegment(sketch, "E2934", {"start": v(10.06, -11.56) * mm, "end": v(10, -11.53) * mm});
            skLineSegment(sketch, "E2935", {"start": v(10, -11.53) * mm, "end": v(9.9, -11.47) * mm});
            skLineSegment(sketch, "E2936", {"start": v(9.9, -11.47) * mm, "end": v(9.8, -11.41) * mm});
            skLineSegment(sketch, "E2937", {"start": v(9.8, -11.41) * mm, "end": v(9.72, -11.36) * mm});
            skLineSegment(sketch, "E2938", {"start": v(9.72, -11.36) * mm, "end": v(9.68, -11.34) * mm});
            skLineSegment(sketch, "E2939", {"start": v(9.68, -11.34) * mm, "end": v(9.65, -11.33) * mm});
            skLineSegment(sketch, "E2940", {"start": v(9.65, -11.33) * mm, "end": v(9.63, -11.33) * mm});
            skLineSegment(sketch, "E2941", {"start": v(9.63, -11.33) * mm, "end": v(9.61, -11.33) * mm});
            skLineSegment(sketch, "E2942", {"start": v(9.61, -11.33) * mm, "end": v(9.17, -11.68) * mm});
            skLineSegment(sketch, "E2943", {"start": v(9.17, -11.68) * mm, "end": v(9.17, -11.7) * mm});
            skLineSegment(sketch, "E2944", {"start": v(9.17, -11.7) * mm, "end": v(9.17, -11.72) * mm});
            skLineSegment(sketch, "E2945", {"start": v(9.17, -11.72) * mm, "end": v(9.17, -11.75) * mm});
            skLineSegment(sketch, "E2946", {"start": v(9.17, -11.75) * mm, "end": v(9.18, -11.8) * mm});
            skLineSegment(sketch, "E2947", {"start": v(9.18, -11.8) * mm, "end": v(9.22, -11.9) * mm});
            skLineSegment(sketch, "E2948", {"start": v(9.22, -11.9) * mm, "end": v(9.26, -12) * mm});
            skLineSegment(sketch, "E2949", {"start": v(9.26, -12) * mm, "end": v(9.3, -12.1) * mm});
            skLineSegment(sketch, "E2950", {"start": v(9.3, -12.1) * mm, "end": v(9.31, -12.17) * mm});
            skLineSegment(sketch, "E2951", {"start": v(9.31, -12.17) * mm, "end": v(9.36, -12.34) * mm});
            skLineSegment(sketch, "E2952", {"start": v(9.36, -12.34) * mm, "end": v(9.37, -12.36) * mm});
            skLineSegment(sketch, "E2953", {"start": v(9.37, -12.36) * mm, "end": v(9.42, -12.57) * mm});
            skLineSegment(sketch, "E2954", {"start": v(9.42, -12.57) * mm, "end": v(9.43, -12.6) * mm});
            skLineSegment(sketch, "E2955", {"start": v(9.43, -12.6) * mm, "end": v(9.43, -12.6) * mm});
            skLineSegment(sketch, "E2956", {"start": v(9.43, -12.6) * mm, "end": v(9.47, -12.8) * mm});
            skLineSegment(sketch, "E2957", {"start": v(9.47, -12.8) * mm, "end": v(9.48, -12.81) * mm});
            skLineSegment(sketch, "E2958", {"start": v(9.48, -12.81) * mm, "end": v(9.49, -12.88) * mm});
            skLineSegment(sketch, "E2959", {"start": v(9.49, -12.88) * mm, "end": v(9.54, -13.2) * mm});
            skLineSegment(sketch, "E2960", {"start": v(9.54, -13.2) * mm, "end": v(9.54, -13.26) * mm});
            skLineSegment(sketch, "E2961", {"start": v(9.54, -13.26) * mm, "end": v(9.52, -13.33) * mm});
            skLineSegment(sketch, "E2962", {"start": v(9.52, -13.33) * mm, "end": v(9.32, -13.5) * mm});
            skLineSegment(sketch, "E2963", {"start": v(9.32, -13.5) * mm, "end": v(9.1, -13.63) * mm});
            skLineSegment(sketch, "E2964", {"start": v(9.1, -13.63) * mm, "end": v(9.01, -13.62) * mm});
            skLineSegment(sketch, "E2965", {"start": v(9.01, -13.62) * mm, "end": v(8.95, -13.6) * mm});
            skLineSegment(sketch, "E2966", {"start": v(8.95, -13.6) * mm, "end": v(8.68, -13.44) * mm});
            skLineSegment(sketch, "E2967", {"start": v(8.68, -13.44) * mm, "end": v(8.62, -13.4) * mm});
            skLineSegment(sketch, "E2968", {"start": v(8.62, -13.4) * mm, "end": v(8.6, -13.4) * mm});
            skLineSegment(sketch, "E2969", {"start": v(8.6, -13.4) * mm, "end": v(8.44, -13.29) * mm});
            skLineSegment(sketch, "E2970", {"start": v(8.44, -13.29) * mm, "end": v(8.43, -13.28) * mm});
            skLineSegment(sketch, "E2971", {"start": v(8.43, -13.28) * mm, "end": v(8.41, -13.27) * mm});
            skLineSegment(sketch, "E2972", {"start": v(8.41, -13.27) * mm, "end": v(8.23, -13.14) * mm});
            skLineSegment(sketch, "E2973", {"start": v(8.23, -13.14) * mm, "end": v(8.21, -13.13) * mm});
            skLineSegment(sketch, "E2974", {"start": v(8.21, -13.13) * mm, "end": v(8.07, -13.02) * mm});
            skLineSegment(sketch, "E2975", {"start": v(8.07, -13.02) * mm, "end": v(8.02, -12.98) * mm});
            skLineSegment(sketch, "E2976", {"start": v(8.02, -12.98) * mm, "end": v(7.94, -12.91) * mm});
            skLineSegment(sketch, "E2977", {"start": v(7.94, -12.91) * mm, "end": v(7.85, -12.84) * mm});
            skLineSegment(sketch, "E2978", {"start": v(7.85, -12.84) * mm, "end": v(7.77, -12.77) * mm});
            skLineSegment(sketch, "E2979", {"start": v(7.77, -12.77) * mm, "end": v(7.73, -12.74) * mm});
            skLineSegment(sketch, "E2980", {"start": v(7.73, -12.74) * mm, "end": v(7.7, -12.73) * mm});
            skLineSegment(sketch, "E2981", {"start": v(7.7, -12.73) * mm, "end": v(7.69, -12.72) * mm});
            skLineSegment(sketch, "E2982", {"start": v(7.69, -12.72) * mm, "end": v(7.67, -12.72) * mm});
            skLineSegment(sketch, "E2983", {"start": v(7.67, -12.72) * mm, "end": v(7.18, -13) * mm});
            skLineSegment(sketch, "E2984", {"start": v(7.18, -13) * mm, "end": v(7.17, -13.02) * mm});
            skLineSegment(sketch, "E2985", {"start": v(7.17, -13.02) * mm, "end": v(7.17, -13.04) * mm});
            skLineSegment(sketch, "E2986", {"start": v(7.17, -13.04) * mm, "end": v(7.17, -13.07) * mm});
            skLineSegment(sketch, "E2987", {"start": v(7.17, -13.07) * mm, "end": v(7.17, -13.12) * mm});
            skLineSegment(sketch, "E2988", {"start": v(7.17, -13.12) * mm, "end": v(7.2, -13.22) * mm});
            skLineSegment(sketch, "E2989", {"start": v(7.2, -13.22) * mm, "end": v(7.21, -13.33) * mm});
            skLineSegment(sketch, "E2990", {"start": v(7.21, -13.33) * mm, "end": v(7.23, -13.43) * mm});
            skLineSegment(sketch, "E2991", {"start": v(7.23, -13.43) * mm, "end": v(7.24, -13.5) * mm});
            skLineSegment(sketch, "E2992", {"start": v(7.24, -13.5) * mm, "end": v(7.26, -13.68) * mm});
            skLineSegment(sketch, "E2993", {"start": v(7.26, -13.68) * mm, "end": v(7.27, -13.7) * mm});
            skLineSegment(sketch, "E2994", {"start": v(7.27, -13.7) * mm, "end": v(7.29, -13.92) * mm});
            skLineSegment(sketch, "E2995", {"start": v(7.29, -13.92) * mm, "end": v(7.29, -13.95) * mm});
            skLineSegment(sketch, "E2996", {"start": v(7.29, -13.95) * mm, "end": v(7.29, -13.95) * mm});
            skLineSegment(sketch, "E2997", {"start": v(7.29, -13.95) * mm, "end": v(7.3, -14.15) * mm});
            skLineSegment(sketch, "E2998", {"start": v(7.3, -14.15) * mm, "end": v(7.3, -14.17) * mm});
            skLineSegment(sketch, "E2999", {"start": v(7.3, -14.17) * mm, "end": v(7.3, -14.24) * mm});
            skLineSegment(sketch, "E3000", {"start": v(7.3, -14.24) * mm, "end": v(7.3, -14.55) * mm});
            skLineSegment(sketch, "E3001", {"start": v(7.3, -14.55) * mm, "end": v(7.3, -14.62) * mm});
            skLineSegment(sketch, "E3002", {"start": v(7.3, -14.62) * mm, "end": v(7.26, -14.69) * mm});
            skLineSegment(sketch, "E3003", {"start": v(7.26, -14.69) * mm, "end": v(7.03, -14.82) * mm});
            skLineSegment(sketch, "E3004", {"start": v(7.03, -14.82) * mm, "end": v(6.79, -14.9) * mm});
            skLineSegment(sketch, "E3005", {"start": v(6.79, -14.9) * mm, "end": v(6.71, -14.9) * mm});
            skLineSegment(sketch, "E3006", {"start": v(6.71, -14.9) * mm, "end": v(6.66, -14.86) * mm});
            skLineSegment(sketch, "E3007", {"start": v(6.66, -14.86) * mm, "end": v(6.41, -14.66) * mm});
            skLineSegment(sketch, "E3008", {"start": v(6.41, -14.66) * mm, "end": v(6.36, -14.61) * mm});
            skLineSegment(sketch, "E3009", {"start": v(6.36, -14.61) * mm, "end": v(6.34, -14.6) * mm});
            skLineSegment(sketch, "E3010", {"start": v(6.34, -14.6) * mm, "end": v(6.2, -14.47) * mm});
            skLineSegment(sketch, "E3011", {"start": v(6.2, -14.47) * mm, "end": v(6.2, -14.46) * mm});
            skLineSegment(sketch, "E3012", {"start": v(6.2, -14.46) * mm, "end": v(6.18, -14.45) * mm});
            skLineSegment(sketch, "E3013", {"start": v(6.18, -14.45) * mm, "end": v(6.02, -14.3) * mm});
            skLineSegment(sketch, "E3014", {"start": v(6.02, -14.3) * mm, "end": v(6, -14.28) * mm});
            skLineSegment(sketch, "E3015", {"start": v(6, -14.28) * mm, "end": v(5.88, -14.15) * mm});
            skLineSegment(sketch, "E3016", {"start": v(5.88, -14.15) * mm, "end": v(5.83, -14.1) * mm});
            skLineSegment(sketch, "E3017", {"start": v(5.83, -14.1) * mm, "end": v(5.76, -14.02) * mm});
            skLineSegment(sketch, "E3018", {"start": v(5.76, -14.02) * mm, "end": v(5.69, -13.93) * mm});
            skLineSegment(sketch, "E3019", {"start": v(5.69, -13.93) * mm, "end": v(5.62, -13.85) * mm});
            skLineSegment(sketch, "E3020", {"start": v(5.62, -13.85) * mm, "end": v(5.59, -13.82) * mm});
            skLineSegment(sketch, "E3021", {"start": v(5.59, -13.82) * mm, "end": v(5.57, -13.8) * mm});
            skLineSegment(sketch, "E3022", {"start": v(5.57, -13.8) * mm, "end": v(5.55, -13.8) * mm});
            skLineSegment(sketch, "E3023", {"start": v(5.55, -13.8) * mm, "end": v(5.53, -13.79) * mm});
            skLineSegment(sketch, "E3024", {"start": v(5.53, -13.79) * mm, "end": v(5, -13.99) * mm});
            skLineSegment(sketch, "E3025", {"start": v(5, -13.99) * mm, "end": v(5, -14) * mm});
            skLineSegment(sketch, "E3026", {"start": v(5, -14) * mm, "end": v(4.98, -14.02) * mm});
            skLineSegment(sketch, "E3027", {"start": v(4.98, -14.02) * mm, "end": v(4.98, -14.05) * mm});
            skLineSegment(sketch, "E3028", {"start": v(4.98, -14.05) * mm, "end": v(4.98, -14.1) * mm});
            skLineSegment(sketch, "E3029", {"start": v(4.98, -14.1) * mm, "end": v(4.98, -14.2) * mm});
            skLineSegment(sketch, "E3030", {"start": v(4.98, -14.2) * mm, "end": v(4.98, -14.31) * mm});
            skLineSegment(sketch, "E3031", {"start": v(4.98, -14.31) * mm, "end": v(4.98, -14.42) * mm});
            skLineSegment(sketch, "E3032", {"start": v(4.98, -14.42) * mm, "end": v(4.98, -14.49) * mm});
            skLineSegment(sketch, "E3033", {"start": v(4.98, -14.49) * mm, "end": v(4.98, -14.67) * mm});
            skLineSegment(sketch, "E3034", {"start": v(4.98, -14.67) * mm, "end": v(4.97, -14.69) * mm});
            skLineSegment(sketch, "E3035", {"start": v(4.97, -14.69) * mm, "end": v(4.96, -14.9) * mm});
            skLineSegment(sketch, "E3036", {"start": v(4.96, -14.9) * mm, "end": v(4.96, -14.93) * mm});
            skLineSegment(sketch, "E3037", {"start": v(4.96, -14.93) * mm, "end": v(4.95, -14.94) * mm});
            skLineSegment(sketch, "E3038", {"start": v(4.95, -14.94) * mm, "end": v(4.93, -15.13) * mm});
            skLineSegment(sketch, "E3039", {"start": v(4.93, -15.13) * mm, "end": v(4.93, -15.15) * mm});
            skLineSegment(sketch, "E3040", {"start": v(4.93, -15.15) * mm, "end": v(4.92, -15.22) * mm});
            skLineSegment(sketch, "E3041", {"start": v(4.92, -15.22) * mm, "end": v(4.87, -15.54) * mm});
            skLineSegment(sketch, "E3042", {"start": v(4.87, -15.54) * mm, "end": v(4.85, -15.6) * mm});
            skLineSegment(sketch, "E3043", {"start": v(4.85, -15.6) * mm, "end": v(4.8, -15.66) * mm});
            skLineSegment(sketch, "E3044", {"start": v(4.8, -15.66) * mm, "end": v(4.56, -15.75) * mm});
            skLineSegment(sketch, "E3045", {"start": v(4.56, -15.75) * mm, "end": v(4.3, -15.8) * mm});
            skLineSegment(sketch, "E3046", {"start": v(4.3, -15.8) * mm, "end": v(4.23, -15.78) * mm});
            skLineSegment(sketch, "E3047", {"start": v(4.23, -15.78) * mm, "end": v(4.19, -15.73) * mm});
            skLineSegment(sketch, "E3048", {"start": v(4.19, -15.73) * mm, "end": v(3.98, -15.5) * mm});
            skLineSegment(sketch, "E3049", {"start": v(3.98, -15.5) * mm, "end": v(3.93, -15.44) * mm});
            skLineSegment(sketch, "E3050", {"start": v(3.93, -15.44) * mm, "end": v(3.92, -15.43) * mm});
            skLineSegment(sketch, "E3051", {"start": v(3.92, -15.43) * mm, "end": v(3.8, -15.27) * mm});
            skLineSegment(sketch, "E3052", {"start": v(3.8, -15.27) * mm, "end": v(3.8, -15.27) * mm});
            skLineSegment(sketch, "E3053", {"start": v(3.8, -15.27) * mm, "end": v(3.78, -15.25) * mm});
            skLineSegment(sketch, "E3054", {"start": v(3.78, -15.25) * mm, "end": v(3.65, -15.07) * mm});
            skLineSegment(sketch, "E3055", {"start": v(3.65, -15.07) * mm, "end": v(3.63, -15.06) * mm});
            skLineSegment(sketch, "E3056", {"start": v(3.63, -15.06) * mm, "end": v(3.53, -14.9) * mm});
            skLineSegment(sketch, "E3057", {"start": v(3.53, -14.9) * mm, "end": v(3.5, -14.85) * mm});
            skLineSegment(sketch, "E3058", {"start": v(3.5, -14.85) * mm, "end": v(3.44, -14.76) * mm});
            skLineSegment(sketch, "E3059", {"start": v(3.44, -14.76) * mm, "end": v(3.38, -14.66) * mm});
            skLineSegment(sketch, "E3060", {"start": v(3.38, -14.66) * mm, "end": v(3.33, -14.57) * mm});
            skLineSegment(sketch, "E3061", {"start": v(3.33, -14.57) * mm, "end": v(3.3, -14.53) * mm});
            skLineSegment(sketch, "E3062", {"start": v(3.3, -14.53) * mm, "end": v(3.28, -14.51) * mm});
            skLineSegment(sketch, "E3063", {"start": v(3.28, -14.51) * mm, "end": v(3.26, -14.5) * mm});
            skLineSegment(sketch, "E3064", {"start": v(3.26, -14.5) * mm, "end": v(3.25, -14.5) * mm});
            skLineSegment(sketch, "E3065", {"start": v(3.25, -14.5) * mm, "end": v(2.7, -14.6) * mm});
            skLineSegment(sketch, "E3066", {"start": v(2.7, -14.6) * mm, "end": v(2.68, -14.62) * mm});
            skLineSegment(sketch, "E3067", {"start": v(2.68, -14.62) * mm, "end": v(2.67, -14.64) * mm});
            skLineSegment(sketch, "E3068", {"start": v(2.67, -14.64) * mm, "end": v(2.66, -14.66) * mm});
            skLineSegment(sketch, "E3069", {"start": v(2.66, -14.66) * mm, "end": v(2.65, -14.71) * mm});
            skLineSegment(sketch, "E3070", {"start": v(2.65, -14.71) * mm, "end": v(2.64, -14.81) * mm});
            skLineSegment(sketch, "E3071", {"start": v(2.64, -14.81) * mm, "end": v(2.62, -14.93) * mm});
            skLineSegment(sketch, "E3072", {"start": v(2.62, -14.93) * mm, "end": v(2.6, -15.03) * mm});
            skLineSegment(sketch, "E3073", {"start": v(2.6, -15.03) * mm, "end": v(2.6, -15.1) * mm});
            skLineSegment(sketch, "E3074", {"start": v(2.6, -15.1) * mm, "end": v(2.56, -15.27) * mm});
            skLineSegment(sketch, "E3075", {"start": v(2.56, -15.27) * mm, "end": v(2.55, -15.3) * mm});
            skLineSegment(sketch, "E3076", {"start": v(2.55, -15.3) * mm, "end": v(2.5, -15.51) * mm});
            skLineSegment(sketch, "E3077", {"start": v(2.5, -15.51) * mm, "end": v(2.5, -15.54) * mm});
            skLineSegment(sketch, "E3078", {"start": v(2.5, -15.54) * mm, "end": v(2.5, -15.54) * mm});
            skLineSegment(sketch, "E3079", {"start": v(2.5, -15.54) * mm, "end": v(2.44, -15.73) * mm});
            skLineSegment(sketch, "E3080", {"start": v(2.44, -15.73) * mm, "end": v(2.44, -15.75) * mm});
            skLineSegment(sketch, "E3081", {"start": v(2.44, -15.75) * mm, "end": v(2.41, -15.82) * mm});
            skLineSegment(sketch, "E3082", {"start": v(2.41, -15.82) * mm, "end": v(2.31, -16.12) * mm});
            skLineSegment(sketch, "E3083", {"start": v(2.31, -16.12) * mm, "end": v(2.29, -16.17) * mm});
            skLineSegment(sketch, "E3084", {"start": v(2.29, -16.17) * mm, "end": v(2.23, -16.23) * mm});
            skLineSegment(sketch, "E3085", {"start": v(2.23, -16.23) * mm, "end": v(1.98, -16.28) * mm});
            skLineSegment(sketch, "E3086", {"start": v(1.98, -16.28) * mm, "end": v(1.72, -16.3) * mm});
            skLineSegment(sketch, "E3087", {"start": v(1.72, -16.3) * mm, "end": v(1.65, -16.25) * mm});
            skLineSegment(sketch, "E3088", {"start": v(1.65, -16.25) * mm, "end": v(1.6, -16.2) * mm});
            skLineSegment(sketch, "E3089", {"start": v(1.6, -16.2) * mm, "end": v(1.44, -15.94) * mm});
            skLineSegment(sketch, "E3090", {"start": v(1.44, -15.94) * mm, "end": v(1.4, -15.87) * mm});
            skLineSegment(sketch, "E3091", {"start": v(1.4, -15.87) * mm, "end": v(1.4, -15.85) * mm});
            skLineSegment(sketch, "E3092", {"start": v(1.4, -15.85) * mm, "end": v(1.3, -15.69) * mm});
            skLineSegment(sketch, "E3093", {"start": v(1.3, -15.69) * mm, "end": v(1.3, -15.68) * mm});
            skLineSegment(sketch, "E3094", {"start": v(1.3, -15.68) * mm, "end": v(1.28, -15.66) * mm});
            skLineSegment(sketch, "E3095", {"start": v(1.28, -15.66) * mm, "end": v(1.18, -15.46) * mm});
            skLineSegment(sketch, "E3096", {"start": v(1.18, -15.46) * mm, "end": v(1.17, -15.44) * mm});
            skLineSegment(sketch, "E3097", {"start": v(1.17, -15.44) * mm, "end": v(1.1, -15.28) * mm});
            skLineSegment(sketch, "E3098", {"start": v(1.1, -15.28) * mm, "end": v(1.07, -15.22) * mm});
            skLineSegment(sketch, "E3099", {"start": v(1.07, -15.22) * mm, "end": v(1.03, -15.12) * mm});
            skLineSegment(sketch, "E3100", {"start": v(1.03, -15.12) * mm, "end": v(0.98, -15.01) * mm});
            skLineSegment(sketch, "E3101", {"start": v(0.98, -15.01) * mm, "end": v(0.95, -14.92) * mm});
            skLineSegment(sketch, "E3102", {"start": v(0.95, -14.92) * mm, "end": v(0.92, -14.87) * mm});
            skLineSegment(sketch, "E3103", {"start": v(0.92, -14.87) * mm, "end": v(0.9, -14.85) * mm});
            skLineSegment(sketch, "E3104", {"start": v(0.9, -14.85) * mm, "end": v(0.9, -14.84) * mm});
            skLineSegment(sketch, "E3105", {"start": v(0.9, -14.84) * mm, "end": v(0.88, -14.83) * mm});
            skLineSegment(sketch, "E3106", {"start": v(0.88, -14.83) * mm, "end": v(0.32, -14.85) * mm});
            skLineSegment(sketch, "E3107", {"start": v(0.32, -14.85) * mm, "end": v(0.3, -14.86) * mm});
            skLineSegment(sketch, "E3108", {"start": v(0.3, -14.86) * mm, "end": v(0.29, -14.88) * mm});
            skLineSegment(sketch, "E3109", {"start": v(0.29, -14.88) * mm, "end": v(0.28, -14.9) * mm});
            skLineSegment(sketch, "E3110", {"start": v(0.28, -14.9) * mm, "end": v(0.26, -14.95) * mm});
            skLineSegment(sketch, "E3111", {"start": v(0.26, -14.95) * mm, "end": v(0.23, -15.04) * mm});
            skLineSegment(sketch, "E3112", {"start": v(0.23, -15.04) * mm, "end": v(0.2, -15.15) * mm});
            skLineSegment(sketch, "E3113", {"start": v(0.2, -15.15) * mm, "end": v(0.16, -15.26) * mm});
            skLineSegment(sketch, "E3114", {"start": v(0.16, -15.26) * mm, "end": v(0.14, -15.32) * mm});
            skLineSegment(sketch, "E3115", {"start": v(0.14, -15.32) * mm, "end": v(0.08, -15.49) * mm});
            skLineSegment(sketch, "E3116", {"start": v(0.08, -15.49) * mm, "end": v(0.07, -15.5) * mm});
            skLineSegment(sketch, "E3117", {"start": v(0.07, -15.5) * mm, "end": v(-0.02, -15.71) * mm});
            skLineSegment(sketch, "E3118", {"start": v(-0.02, -15.71) * mm, "end": v(-0.03, -15.74) * mm});
            skLineSegment(sketch, "E3119", {"start": v(-0.03, -15.74) * mm, "end": v(-0.03, -15.74) * mm});
            skLineSegment(sketch, "E3120", {"start": v(-0.03, -15.74) * mm, "end": v(-0.11, -15.92) * mm});
            skLineSegment(sketch, "E3121", {"start": v(-0.11, -15.92) * mm, "end": v(-0.12, -15.93) * mm});
            skLineSegment(sketch, "E3122", {"start": v(-0.12, -15.93) * mm, "end": v(-0.15, -16) * mm});
            skLineSegment(sketch, "E3123", {"start": v(-0.15, -16) * mm, "end": v(-0.3, -16.28) * mm});
            skLineSegment(sketch, "E3124", {"start": v(-0.3, -16.28) * mm, "end": v(-0.34, -16.33) * mm});
            skLineSegment(sketch, "E3125", {"start": v(-0.34, -16.33) * mm, "end": v(-0.4, -16.38) * mm});
            skLineSegment(sketch, "E3126", {"start": v(-0.4, -16.38) * mm, "end": v(-0.66, -16.39) * mm});
            skLineSegment(sketch, "E3127", {"start": v(-0.66, -16.39) * mm, "end": v(-0.92, -16.36) * mm});
            skLineSegment(sketch, "E3128", {"start": v(-0.92, -16.36) * mm, "end": v(-0.98, -16.3) * mm});
            skLineSegment(sketch, "E3129", {"start": v(-0.98, -16.3) * mm, "end": v(-1, -16.25) * mm});
            skLineSegment(sketch, "E3130", {"start": v(-1, -16.25) * mm, "end": v(-1.13, -15.96) * mm});
            skLineSegment(sketch, "E3131", {"start": v(-1.13, -15.96) * mm, "end": v(-1.16, -15.9) * mm});
            skLineSegment(sketch, "E3132", {"start": v(-1.16, -15.9) * mm, "end": v(-1.17, -15.87) * mm});
            skLineSegment(sketch, "E3133", {"start": v(-1.17, -15.87) * mm, "end": v(-1.24, -15.7) * mm});
            skLineSegment(sketch, "E3134", {"start": v(-1.24, -15.7) * mm, "end": v(-1.24, -15.69) * mm});
            skLineSegment(sketch, "E3135", {"start": v(-1.24, -15.69) * mm, "end": v(-1.25, -15.66) * mm});
            skLineSegment(sketch, "E3136", {"start": v(-1.25, -15.66) * mm, "end": v(-1.32, -15.45) * mm});
            skLineSegment(sketch, "E3137", {"start": v(-1.32, -15.45) * mm, "end": v(-1.32, -15.43) * mm});
            skLineSegment(sketch, "E3138", {"start": v(-1.32, -15.43) * mm, "end": v(-1.37, -15.26) * mm});
            skLineSegment(sketch, "E3139", {"start": v(-1.37, -15.26) * mm, "end": v(-1.39, -15.2) * mm});
            skLineSegment(sketch, "E3140", {"start": v(-1.39, -15.2) * mm, "end": v(-1.41, -15.09) * mm});
            skLineSegment(sketch, "E3141", {"start": v(-1.41, -15.09) * mm, "end": v(-1.44, -14.98) * mm});
            skLineSegment(sketch, "E3142", {"start": v(-1.44, -14.98) * mm, "end": v(-1.46, -14.88) * mm});
            skLineSegment(sketch, "E3143", {"start": v(-1.46, -14.88) * mm, "end": v(-1.47, -14.83) * mm});
            skLineSegment(sketch, "E3144", {"start": v(-1.47, -14.83) * mm, "end": v(-1.48, -14.8) * mm});
            skLineSegment(sketch, "E3145", {"start": v(-1.48, -14.8) * mm, "end": v(-1.5, -14.8) * mm});
            skLineSegment(sketch, "E3146", {"start": v(-1.5, -14.8) * mm, "end": v(-1.51, -14.78) * mm});
            skLineSegment(sketch, "E3147", {"start": v(-1.51, -14.78) * mm, "end": v(-2.07, -14.7) * mm});
            skLineSegment(sketch, "E3148", {"start": v(-2.07, -14.7) * mm, "end": v(-2.09, -14.72) * mm});
            skLineSegment(sketch, "E3149", {"start": v(-2.09, -14.72) * mm, "end": v(-2.1, -14.73) * mm});
            skLineSegment(sketch, "E3150", {"start": v(-2.1, -14.73) * mm, "end": v(-2.12, -14.75) * mm});
            skLineSegment(sketch, "E3151", {"start": v(-2.12, -14.75) * mm, "end": v(-2.15, -14.8) * mm});
            skLineSegment(sketch, "E3152", {"start": v(-2.15, -14.8) * mm, "end": v(-2.19, -14.89) * mm});
            skLineSegment(sketch, "E3153", {"start": v(-2.19, -14.89) * mm, "end": v(-2.24, -14.99) * mm});
            skLineSegment(sketch, "E3154", {"start": v(-2.24, -14.99) * mm, "end": v(-2.29, -15.08) * mm});
            skLineSegment(sketch, "E3155", {"start": v(-2.29, -15.08) * mm, "end": v(-2.32, -15.14) * mm});
            skLineSegment(sketch, "E3156", {"start": v(-2.32, -15.14) * mm, "end": v(-2.41, -15.3) * mm});
            skLineSegment(sketch, "E3157", {"start": v(-2.41, -15.3) * mm, "end": v(-2.42, -15.32) * mm});
            skLineSegment(sketch, "E3158", {"start": v(-2.42, -15.32) * mm, "end": v(-2.54, -15.5) * mm});
            skLineSegment(sketch, "E3159", {"start": v(-2.54, -15.5) * mm, "end": v(-2.55, -15.53) * mm});
            skLineSegment(sketch, "E3160", {"start": v(-2.55, -15.53) * mm, "end": v(-2.56, -15.53) * mm});
            skLineSegment(sketch, "E3161", {"start": v(-2.56, -15.53) * mm, "end": v(-2.67, -15.7) * mm});
            skLineSegment(sketch, "E3162", {"start": v(-2.67, -15.7) * mm, "end": v(-2.68, -15.7) * mm});
            skLineSegment(sketch, "E3163", {"start": v(-2.68, -15.7) * mm, "end": v(-2.72, -15.77) * mm});
            skLineSegment(sketch, "E3164", {"start": v(-2.72, -15.77) * mm, "end": v(-2.9, -16.02) * mm});
            skLineSegment(sketch, "E3165", {"start": v(-2.9, -16.02) * mm, "end": v(-2.95, -16.06) * mm});
            skLineSegment(sketch, "E3166", {"start": v(-2.95, -16.06) * mm, "end": v(-3.02, -16.1) * mm});
            skLineSegment(sketch, "E3167", {"start": v(-3.02, -16.1) * mm, "end": v(-3.28, -16.07) * mm});
            skLineSegment(sketch, "E3168", {"start": v(-3.28, -16.07) * mm, "end": v(-3.53, -16) * mm});
            skLineSegment(sketch, "E3169", {"start": v(-3.53, -16) * mm, "end": v(-3.58, -15.94) * mm});
            skLineSegment(sketch, "E3170", {"start": v(-3.58, -15.94) * mm, "end": v(-3.6, -15.88) * mm});
            skLineSegment(sketch, "E3171", {"start": v(-3.6, -15.88) * mm, "end": v(-3.68, -15.57) * mm});
            skLineSegment(sketch, "E3172", {"start": v(-3.68, -15.57) * mm, "end": v(-3.7, -15.5) * mm});
            skLineSegment(sketch, "E3173", {"start": v(-3.7, -15.5) * mm, "end": v(-3.7, -15.48) * mm});
            skLineSegment(sketch, "E3174", {"start": v(-3.7, -15.48) * mm, "end": v(-3.74, -15.29) * mm});
            skLineSegment(sketch, "E3175", {"start": v(-3.74, -15.29) * mm, "end": v(-3.74, -15.28) * mm});
            skLineSegment(sketch, "E3176", {"start": v(-3.74, -15.28) * mm, "end": v(-3.74, -15.26) * mm});
            skLineSegment(sketch, "E3177", {"start": v(-3.74, -15.26) * mm, "end": v(-3.78, -15.04) * mm});
            skLineSegment(sketch, "E3178", {"start": v(-3.78, -15.04) * mm, "end": v(-3.78, -15.02) * mm});
            skLineSegment(sketch, "E3179", {"start": v(-3.78, -15.02) * mm, "end": v(-3.8, -14.84) * mm});
            skLineSegment(sketch, "E3180", {"start": v(-3.8, -14.84) * mm, "end": v(-3.8, -14.77) * mm});
            skLineSegment(sketch, "E3181", {"start": v(-3.8, -14.77) * mm, "end": v(-3.82, -14.67) * mm});
            skLineSegment(sketch, "E3182", {"start": v(-3.82, -14.67) * mm, "end": v(-3.82, -14.55) * mm});
            skLineSegment(sketch, "E3183", {"start": v(-3.82, -14.55) * mm, "end": v(-3.83, -14.45) * mm});
            skLineSegment(sketch, "E3184", {"start": v(-3.83, -14.45) * mm, "end": v(-3.83, -14.4) * mm});
            skLineSegment(sketch, "E3185", {"start": v(-3.83, -14.4) * mm, "end": v(-3.84, -14.37) * mm});
            skLineSegment(sketch, "E3186", {"start": v(-3.84, -14.37) * mm, "end": v(-3.85, -14.36) * mm});
            skLineSegment(sketch, "E3187", {"start": v(-3.85, -14.36) * mm, "end": v(-3.86, -14.34) * mm});
            skLineSegment(sketch, "E3188", {"start": v(-3.86, -14.34) * mm, "end": v(-4.4, -14.19) * mm});
            skLineSegment(sketch, "E3189", {"start": v(-4.4, -14.19) * mm, "end": v(-4.42, -14.2) * mm});
            skLineSegment(sketch, "E3190", {"start": v(-4.42, -14.2) * mm, "end": v(-4.44, -14.2) * mm});
            skLineSegment(sketch, "E3191", {"start": v(-4.44, -14.2) * mm, "end": v(-4.46, -14.22) * mm});
            skLineSegment(sketch, "E3192", {"start": v(-4.46, -14.22) * mm, "end": v(-4.5, -14.26) * mm});
            skLineSegment(sketch, "E3193", {"start": v(-4.5, -14.26) * mm, "end": v(-4.55, -14.34) * mm});
            skLineSegment(sketch, "E3194", {"start": v(-4.55, -14.34) * mm, "end": v(-4.61, -14.44) * mm});
            skLineSegment(sketch, "E3195", {"start": v(-4.61, -14.44) * mm, "end": v(-4.68, -14.52) * mm});
            skLineSegment(sketch, "E3196", {"start": v(-4.68, -14.52) * mm, "end": v(-4.72, -14.58) * mm});
            skLineSegment(sketch, "E3197", {"start": v(-4.72, -14.58) * mm, "end": v(-4.83, -14.71) * mm});
            skLineSegment(sketch, "E3198", {"start": v(-4.83, -14.71) * mm, "end": v(-4.85, -14.73) * mm});
            skLineSegment(sketch, "E3199", {"start": v(-4.85, -14.73) * mm, "end": v(-5, -14.9) * mm});
            skLineSegment(sketch, "E3200", {"start": v(-5, -14.9) * mm, "end": v(-5.01, -14.92) * mm});
            skLineSegment(sketch, "E3201", {"start": v(-5.01, -14.92) * mm, "end": v(-5.01, -14.92) * mm});
            skLineSegment(sketch, "E3202", {"start": v(-5.01, -14.92) * mm, "end": v(-5.15, -15.06) * mm});
            skLineSegment(sketch, "E3203", {"start": v(-5.15, -15.06) * mm, "end": v(-5.16, -15.08) * mm});
            skLineSegment(sketch, "E3204", {"start": v(-5.16, -15.08) * mm, "end": v(-5.21, -15.13) * mm});
            skLineSegment(sketch, "E3205", {"start": v(-5.21, -15.13) * mm, "end": v(-5.44, -15.35) * mm});
            skLineSegment(sketch, "E3206", {"start": v(-5.44, -15.35) * mm, "end": v(-5.5, -15.38) * mm});
            skLineSegment(sketch, "E3207", {"start": v(-5.5, -15.38) * mm, "end": v(-5.56, -15.4) * mm});
            skLineSegment(sketch, "E3208", {"start": v(-5.56, -15.4) * mm, "end": v(-5.82, -15.33) * mm});
            skLineSegment(sketch, "E3209", {"start": v(-5.82, -15.33) * mm, "end": v(-6.05, -15.22) * mm});
            skLineSegment(sketch, "E3210", {"start": v(-6.05, -15.22) * mm, "end": v(-6.1, -15.15) * mm});
            skLineSegment(sketch, "E3211", {"start": v(-6.1, -15.15) * mm, "end": v(-6.1, -15.1) * mm});
            skLineSegment(sketch, "E3212", {"start": v(-6.1, -15.1) * mm, "end": v(-6.13, -14.78) * mm});
            skLineSegment(sketch, "E3213", {"start": v(-6.13, -14.78) * mm, "end": v(-6.13, -14.7) * mm});
            skLineSegment(sketch, "E3214", {"start": v(-6.13, -14.7) * mm, "end": v(-6.13, -14.69) * mm});
            skLineSegment(sketch, "E3215", {"start": v(-6.13, -14.69) * mm, "end": v(-6.14, -14.5) * mm});
            skLineSegment(sketch, "E3216", {"start": v(-6.14, -14.5) * mm, "end": v(-6.14, -14.49) * mm});
            skLineSegment(sketch, "E3217", {"start": v(-6.14, -14.49) * mm, "end": v(-6.14, -14.46) * mm});
            skLineSegment(sketch, "E3218", {"start": v(-6.14, -14.46) * mm, "end": v(-6.14, -14.24) * mm});
            skLineSegment(sketch, "E3219", {"start": v(-6.14, -14.24) * mm, "end": v(-6.14, -14.22) * mm});
            skLineSegment(sketch, "E3220", {"start": v(-6.14, -14.22) * mm, "end": v(-6.13, -14.04) * mm});
            skLineSegment(sketch, "E3221", {"start": v(-6.13, -14.04) * mm, "end": v(-6.13, -13.97) * mm});
            skLineSegment(sketch, "E3222", {"start": v(-6.13, -13.97) * mm, "end": v(-6.12, -13.87) * mm});
            skLineSegment(sketch, "E3223", {"start": v(-6.12, -13.87) * mm, "end": v(-6.1, -13.75) * mm});
            skLineSegment(sketch, "E3224", {"start": v(-6.1, -13.75) * mm, "end": v(-6.1, -13.65) * mm});
            skLineSegment(sketch, "E3225", {"start": v(-6.1, -13.65) * mm, "end": v(-6.1, -13.6) * mm});
            skLineSegment(sketch, "E3226", {"start": v(-6.1, -13.6) * mm, "end": v(-6.1, -13.57) * mm});
            skLineSegment(sketch, "E3227", {"start": v(-6.1, -13.57) * mm, "end": v(-6.1, -13.56) * mm});
            skLineSegment(sketch, "E3228", {"start": v(-6.1, -13.56) * mm, "end": v(-6.11, -13.54) * mm});
            skLineSegment(sketch, "E3229", {"start": v(-6.11, -13.54) * mm, "end": v(-6.62, -13.3) * mm});
            skLineSegment(sketch, "E3230", {"start": v(-6.62, -13.3) * mm, "end": v(-6.64, -13.3) * mm});
            skLineSegment(sketch, "E3231", {"start": v(-6.64, -13.3) * mm, "end": v(-6.66, -13.3) * mm});
            skLineSegment(sketch, "E3232", {"start": v(-6.66, -13.3) * mm, "end": v(-6.68, -13.32) * mm});
            skLineSegment(sketch, "E3233", {"start": v(-6.68, -13.32) * mm, "end": v(-6.72, -13.35) * mm});
            skLineSegment(sketch, "E3234", {"start": v(-6.72, -13.35) * mm, "end": v(-6.8, -13.43) * mm});
            skLineSegment(sketch, "E3235", {"start": v(-6.8, -13.43) * mm, "end": v(-6.87, -13.5) * mm});
            skLineSegment(sketch, "E3236", {"start": v(-6.87, -13.5) * mm, "end": v(-6.95, -13.58) * mm});
            skLineSegment(sketch, "E3237", {"start": v(-6.95, -13.58) * mm, "end": v(-7, -13.63) * mm});
            skLineSegment(sketch, "E3238", {"start": v(-7, -13.63) * mm, "end": v(-7.13, -13.75) * mm});
            skLineSegment(sketch, "E3239", {"start": v(-7.13, -13.75) * mm, "end": v(-7.15, -13.76) * mm});
            skLineSegment(sketch, "E3240", {"start": v(-7.15, -13.76) * mm, "end": v(-7.32, -13.9) * mm});
            skLineSegment(sketch, "E3241", {"start": v(-7.32, -13.9) * mm, "end": v(-7.34, -13.92) * mm});
            skLineSegment(sketch, "E3242", {"start": v(-7.34, -13.92) * mm, "end": v(-7.34, -13.92) * mm});
            skLineSegment(sketch, "E3243", {"start": v(-7.34, -13.92) * mm, "end": v(-7.5, -14.04) * mm});
            skLineSegment(sketch, "E3244", {"start": v(-7.5, -14.04) * mm, "end": v(-7.51, -14.05) * mm});
            skLineSegment(sketch, "E3245", {"start": v(-7.51, -14.05) * mm, "end": v(-7.57, -14.1) * mm});
            skLineSegment(sketch, "E3246", {"start": v(-7.57, -14.1) * mm, "end": v(-7.83, -14.27) * mm});
            skLineSegment(sketch, "E3247", {"start": v(-7.83, -14.27) * mm, "end": v(-7.89, -14.3) * mm});
            skLineSegment(sketch, "E3248", {"start": v(-7.89, -14.3) * mm, "end": v(-7.96, -14.31) * mm});
            skLineSegment(sketch, "E3249", {"start": v(-7.96, -14.31) * mm, "end": v(-8.2, -14.2) * mm});
            skLineSegment(sketch, "E3250", {"start": v(-8.2, -14.2) * mm, "end": v(-8.41, -14.05) * mm});
            skLineSegment(sketch, "E3251", {"start": v(-8.41, -14.05) * mm, "end": v(-8.44, -13.98) * mm});
            skLineSegment(sketch, "E3252", {"start": v(-8.44, -13.98) * mm, "end": v(-8.45, -13.92) * mm});
            skLineSegment(sketch, "E3253", {"start": v(-8.45, -13.92) * mm, "end": v(-8.42, -13.6) * mm});
            skLineSegment(sketch, "E3254", {"start": v(-8.42, -13.6) * mm, "end": v(-8.41, -13.53) * mm});
            skLineSegment(sketch, "E3255", {"start": v(-8.41, -13.53) * mm, "end": v(-8.4, -13.51) * mm});
            skLineSegment(sketch, "E3256", {"start": v(-8.4, -13.51) * mm, "end": v(-8.39, -13.32) * mm});
            skLineSegment(sketch, "E3257", {"start": v(-8.39, -13.32) * mm, "end": v(-8.39, -13.31) * mm});
            skLineSegment(sketch, "E3258", {"start": v(-8.39, -13.31) * mm, "end": v(-8.38, -13.29) * mm});
            skLineSegment(sketch, "E3259", {"start": v(-8.38, -13.29) * mm, "end": v(-8.34, -13.07) * mm});
            skLineSegment(sketch, "E3260", {"start": v(-8.34, -13.07) * mm, "end": v(-8.34, -13.05) * mm});
            skLineSegment(sketch, "E3261", {"start": v(-8.34, -13.05) * mm, "end": v(-8.3, -12.88) * mm});
            skLineSegment(sketch, "E3262", {"start": v(-8.3, -12.88) * mm, "end": v(-8.29, -12.8) * mm});
            skLineSegment(sketch, "E3263", {"start": v(-8.29, -12.8) * mm, "end": v(-8.26, -12.7) * mm});
            skLineSegment(sketch, "E3264", {"start": v(-8.26, -12.7) * mm, "end": v(-8.23, -12.6) * mm});
            skLineSegment(sketch, "E3265", {"start": v(-8.23, -12.6) * mm, "end": v(-8.2, -12.5) * mm});
            skLineSegment(sketch, "E3266", {"start": v(-8.2, -12.5) * mm, "end": v(-8.2, -12.45) * mm});
            skLineSegment(sketch, "E3267", {"start": v(-8.2, -12.45) * mm, "end": v(-8.2, -12.42) * mm});
            skLineSegment(sketch, "E3268", {"start": v(-8.2, -12.42) * mm, "end": v(-8.2, -12.4) * mm});
            skLineSegment(sketch, "E3269", {"start": v(-8.2, -12.4) * mm, "end": v(-8.2, -12.38) * mm});
            skLineSegment(sketch, "E3270", {"start": v(-8.2, -12.38) * mm, "end": v(-8.67, -12.06) * mm});
            skLineSegment(sketch, "E3271", {"start": v(-8.67, -12.06) * mm, "end": v(-8.69, -12.06) * mm});
            skLineSegment(sketch, "E3272", {"start": v(-8.69, -12.06) * mm, "end": v(-8.7, -12.07) * mm});
            skLineSegment(sketch, "E3273", {"start": v(-8.7, -12.07) * mm, "end": v(-8.73, -12.08) * mm});
            skLineSegment(sketch, "E3274", {"start": v(-8.73, -12.08) * mm, "end": v(-8.78, -12.1) * mm});
            skLineSegment(sketch, "E3275", {"start": v(-8.78, -12.1) * mm, "end": v(-8.86, -12.16) * mm});
            skLineSegment(sketch, "E3276", {"start": v(-8.86, -12.16) * mm, "end": v(-8.95, -12.23) * mm});
            skLineSegment(sketch, "E3277", {"start": v(-8.95, -12.23) * mm, "end": v(-9.04, -12.3) * mm});
            skLineSegment(sketch, "E3278", {"start": v(-9.04, -12.3) * mm, "end": v(-9.1, -12.33) * mm});
            skLineSegment(sketch, "E3279", {"start": v(-9.1, -12.33) * mm, "end": v(-9.24, -12.43) * mm});
            skLineSegment(sketch, "E3280", {"start": v(-9.24, -12.43) * mm, "end": v(-9.26, -12.44) * mm});
            skLineSegment(sketch, "E3281", {"start": v(-9.26, -12.44) * mm, "end": v(-9.45, -12.55) * mm});
            skLineSegment(sketch, "E3282", {"start": v(-9.45, -12.55) * mm, "end": v(-9.48, -12.56) * mm});
            skLineSegment(sketch, "E3283", {"start": v(-9.48, -12.56) * mm, "end": v(-9.48, -12.56) * mm});
            skLineSegment(sketch, "E3284", {"start": v(-9.48, -12.56) * mm, "end": v(-9.65, -12.65) * mm});
            skLineSegment(sketch, "E3285", {"start": v(-9.65, -12.65) * mm, "end": v(-9.67, -12.67) * mm});
            skLineSegment(sketch, "E3286", {"start": v(-9.67, -12.67) * mm, "end": v(-9.73, -12.7) * mm});
            skLineSegment(sketch, "E3287", {"start": v(-9.73, -12.7) * mm, "end": v(-10.02, -12.83) * mm});
            skLineSegment(sketch, "E3288", {"start": v(-10.02, -12.83) * mm, "end": v(-10.08, -12.85) * mm});
            skLineSegment(sketch, "E3289", {"start": v(-10.08, -12.85) * mm, "end": v(-10.16, -12.85) * mm});
            skLineSegment(sketch, "E3290", {"start": v(-10.16, -12.85) * mm, "end": v(-10.37, -12.7) * mm});
            skLineSegment(sketch, "E3291", {"start": v(-10.37, -12.7) * mm, "end": v(-10.56, -12.52) * mm});
            skLineSegment(sketch, "E3292", {"start": v(-10.56, -12.52) * mm, "end": v(-10.58, -12.45) * mm});
            skLineSegment(sketch, "E3293", {"start": v(-10.58, -12.45) * mm, "end": v(-10.57, -12.38) * mm});
            skLineSegment(sketch, "E3294", {"start": v(-10.57, -12.38) * mm, "end": v(-10.5, -12.08) * mm});
            skLineSegment(sketch, "E3295", {"start": v(-10.5, -12.08) * mm, "end": v(-10.48, -12) * mm});
            skLineSegment(sketch, "E3296", {"start": v(-10.48, -12) * mm, "end": v(-10.47, -11.99) * mm});
            skLineSegment(sketch, "E3297", {"start": v(-10.47, -11.99) * mm, "end": v(-10.41, -11.8) * mm});
            skLineSegment(sketch, "E3298", {"start": v(-10.41, -11.8) * mm, "end": v(-10.41, -11.8) * mm});
            skLineSegment(sketch, "E3299", {"start": v(-10.41, -11.8) * mm, "end": v(-10.4, -11.77) * mm});
            skLineSegment(sketch, "E3300", {"start": v(-10.4, -11.77) * mm, "end": v(-10.33, -11.56) * mm});
            skLineSegment(sketch, "E3301", {"start": v(-10.33, -11.56) * mm, "end": v(-10.33, -11.54) * mm});
            skLineSegment(sketch, "E3302", {"start": v(-10.33, -11.54) * mm, "end": v(-10.26, -11.38) * mm});
            skLineSegment(sketch, "E3303", {"start": v(-10.26, -11.38) * mm, "end": v(-10.24, -11.31) * mm});
            skLineSegment(sketch, "E3304", {"start": v(-10.24, -11.31) * mm, "end": v(-10.2, -11.21) * mm});
            skLineSegment(sketch, "E3305", {"start": v(-10.2, -11.21) * mm, "end": v(-10.15, -11.11) * mm});
            skLineSegment(sketch, "E3306", {"start": v(-10.15, -11.11) * mm, "end": v(-10.1, -11.02) * mm});
            skLineSegment(sketch, "E3307", {"start": v(-10.1, -11.02) * mm, "end": v(-10.09, -10.97) * mm});
            skLineSegment(sketch, "E3308", {"start": v(-10.09, -10.97) * mm, "end": v(-10.08, -10.94) * mm});
            skLineSegment(sketch, "E3309", {"start": v(-10.08, -10.94) * mm, "end": v(-10.08, -10.92) * mm});
            skLineSegment(sketch, "E3310", {"start": v(-10.08, -10.92) * mm, "end": v(-10.08, -10.9) * mm});
            skLineSegment(sketch, "E3311", {"start": v(-10.08, -10.9) * mm, "end": v(-10.5, -10.52) * mm});
            skLineSegment(sketch, "E3312", {"start": v(-10.5, -10.52) * mm, "end": v(-10.51, -10.51) * mm});
            skLineSegment(sketch, "E3313", {"start": v(-10.51, -10.51) * mm, "end": v(-10.53, -10.51) * mm});
            skLineSegment(sketch, "E3314", {"start": v(-10.53, -10.51) * mm, "end": v(-10.56, -10.52) * mm});
            skLineSegment(sketch, "E3315", {"start": v(-10.56, -10.52) * mm, "end": v(-10.6, -10.54) * mm});
            skLineSegment(sketch, "E3316", {"start": v(-10.6, -10.54) * mm, "end": v(-10.7, -10.59) * mm});
            skLineSegment(sketch, "E3317", {"start": v(-10.7, -10.59) * mm, "end": v(-10.8, -10.64) * mm});
            skLineSegment(sketch, "E3318", {"start": v(-10.8, -10.64) * mm, "end": v(-10.9, -10.68) * mm});
            skLineSegment(sketch, "E3319", {"start": v(-10.9, -10.68) * mm, "end": v(-10.95, -10.71) * mm});
            skLineSegment(sketch, "E3320", {"start": v(-10.95, -10.71) * mm, "end": v(-11.12, -10.78) * mm});
            skLineSegment(sketch, "E3321", {"start": v(-11.12, -10.78) * mm, "end": v(-11.14, -10.8) * mm});
            skLineSegment(sketch, "E3322", {"start": v(-11.14, -10.8) * mm, "end": v(-11.34, -10.87) * mm});
            skLineSegment(sketch, "E3323", {"start": v(-11.34, -10.87) * mm, "end": v(-11.37, -10.88) * mm});
            skLineSegment(sketch, "E3324", {"start": v(-11.37, -10.88) * mm, "end": v(-11.37, -10.88) * mm});
            skLineSegment(sketch, "E3325", {"start": v(-11.37, -10.88) * mm, "end": v(-11.56, -10.94) * mm});
            skLineSegment(sketch, "E3326", {"start": v(-11.56, -10.94) * mm, "end": v(-11.58, -10.95) * mm});
            skLineSegment(sketch, "E3327", {"start": v(-11.58, -10.95) * mm, "end": v(-11.65, -10.97) * mm});
            skLineSegment(sketch, "E3328", {"start": v(-11.65, -10.97) * mm, "end": v(-11.95, -11.06) * mm});
            skLineSegment(sketch, "E3329", {"start": v(-11.95, -11.06) * mm, "end": v(-12.01, -11.07) * mm});
            skLineSegment(sketch, "E3330", {"start": v(-12.01, -11.07) * mm, "end": v(-12.09, -11.06) * mm});
            skLineSegment(sketch, "E3331", {"start": v(-12.09, -11.06) * mm, "end": v(-12.28, -10.88) * mm});
            skLineSegment(sketch, "E3332", {"start": v(-12.28, -10.88) * mm, "end": v(-12.43, -10.67) * mm});
            skLineSegment(sketch, "E3333", {"start": v(-12.43, -10.67) * mm, "end": v(-12.44, -10.59) * mm});
            skLineSegment(sketch, "E3334", {"start": v(-12.44, -10.59) * mm, "end": v(-12.42, -10.53) * mm});
            skLineSegment(sketch, "E3335", {"start": v(-12.42, -10.53) * mm, "end": v(-12.3, -10.24) * mm});
            skLineSegment(sketch, "E3336", {"start": v(-12.3, -10.24) * mm, "end": v(-12.27, -10.17) * mm});
            skLineSegment(sketch, "E3337", {"start": v(-12.27, -10.17) * mm, "end": v(-12.26, -10.15) * mm});
            skLineSegment(sketch, "E3338", {"start": v(-12.26, -10.15) * mm, "end": v(-12.17, -9.98) * mm});
            skLineSegment(sketch, "E3339", {"start": v(-12.17, -9.98) * mm, "end": v(-12.17, -9.97) * mm});
            skLineSegment(sketch, "E3340", {"start": v(-12.17, -9.97) * mm, "end": v(-12.16, -9.95) * mm});
            skLineSegment(sketch, "E3341", {"start": v(-12.16, -9.95) * mm, "end": v(-12.05, -9.75) * mm});
            skLineSegment(sketch, "E3342", {"start": v(-12.05, -9.75) * mm, "end": v(-12.04, -9.74) * mm});
            skLineSegment(sketch, "E3343", {"start": v(-12.04, -9.74) * mm, "end": v(-11.95, -9.58) * mm});
            skLineSegment(sketch, "E3344", {"start": v(-11.95, -9.58) * mm, "end": v(-11.92, -9.52) * mm});
            skLineSegment(sketch, "E3345", {"start": v(-11.92, -9.52) * mm, "end": v(-11.86, -9.43) * mm});
            skLineSegment(sketch, "E3346", {"start": v(-11.86, -9.43) * mm, "end": v(-11.8, -9.34) * mm});
            skLineSegment(sketch, "E3347", {"start": v(-11.8, -9.34) * mm, "end": v(-11.74, -9.26) * mm});
            skLineSegment(sketch, "E3348", {"start": v(-11.74, -9.26) * mm, "end": v(-11.72, -9.21) * mm});
            skLineSegment(sketch, "E3349", {"start": v(-11.72, -9.21) * mm, "end": v(-11.7, -9.18) * mm});
            skLineSegment(sketch, "E3350", {"start": v(-11.7, -9.18) * mm, "end": v(-11.7, -9.17) * mm});
            skLineSegment(sketch, "E3351", {"start": v(-11.7, -9.17) * mm, "end": v(-11.7, -9.15) * mm});
            skLineSegment(sketch, "E3352", {"start": v(-11.7, -9.15) * mm, "end": v(-12.04, -8.7) * mm});
            skLineSegment(sketch, "E3353", {"start": v(-12.04, -8.7) * mm, "end": v(-12.06, -8.7) * mm});
            skLineSegment(sketch, "E3354", {"start": v(-12.06, -8.7) * mm, "end": v(-12.08, -8.69) * mm});
            skLineSegment(sketch, "E3355", {"start": v(-12.08, -8.69) * mm, "end": v(-12.1, -8.7) * mm});
            skLineSegment(sketch, "E3356", {"start": v(-12.1, -8.7) * mm, "end": v(-12.16, -8.7) * mm});
            skLineSegment(sketch, "E3357", {"start": v(-12.16, -8.7) * mm, "end": v(-12.25, -8.73) * mm});
            skLineSegment(sketch, "E3358", {"start": v(-12.25, -8.73) * mm, "end": v(-12.36, -8.77) * mm});
            skLineSegment(sketch, "E3359", {"start": v(-12.36, -8.77) * mm, "end": v(-12.46, -8.8) * mm});
            skLineSegment(sketch, "E3360", {"start": v(-12.46, -8.8) * mm, "end": v(-12.53, -8.82) * mm});
            skLineSegment(sketch, "E3361", {"start": v(-12.53, -8.82) * mm, "end": v(-12.7, -8.86) * mm});
            skLineSegment(sketch, "E3362", {"start": v(-12.7, -8.86) * mm, "end": v(-12.72, -8.86) * mm});
            skLineSegment(sketch, "E3363", {"start": v(-12.72, -8.86) * mm, "end": v(-12.94, -8.91) * mm});
            skLineSegment(sketch, "E3364", {"start": v(-12.94, -8.91) * mm, "end": v(-12.97, -8.91) * mm});
            skLineSegment(sketch, "E3365", {"start": v(-12.97, -8.91) * mm, "end": v(-12.97, -8.92) * mm});
            skLineSegment(sketch, "E3366", {"start": v(-12.97, -8.92) * mm, "end": v(-13.16, -8.95) * mm});
            skLineSegment(sketch, "E3367", {"start": v(-13.16, -8.95) * mm, "end": v(-13.18, -8.95) * mm});
            skLineSegment(sketch, "E3368", {"start": v(-13.18, -8.95) * mm, "end": v(-13.25, -8.96) * mm});
            skLineSegment(sketch, "E3369", {"start": v(-13.25, -8.96) * mm, "end": v(-13.57, -9) * mm});
            skLineSegment(sketch, "E3370", {"start": v(-13.57, -9) * mm, "end": v(-13.63, -9) * mm});
            skLineSegment(sketch, "E3371", {"start": v(-13.63, -9) * mm, "end": v(-13.7, -8.97) * mm});
            skLineSegment(sketch, "E3372", {"start": v(-13.7, -8.97) * mm, "end": v(-13.86, -8.77) * mm});
            skLineSegment(sketch, "E3373", {"start": v(-13.86, -8.77) * mm, "end": v(-13.98, -8.53) * mm});
            skLineSegment(sketch, "E3374", {"start": v(-13.98, -8.53) * mm, "end": v(-13.97, -8.46) * mm});
            skLineSegment(sketch, "E3375", {"start": v(-13.97, -8.46) * mm, "end": v(-13.95, -8.4) * mm});
            skLineSegment(sketch, "E3376", {"start": v(-13.95, -8.4) * mm, "end": v(-13.78, -8.13) * mm});
            skLineSegment(sketch, "E3377", {"start": v(-13.78, -8.13) * mm, "end": v(-13.74, -8.07) * mm});
            skLineSegment(sketch, "E3378", {"start": v(-13.74, -8.07) * mm, "end": v(-13.73, -8.06) * mm});
            skLineSegment(sketch, "E3379", {"start": v(-13.73, -8.06) * mm, "end": v(-13.61, -7.9) * mm});
            skLineSegment(sketch, "E3380", {"start": v(-13.61, -7.9) * mm, "end": v(-13.61, -7.9) * mm});
            skLineSegment(sketch, "E3381", {"start": v(-13.61, -7.9) * mm, "end": v(-13.6, -7.87) * mm});
            skLineSegment(sketch, "E3382", {"start": v(-13.6, -7.87) * mm, "end": v(-13.46, -7.7) * mm});
            skLineSegment(sketch, "E3383", {"start": v(-13.46, -7.7) * mm, "end": v(-13.45, -7.68) * mm});
            skLineSegment(sketch, "E3384", {"start": v(-13.45, -7.68) * mm, "end": v(-13.34, -7.54) * mm});
            skLineSegment(sketch, "E3385", {"start": v(-13.34, -7.54) * mm, "end": v(-13.3, -7.49) * mm});
            skLineSegment(sketch, "E3386", {"start": v(-13.3, -7.49) * mm, "end": v(-13.22, -7.4) * mm});
            skLineSegment(sketch, "E3387", {"start": v(-13.22, -7.4) * mm, "end": v(-13.14, -7.33) * mm});
            skLineSegment(sketch, "E3388", {"start": v(-13.14, -7.33) * mm, "end": v(-13.07, -7.25) * mm});
            skLineSegment(sketch, "E3389", {"start": v(-13.07, -7.25) * mm, "end": v(-13.04, -7.21) * mm});
            skLineSegment(sketch, "E3390", {"start": v(-13.04, -7.21) * mm, "end": v(-13.03, -7.19) * mm});
            skLineSegment(sketch, "E3391", {"start": v(-13.03, -7.19) * mm, "end": v(-13.02, -7.17) * mm});
            skLineSegment(sketch, "E3392", {"start": v(-13.02, -7.17) * mm, "end": v(-13.02, -7.15) * mm});
            skLineSegment(sketch, "E3393", {"start": v(-13.02, -7.15) * mm, "end": v(-13.28, -6.65) * mm});
            skLineSegment(sketch, "E3394", {"start": v(-13.28, -6.65) * mm, "end": v(-13.3, -6.64) * mm});
            skLineSegment(sketch, "E3395", {"start": v(-13.3, -6.64) * mm, "end": v(-13.32, -6.64) * mm});
            skLineSegment(sketch, "E3396", {"start": v(-13.32, -6.64) * mm, "end": v(-13.34, -6.64) * mm});
            skLineSegment(sketch, "E3397", {"start": v(-13.34, -6.64) * mm, "end": v(-13.4, -6.64) * mm});
            skLineSegment(sketch, "E3398", {"start": v(-13.4, -6.64) * mm, "end": v(-13.5, -6.66) * mm});
            skLineSegment(sketch, "E3399", {"start": v(-13.5, -6.66) * mm, "end": v(-13.6, -6.67) * mm});
            skLineSegment(sketch, "E3400", {"start": v(-13.6, -6.67) * mm, "end": v(-13.71, -6.69) * mm});
            skLineSegment(sketch, "E3401", {"start": v(-13.71, -6.69) * mm, "end": v(-13.78, -6.7) * mm});
            skLineSegment(sketch, "E3402", {"start": v(-13.78, -6.7) * mm, "end": v(-13.96, -6.7) * mm});
            skLineSegment(sketch, "E3403", {"start": v(-13.96, -6.7) * mm, "end": v(-13.98, -6.7) * mm});
            skLineSegment(sketch, "E3404", {"start": v(-13.98, -6.7) * mm, "end": v(-14.2, -6.72) * mm});
            skLineSegment(sketch, "E3405", {"start": v(-14.2, -6.72) * mm, "end": v(-14.23, -6.72) * mm});
            skLineSegment(sketch, "E3406", {"start": v(-14.23, -6.72) * mm, "end": v(-14.23, -6.72) * mm});
            skLineSegment(sketch, "E3407", {"start": v(-14.23, -6.72) * mm, "end": v(-14.43, -6.72) * mm});
            skLineSegment(sketch, "E3408", {"start": v(-14.43, -6.72) * mm, "end": v(-14.45, -6.72) * mm});
            skLineSegment(sketch, "E3409", {"start": v(-14.45, -6.72) * mm, "end": v(-14.52, -6.72) * mm});
            skLineSegment(sketch, "E3410", {"start": v(-14.52, -6.72) * mm, "end": v(-14.84, -6.7) * mm});
            skLineSegment(sketch, "E3411", {"start": v(-14.84, -6.7) * mm, "end": v(-14.9, -6.7) * mm});
            skLineSegment(sketch, "E3412", {"start": v(-14.9, -6.7) * mm, "end": v(-14.97, -6.66) * mm});
            skLineSegment(sketch, "E3413", {"start": v(-14.97, -6.66) * mm, "end": v(-15.09, -6.43) * mm});
            skLineSegment(sketch, "E3414", {"start": v(-15.09, -6.43) * mm, "end": v(-15.17, -6.18) * mm});
            skLineSegment(sketch, "E3415", {"start": v(-15.17, -6.18) * mm, "end": v(-15.15, -6.1) * mm});
            skLineSegment(sketch, "E3416", {"start": v(-15.15, -6.1) * mm, "end": v(-15.11, -6.05) * mm});
            skLineSegment(sketch, "E3417", {"start": v(-15.11, -6.05) * mm, "end": v(-14.9, -5.82) * mm});
            skLineSegment(sketch, "E3418", {"start": v(-14.9, -5.82) * mm, "end": v(-14.86, -5.76) * mm});
            skLineSegment(sketch, "E3419", {"start": v(-14.86, -5.76) * mm, "end": v(-14.84, -5.75) * mm});
            skLineSegment(sketch, "E3420", {"start": v(-14.84, -5.75) * mm, "end": v(-14.7, -5.61) * mm});
            skLineSegment(sketch, "E3421", {"start": v(-14.7, -5.61) * mm, "end": v(-14.7, -5.6) * mm});
            skLineSegment(sketch, "E3422", {"start": v(-14.7, -5.6) * mm, "end": v(-14.68, -5.59) * mm});
            skLineSegment(sketch, "E3423", {"start": v(-14.68, -5.59) * mm, "end": v(-14.52, -5.44) * mm});
            skLineSegment(sketch, "E3424", {"start": v(-14.52, -5.44) * mm, "end": v(-14.5, -5.42) * mm});
            skLineSegment(sketch, "E3425", {"start": v(-14.5, -5.42) * mm, "end": v(-14.37, -5.3) * mm});
            skLineSegment(sketch, "E3426", {"start": v(-14.37, -5.3) * mm, "end": v(-14.32, -5.26) * mm});
            skLineSegment(sketch, "E3427", {"start": v(-14.32, -5.26) * mm, "end": v(-14.24, -5.2) * mm});
            skLineSegment(sketch, "E3428", {"start": v(-14.24, -5.2) * mm, "end": v(-14.15, -5.12) * mm});
            skLineSegment(sketch, "E3429", {"start": v(-14.15, -5.12) * mm, "end": v(-14.07, -5.06) * mm});
            skLineSegment(sketch, "E3430", {"start": v(-14.07, -5.06) * mm, "end": v(-14.03, -5.03) * mm});
            skLineSegment(sketch, "E3431", {"start": v(-14.03, -5.03) * mm, "end": v(-14.01, -5) * mm});
            skLineSegment(sketch, "E3432", {"start": v(-14.01, -5) * mm, "end": v(-14, -4.99) * mm});
            skLineSegment(sketch, "E3433", {"start": v(-14, -4.99) * mm, "end": v(-14, -4.97) * mm});
            skLineSegment(sketch, "E3434", {"start": v(-14, -4.97) * mm, "end": v(-14.18, -4.44) * mm});
            skLineSegment(sketch, "E3435", {"start": v(-14.18, -4.44) * mm, "end": v(-14.2, -4.42) * mm});
            skLineSegment(sketch, "E3436", {"start": v(-14.2, -4.42) * mm, "end": v(-14.2, -4.42) * mm});
            skLineSegment(sketch, "E3437", {"start": v(-14.2, -4.42) * mm, "end": v(-14.24, -4.41) * mm});
            skLineSegment(sketch, "E3438", {"start": v(-14.24, -4.41) * mm, "end": v(-14.29, -4.4) * mm});
            skLineSegment(sketch, "E3439", {"start": v(-14.29, -4.4) * mm, "end": v(-14.39, -4.4) * mm});
            skLineSegment(sketch, "E3440", {"start": v(-14.39, -4.4) * mm, "end": v(-14.5, -4.4) * mm});
            skLineSegment(sketch, "E3441", {"start": v(-14.5, -4.4) * mm, "end": v(-14.6, -4.4) * mm});
            skLineSegment(sketch, "E3442", {"start": v(-14.6, -4.4) * mm, "end": v(-14.68, -4.4) * mm});
            skLineSegment(sketch, "E3443", {"start": v(-14.68, -4.4) * mm, "end": v(-14.85, -4.38) * mm});
            skLineSegment(sketch, "E3444", {"start": v(-14.85, -4.38) * mm, "end": v(-14.88, -4.38) * mm});
            skLineSegment(sketch, "E3445", {"start": v(-14.88, -4.38) * mm, "end": v(-15.1, -4.35) * mm});
            skLineSegment(sketch, "E3446", {"start": v(-15.1, -4.35) * mm, "end": v(-15.12, -4.35) * mm});
            skLineSegment(sketch, "E3447", {"start": v(-15.12, -4.35) * mm, "end": v(-15.13, -4.35) * mm});
            skLineSegment(sketch, "E3448", {"start": v(-15.13, -4.35) * mm, "end": v(-15.32, -4.32) * mm});
            skLineSegment(sketch, "E3449", {"start": v(-15.32, -4.32) * mm, "end": v(-15.34, -4.32) * mm});
            skLineSegment(sketch, "E3450", {"start": v(-15.34, -4.32) * mm, "end": v(-15.41, -4.3) * mm});
            skLineSegment(sketch, "E3451", {"start": v(-15.41, -4.3) * mm, "end": v(-15.72, -4.24) * mm});
            skLineSegment(sketch, "E3452", {"start": v(-15.72, -4.24) * mm, "end": v(-15.78, -4.22) * mm});
            skLineSegment(sketch, "E3453", {"start": v(-15.78, -4.22) * mm, "end": v(-15.84, -4.17) * mm});
            skLineSegment(sketch, "E3454", {"start": v(-15.84, -4.17) * mm, "end": v(-15.92, -3.92) * mm});
            skLineSegment(sketch, "E3455", {"start": v(-15.92, -3.92) * mm, "end": v(-15.97, -3.67) * mm});
            skLineSegment(sketch, "E3456", {"start": v(-15.97, -3.67) * mm, "end": v(-15.93, -3.6) * mm});
            skLineSegment(sketch, "E3457", {"start": v(-15.93, -3.6) * mm, "end": v(-15.89, -3.55) * mm});
            skLineSegment(sketch, "E3458", {"start": v(-15.89, -3.55) * mm, "end": v(-15.65, -3.35) * mm});
            skLineSegment(sketch, "E3459", {"start": v(-15.65, -3.35) * mm, "end": v(-15.59, -3.3) * mm});
            skLineSegment(sketch, "E3460", {"start": v(-15.59, -3.3) * mm, "end": v(-15.57, -3.3) * mm});
            skLineSegment(sketch, "E3461", {"start": v(-15.57, -3.3) * mm, "end": v(-15.41, -3.18) * mm});
            skLineSegment(sketch, "E3462", {"start": v(-15.41, -3.18) * mm, "end": v(-15.41, -3.18) * mm});
            skLineSegment(sketch, "E3463", {"start": v(-15.41, -3.18) * mm, "end": v(-15.4, -3.16) * mm});
            skLineSegment(sketch, "E3464", {"start": v(-15.4, -3.16) * mm, "end": v(-15.2, -3.04) * mm});
            skLineSegment(sketch, "E3465", {"start": v(-15.2, -3.04) * mm, "end": v(-15.19, -3.02) * mm});
            skLineSegment(sketch, "E3466", {"start": v(-15.19, -3.02) * mm, "end": v(-15.04, -2.93) * mm});
            skLineSegment(sketch, "E3467", {"start": v(-15.04, -2.93) * mm, "end": v(-14.98, -2.9) * mm});
            skLineSegment(sketch, "E3468", {"start": v(-14.98, -2.9) * mm, "end": v(-14.89, -2.84) * mm});
            skLineSegment(sketch, "E3469", {"start": v(-14.89, -2.84) * mm, "end": v(-14.79, -2.79) * mm});
            skLineSegment(sketch, "E3470", {"start": v(-14.79, -2.79) * mm, "end": v(-14.7, -2.74) * mm});
            skLineSegment(sketch, "E3471", {"start": v(-14.7, -2.74) * mm, "end": v(-14.65, -2.71) * mm});
            skLineSegment(sketch, "E3472", {"start": v(-14.65, -2.71) * mm, "end": v(-14.63, -2.7) * mm});
            skLineSegment(sketch, "E3473", {"start": v(-14.63, -2.7) * mm, "end": v(-14.62, -2.68) * mm});
            skLineSegment(sketch, "E3474", {"start": v(-14.62, -2.68) * mm, "end": v(-14.61, -2.66) * mm});
            skLineSegment(sketch, "E3475", {"start": v(-14.61, -2.66) * mm, "end": v(-14.7, -2.1) * mm});
            skLineSegment(sketch, "E3476", {"start": v(-14.7, -2.1) * mm, "end": v(-14.72, -2.1) * mm});
            skLineSegment(sketch, "E3477", {"start": v(-14.72, -2.1) * mm, "end": v(-14.73, -2.08) * mm});
            skLineSegment(sketch, "E3478", {"start": v(-14.73, -2.08) * mm, "end": v(-14.76, -2.07) * mm});
            skLineSegment(sketch, "E3479", {"start": v(-14.76, -2.07) * mm, "end": v(-14.8, -2.06) * mm});
            skLineSegment(sketch, "E3480", {"start": v(-14.8, -2.06) * mm, "end": v(-14.9, -2.04) * mm});
            skLineSegment(sketch, "E3481", {"start": v(-14.9, -2.04) * mm, "end": v(-15.02, -2.02) * mm});
            skLineSegment(sketch, "E3482", {"start": v(-15.02, -2.02) * mm, "end": v(-15.13, -2) * mm});
            skLineSegment(sketch, "E3483", {"start": v(-15.13, -2) * mm, "end": v(-15.2, -1.98) * mm});
            skLineSegment(sketch, "E3484", {"start": v(-15.2, -1.98) * mm, "end": v(-15.37, -1.94) * mm});
            skLineSegment(sketch, "E3485", {"start": v(-15.37, -1.94) * mm, "end": v(-15.39, -1.94) * mm});
            skLineSegment(sketch, "E3486", {"start": v(-15.39, -1.94) * mm, "end": v(-15.6, -1.88) * mm});
            skLineSegment(sketch, "E3487", {"start": v(-15.6, -1.88) * mm, "end": v(-15.62, -1.87) * mm});
            skLineSegment(sketch, "E3488", {"start": v(-15.62, -1.87) * mm, "end": v(-15.63, -1.87) * mm});
            skLineSegment(sketch, "E3489", {"start": v(-15.63, -1.87) * mm, "end": v(-15.81, -1.8) * mm});
            skLineSegment(sketch, "E3490", {"start": v(-15.81, -1.8) * mm, "end": v(-15.83, -1.8) * mm});
            skLineSegment(sketch, "E3491", {"start": v(-15.83, -1.8) * mm, "end": v(-15.9, -1.78) * mm});
            skLineSegment(sketch, "E3492", {"start": v(-15.9, -1.78) * mm, "end": v(-16.2, -1.66) * mm});
            skLineSegment(sketch, "E3493", {"start": v(-16.2, -1.66) * mm, "end": v(-16.25, -1.63) * mm});
            skLineSegment(sketch, "E3494", {"start": v(-16.25, -1.63) * mm, "end": v(-16.3, -1.58) * mm});
            skLineSegment(sketch, "E3495", {"start": v(-16.3, -1.58) * mm, "end": v(-16.35, -1.32) * mm});
            skLineSegment(sketch, "E3496", {"start": v(-16.35, -1.32) * mm, "end": v(-16.35, -1.06) * mm});
            skLineSegment(sketch, "E3497", {"start": v(-16.35, -1.06) * mm, "end": v(-16.3, -1) * mm});
            skLineSegment(sketch, "E3498", {"start": v(-16.3, -1) * mm, "end": v(-16.25, -0.96) * mm});
            skLineSegment(sketch, "E3499", {"start": v(-16.25, -0.96) * mm, "end": v(-15.98, -0.8) * mm});
            skLineSegment(sketch, "E3500", {"start": v(-15.98, -0.8) * mm, "end": v(-15.92, -0.76) * mm});
            skLineSegment(sketch, "E3501", {"start": v(-15.92, -0.76) * mm, "end": v(-15.9, -0.76) * mm});
            skLineSegment(sketch, "E3502", {"start": v(-15.9, -0.76) * mm, "end": v(-15.72, -0.66) * mm});
            skLineSegment(sketch, "E3503", {"start": v(-15.72, -0.66) * mm, "end": v(-15.72, -0.66) * mm});
            skLineSegment(sketch, "E3504", {"start": v(-15.72, -0.66) * mm, "end": v(-15.7, -0.65) * mm});
            skLineSegment(sketch, "E3505", {"start": v(-15.7, -0.65) * mm, "end": v(-15.5, -0.56) * mm});
            skLineSegment(sketch, "E3506", {"start": v(-15.5, -0.56) * mm, "end": v(-15.48, -0.55) * mm});
            skLineSegment(sketch, "E3507", {"start": v(-15.48, -0.55) * mm, "end": v(-15.31, -0.48) * mm});
            skLineSegment(sketch, "E3508", {"start": v(-15.31, -0.48) * mm, "end": v(-15.25, -0.45) * mm});
            skLineSegment(sketch, "E3509", {"start": v(-15.25, -0.45) * mm, "end": v(-15.15, -0.42) * mm});
            skLineSegment(sketch, "E3510", {"start": v(-15.15, -0.42) * mm, "end": v(-15.04, -0.38) * mm});
            skLineSegment(sketch, "E3511", {"start": v(-15.04, -0.38) * mm, "end": v(-14.95, -0.35) * mm});
            skLineSegment(sketch, "E3512", {"start": v(-14.95, -0.35) * mm, "end": v(-14.9, -0.32) * mm});
            skLineSegment(sketch, "E3513", {"start": v(-14.9, -0.32) * mm, "end": v(-14.88, -0.31) * mm});
            skLineSegment(sketch, "E3514", {"start": v(-14.88, -0.31) * mm, "end": v(-14.86, -0.3) * mm});
            skLineSegment(sketch, "E3515", {"start": v(-14.86, -0.3) * mm, "end": v(-14.85, -0.28) * mm});
            skLineSegment(sketch, "E3516", {"start": v(-14.85, -0.28) * mm, "end": v(-14.85, 0.28) * mm});
            skLineSegment(sketch, "E3517", {"start": v(-14.85, 0.28) * mm, "end": v(-14.86, 0.3) * mm});
            skLineSegment(sketch, "E3518", {"start": v(-14.86, 0.3) * mm, "end": v(-14.88, 0.31) * mm});
            skLineSegment(sketch, "E3519", {"start": v(-14.88, 0.31) * mm, "end": v(-14.9, 0.32) * mm});
            skLineSegment(sketch, "E3520", {"start": v(-14.9, 0.32) * mm, "end": v(-14.95, 0.35) * mm});
            skLineSegment(sketch, "E3521", {"start": v(-14.95, 0.35) * mm, "end": v(-15.04, 0.38) * mm});
            skLineSegment(sketch, "E3522", {"start": v(-15.04, 0.38) * mm, "end": v(-15.15, 0.42) * mm});
            skLineSegment(sketch, "E3523", {"start": v(-15.15, 0.42) * mm, "end": v(-15.25, 0.45) * mm});
            skLineSegment(sketch, "E3524", {"start": v(-15.25, 0.45) * mm, "end": v(-15.31, 0.48) * mm});
            skLineSegment(sketch, "E3525", {"start": v(-15.31, 0.48) * mm, "end": v(-15.48, 0.55) * mm});
            skLineSegment(sketch, "E3526", {"start": v(-15.48, 0.55) * mm, "end": v(-15.5, 0.56) * mm});
            skLineSegment(sketch, "E3527", {"start": v(-15.5, 0.56) * mm, "end": v(-15.7, 0.65) * mm});
            skLineSegment(sketch, "E3528", {"start": v(-15.7, 0.65) * mm, "end": v(-15.72, 0.66) * mm});
            skLineSegment(sketch, "E3529", {"start": v(-15.72, 0.66) * mm, "end": v(-15.72, 0.66) * mm});
            skLineSegment(sketch, "E3530", {"start": v(-15.72, 0.66) * mm, "end": v(-15.9, 0.76) * mm});
            skLineSegment(sketch, "E3531", {"start": v(-15.9, 0.76) * mm, "end": v(-15.92, 0.76) * mm});
            skLineSegment(sketch, "E3532", {"start": v(-15.92, 0.76) * mm, "end": v(-15.98, 0.8) * mm});
            skLineSegment(sketch, "E3533", {"start": v(-15.98, 0.8) * mm, "end": v(-16.25, 0.96) * mm});
            skLineSegment(sketch, "E3534", {"start": v(-16.25, 0.96) * mm, "end": v(-16.3, 1) * mm});
            skLineSegment(sketch, "E3535", {"start": v(-16.3, 1) * mm, "end": v(-16.35, 1.06) * mm});
            skLineSegment(sketch, "E3536", {"start": v(-16.16, 1.62) * mm, "end": v(-16.23, 1.44) * mm});
            skLineSegment(sketch, "E3537", {"start": v(-16.23, 1.44) * mm, "end": v(-16.26, 1.25) * mm});
            skLineSegment(sketch, "E3538", {"start": v(-16.26, 1.25) * mm, "end": v(-16.2, 1.17) * mm});
            skLineSegment(sketch, "E3539", {"start": v(-16.2, 1.17) * mm, "end": v(-15.91, 0.9) * mm});
            skLineSegment(sketch, "E3540", {"start": v(-15.91, 0.9) * mm, "end": v(-15.66, 0.72) * mm});
            skLineSegment(sketch, "E3541", {"start": v(-15.66, 0.72) * mm, "end": v(-15.45, 0.6) * mm});
            skLineSegment(sketch, "E3542", {"start": v(-15.45, 0.6) * mm, "end": v(-15.3, 0.53) * mm});
            skLineSegment(sketch, "E3543", {"start": v(-15.3, 0.53) * mm, "end": v(-15.2, 0.5) * mm});
            skLineSegment(sketch, "E3544", {"start": v(-15.2, 0.5) * mm, "end": v(-15, 0.47) * mm});
            skLineSegment(sketch, "E3545", {"start": v(-15, 0.47) * mm, "end": v(-14.83, 0.4) * mm});
            skLineSegment(sketch, "E3546", {"start": v(-14.83, 0.4) * mm, "end": v(-14.75, 0.3) * mm});
            skLineSegment(sketch, "E3547", {"start": v(-14.75, 0.3) * mm, "end": v(-14.75, -0.3) * mm});
            skLineSegment(sketch, "E3548", {"start": v(-14.75, -0.3) * mm, "end": v(-14.83, -0.4) * mm});
            skLineSegment(sketch, "E3549", {"start": v(-14.83, -0.4) * mm, "end": v(-15, -0.47) * mm});
            skLineSegment(sketch, "E3550", {"start": v(-15, -0.47) * mm, "end": v(-15.2, -0.5) * mm});
            skLineSegment(sketch, "E3551", {"start": v(-15.2, -0.5) * mm, "end": v(-15.3, -0.53) * mm});
            skLineSegment(sketch, "E3552", {"start": v(-15.3, -0.53) * mm, "end": v(-15.45, -0.6) * mm});
            skLineSegment(sketch, "E3553", {"start": v(-15.45, -0.6) * mm, "end": v(-15.66, -0.72) * mm});
            skLineSegment(sketch, "E3554", {"start": v(-15.66, -0.72) * mm, "end": v(-15.91, -0.9) * mm});
            skLineSegment(sketch, "E3555", {"start": v(-15.91, -0.9) * mm, "end": v(-16.2, -1.17) * mm});
            skLineSegment(sketch, "E3556", {"start": v(-16.2, -1.17) * mm, "end": v(-16.26, -1.25) * mm});
            skLineSegment(sketch, "E3557", {"start": v(-16.26, -1.25) * mm, "end": v(-16.23, -1.44) * mm});
            skLineSegment(sketch, "E3558", {"start": v(-16.23, -1.44) * mm, "end": v(-16.16, -1.62) * mm});
            skLineSegment(sketch, "E3559", {"start": v(-16.16, -1.62) * mm, "end": v(-16.07, -1.66) * mm});
            skLineSegment(sketch, "E3560", {"start": v(-16.07, -1.66) * mm, "end": v(-15.7, -1.76) * mm});
            skLineSegment(sketch, "E3561", {"start": v(-15.7, -1.76) * mm, "end": v(-15.4, -1.81) * mm});
            skLineSegment(sketch, "E3562", {"start": v(-15.4, -1.81) * mm, "end": v(-15.15, -1.82) * mm});
            skLineSegment(sketch, "E3563", {"start": v(-15.15, -1.82) * mm, "end": v(-14.98, -1.8) * mm});
            skLineSegment(sketch, "E3564", {"start": v(-14.98, -1.8) * mm, "end": v(-14.88, -1.79) * mm});
            skLineSegment(sketch, "E3565", {"start": v(-14.88, -1.79) * mm, "end": v(-14.69, -1.72) * mm});
            skLineSegment(sketch, "E3566", {"start": v(-14.69, -1.72) * mm, "end": v(-14.5, -1.7) * mm});
            skLineSegment(sketch, "E3567", {"start": v(-14.5, -1.7) * mm, "end": v(-14.39, -1.76) * mm});
            skLineSegment(sketch, "E3568", {"start": v(-14.39, -1.76) * mm, "end": v(-14.11, -2.28) * mm});
            skLineSegment(sketch, "E3569", {"start": v(-14.11, -2.28) * mm, "end": v(-14.14, -2.4) * mm});
            skLineSegment(sketch, "E3570", {"start": v(-14.14, -2.4) * mm, "end": v(-14.25, -2.55) * mm});
            skLineSegment(sketch, "E3571", {"start": v(-14.25, -2.55) * mm, "end": v(-14.42, -2.67) * mm});
            skLineSegment(sketch, "E3572", {"start": v(-14.42, -2.67) * mm, "end": v(-14.5, -2.74) * mm});
            skLineSegment(sketch, "E3573", {"start": v(-14.5, -2.74) * mm, "end": v(-14.6, -2.88) * mm});
            skLineSegment(sketch, "E3574", {"start": v(-14.6, -2.88) * mm, "end": v(-14.73, -3.08) * mm});
            skLineSegment(sketch, "E3575", {"start": v(-14.73, -3.08) * mm, "end": v(-14.86, -3.36) * mm});
            skLineSegment(sketch, "E3576", {"start": v(-14.86, -3.36) * mm, "end": v(-14.99, -3.72) * mm});
            skLineSegment(sketch, "E3577", {"start": v(-14.99, -3.72) * mm, "end": v(-15, -3.83) * mm});
            skLineSegment(sketch, "E3578", {"start": v(-15, -3.83) * mm, "end": v(-14.9, -3.98) * mm});
            skLineSegment(sketch, "E3579", {"start": v(-14.9, -3.98) * mm, "end": v(-14.75, -4.11) * mm});
            skLineSegment(sketch, "E3580", {"start": v(-14.75, -4.11) * mm, "end": v(-14.65, -4.1) * mm});
            skLineSegment(sketch, "E3581", {"start": v(-14.65, -4.1) * mm, "end": v(-14.27, -4.03) * mm});
            skLineSegment(sketch, "E3582", {"start": v(-14.27, -4.03) * mm, "end": v(-13.98, -3.93) * mm});
            skLineSegment(sketch, "E3583", {"start": v(-13.98, -3.93) * mm, "end": v(-13.76, -3.82) * mm});
            skLineSegment(sketch, "E3584", {"start": v(-13.76, -3.82) * mm, "end": v(-13.62, -3.73) * mm});
            skLineSegment(sketch, "E3585", {"start": v(-13.62, -3.73) * mm, "end": v(-13.54, -3.67) * mm});
            skLineSegment(sketch, "E3586", {"start": v(-13.54, -3.67) * mm, "end": v(-13.4, -3.52) * mm});
            skLineSegment(sketch, "E3587", {"start": v(-13.4, -3.52) * mm, "end": v(-13.24, -3.42) * mm});
            skLineSegment(sketch, "E3588", {"start": v(-13.24, -3.42) * mm, "end": v(-13.11, -3.41) * mm});
            skLineSegment(sketch, "E3589", {"start": v(-13.11, -3.41) * mm, "end": v(-12.63, -3.75) * mm});
            skLineSegment(sketch, "E3590", {"start": v(-12.63, -3.75) * mm, "end": v(-12.6, -3.87) * mm});
            skLineSegment(sketch, "E3591", {"start": v(-12.6, -3.87) * mm, "end": v(-12.63, -4.05) * mm});
            skLineSegment(sketch, "E3592", {"start": v(-12.63, -4.05) * mm, "end": v(-12.71, -4.23) * mm});
            skLineSegment(sketch, "E3593", {"start": v(-12.71, -4.23) * mm, "end": v(-12.75, -4.33) * mm});
            skLineSegment(sketch, "E3594", {"start": v(-12.75, -4.33) * mm, "end": v(-12.78, -4.5) * mm});
            skLineSegment(sketch, "E3595", {"start": v(-12.78, -4.5) * mm, "end": v(-12.8, -4.74) * mm});
            skLineSegment(sketch, "E3596", {"start": v(-12.8, -4.74) * mm, "end": v(-12.8, -5.05) * mm});
            skLineSegment(sketch, "E3597", {"start": v(-12.8, -5.05) * mm, "end": v(-12.73, -5.43) * mm});
            skLineSegment(sketch, "E3598", {"start": v(-12.73, -5.43) * mm, "end": v(-12.7, -5.53) * mm});
            skLineSegment(sketch, "E3599", {"start": v(-12.7, -5.53) * mm, "end": v(-12.53, -5.61) * mm});
            skLineSegment(sketch, "E3600", {"start": v(-12.53, -5.61) * mm, "end": v(-12.34, -5.66) * mm});
            skLineSegment(sketch, "E3601", {"start": v(-12.34, -5.66) * mm, "end": v(-12.25, -5.6) * mm});
            skLineSegment(sketch, "E3602", {"start": v(-12.25, -5.6) * mm, "end": v(-11.96, -5.37) * mm});
            skLineSegment(sketch, "E3603", {"start": v(-11.96, -5.37) * mm, "end": v(-11.74, -5.14) * mm});
            skLineSegment(sketch, "E3604", {"start": v(-11.74, -5.14) * mm, "end": v(-11.6, -4.95) * mm});
            skLineSegment(sketch, "E3605", {"start": v(-11.6, -4.95) * mm, "end": v(-11.51, -4.8) * mm});
            skLineSegment(sketch, "E3606", {"start": v(-11.51, -4.8) * mm, "end": v(-11.47, -4.7) * mm});
            skLineSegment(sketch, "E3607", {"start": v(-11.47, -4.7) * mm, "end": v(-11.42, -4.5) * mm});
            skLineSegment(sketch, "E3608", {"start": v(-11.42, -4.5) * mm, "end": v(-11.33, -4.35) * mm});
            skLineSegment(sketch, "E3609", {"start": v(-11.33, -4.35) * mm, "end": v(-11.22, -4.28) * mm});
            skLineSegment(sketch, "E3610", {"start": v(-11.22, -4.28) * mm, "end": v(-10.63, -4.35) * mm});
            skLineSegment(sketch, "E3611", {"start": v(-10.63, -4.35) * mm, "end": v(-10.54, -4.44) * mm});
            skLineSegment(sketch, "E3612", {"start": v(-10.54, -4.44) * mm, "end": v(-10.49, -4.62) * mm});
            skLineSegment(sketch, "E3613", {"start": v(-10.49, -4.62) * mm, "end": v(-10.48, -4.82) * mm});
            skLineSegment(sketch, "E3614", {"start": v(-10.48, -4.82) * mm, "end": v(-10.47, -4.92) * mm});
            skLineSegment(sketch, "E3615", {"start": v(-10.47, -4.92) * mm, "end": v(-10.42, -5.09) * mm});
            skLineSegment(sketch, "E3616", {"start": v(-10.42, -5.09) * mm, "end": v(-10.32, -5.31) * mm});
            skLineSegment(sketch, "E3617", {"start": v(-10.32, -5.31) * mm, "end": v(-10.17, -5.58) * mm});
            skLineSegment(sketch, "E3618", {"start": v(-10.17, -5.58) * mm, "end": v(-9.94, -5.89) * mm});
            skLineSegment(sketch, "E3619", {"start": v(-9.94, -5.89) * mm, "end": v(-9.87, -5.96) * mm});
            skLineSegment(sketch, "E3620", {"start": v(-9.87, -5.96) * mm, "end": v(-9.68, -5.96) * mm});
            skLineSegment(sketch, "E3621", {"start": v(-9.68, -5.96) * mm, "end": v(-9.49, -5.92) * mm});
            skLineSegment(sketch, "E3622", {"start": v(-9.49, -5.92) * mm, "end": v(-9.44, -5.83) * mm});
            skLineSegment(sketch, "E3623", {"start": v(-9.44, -5.83) * mm, "end": v(-9.29, -5.48) * mm});
            skLineSegment(sketch, "E3624", {"start": v(-9.29, -5.48) * mm, "end": v(-9.2, -5.18) * mm});
            skLineSegment(sketch, "E3625", {"start": v(-9.2, -5.18) * mm, "end": v(-9.16, -4.94) * mm});
            skLineSegment(sketch, "E3626", {"start": v(-9.16, -4.94) * mm, "end": v(-9.16, -4.77) * mm});
            skLineSegment(sketch, "E3627", {"start": v(-9.16, -4.77) * mm, "end": v(-9.17, -4.66) * mm});
            skLineSegment(sketch, "E3628", {"start": v(-9.17, -4.66) * mm, "end": v(-9.2, -4.46) * mm});
            skLineSegment(sketch, "E3629", {"start": v(-9.2, -4.46) * mm, "end": v(-9.2, -4.28) * mm});
            skLineSegment(sketch, "E3630", {"start": v(-9.2, -4.28) * mm, "end": v(-9.14, -4.17) * mm});
            skLineSegment(sketch, "E3631", {"start": v(-9.14, -4.17) * mm, "end": v(-8.58, -3.96) * mm});
            skLineSegment(sketch, "E3632", {"start": v(-8.58, -3.96) * mm, "end": v(-8.46, -4) * mm});
            skLineSegment(sketch, "E3633", {"start": v(-8.46, -4) * mm, "end": v(-8.33, -4.13) * mm});
            skLineSegment(sketch, "E3634", {"start": v(-8.33, -4.13) * mm, "end": v(-8.23, -4.3) * mm});
            skLineSegment(sketch, "E3635", {"start": v(-8.23, -4.3) * mm, "end": v(-8.17, -4.4) * mm});
            skLineSegment(sketch, "E3636", {"start": v(-8.17, -4.4) * mm, "end": v(-8.05, -4.52) * mm});
            skLineSegment(sketch, "E3637", {"start": v(-8.05, -4.52) * mm, "end": v(-7.86, -4.67) * mm});
            skLineSegment(sketch, "E3638", {"start": v(-7.86, -4.67) * mm, "end": v(-7.6, -4.84) * mm});
            skLineSegment(sketch, "E3639", {"start": v(-7.6, -4.84) * mm, "end": v(-7.26, -5) * mm});
            skLineSegment(sketch, "E3640", {"start": v(-7.26, -5) * mm, "end": v(-7.16, -5.03) * mm});
            skLineSegment(sketch, "E3641", {"start": v(-7.16, -5.03) * mm, "end": v(-7, -4.94) * mm});
            skLineSegment(sketch, "E3642", {"start": v(-7, -4.94) * mm, "end": v(-6.84, -4.82) * mm});
            skLineSegment(sketch, "E3643", {"start": v(-6.84, -4.82) * mm, "end": v(-6.84, -4.71) * mm});
            skLineSegment(sketch, "E3644", {"start": v(-6.84, -4.71) * mm, "end": v(-6.87, -4.33) * mm});
            skLineSegment(sketch, "E3645", {"start": v(-6.87, -4.33) * mm, "end": v(-6.93, -4.03) * mm});
            skLineSegment(sketch, "E3646", {"start": v(-6.93, -4.03) * mm, "end": v(-7.01, -3.8) * mm});
            skLineSegment(sketch, "E3647", {"start": v(-7.01, -3.8) * mm, "end": v(-7.09, -3.64) * mm});
            skLineSegment(sketch, "E3648", {"start": v(-7.09, -3.64) * mm, "end": v(-7.14, -3.56) * mm});
            skLineSegment(sketch, "E3649", {"start": v(-7.14, -3.56) * mm, "end": v(-7.27, -3.4) * mm});
            skLineSegment(sketch, "E3650", {"start": v(-7.27, -3.4) * mm, "end": v(-7.35, -3.23) * mm});
            skLineSegment(sketch, "E3651", {"start": v(-7.35, -3.23) * mm, "end": v(-7.34, -3.1) * mm});
            skLineSegment(sketch, "E3652", {"start": v(-7.34, -3.1) * mm, "end": v(-6.95, -2.66) * mm});
            skLineSegment(sketch, "E3653", {"start": v(-6.95, -2.66) * mm, "end": v(-6.82, -2.64) * mm});
            skLineSegment(sketch, "E3654", {"start": v(-6.82, -2.64) * mm, "end": v(-6.65, -2.7) * mm});
            skLineSegment(sketch, "E3655", {"start": v(-6.65, -2.7) * mm, "end": v(-6.48, -2.8) * mm});
            skLineSegment(sketch, "E3656", {"start": v(-6.48, -2.8) * mm, "end": v(-6.38, -2.85) * mm});
            skLineSegment(sketch, "E3657", {"start": v(-6.38, -2.85) * mm, "end": v(-6.22, -2.9) * mm});
            skLineSegment(sketch, "E3658", {"start": v(-6.22, -2.9) * mm, "end": v(-5.99, -2.96) * mm});
            skLineSegment(sketch, "E3659", {"start": v(-5.99, -2.96) * mm, "end": v(-5.67, -2.98) * mm});
            skLineSegment(sketch, "E3660", {"start": v(-5.67, -2.98) * mm, "end": v(-5.3, -2.97) * mm});
            skLineSegment(sketch, "E3661", {"start": v(-5.3, -2.97) * mm, "end": v(-5.2, -2.95) * mm});
            skLineSegment(sketch, "E3662", {"start": v(-5.2, -2.95) * mm, "end": v(-5.09, -2.79) * mm});
            skLineSegment(sketch, "E3663", {"start": v(-5.09, -2.79) * mm, "end": v(-5.01, -2.61) * mm});
            skLineSegment(sketch, "E3664", {"start": v(-5.01, -2.61) * mm, "end": v(-5.06, -2.52) * mm});
            skLineSegment(sketch, "E3665", {"start": v(-5.06, -2.52) * mm, "end": v(-5.26, -2.2) * mm});
            skLineSegment(sketch, "E3666", {"start": v(-5.26, -2.2) * mm, "end": v(-5.46, -1.95) * mm});
            skLineSegment(sketch, "E3667", {"start": v(-5.46, -1.95) * mm, "end": v(-5.63, -1.79) * mm});
            skLineSegment(sketch, "E3668", {"start": v(-5.63, -1.79) * mm, "end": v(-5.77, -1.68) * mm});
            skLineSegment(sketch, "E3669", {"start": v(-5.77, -1.68) * mm, "end": v(-5.86, -1.63) * mm});
            skLineSegment(sketch, "E3670", {"start": v(-5.86, -1.63) * mm, "end": v(-6.05, -1.55) * mm});
            skLineSegment(sketch, "E3671", {"start": v(-6.05, -1.55) * mm, "end": v(-6.2, -1.44) * mm});
            skLineSegment(sketch, "E3672", {"start": v(-6.2, -1.44) * mm, "end": v(-6.25, -1.33) * mm});
            skLineSegment(sketch, "E3673", {"start": v(-6.25, -1.33) * mm, "end": v(-6.1, -0.75) * mm});
            skLineSegment(sketch, "E3674", {"start": v(-6.1, -0.75) * mm, "end": v(-6, -0.68) * mm});
            skLineSegment(sketch, "E3675", {"start": v(-6, -0.68) * mm, "end": v(-5.83, -0.65) * mm});
            skLineSegment(sketch, "E3676", {"start": v(-5.83, -0.65) * mm, "end": v(-5.62, -0.66) * mm});
            skLineSegment(sketch, "E3677", {"start": v(-5.62, -0.66) * mm, "end": v(-5.52, -0.66) * mm});
            skLineSegment(sketch, "E3678", {"start": v(-5.52, -0.66) * mm, "end": v(-5.35, -0.63) * mm});
            skLineSegment(sketch, "E3679", {"start": v(-5.35, -0.63) * mm, "end": v(-5.12, -0.57) * mm});
            skLineSegment(sketch, "E3680", {"start": v(-5.12, -0.57) * mm, "end": v(-4.83, -0.44) * mm});
            skLineSegment(sketch, "E3681", {"start": v(-4.83, -0.44) * mm, "end": v(-4.5, -0.25) * mm});
            skLineSegment(sketch, "E3682", {"start": v(-4.5, -0.25) * mm, "end": v(-4.42, -0.2) * mm});
            skLineSegment(sketch, "E3683", {"start": v(-4.42, -0.2) * mm, "end": v(-4.4, 0) * mm});
            skLineSegment(sketch, "E3684", {"start": v(-4.4, 0) * mm, "end": v(-4.42, 0.2) * mm});
            skLineSegment(sketch, "E3685", {"start": v(-4.42, 0.2) * mm, "end": v(-4.5, 0.25) * mm});
            skLineSegment(sketch, "E3686", {"start": v(-4.5, 0.25) * mm, "end": v(-4.83, 0.44) * mm});
            skLineSegment(sketch, "E3687", {"start": v(-4.83, 0.44) * mm, "end": v(-5.12, 0.57) * mm});
            skLineSegment(sketch, "E3688", {"start": v(-5.12, 0.57) * mm, "end": v(-5.35, 0.63) * mm});
            skLineSegment(sketch, "E3689", {"start": v(-5.35, 0.63) * mm, "end": v(-5.52, 0.66) * mm});
            skLineSegment(sketch, "E3690", {"start": v(-5.52, 0.66) * mm, "end": v(-5.62, 0.66) * mm});
            skLineSegment(sketch, "E3691", {"start": v(-5.62, 0.66) * mm, "end": v(-5.83, 0.65) * mm});
            skLineSegment(sketch, "E3692", {"start": v(-5.83, 0.65) * mm, "end": v(-6, 0.68) * mm});
            skLineSegment(sketch, "E3693", {"start": v(-6, 0.68) * mm, "end": v(-6.1, 0.75) * mm});
            skLineSegment(sketch, "E3694", {"start": v(-6.1, 0.75) * mm, "end": v(-6.25, 1.33) * mm});
            skLineSegment(sketch, "E3695", {"start": v(-6.25, 1.33) * mm, "end": v(-6.2, 1.44) * mm});
            skLineSegment(sketch, "E3696", {"start": v(-6.2, 1.44) * mm, "end": v(-6.05, 1.55) * mm});
            skLineSegment(sketch, "E3697", {"start": v(-6.05, 1.55) * mm, "end": v(-5.86, 1.63) * mm});
            skLineSegment(sketch, "E3698", {"start": v(-5.86, 1.63) * mm, "end": v(-5.77, 1.68) * mm});
            skLineSegment(sketch, "E3699", {"start": v(-5.77, 1.68) * mm, "end": v(-5.63, 1.79) * mm});
            skLineSegment(sketch, "E3700", {"start": v(-5.63, 1.79) * mm, "end": v(-5.46, 1.95) * mm});
            skLineSegment(sketch, "E3701", {"start": v(-5.46, 1.95) * mm, "end": v(-5.26, 2.2) * mm});
            skLineSegment(sketch, "E3702", {"start": v(-5.26, 2.2) * mm, "end": v(-5.06, 2.52) * mm});
            skLineSegment(sketch, "E3703", {"start": v(-5.06, 2.52) * mm, "end": v(-5.01, 2.61) * mm});
            skLineSegment(sketch, "E3704", {"start": v(-5.01, 2.61) * mm, "end": v(-5.09, 2.79) * mm});
            skLineSegment(sketch, "E3705", {"start": v(-5.09, 2.79) * mm, "end": v(-5.2, 2.95) * mm});
            skLineSegment(sketch, "E3706", {"start": v(-5.2, 2.95) * mm, "end": v(-5.3, 2.97) * mm});
            skLineSegment(sketch, "E3707", {"start": v(-5.3, 2.97) * mm, "end": v(-5.67, 2.98) * mm});
            skLineSegment(sketch, "E3708", {"start": v(-5.67, 2.98) * mm, "end": v(-5.99, 2.96) * mm});
            skLineSegment(sketch, "E3709", {"start": v(-5.99, 2.96) * mm, "end": v(-6.22, 2.9) * mm});
            skLineSegment(sketch, "E3710", {"start": v(-6.22, 2.9) * mm, "end": v(-6.38, 2.85) * mm});
            skLineSegment(sketch, "E3711", {"start": v(-6.38, 2.85) * mm, "end": v(-6.48, 2.8) * mm});
            skLineSegment(sketch, "E3712", {"start": v(-6.48, 2.8) * mm, "end": v(-6.65, 2.7) * mm});
            skLineSegment(sketch, "E3713", {"start": v(-6.65, 2.7) * mm, "end": v(-6.82, 2.64) * mm});
            skLineSegment(sketch, "E3714", {"start": v(-6.82, 2.64) * mm, "end": v(-6.95, 2.66) * mm});
            skLineSegment(sketch, "E3715", {"start": v(-6.95, 2.66) * mm, "end": v(-7.34, 3.1) * mm});
            skLineSegment(sketch, "E3716", {"start": v(-7.34, 3.1) * mm, "end": v(-7.35, 3.23) * mm});
            skLineSegment(sketch, "E3717", {"start": v(-7.35, 3.23) * mm, "end": v(-7.27, 3.4) * mm});
            skLineSegment(sketch, "E3718", {"start": v(-7.27, 3.4) * mm, "end": v(-7.14, 3.56) * mm});
            skLineSegment(sketch, "E3719", {"start": v(-7.14, 3.56) * mm, "end": v(-7.09, 3.64) * mm});
            skLineSegment(sketch, "E3720", {"start": v(-7.09, 3.64) * mm, "end": v(-7.01, 3.8) * mm});
            skLineSegment(sketch, "E3721", {"start": v(-7.01, 3.8) * mm, "end": v(-6.93, 4.03) * mm});
            skLineSegment(sketch, "E3722", {"start": v(-6.93, 4.03) * mm, "end": v(-6.87, 4.33) * mm});
            skLineSegment(sketch, "E3723", {"start": v(-6.87, 4.33) * mm, "end": v(-6.84, 4.71) * mm});
            skLineSegment(sketch, "E3724", {"start": v(-6.84, 4.71) * mm, "end": v(-6.84, 4.82) * mm});
            skLineSegment(sketch, "E3725", {"start": v(-6.84, 4.82) * mm, "end": v(-7, 4.94) * mm});
            skLineSegment(sketch, "E3726", {"start": v(-7, 4.94) * mm, "end": v(-7.16, 5.03) * mm});
            skLineSegment(sketch, "E3727", {"start": v(-7.16, 5.03) * mm, "end": v(-7.26, 5) * mm});
            skLineSegment(sketch, "E3728", {"start": v(-7.26, 5) * mm, "end": v(-7.6, 4.84) * mm});
            skLineSegment(sketch, "E3729", {"start": v(-7.6, 4.84) * mm, "end": v(-7.86, 4.67) * mm});
            skLineSegment(sketch, "E3730", {"start": v(-7.86, 4.67) * mm, "end": v(-8.05, 4.52) * mm});
            skLineSegment(sketch, "E3731", {"start": v(-8.05, 4.52) * mm, "end": v(-8.17, 4.4) * mm});
            skLineSegment(sketch, "E3732", {"start": v(-8.17, 4.4) * mm, "end": v(-8.23, 4.3) * mm});
            skLineSegment(sketch, "E3733", {"start": v(-8.23, 4.3) * mm, "end": v(-8.33, 4.13) * mm});
            skLineSegment(sketch, "E3734", {"start": v(-8.33, 4.13) * mm, "end": v(-8.46, 4) * mm});
            skLineSegment(sketch, "E3735", {"start": v(-8.46, 4) * mm, "end": v(-8.58, 3.96) * mm});
            skLineSegment(sketch, "E3736", {"start": v(-8.58, 3.96) * mm, "end": v(-9.14, 4.17) * mm});
            skLineSegment(sketch, "E3737", {"start": v(-9.14, 4.17) * mm, "end": v(-9.2, 4.28) * mm});
            skLineSegment(sketch, "E3738", {"start": v(-9.2, 4.28) * mm, "end": v(-9.2, 4.46) * mm});
            skLineSegment(sketch, "E3739", {"start": v(-9.2, 4.46) * mm, "end": v(-9.17, 4.66) * mm});
            skLineSegment(sketch, "E3740", {"start": v(-9.17, 4.66) * mm, "end": v(-9.16, 4.77) * mm});
            skLineSegment(sketch, "E3741", {"start": v(-9.16, 4.77) * mm, "end": v(-9.16, 4.94) * mm});
            skLineSegment(sketch, "E3742", {"start": v(-9.16, 4.94) * mm, "end": v(-9.2, 5.18) * mm});
            skLineSegment(sketch, "E3743", {"start": v(-9.2, 5.18) * mm, "end": v(-9.29, 5.48) * mm});
            skLineSegment(sketch, "E3744", {"start": v(-9.29, 5.48) * mm, "end": v(-9.44, 5.83) * mm});
            skLineSegment(sketch, "E3745", {"start": v(-9.44, 5.83) * mm, "end": v(-9.49, 5.92) * mm});
            skLineSegment(sketch, "E3746", {"start": v(-9.49, 5.92) * mm, "end": v(-9.68, 5.96) * mm});
            skLineSegment(sketch, "E3747", {"start": v(-9.68, 5.96) * mm, "end": v(-9.87, 5.96) * mm});
            skLineSegment(sketch, "E3748", {"start": v(-9.87, 5.96) * mm, "end": v(-9.94, 5.89) * mm});
            skLineSegment(sketch, "E3749", {"start": v(-9.94, 5.89) * mm, "end": v(-10.17, 5.58) * mm});
            skLineSegment(sketch, "E3750", {"start": v(-10.17, 5.58) * mm, "end": v(-10.32, 5.31) * mm});
            skLineSegment(sketch, "E3751", {"start": v(-10.32, 5.31) * mm, "end": v(-10.42, 5.09) * mm});
            skLineSegment(sketch, "E3752", {"start": v(-10.42, 5.09) * mm, "end": v(-10.47, 4.92) * mm});
            skLineSegment(sketch, "E3753", {"start": v(-10.47, 4.92) * mm, "end": v(-10.48, 4.82) * mm});
            skLineSegment(sketch, "E3754", {"start": v(-10.48, 4.82) * mm, "end": v(-10.49, 4.62) * mm});
            skLineSegment(sketch, "E3755", {"start": v(-10.49, 4.62) * mm, "end": v(-10.54, 4.44) * mm});
            skLineSegment(sketch, "E3756", {"start": v(-10.54, 4.44) * mm, "end": v(-10.63, 4.35) * mm});
            skLineSegment(sketch, "E3757", {"start": v(-10.63, 4.35) * mm, "end": v(-11.22, 4.28) * mm});
            skLineSegment(sketch, "E3758", {"start": v(-11.22, 4.28) * mm, "end": v(-11.33, 4.35) * mm});
            skLineSegment(sketch, "E3759", {"start": v(-11.33, 4.35) * mm, "end": v(-11.42, 4.5) * mm});
            skLineSegment(sketch, "E3760", {"start": v(-11.42, 4.5) * mm, "end": v(-11.47, 4.7) * mm});
            skLineSegment(sketch, "E3761", {"start": v(-11.47, 4.7) * mm, "end": v(-11.51, 4.8) * mm});
            skLineSegment(sketch, "E3762", {"start": v(-11.51, 4.8) * mm, "end": v(-11.6, 4.95) * mm});
            skLineSegment(sketch, "E3763", {"start": v(-11.6, 4.95) * mm, "end": v(-11.74, 5.14) * mm});
            skLineSegment(sketch, "E3764", {"start": v(-11.74, 5.14) * mm, "end": v(-11.96, 5.37) * mm});
            skLineSegment(sketch, "E3765", {"start": v(-11.96, 5.37) * mm, "end": v(-12.25, 5.6) * mm});
            skLineSegment(sketch, "E3766", {"start": v(-12.25, 5.6) * mm, "end": v(-12.34, 5.66) * mm});
            skLineSegment(sketch, "E3767", {"start": v(-12.34, 5.66) * mm, "end": v(-12.53, 5.61) * mm});
            skLineSegment(sketch, "E3768", {"start": v(-12.53, 5.61) * mm, "end": v(-12.7, 5.53) * mm});
            skLineSegment(sketch, "E3769", {"start": v(-12.7, 5.53) * mm, "end": v(-12.73, 5.43) * mm});
            skLineSegment(sketch, "E3770", {"start": v(-12.73, 5.43) * mm, "end": v(-12.8, 5.05) * mm});
            skLineSegment(sketch, "E3771", {"start": v(-12.8, 5.05) * mm, "end": v(-12.8, 4.74) * mm});
            skLineSegment(sketch, "E3772", {"start": v(-12.8, 4.74) * mm, "end": v(-12.78, 4.5) * mm});
            skLineSegment(sketch, "E3773", {"start": v(-12.78, 4.5) * mm, "end": v(-12.75, 4.33) * mm});
            skLineSegment(sketch, "E3774", {"start": v(-12.75, 4.33) * mm, "end": v(-12.71, 4.23) * mm});
            skLineSegment(sketch, "E3775", {"start": v(-12.71, 4.23) * mm, "end": v(-12.63, 4.05) * mm});
            skLineSegment(sketch, "E3776", {"start": v(-12.63, 4.05) * mm, "end": v(-12.6, 3.87) * mm});
            skLineSegment(sketch, "E3777", {"start": v(-12.6, 3.87) * mm, "end": v(-12.63, 3.75) * mm});
            skLineSegment(sketch, "E3778", {"start": v(-12.63, 3.75) * mm, "end": v(-13.11, 3.41) * mm});
            skLineSegment(sketch, "E3779", {"start": v(-13.11, 3.41) * mm, "end": v(-13.24, 3.42) * mm});
            skLineSegment(sketch, "E3780", {"start": v(-13.24, 3.42) * mm, "end": v(-13.4, 3.52) * mm});
            skLineSegment(sketch, "E3781", {"start": v(-13.4, 3.52) * mm, "end": v(-13.54, 3.67) * mm});
            skLineSegment(sketch, "E3782", {"start": v(-13.54, 3.67) * mm, "end": v(-13.62, 3.73) * mm});
            skLineSegment(sketch, "E3783", {"start": v(-13.62, 3.73) * mm, "end": v(-13.76, 3.82) * mm});
            skLineSegment(sketch, "E3784", {"start": v(-13.76, 3.82) * mm, "end": v(-13.98, 3.93) * mm});
            skLineSegment(sketch, "E3785", {"start": v(-13.98, 3.93) * mm, "end": v(-14.27, 4.03) * mm});
            skLineSegment(sketch, "E3786", {"start": v(-14.27, 4.03) * mm, "end": v(-14.65, 4.1) * mm});
            skLineSegment(sketch, "E3787", {"start": v(-14.65, 4.1) * mm, "end": v(-14.75, 4.11) * mm});
            skLineSegment(sketch, "E3788", {"start": v(-14.75, 4.11) * mm, "end": v(-14.9, 3.98) * mm});
            skLineSegment(sketch, "E3789", {"start": v(-14.9, 3.98) * mm, "end": v(-15, 3.83) * mm});
            skLineSegment(sketch, "E3790", {"start": v(-15, 3.83) * mm, "end": v(-14.99, 3.72) * mm});
            skLineSegment(sketch, "E3791", {"start": v(-14.99, 3.72) * mm, "end": v(-14.86, 3.36) * mm});
            skLineSegment(sketch, "E3792", {"start": v(-14.86, 3.36) * mm, "end": v(-14.73, 3.08) * mm});
            skLineSegment(sketch, "E3793", {"start": v(-14.73, 3.08) * mm, "end": v(-14.6, 2.88) * mm});
            skLineSegment(sketch, "E3794", {"start": v(-14.6, 2.88) * mm, "end": v(-14.5, 2.74) * mm});
            skLineSegment(sketch, "E3795", {"start": v(-14.5, 2.74) * mm, "end": v(-14.42, 2.67) * mm});
            skLineSegment(sketch, "E3796", {"start": v(-14.42, 2.67) * mm, "end": v(-14.25, 2.55) * mm});
            skLineSegment(sketch, "E3797", {"start": v(-14.25, 2.55) * mm, "end": v(-14.14, 2.4) * mm});
            skLineSegment(sketch, "E3798", {"start": v(-14.14, 2.4) * mm, "end": v(-14.11, 2.28) * mm});
            skLineSegment(sketch, "E3799", {"start": v(-14.11, 2.28) * mm, "end": v(-14.39, 1.76) * mm});
            skLineSegment(sketch, "E3800", {"start": v(-14.39, 1.76) * mm, "end": v(-14.5, 1.7) * mm});
            skLineSegment(sketch, "E3801", {"start": v(-14.5, 1.7) * mm, "end": v(-14.69, 1.72) * mm});
            skLineSegment(sketch, "E3802", {"start": v(-14.69, 1.72) * mm, "end": v(-14.88, 1.79) * mm});
            skLineSegment(sketch, "E3803", {"start": v(-14.88, 1.79) * mm, "end": v(-14.98, 1.8) * mm});
            skLineSegment(sketch, "E3804", {"start": v(-14.98, 1.8) * mm, "end": v(-15.15, 1.82) * mm});
            skLineSegment(sketch, "E3805", {"start": v(-15.15, 1.82) * mm, "end": v(-15.4, 1.81) * mm});
            skLineSegment(sketch, "E3806", {"start": v(-15.4, 1.81) * mm, "end": v(-15.7, 1.76) * mm});
            skLineSegment(sketch, "E3807", {"start": v(-15.7, 1.76) * mm, "end": v(-16.07, 1.66) * mm});
            skLineSegment(sketch, "E3808", {"start": v(-16.07, 1.66) * mm, "end": v(-16.16, 1.62) * mm});
            skCircle(sketch, "E3809", {"center": v(0, 0) * mm, "radius": 23 * mm});
            skCircle(sketch, "E3810", {"center": v(-10.4, 0) * mm, "radius": 1.5 * mm});
            skCircle(sketch, "E3811", {"center": v(0, 0) * mm, "radius": 19.5 * mm});
            skSolve(sketch);
        }
        {
            var Q0;
            Q0=qCreatedBy(makeId("Top.planeOp"),FACE);
            var sketch = newSketch(context, id + "F2", { "sketchPlane" : qUnion([Q0])});
            skCircle(sketch, "E3812", {"center": v(0, 0) * mm, "radius": 17.9 * mm});
            skCircle(sketch, "E3813", {"center": v(0, 0) * mm, "radius": 18.75 * mm});
            skCircle(sketch, "E3814", {"center": v(0, 0) * mm, "radius": 31.75 * mm});
            skCircle(sketch, "E3815", {"center": v(0, 0) * mm, "radius": 21.05 * mm});
            skCircle(sketch, "E3816", {"center": v(0, 0) * mm, "radius": 23 * mm});
            skCircle(sketch, "E3817", {"center": v(-10.4, 0) * mm, "radius": 6.5 * mm});
            skSolve(sketch);
        }
        {
            var Q0;
            Q0=makeQuery(id+"F1.imprint","IMPRINT",FACE,{"disambiguationData":[TD([[makeQuery(id+"F1.imprint","IMPRINT",EDGE,{"derivedFrom":sQuery(id+"F1.wireOp",EDGE,"E3536")}),1.0]])]});
            extrude(context, id + "F3", {"entities" : qUnion([Q0]), "depth" : 30 * mm, "offsetDistance" : 25 * mm});
        }
        {
            var Q0;
            Q0=makeQuery(id+"F1.imprint","IMPRINT",FACE,{"disambiguationData":[TD([[makeQuery(id+"F1.imprint","IMPRINT",EDGE,{"derivedFrom":sQuery(id+"F1.wireOp",EDGE,"E3536")}),1.0]])]});
            extrude(context, id + "F4", {"entities" : qUnion([Q0]), "operationType" : NewBodyOperationType.REMOVE, "depth" : 15 * mm, "offsetDistance" : 25 * mm});
        }
        {
            var Q0;
            Q0=makeQuery(id+"F2.imprint","IMPRINT",FACE,{"disambiguationData":[TD([[makeQuery(id+"F2.imprint","IMPRINT",EDGE,{"derivedFrom":sQuery(id+"F2.wireOp",EDGE,"E3817")}),1.0]])]});
            extrude(context, id + "F5", {"entities" : qUnion([Q0]), "operationType" : NewBodyOperationType.ADD, "depth" : 16 * mm, "offsetDistance" : 25 * mm});
        }
        {
            var Q0;
            Q0=makeQuery(id+"F2.imprint","IMPRINT",FACE,{"disambiguationData":[TD([[makeQuery(id+"F2.imprint","IMPRINT",EDGE,{"derivedFrom":sQuery(id+"F2.wireOp",EDGE,"E3817")}),1.0]])]});
            extrude(context, id + "F6", {"entities" : qUnion([Q0]), "operationType" : NewBodyOperationType.REMOVE, "depth" : 14 * mm, "offsetDistance" : 25 * mm});
        }
        {
            var Q0;
            Q0=makeQuery(id+"F0.imprint","IMPRINT",FACE,{"disambiguationData":[TD([[makeQuery(id+"F0.imprint","IMPRINT",EDGE,{"derivedFrom":sQuery(id+"F0.wireOp",EDGE,"E1640")}),1.0]])]});
            extrude(context, id + "F7", {"entities" : qUnion([Q0]), "operationType" : NewBodyOperationType.ADD, "depth" : 15 * mm, "offsetDistance" : 25 * mm});
        }
        {
            var Q0;
            Q0=makeQuery(id+"F5.opExtrude","SWEPT_FACE",FACE,{"disambiguationData":[OSD([sQuery(id+"F2.wireOp",EDGE,"E3817")])]});
            chamfer(context, id + "F8", {"entities" : qUnion([Q0]), "chamferType" : ChamferType.TWO_OFFSETS, "width1" : 2.2 * mm, "oppositeDirection" : false, "width2" : .8 * mm, "tangentPropagation" : true});
        }
        {
            var Q0;
            Q0=makeQuery(id+"F0.imprint","IMPRINT",FACE,{"disambiguationData":[TD([[makeQuery(id+"F0.imprint","IMPRINT",EDGE,{"derivedFrom":sQuery(id+"F0.wireOp",EDGE,"E1935")}),1.0]])]});
            extrude(context, id + "F9", {"entities" : qUnion([Q0]), "operationType" : NewBodyOperationType.ADD, "depth" : 33 * mm, "offsetDistance" : 25 * mm, "hasSecondDirection" : true, "secondDirectionOppositeDirection" : true, "secondDirectionDepth" : 3 * mm});
        }
        {
            var Q0;
            Q0=makeQuery(id+"F0.imprint","IMPRINT",FACE,{"disambiguationData":[TD([[makeQuery(id+"F0.imprint","IMPRINT",EDGE,{"derivedFrom":sQuery(id+"F0.wireOp",EDGE,"E0")}),1.0]])]});
            extrude(context, id + "F10", {"entities" : qUnion([Q0]), "depth" : 14 * mm, "offsetDistance" : 25 * mm});
        }
        {
            var Q0;
            Q0=makeQuery(id+"F0.imprint","IMPRINT",FACE,{"disambiguationData":[TD([[makeQuery(id+"F0.imprint","IMPRINT",EDGE,{"derivedFrom":sQuery(id+"F0.wireOp",EDGE,"E0")}),-1.0]])]});
            var Q1;
            Q1=makeQuery(id+"F0.imprint","IMPRINT",FACE,{"disambiguationData":[TD([[makeQuery(id+"F0.imprint","IMPRINT",EDGE,{"derivedFrom":sQuery(id+"F0.wireOp",EDGE,"E0")}),1.0]])]});
            var Q2;
            Q2=makeQuery(id+"F0.imprint","IMPRINT",FACE,{"disambiguationData":[TD([[makeQuery(id+"F0.imprint","IMPRINT",EDGE,{"derivedFrom":sQuery(id+"F0.wireOp",EDGE,"E1640")}),1.0]])]});
            var Q3;
            Q3=makeQuery(id+"F0.imprint","IMPRINT",FACE,{"disambiguationData":[TD([[makeQuery(id+"F0.imprint","IMPRINT",EDGE,{"derivedFrom":sQuery(id+"F0.wireOp",EDGE,"E1935")}),1.0]])]});
            extrude(context, id + "F11", {"entities" : qUnion([Q0, Q1, Q2, Q3]), "operationType" : NewBodyOperationType.ADD, "oppositeDirection" : true, "depth" : 6 * mm, "offsetDistance" : 25 * mm});
        }
        {
            var Q0;
            Q0=makeQuery(id+"F0.imprint","IMPRINT",FACE,{"disambiguationData":[TD([[makeQuery(id+"F0.imprint","IMPRINT",EDGE,{"derivedFrom":sQuery(id+"F0.wireOp",EDGE,"E0")}),-1.0]])]});
            var Q1;
            Q1=makeQuery(id+"F0.imprint","IMPRINT",FACE,{"disambiguationData":[TD([[makeQuery(id+"F0.imprint","IMPRINT",EDGE,{"derivedFrom":sQuery(id+"F0.wireOp",EDGE,"E1640")}),1.0]])]});
            var Q2;
            Q2=makeQuery(id+"F0.imprint","IMPRINT",FACE,{"disambiguationData":[TD([[makeQuery(id+"F0.imprint","IMPRINT",EDGE,{"derivedFrom":sQuery(id+"F0.wireOp",EDGE,"E1935")}),1.0]])]});
            extrude(context, id + "F12", {"entities" : qUnion([Q0, Q1, Q2]), "operationType" : NewBodyOperationType.REMOVE, "oppositeDirection" : true, "depth" : 3 * mm, "offsetDistance" : 25 * mm});
        }
        {
            var Q0;
            Q0=makeQuery(id+"F1.imprint","IMPRINT",FACE,{"disambiguationData":[TD([[makeQuery(id+"F1.imprint","IMPRINT",EDGE,{"derivedFrom":sQuery(id+"F1.wireOp",EDGE,"E1937")}),-1.0]])]});
            var Q1;
            Q1=makeQuery(id+"F1.imprint","IMPRINT",FACE,{"disambiguationData":[TD([[makeQuery(id+"F1.imprint","IMPRINT",EDGE,{"derivedFrom":sQuery(id+"F1.wireOp",EDGE,"E3536")}),1.0]])]});
            var Q2;
            Q2=makeQuery(id+"F1.imprint","IMPRINT",FACE,{"disambiguationData":[TD([[makeQuery(id+"F1.imprint","IMPRINT",EDGE,{"derivedFrom":sQuery(id+"F1.wireOp",EDGE,"E3810")}),1.0]])]});
            var Q3;
            Q3=makeQuery(id+"F1.imprint","IMPRINT",FACE,{"disambiguationData":[TD([[makeQuery(id+"F1.imprint","IMPRINT",EDGE,{"derivedFrom":sQuery(id+"F1.wireOp",EDGE,"E1937")}),1.0]])]});
            extrude(context, id + "F13", {"entities" : qUnion([Q0, Q1, Q2, Q3]), "depth" : 36 * mm, "offsetDistance" : 25 * mm});
        }
        {
            var Q0;
            Q0=makeQuery(id+"F1.imprint","IMPRINT",FACE,{"disambiguationData":[TD([[makeQuery(id+"F1.imprint","IMPRINT",EDGE,{"derivedFrom":sQuery(id+"F1.wireOp",EDGE,"E1937")}),-1.0]])]});
            var Q1;
            Q1=makeQuery(id+"F1.imprint","IMPRINT",FACE,{"disambiguationData":[TD([[makeQuery(id+"F1.imprint","IMPRINT",EDGE,{"derivedFrom":sQuery(id+"F1.wireOp",EDGE,"E3810")}),1.0]])]});
            var Q2;
            Q2=makeQuery(id+"F1.imprint","IMPRINT",FACE,{"disambiguationData":[TD([[makeQuery(id+"F1.imprint","IMPRINT",EDGE,{"derivedFrom":sQuery(id+"F1.wireOp",EDGE,"E3536")}),1.0]])]});
            extrude(context, id + "F14", {"entities" : qUnion([Q0, Q1, Q2]), "operationType" : NewBodyOperationType.REMOVE, "depth" : 33 * mm, "offsetDistance" : 25 * mm});
        }
        {
            var Q0;
            Q0=makeQuery(id+"F1.imprint","IMPRINT",FACE,{"disambiguationData":[TD([[makeQuery(id+"F1.imprint","IMPRINT",EDGE,{"derivedFrom":sQuery(id+"F1.wireOp",EDGE,"E1937")}),1.0]])]});
            extrude(context, id + "F15", {"entities" : qUnion([Q0]), "operationType" : NewBodyOperationType.REMOVE, "depth" : 16 * mm, "offsetDistance" : 25 * mm});
        }
        {
            var Q0;
            Q0=makeQuery(id+"F11.opExtrude","CAP_FACE",FACE,{"disambiguationData":[OSD([sQuery(id+"F0.wireOp",EDGE,"E1934")])],"isStart":false});
            var sketch = newSketch(context, id + "F16", { "sketchPlane" : qUnion([Q0])});
            skLineSegment(sketch, "E3818.bottom", {"start": v(13, 14) * mm, "end": v(-13, 14) * mm});
            skLineSegment(sketch, "E3818.top", {"start": v(13, -14) * mm, "end": v(-13, -14) * mm});
            skLineSegment(sketch, "E3818.left", {"start": v(14, 13) * mm, "end": v(14, -13) * mm});
            skLineSegment(sketch, "E3818.right", {"start": v(-14, 13) * mm, "end": v(-14, -13) * mm});
            skPoint(sketch, "E3818.middle", {"position": v(0, 0) * mm});
            skLineSegment(sketch, "E3819", {"start": v(0, 0) * mm, "end": v(13.79, 13.79) * mm});
            skPoint(sketch, "E3820.visualSharp", {"position": v(-14, 14) * mm});
            skArc(sketch, "E3820.filletArc", {"start": v(-13, 14) * mm, "mid": v(-13.7, 13.7) * mm, "end": v(-14, 13) * mm});
            skPoint(sketch, "E3821.visualSharp", {"position": v(-14, -14) * mm});
            skArc(sketch, "E3821.filletArc", {"start": v(-14, -13) * mm, "mid": v(-13.7, -13.7) * mm, "end": v(-13, -14) * mm});
            skPoint(sketch, "E3822.visualSharp", {"position": v(14, -14) * mm});
            skArc(sketch, "E3822.filletArc", {"start": v(13, -14) * mm, "mid": v(13.7, -13.7) * mm, "end": v(14, -13) * mm});
            skPoint(sketch, "E3823.visualSharp", {"position": v(14, 14) * mm});
            skArc(sketch, "E3823.filletArc", {"start": v(14, 13) * mm, "mid": v(13.7, 13.7) * mm, "end": v(13, 14) * mm});
            skCircle(sketch, "E3824", {"center": v(0, 0) * mm, "radius": 6 * mm});
            skSolve(sketch);
        }
        {
            var Q0;
            {var subQ1=sQuery(id+"F16.wireOp",EDGE,"E3818.bottom");Q0=makeQuery(id+"F16.imprint","IMPRINT",FACE,{"disambiguationData":[TD([[makeQuery(id+"F16.imprint","IMPRINT",EDGE,{"derivedFrom":subQ1}),1.0]])]});}
            extrude(context, id + "F17", {"entities" : qUnion([Q0]), "operationType" : NewBodyOperationType.ADD, "depth" : 3 * mm, "offsetDistance" : 25 * mm});
        }
        {
            var Q0;
            Q0=makeQuery(id+"F13.opExtrude","CAP_FACE",FACE,{"disambiguationData":[OSD([sQuery(id+"F1.wireOp",EDGE,"E3811")])],"isStart":false});
            var sketch = newSketch(context, id + "F18", { "sketchPlane" : qUnion([Q0])});
            skCircle(sketch, "E3825", {"center": v(0, 0) * mm, "radius": 16.5 * mm});
            skSolve(sketch);
        }
        {
            var Q0;
            Q0=makeQuery(id+"F18.imprint","IMPRINT",FACE,{"disambiguationData":[TD([[makeQuery(id+"F18.imprint","IMPRINT",EDGE,{"derivedFrom":sQuery(id+"F18.wireOp",EDGE,"E3825")}),1.0]])]});
            extrude(context, id + "F19", {"entities" : qUnion([Q0]), "operationType" : NewBodyOperationType.ADD, "depth" : 6 * mm, "offsetDistance" : 25 * mm});
        }
        {
            var Q0;
            Q0=qCreatedBy(makeId("Front.planeOp"),FACE);
            var sketch = newSketch(context, id + "F20", { "sketchPlane" : qUnion([Q0])});
            skLineSegment(sketch, "E3826", {"start": v(16.5, 42) * mm, "end": v(23, 42) * mm});
            skLineSegment(sketch, "E3827", {"start": v(23, 42) * mm, "end": v(23, -9) * mm});
            skLineSegment(sketch, "E3828", {"start": v(14, -9) * mm, "end": v(7.5, -9) * mm});
            skLineSegment(sketch, "E3829", {"start": v(14, -9) * mm, "end": v(14, -6) * mm});
            skLineSegment(sketch, "E3830", {"start": v(14, -6) * mm, "end": v(19.5, -6) * mm});
            skLineSegment(sketch, "E3831", {"start": v(19.5, -6) * mm, "end": v(19.5, 36) * mm});
            skLineSegment(sketch, "E3832", {"start": v(19.5, 36) * mm, "end": v(16.5, 36) * mm});
            skLineSegment(sketch, "E3833", {"start": v(16.5, 36) * mm, "end": v(16.5, 42) * mm});
            skLineSegment(sketch, "E3834", {"start": v(7.5, -9) * mm, "end": v(7.5, -13.2) * mm});
            skLineSegment(sketch, "E3835", {"start": v(7.5, -13.2) * mm, "end": v(23, -13.2) * mm});
            skLineSegment(sketch, "E3836", {"start": v(23, -13.2) * mm, "end": v(23, -9) * mm});
            skSolve(sketch);
        }
        {
            var Q0;
            Q0 = qSketchRegion(id + "F20", true);
            var Q1;
            Q1=sQuery(id+"F2.wireOp",EDGE,"E3814");
            revolve(context, id + "F21", {"entities" : qUnion([Q0]), "axis" : qUnion([Q1]), "revolveType" : RevolveType.ONE_DIRECTION, "angle" : 180 * degree});
        }
        {
            var Q0;
            {var subQ1=sQuery(id+"F16.wireOp",EDGE,"E3818.bottom");Q0=makeQuery(id+"F16.imprint","IMPRINT",FACE,{"disambiguationData":[TD([[makeQuery(id+"F16.imprint","IMPRINT",EDGE,{"derivedFrom":subQ1}),1.0]])]});}
            extrude(context, id + "F22", {"entities" : qUnion([Q0]), "operationType" : NewBodyOperationType.REMOVE, "depth" : 3 * mm, "offsetDistance" : 25 * mm});
        }
        {
            var Q0;
            Q0=makeQuery(id+"F16.imprint","IMPRINT",FACE,{"disambiguationData":[TD([[makeQuery(id+"F16.imprint","IMPRINT",EDGE,{"derivedFrom":sQuery(id+"F16.wireOp",EDGE,"E3824")}),1.0]])]});
            extrude(context, id + "F23", {"entities" : qUnion([Q0]), "operationType" : NewBodyOperationType.REMOVE, "oppositeDirection" : true, "depth" : 3 * mm, "offsetDistance" : 25 * mm});
        }
    });
